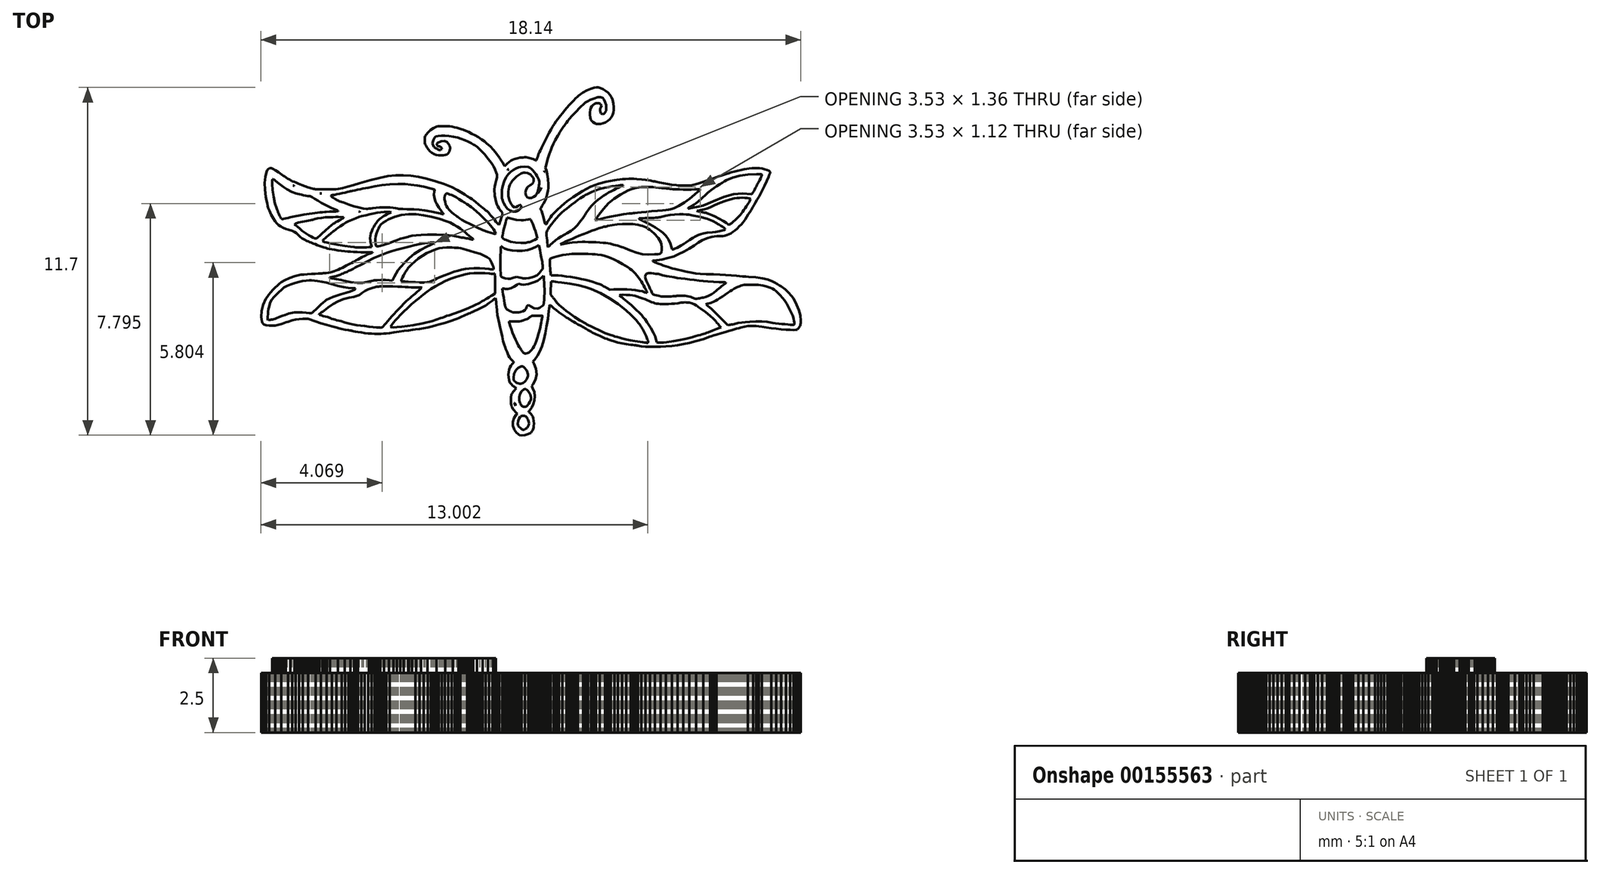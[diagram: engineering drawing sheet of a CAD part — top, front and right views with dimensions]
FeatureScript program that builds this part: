
annotation { "Feature Type Name" : "Feature", "Feature Type Description" : "" }
export const myFeature = defineFeature(function(context is Context, id is Id, definition is map)
    precondition{}
    {
        {
            var Q0;
            Q0=qCreatedBy(makeId("Top.planeOp"),FACE);
            var sketch = newSketch(context, id + "F0", { "sketchPlane" : qUnion([Q0])});
            skLineSegment(sketch, "E0", {"start": v(-0.39, -5.84) * mm, "end": v(-0.43, -5.8) * mm});
            skLineSegment(sketch, "E1", {"start": v(-0.43, -5.8) * mm, "end": v(-0.48, -5.76) * mm});
            skLineSegment(sketch, "E2", {"start": v(-0.48, -5.76) * mm, "end": v(-0.52, -5.71) * mm});
            skLineSegment(sketch, "E3", {"start": v(-0.52, -5.71) * mm, "end": v(-0.56, -5.66) * mm});
            skLineSegment(sketch, "E4", {"start": v(-0.56, -5.66) * mm, "end": v(-0.6, -5.53) * mm});
            skLineSegment(sketch, "E5", {"start": v(-0.6, -5.53) * mm, "end": v(-0.6, -5.4) * mm});
            skLineSegment(sketch, "E6", {"start": v(-0.6, -5.4) * mm, "end": v(-0.57, -5.28) * mm});
            skLineSegment(sketch, "E7", {"start": v(-0.57, -5.28) * mm, "end": v(-0.5, -5.18) * mm});
            skLineSegment(sketch, "E8", {"start": v(-0.5, -5.18) * mm, "end": v(-0.45, -5.13) * mm});
            skLineSegment(sketch, "E9", {"start": v(-0.45, -5.13) * mm, "end": v(-0.5, -5.07) * mm});
            skLineSegment(sketch, "E10", {"start": v(-0.5, -5.07) * mm, "end": v(-0.56, -5.02) * mm});
            skLineSegment(sketch, "E11", {"start": v(-0.56, -5.02) * mm, "end": v(-0.6, -4.96) * mm});
            skLineSegment(sketch, "E12", {"start": v(-0.6, -4.96) * mm, "end": v(-0.63, -4.9) * mm});
            skLineSegment(sketch, "E13", {"start": v(-0.63, -4.9) * mm, "end": v(-0.65, -4.86) * mm});
            skLineSegment(sketch, "E14", {"start": v(-0.65, -4.86) * mm, "end": v(-0.66, -4.83) * mm});
            skLineSegment(sketch, "E15", {"start": v(-0.66, -4.83) * mm, "end": v(-0.66, -4.79) * mm});
            skLineSegment(sketch, "E16", {"start": v(-0.66, -4.79) * mm, "end": v(-0.66, -4.73) * mm});
            skLineSegment(sketch, "E17", {"start": v(-0.66, -4.73) * mm, "end": v(-0.67, -4.66) * mm});
            skLineSegment(sketch, "E18", {"start": v(-0.67, -4.66) * mm, "end": v(-0.66, -4.61) * mm});
            skLineSegment(sketch, "E19", {"start": v(-0.66, -4.61) * mm, "end": v(-0.66, -4.57) * mm});
            skLineSegment(sketch, "E20", {"start": v(-0.66, -4.57) * mm, "end": v(-0.66, -4.54) * mm});
            skLineSegment(sketch, "E21", {"start": v(-0.66, -4.54) * mm, "end": v(-0.66, -4.52) * mm});
            skLineSegment(sketch, "E22", {"start": v(-0.66, -4.52) * mm, "end": v(-0.66, -4.5) * mm});
            skLineSegment(sketch, "E23", {"start": v(-0.66, -4.5) * mm, "end": v(-0.65, -4.48) * mm});
            skLineSegment(sketch, "E24", {"start": v(-0.65, -4.48) * mm, "end": v(-0.64, -4.47) * mm});
            skLineSegment(sketch, "E25", {"start": v(-0.64, -4.47) * mm, "end": v(-0.63, -4.45) * mm});
            skLineSegment(sketch, "E26", {"start": v(-0.63, -4.45) * mm, "end": v(-0.62, -4.42) * mm});
            skLineSegment(sketch, "E27", {"start": v(-0.62, -4.42) * mm, "end": v(-0.6, -4.39) * mm});
            skLineSegment(sketch, "E28", {"start": v(-0.6, -4.39) * mm, "end": v(-0.57, -4.36) * mm});
            skLineSegment(sketch, "E29", {"start": v(-0.57, -4.36) * mm, "end": v(-0.55, -4.33) * mm});
            skLineSegment(sketch, "E30", {"start": v(-0.55, -4.33) * mm, "end": v(-0.53, -4.3) * mm});
            skLineSegment(sketch, "E31", {"start": v(-0.53, -4.3) * mm, "end": v(-0.5, -4.3) * mm});
            skLineSegment(sketch, "E32", {"start": v(-0.5, -4.3) * mm, "end": v(-0.5, -4.28) * mm});
            skLineSegment(sketch, "E33", {"start": v(-0.5, -4.28) * mm, "end": v(-0.5, -4.27) * mm});
            skLineSegment(sketch, "E34", {"start": v(-0.5, -4.27) * mm, "end": v(-0.5, -4.26) * mm});
            skLineSegment(sketch, "E35", {"start": v(-0.5, -4.26) * mm, "end": v(-0.53, -4.24) * mm});
            skLineSegment(sketch, "E36", {"start": v(-0.53, -4.24) * mm, "end": v(-0.55, -4.22) * mm});
            skLineSegment(sketch, "E37", {"start": v(-0.55, -4.22) * mm, "end": v(-0.58, -4.2) * mm});
            skLineSegment(sketch, "E38", {"start": v(-0.58, -4.2) * mm, "end": v(-0.61, -4.17) * mm});
            skLineSegment(sketch, "E39", {"start": v(-0.61, -4.17) * mm, "end": v(-0.64, -4.15) * mm});
            skLineSegment(sketch, "E40", {"start": v(-0.64, -4.15) * mm, "end": v(-0.68, -4.1) * mm});
            skLineSegment(sketch, "E41", {"start": v(-0.68, -4.1) * mm, "end": v(-0.7, -4.08) * mm});
            skLineSegment(sketch, "E42", {"start": v(-0.7, -4.08) * mm, "end": v(-0.72, -4.04) * mm});
            skLineSegment(sketch, "E43", {"start": v(-0.72, -4.04) * mm, "end": v(-0.74, -4) * mm});
            skLineSegment(sketch, "E44", {"start": v(-0.74, -4) * mm, "end": v(-0.76, -3.81) * mm});
            skLineSegment(sketch, "E45", {"start": v(-0.76, -3.81) * mm, "end": v(-0.73, -3.65) * mm});
            skLineSegment(sketch, "E46", {"start": v(-0.73, -3.65) * mm, "end": v(-0.7, -3.58) * mm});
            skLineSegment(sketch, "E47", {"start": v(-0.7, -3.58) * mm, "end": v(-0.67, -3.51) * mm});
            skLineSegment(sketch, "E48", {"start": v(-0.67, -3.51) * mm, "end": v(-0.63, -3.46) * mm});
            skLineSegment(sketch, "E49", {"start": v(-0.63, -3.46) * mm, "end": v(-0.6, -3.43) * mm});
            skLineSegment(sketch, "E50", {"start": v(-0.6, -3.43) * mm, "end": v(-0.58, -3.4) * mm});
            skLineSegment(sketch, "E51", {"start": v(-0.58, -3.4) * mm, "end": v(-0.57, -3.4) * mm});
            skLineSegment(sketch, "E52", {"start": v(-0.57, -3.4) * mm, "end": v(-0.59, -3.37) * mm});
            skLineSegment(sketch, "E53", {"start": v(-0.59, -3.37) * mm, "end": v(-0.62, -3.34) * mm});
            skLineSegment(sketch, "E54", {"start": v(-0.62, -3.34) * mm, "end": v(-0.67, -3.3) * mm});
            skLineSegment(sketch, "E55", {"start": v(-0.67, -3.3) * mm, "end": v(-0.71, -3.23) * mm});
            skLineSegment(sketch, "E56", {"start": v(-0.71, -3.23) * mm, "end": v(-0.75, -3.16) * mm});
            skLineSegment(sketch, "E57", {"start": v(-0.75, -3.16) * mm, "end": v(-0.79, -3.1) * mm});
            skLineSegment(sketch, "E58", {"start": v(-0.79, -3.1) * mm, "end": v(-0.8, -3.05) * mm});
            skLineSegment(sketch, "E59", {"start": v(-0.8, -3.05) * mm, "end": v(-0.82, -3) * mm});
            skLineSegment(sketch, "E60", {"start": v(-0.82, -3) * mm, "end": v(-0.84, -2.95) * mm});
            skLineSegment(sketch, "E61", {"start": v(-0.84, -2.95) * mm, "end": v(-0.86, -2.9) * mm});
            skLineSegment(sketch, "E62", {"start": v(-0.86, -2.9) * mm, "end": v(-0.9, -2.8) * mm});
            skLineSegment(sketch, "E63", {"start": v(-0.9, -2.8) * mm, "end": v(-0.93, -2.68) * mm});
            skLineSegment(sketch, "E64", {"start": v(-0.93, -2.68) * mm, "end": v(-0.96, -2.54) * mm});
            skLineSegment(sketch, "E65", {"start": v(-0.96, -2.54) * mm, "end": v(-1, -2.36) * mm});
            skLineSegment(sketch, "E66", {"start": v(-1, -2.36) * mm, "end": v(-1.03, -2.21) * mm});
            skLineSegment(sketch, "E67", {"start": v(-1.03, -2.21) * mm, "end": v(-1.06, -2.08) * mm});
            skLineSegment(sketch, "E68", {"start": v(-1.06, -2.08) * mm, "end": v(-1.12, -1.8) * mm});
            skLineSegment(sketch, "E69", {"start": v(-1.12, -1.8) * mm, "end": v(-1.15, -1.51) * mm});
            skLineSegment(sketch, "E70", {"start": v(-1.15, -1.51) * mm, "end": v(-1.16, -1.44) * mm});
            skLineSegment(sketch, "E71", {"start": v(-1.16, -1.44) * mm, "end": v(-1.17, -1.37) * mm});
            skLineSegment(sketch, "E72", {"start": v(-1.17, -1.37) * mm, "end": v(-1.17, -1.31) * mm});
            skLineSegment(sketch, "E73", {"start": v(-1.17, -1.31) * mm, "end": v(-1.18, -1.28) * mm});
            skLineSegment(sketch, "E74", {"start": v(-1.18, -1.28) * mm, "end": v(-1.18, -1.23) * mm});
            skLineSegment(sketch, "E75", {"start": v(-1.18, -1.23) * mm, "end": v(-1.22, -1.26) * mm});
            skLineSegment(sketch, "E76", {"start": v(-1.22, -1.26) * mm, "end": v(-1.3, -1.32) * mm});
            skLineSegment(sketch, "E77", {"start": v(-1.3, -1.32) * mm, "end": v(-1.4, -1.4) * mm});
            skLineSegment(sketch, "E78", {"start": v(-1.4, -1.4) * mm, "end": v(-1.52, -1.48) * mm});
            skLineSegment(sketch, "E79", {"start": v(-1.52, -1.48) * mm, "end": v(-1.62, -1.54) * mm});
            skLineSegment(sketch, "E80", {"start": v(-1.62, -1.54) * mm, "end": v(-1.67, -1.57) * mm});
            skLineSegment(sketch, "E81", {"start": v(-1.67, -1.57) * mm, "end": v(-1.72, -1.6) * mm});
            skLineSegment(sketch, "E82", {"start": v(-1.72, -1.6) * mm, "end": v(-1.77, -1.62) * mm});
            skLineSegment(sketch, "E83", {"start": v(-1.77, -1.62) * mm, "end": v(-1.82, -1.64) * mm});
            skLineSegment(sketch, "E84", {"start": v(-1.82, -1.64) * mm, "end": v(-1.87, -1.66) * mm});
            skLineSegment(sketch, "E85", {"start": v(-1.87, -1.66) * mm, "end": v(-1.91, -1.68) * mm});
            skLineSegment(sketch, "E86", {"start": v(-1.91, -1.68) * mm, "end": v(-1.96, -1.7) * mm});
            skLineSegment(sketch, "E87", {"start": v(-1.96, -1.7) * mm, "end": v(-2, -1.72) * mm});
            skLineSegment(sketch, "E88", {"start": v(-2, -1.72) * mm, "end": v(-2.04, -1.74) * mm});
            skLineSegment(sketch, "E89", {"start": v(-2.04, -1.74) * mm, "end": v(-2.09, -1.76) * mm});
            skLineSegment(sketch, "E90", {"start": v(-2.09, -1.76) * mm, "end": v(-2.14, -1.79) * mm});
            skLineSegment(sketch, "E91", {"start": v(-2.14, -1.79) * mm, "end": v(-2.2, -1.8) * mm});
            skLineSegment(sketch, "E92", {"start": v(-2.2, -1.8) * mm, "end": v(-2.26, -1.83) * mm});
            skLineSegment(sketch, "E93", {"start": v(-2.26, -1.83) * mm, "end": v(-2.32, -1.86) * mm});
            skLineSegment(sketch, "E94", {"start": v(-2.32, -1.86) * mm, "end": v(-2.37, -1.88) * mm});
            skLineSegment(sketch, "E95", {"start": v(-2.37, -1.88) * mm, "end": v(-2.42, -1.9) * mm});
            skLineSegment(sketch, "E96", {"start": v(-2.42, -1.9) * mm, "end": v(-2.48, -1.93) * mm});
            skLineSegment(sketch, "E97", {"start": v(-2.48, -1.93) * mm, "end": v(-2.56, -1.96) * mm});
            skLineSegment(sketch, "E98", {"start": v(-2.56, -1.96) * mm, "end": v(-2.67, -2) * mm});
            skLineSegment(sketch, "E99", {"start": v(-2.67, -2) * mm, "end": v(-2.78, -2.03) * mm});
            skLineSegment(sketch, "E100", {"start": v(-2.78, -2.03) * mm, "end": v(-2.89, -2.07) * mm});
            skLineSegment(sketch, "E101", {"start": v(-2.89, -2.07) * mm, "end": v(-3, -2.1) * mm});
            skLineSegment(sketch, "E102", {"start": v(-3, -2.1) * mm, "end": v(-3.1, -2.13) * mm});
            skLineSegment(sketch, "E103", {"start": v(-3.1, -2.13) * mm, "end": v(-3.18, -2.15) * mm});
            skLineSegment(sketch, "E104", {"start": v(-3.18, -2.15) * mm, "end": v(-3.22, -2.16) * mm});
            skLineSegment(sketch, "E105", {"start": v(-3.22, -2.16) * mm, "end": v(-3.27, -2.17) * mm});
            skLineSegment(sketch, "E106", {"start": v(-3.27, -2.17) * mm, "end": v(-3.31, -2.18) * mm});
            skLineSegment(sketch, "E107", {"start": v(-3.31, -2.18) * mm, "end": v(-3.35, -2.2) * mm});
            skLineSegment(sketch, "E108", {"start": v(-3.35, -2.2) * mm, "end": v(-3.46, -2.22) * mm});
            skLineSegment(sketch, "E109", {"start": v(-3.46, -2.22) * mm, "end": v(-3.6, -2.25) * mm});
            skLineSegment(sketch, "E110", {"start": v(-3.6, -2.25) * mm, "end": v(-3.74, -2.27) * mm});
            skLineSegment(sketch, "E111", {"start": v(-3.74, -2.27) * mm, "end": v(-3.88, -2.3) * mm});
            skLineSegment(sketch, "E112", {"start": v(-3.88, -2.3) * mm, "end": v(-3.97, -2.3) * mm});
            skLineSegment(sketch, "E113", {"start": v(-3.97, -2.3) * mm, "end": v(-4.1, -2.32) * mm});
            skLineSegment(sketch, "E114", {"start": v(-4.1, -2.32) * mm, "end": v(-4.26, -2.34) * mm});
            skLineSegment(sketch, "E115", {"start": v(-4.26, -2.34) * mm, "end": v(-4.43, -2.37) * mm});
            skLineSegment(sketch, "E116", {"start": v(-4.43, -2.37) * mm, "end": v(-4.6, -2.4) * mm});
            skLineSegment(sketch, "E117", {"start": v(-4.6, -2.4) * mm, "end": v(-4.74, -2.4) * mm});
            skLineSegment(sketch, "E118", {"start": v(-4.74, -2.4) * mm, "end": v(-4.86, -2.42) * mm});
            skLineSegment(sketch, "E119", {"start": v(-4.86, -2.42) * mm, "end": v(-4.95, -2.43) * mm});
            skLineSegment(sketch, "E120", {"start": v(-4.95, -2.43) * mm, "end": v(-5.03, -2.44) * mm});
            skLineSegment(sketch, "E121", {"start": v(-5.03, -2.44) * mm, "end": v(-5.1, -2.44) * mm});
            skLineSegment(sketch, "E122", {"start": v(-5.1, -2.44) * mm, "end": v(-5.18, -2.44) * mm});
            skLineSegment(sketch, "E123", {"start": v(-5.18, -2.44) * mm, "end": v(-5.25, -2.44) * mm});
            skLineSegment(sketch, "E124", {"start": v(-5.25, -2.44) * mm, "end": v(-5.35, -2.43) * mm});
            skLineSegment(sketch, "E125", {"start": v(-5.35, -2.43) * mm, "end": v(-5.46, -2.42) * mm});
            skLineSegment(sketch, "E126", {"start": v(-5.46, -2.42) * mm, "end": v(-5.58, -2.4) * mm});
            skLineSegment(sketch, "E127", {"start": v(-5.58, -2.4) * mm, "end": v(-5.7, -2.4) * mm});
            skLineSegment(sketch, "E128", {"start": v(-5.7, -2.4) * mm, "end": v(-5.8, -2.38) * mm});
            skLineSegment(sketch, "E129", {"start": v(-5.8, -2.38) * mm, "end": v(-5.9, -2.36) * mm});
            skLineSegment(sketch, "E130", {"start": v(-5.9, -2.36) * mm, "end": v(-5.97, -2.35) * mm});
            skLineSegment(sketch, "E131", {"start": v(-5.97, -2.35) * mm, "end": v(-6, -2.34) * mm});
            skLineSegment(sketch, "E132", {"start": v(-6, -2.34) * mm, "end": v(-6.02, -2.34) * mm});
            skLineSegment(sketch, "E133", {"start": v(-6.02, -2.34) * mm, "end": v(-6.04, -2.33) * mm});
            skLineSegment(sketch, "E134", {"start": v(-6.04, -2.33) * mm, "end": v(-6.08, -2.32) * mm});
            skLineSegment(sketch, "E135", {"start": v(-6.08, -2.32) * mm, "end": v(-6.13, -2.32) * mm});
            skLineSegment(sketch, "E136", {"start": v(-6.13, -2.32) * mm, "end": v(-6.24, -2.3) * mm});
            skLineSegment(sketch, "E137", {"start": v(-6.24, -2.3) * mm, "end": v(-6.35, -2.27) * mm});
            skLineSegment(sketch, "E138", {"start": v(-6.35, -2.27) * mm, "end": v(-6.4, -2.26) * mm});
            skLineSegment(sketch, "E139", {"start": v(-6.4, -2.26) * mm, "end": v(-6.45, -2.25) * mm});
            skLineSegment(sketch, "E140", {"start": v(-6.45, -2.25) * mm, "end": v(-6.5, -2.23) * mm});
            skLineSegment(sketch, "E141", {"start": v(-6.5, -2.23) * mm, "end": v(-6.53, -2.23) * mm});
            skLineSegment(sketch, "E142", {"start": v(-6.53, -2.23) * mm, "end": v(-6.7, -2.19) * mm});
            skLineSegment(sketch, "E143", {"start": v(-6.7, -2.19) * mm, "end": v(-6.87, -2.14) * mm});
            skLineSegment(sketch, "E144", {"start": v(-6.87, -2.14) * mm, "end": v(-7.06, -2.08) * mm});
            skLineSegment(sketch, "E145", {"start": v(-7.06, -2.08) * mm, "end": v(-7.24, -2.02) * mm});
            skLineSegment(sketch, "E146", {"start": v(-7.24, -2.02) * mm, "end": v(-7.49, -1.94) * mm});
            skLineSegment(sketch, "E147", {"start": v(-7.49, -1.94) * mm, "end": v(-7.66, -1.94) * mm});
            skLineSegment(sketch, "E148", {"start": v(-7.66, -1.94) * mm, "end": v(-7.8, -1.94) * mm});
            skLineSegment(sketch, "E149", {"start": v(-7.8, -1.94) * mm, "end": v(-7.9, -1.96) * mm});
            skLineSegment(sketch, "E150", {"start": v(-7.9, -1.96) * mm, "end": v(-8.02, -1.98) * mm});
            skLineSegment(sketch, "E151", {"start": v(-8.02, -1.98) * mm, "end": v(-8.17, -2.03) * mm});
            skLineSegment(sketch, "E152", {"start": v(-8.17, -2.03) * mm, "end": v(-8.23, -2.05) * mm});
            skLineSegment(sketch, "E153", {"start": v(-8.23, -2.05) * mm, "end": v(-8.29, -2.07) * mm});
            skLineSegment(sketch, "E154", {"start": v(-8.29, -2.07) * mm, "end": v(-8.35, -2.1) * mm});
            skLineSegment(sketch, "E155", {"start": v(-8.35, -2.1) * mm, "end": v(-8.39, -2.1) * mm});
            skLineSegment(sketch, "E156", {"start": v(-8.39, -2.1) * mm, "end": v(-8.6, -2.16) * mm});
            skLineSegment(sketch, "E157", {"start": v(-8.6, -2.16) * mm, "end": v(-8.8, -2.16) * mm});
            skLineSegment(sketch, "E158", {"start": v(-8.8, -2.16) * mm, "end": v(-8.9, -2.15) * mm});
            skLineSegment(sketch, "E159", {"start": v(-8.9, -2.15) * mm, "end": v(-8.97, -2.12) * mm});
            skLineSegment(sketch, "E160", {"start": v(-8.97, -2.12) * mm, "end": v(-9, -2.09) * mm});
            skLineSegment(sketch, "E161", {"start": v(-9, -2.09) * mm, "end": v(-9.04, -2.04) * mm});
            skLineSegment(sketch, "E162", {"start": v(-9.04, -2.04) * mm, "end": v(-9.07, -1.87) * mm});
            skLineSegment(sketch, "E163", {"start": v(-9.07, -1.87) * mm, "end": v(-9.05, -1.67) * mm});
            skLineSegment(sketch, "E164", {"start": v(-9.05, -1.67) * mm, "end": v(-9, -1.46) * mm});
            skLineSegment(sketch, "E165", {"start": v(-9, -1.46) * mm, "end": v(-8.9, -1.26) * mm});
            skLineSegment(sketch, "E166", {"start": v(-8.9, -1.26) * mm, "end": v(-8.86, -1.2) * mm});
            skLineSegment(sketch, "E167", {"start": v(-8.86, -1.2) * mm, "end": v(-8.8, -1.12) * mm});
            skLineSegment(sketch, "E168", {"start": v(-8.8, -1.12) * mm, "end": v(-8.74, -1.04) * mm});
            skLineSegment(sketch, "E169", {"start": v(-8.74, -1.04) * mm, "end": v(-8.67, -0.96) * mm});
            skLineSegment(sketch, "E170", {"start": v(-8.67, -0.96) * mm, "end": v(-8.6, -0.88) * mm});
            skLineSegment(sketch, "E171", {"start": v(-8.6, -0.88) * mm, "end": v(-8.52, -0.8) * mm});
            skLineSegment(sketch, "E172", {"start": v(-8.52, -0.8) * mm, "end": v(-8.45, -0.75) * mm});
            skLineSegment(sketch, "E173", {"start": v(-8.45, -0.75) * mm, "end": v(-8.4, -0.7) * mm});
            skLineSegment(sketch, "E174", {"start": v(-8.4, -0.7) * mm, "end": v(-8.27, -0.64) * mm});
            skLineSegment(sketch, "E175", {"start": v(-8.27, -0.64) * mm, "end": v(-8.1, -0.56) * mm});
            skLineSegment(sketch, "E176", {"start": v(-8.1, -0.56) * mm, "end": v(-7.94, -0.5) * mm});
            skLineSegment(sketch, "E177", {"start": v(-7.94, -0.5) * mm, "end": v(-7.78, -0.46) * mm});
            skLineSegment(sketch, "E178", {"start": v(-7.78, -0.46) * mm, "end": v(-7.72, -0.45) * mm});
            skLineSegment(sketch, "E179", {"start": v(-7.72, -0.45) * mm, "end": v(-7.63, -0.44) * mm});
            skLineSegment(sketch, "E180", {"start": v(-7.63, -0.44) * mm, "end": v(-7.51, -0.43) * mm});
            skLineSegment(sketch, "E181", {"start": v(-7.51, -0.43) * mm, "end": v(-7.38, -0.43) * mm});
            skLineSegment(sketch, "E182", {"start": v(-7.38, -0.43) * mm, "end": v(-7.25, -0.42) * mm});
            skLineSegment(sketch, "E183", {"start": v(-7.25, -0.42) * mm, "end": v(-7.14, -0.41) * mm});
            skLineSegment(sketch, "E184", {"start": v(-7.14, -0.41) * mm, "end": v(-7.07, -0.4) * mm});
            skLineSegment(sketch, "E185", {"start": v(-7.07, -0.4) * mm, "end": v(-7.04, -0.4) * mm});
            skLineSegment(sketch, "E186", {"start": v(-7.04, -0.4) * mm, "end": v(-7.02, -0.4) * mm});
            skLineSegment(sketch, "E187", {"start": v(-7.02, -0.4) * mm, "end": v(-6.98, -0.4) * mm});
            skLineSegment(sketch, "E188", {"start": v(-6.98, -0.4) * mm, "end": v(-6.94, -0.4) * mm});
            skLineSegment(sketch, "E189", {"start": v(-6.94, -0.4) * mm, "end": v(-6.88, -0.39) * mm});
            skLineSegment(sketch, "E190", {"start": v(-6.88, -0.39) * mm, "end": v(-6.8, -0.38) * mm});
            skLineSegment(sketch, "E191", {"start": v(-6.8, -0.38) * mm, "end": v(-6.74, -0.37) * mm});
            skLineSegment(sketch, "E192", {"start": v(-6.74, -0.37) * mm, "end": v(-6.68, -0.36) * mm});
            skLineSegment(sketch, "E193", {"start": v(-6.68, -0.36) * mm, "end": v(-6.6, -0.33) * mm});
            skLineSegment(sketch, "E194", {"start": v(-6.6, -0.33) * mm, "end": v(-6.55, -0.3) * mm});
            skLineSegment(sketch, "E195", {"start": v(-6.55, -0.3) * mm, "end": v(-6.47, -0.28) * mm});
            skLineSegment(sketch, "E196", {"start": v(-6.47, -0.28) * mm, "end": v(-6.4, -0.25) * mm});
            skLineSegment(sketch, "E197", {"start": v(-6.4, -0.25) * mm, "end": v(-6.34, -0.21) * mm});
            skLineSegment(sketch, "E198", {"start": v(-6.34, -0.21) * mm, "end": v(-6.27, -0.18) * mm});
            skLineSegment(sketch, "E199", {"start": v(-6.27, -0.18) * mm, "end": v(-6.2, -0.14) * mm});
            skLineSegment(sketch, "E200", {"start": v(-6.2, -0.14) * mm, "end": v(-6.13, -0.1) * mm});
            skLineSegment(sketch, "E201", {"start": v(-6.13, -0.1) * mm, "end": v(-6.08, -0.08) * mm});
            skLineSegment(sketch, "E202", {"start": v(-6.08, -0.08) * mm, "end": v(-6.02, -0.05) * mm});
            skLineSegment(sketch, "E203", {"start": v(-6.02, -0.05) * mm, "end": v(-5.95, 0) * mm});
            skLineSegment(sketch, "E204", {"start": v(-5.95, 0) * mm, "end": v(-5.88, 0.03) * mm});
            skLineSegment(sketch, "E205", {"start": v(-5.88, 0.03) * mm, "end": v(-5.8, 0.07) * mm});
            skLineSegment(sketch, "E206", {"start": v(-5.8, 0.07) * mm, "end": v(-5.69, 0.13) * mm});
            skLineSegment(sketch, "E207", {"start": v(-5.69, 0.13) * mm, "end": v(-5.58, 0.19) * mm});
            skLineSegment(sketch, "E208", {"start": v(-5.58, 0.19) * mm, "end": v(-5.48, 0.23) * mm});
            skLineSegment(sketch, "E209", {"start": v(-5.48, 0.23) * mm, "end": v(-5.4, 0.27) * mm});
            skLineSegment(sketch, "E210", {"start": v(-5.4, 0.27) * mm, "end": v(-5.36, 0.28) * mm});
            skLineSegment(sketch, "E211", {"start": v(-5.36, 0.28) * mm, "end": v(-5.34, 0.29) * mm});
            skLineSegment(sketch, "E212", {"start": v(-5.34, 0.29) * mm, "end": v(-5.32, 0.3) * mm});
            skLineSegment(sketch, "E213", {"start": v(-5.32, 0.3) * mm, "end": v(-5.32, 0.3) * mm});
            skLineSegment(sketch, "E214", {"start": v(-5.32, 0.3) * mm, "end": v(-5.34, 0.3) * mm});
            skLineSegment(sketch, "E215", {"start": v(-5.34, 0.3) * mm, "end": v(-5.4, 0.3) * mm});
            skLineSegment(sketch, "E216", {"start": v(-5.4, 0.3) * mm, "end": v(-5.48, 0.3) * mm});
            skLineSegment(sketch, "E217", {"start": v(-5.48, 0.3) * mm, "end": v(-5.6, 0.3) * mm});
            skLineSegment(sketch, "E218", {"start": v(-5.6, 0.3) * mm, "end": v(-5.71, 0.3) * mm});
            skLineSegment(sketch, "E219", {"start": v(-5.71, 0.3) * mm, "end": v(-5.84, 0.31) * mm});
            skLineSegment(sketch, "E220", {"start": v(-5.84, 0.31) * mm, "end": v(-5.96, 0.32) * mm});
            skLineSegment(sketch, "E221", {"start": v(-5.96, 0.32) * mm, "end": v(-6.06, 0.32) * mm});
            skLineSegment(sketch, "E222", {"start": v(-6.06, 0.32) * mm, "end": v(-6.15, 0.33) * mm});
            skLineSegment(sketch, "E223", {"start": v(-6.15, 0.33) * mm, "end": v(-6.26, 0.34) * mm});
            skLineSegment(sketch, "E224", {"start": v(-6.26, 0.34) * mm, "end": v(-6.37, 0.35) * mm});
            skLineSegment(sketch, "E225", {"start": v(-6.37, 0.35) * mm, "end": v(-6.48, 0.37) * mm});
            skLineSegment(sketch, "E226", {"start": v(-6.48, 0.37) * mm, "end": v(-6.6, 0.39) * mm});
            skLineSegment(sketch, "E227", {"start": v(-6.6, 0.39) * mm, "end": v(-6.7, 0.4) * mm});
            skLineSegment(sketch, "E228", {"start": v(-6.7, 0.4) * mm, "end": v(-6.78, 0.42) * mm});
            skLineSegment(sketch, "E229", {"start": v(-6.78, 0.42) * mm, "end": v(-6.84, 0.43) * mm});
            skLineSegment(sketch, "E230", {"start": v(-6.84, 0.43) * mm, "end": v(-6.89, 0.45) * mm});
            skLineSegment(sketch, "E231", {"start": v(-6.89, 0.45) * mm, "end": v(-6.95, 0.47) * mm});
            skLineSegment(sketch, "E232", {"start": v(-6.95, 0.47) * mm, "end": v(-7.03, 0.5) * mm});
            skLineSegment(sketch, "E233", {"start": v(-7.03, 0.5) * mm, "end": v(-7.1, 0.52) * mm});
            skLineSegment(sketch, "E234", {"start": v(-7.1, 0.52) * mm, "end": v(-7.18, 0.55) * mm});
            skLineSegment(sketch, "E235", {"start": v(-7.18, 0.55) * mm, "end": v(-7.25, 0.58) * mm});
            skLineSegment(sketch, "E236", {"start": v(-7.25, 0.58) * mm, "end": v(-7.31, 0.6) * mm});
            skLineSegment(sketch, "E237", {"start": v(-7.31, 0.6) * mm, "end": v(-7.35, 0.62) * mm});
            skLineSegment(sketch, "E238", {"start": v(-7.35, 0.62) * mm, "end": v(-7.39, 0.63) * mm});
            skLineSegment(sketch, "E239", {"start": v(-7.39, 0.63) * mm, "end": v(-7.43, 0.65) * mm});
            skLineSegment(sketch, "E240", {"start": v(-7.43, 0.65) * mm, "end": v(-7.48, 0.67) * mm});
            skLineSegment(sketch, "E241", {"start": v(-7.48, 0.67) * mm, "end": v(-7.52, 0.69) * mm});
            skLineSegment(sketch, "E242", {"start": v(-7.52, 0.69) * mm, "end": v(-7.61, 0.73) * mm});
            skLineSegment(sketch, "E243", {"start": v(-7.61, 0.73) * mm, "end": v(-7.68, 0.77) * mm});
            skLineSegment(sketch, "E244", {"start": v(-7.68, 0.77) * mm, "end": v(-7.75, 0.82) * mm});
            skLineSegment(sketch, "E245", {"start": v(-7.75, 0.82) * mm, "end": v(-7.81, 0.88) * mm});
            skLineSegment(sketch, "E246", {"start": v(-7.81, 0.88) * mm, "end": v(-7.88, 0.95) * mm});
            skLineSegment(sketch, "E247", {"start": v(-7.88, 0.95) * mm, "end": v(-7.94, 0.99) * mm});
            skLineSegment(sketch, "E248", {"start": v(-7.94, 0.99) * mm, "end": v(-8.02, 1.02) * mm});
            skLineSegment(sketch, "E249", {"start": v(-8.02, 1.02) * mm, "end": v(-8.14, 1.06) * mm});
            skLineSegment(sketch, "E250", {"start": v(-8.14, 1.06) * mm, "end": v(-8.24, 1.1) * mm});
            skLineSegment(sketch, "E251", {"start": v(-8.24, 1.1) * mm, "end": v(-8.33, 1.13) * mm});
            skLineSegment(sketch, "E252", {"start": v(-8.33, 1.13) * mm, "end": v(-8.41, 1.18) * mm});
            skLineSegment(sketch, "E253", {"start": v(-8.41, 1.18) * mm, "end": v(-8.48, 1.22) * mm});
            skLineSegment(sketch, "E254", {"start": v(-8.48, 1.22) * mm, "end": v(-8.54, 1.28) * mm});
            skLineSegment(sketch, "E255", {"start": v(-8.54, 1.28) * mm, "end": v(-8.6, 1.35) * mm});
            skLineSegment(sketch, "E256", {"start": v(-8.6, 1.35) * mm, "end": v(-8.66, 1.45) * mm});
            skLineSegment(sketch, "E257", {"start": v(-8.66, 1.45) * mm, "end": v(-8.73, 1.57) * mm});
            skLineSegment(sketch, "E258", {"start": v(-8.73, 1.57) * mm, "end": v(-8.76, 1.64) * mm});
            skLineSegment(sketch, "E259", {"start": v(-8.76, 1.64) * mm, "end": v(-8.79, 1.7) * mm});
            skLineSegment(sketch, "E260", {"start": v(-8.79, 1.7) * mm, "end": v(-8.8, 1.75) * mm});
            skLineSegment(sketch, "E261", {"start": v(-8.8, 1.75) * mm, "end": v(-8.83, 1.8) * mm});
            skLineSegment(sketch, "E262", {"start": v(-8.83, 1.8) * mm, "end": v(-8.84, 1.87) * mm});
            skLineSegment(sketch, "E263", {"start": v(-8.84, 1.87) * mm, "end": v(-8.86, 1.95) * mm});
            skLineSegment(sketch, "E264", {"start": v(-8.86, 1.95) * mm, "end": v(-8.88, 2.05) * mm});
            skLineSegment(sketch, "E265", {"start": v(-8.88, 2.05) * mm, "end": v(-8.9, 2.17) * mm});
            skLineSegment(sketch, "E266", {"start": v(-8.9, 2.17) * mm, "end": v(-8.94, 2.41) * mm});
            skLineSegment(sketch, "E267", {"start": v(-8.94, 2.41) * mm, "end": v(-8.95, 2.64) * mm});
            skLineSegment(sketch, "E268", {"start": v(-8.95, 2.64) * mm, "end": v(-8.93, 2.84) * mm});
            skLineSegment(sketch, "E269", {"start": v(-8.93, 2.84) * mm, "end": v(-8.89, 3) * mm});
            skLineSegment(sketch, "E270", {"start": v(-8.89, 3) * mm, "end": v(-8.85, 3.07) * mm});
            skLineSegment(sketch, "E271", {"start": v(-8.85, 3.07) * mm, "end": v(-8.82, 3.11) * mm});
            skLineSegment(sketch, "E272", {"start": v(-8.82, 3.11) * mm, "end": v(-8.78, 3.13) * mm});
            skLineSegment(sketch, "E273", {"start": v(-8.78, 3.13) * mm, "end": v(-8.72, 3.13) * mm});
            skLineSegment(sketch, "E274", {"start": v(-8.72, 3.13) * mm, "end": v(-8.67, 3.1) * mm});
            skLineSegment(sketch, "E275", {"start": v(-8.67, 3.1) * mm, "end": v(-8.59, 3.06) * mm});
            skLineSegment(sketch, "E276", {"start": v(-8.59, 3.06) * mm, "end": v(-8.48, 3) * mm});
            skLineSegment(sketch, "E277", {"start": v(-8.48, 3) * mm, "end": v(-8.37, 2.92) * mm});
            skLineSegment(sketch, "E278", {"start": v(-8.37, 2.92) * mm, "end": v(-8.33, 2.89) * mm});
            skLineSegment(sketch, "E279", {"start": v(-8.33, 2.89) * mm, "end": v(-8.28, 2.85) * mm});
            skLineSegment(sketch, "E280", {"start": v(-8.28, 2.85) * mm, "end": v(-8.22, 2.82) * mm});
            skLineSegment(sketch, "E281", {"start": v(-8.22, 2.82) * mm, "end": v(-8.17, 2.78) * mm});
            skLineSegment(sketch, "E282", {"start": v(-8.17, 2.78) * mm, "end": v(-8.12, 2.75) * mm});
            skLineSegment(sketch, "E283", {"start": v(-8.12, 2.75) * mm, "end": v(-8.07, 2.72) * mm});
            skLineSegment(sketch, "E284", {"start": v(-8.07, 2.72) * mm, "end": v(-8.04, 2.7) * mm});
            skLineSegment(sketch, "E285", {"start": v(-8.04, 2.7) * mm, "end": v(-8.02, 2.7) * mm});
            skLineSegment(sketch, "E286", {"start": v(-8.02, 2.7) * mm, "end": v(-8, 2.7) * mm});
            skLineSegment(sketch, "E287", {"start": v(-8, 2.7) * mm, "end": v(-7.96, 2.67) * mm});
            skLineSegment(sketch, "E288", {"start": v(-7.96, 2.67) * mm, "end": v(-7.9, 2.65) * mm});
            skLineSegment(sketch, "E289", {"start": v(-7.9, 2.65) * mm, "end": v(-7.82, 2.61) * mm});
            skLineSegment(sketch, "E290", {"start": v(-7.82, 2.61) * mm, "end": v(-7.7, 2.56) * mm});
            skLineSegment(sketch, "E291", {"start": v(-7.7, 2.56) * mm, "end": v(-7.6, 2.52) * mm});
            skLineSegment(sketch, "E292", {"start": v(-7.6, 2.52) * mm, "end": v(-7.49, 2.49) * mm});
            skLineSegment(sketch, "E293", {"start": v(-7.49, 2.49) * mm, "end": v(-7.35, 2.45) * mm});
            skLineSegment(sketch, "E294", {"start": v(-7.35, 2.45) * mm, "end": v(-7.3, 2.44) * mm});
            skLineSegment(sketch, "E295", {"start": v(-7.3, 2.44) * mm, "end": v(-7.28, 2.43) * mm});
            skLineSegment(sketch, "E296", {"start": v(-7.28, 2.43) * mm, "end": v(-7.24, 2.42) * mm});
            skLineSegment(sketch, "E297", {"start": v(-7.24, 2.42) * mm, "end": v(-7.2, 2.42) * mm});
            skLineSegment(sketch, "E298", {"start": v(-7.2, 2.42) * mm, "end": v(-7.16, 2.42) * mm});
            skLineSegment(sketch, "E299", {"start": v(-7.16, 2.42) * mm, "end": v(-7.1, 2.42) * mm});
            skLineSegment(sketch, "E300", {"start": v(-7.1, 2.42) * mm, "end": v(-7.02, 2.42) * mm});
            skLineSegment(sketch, "E301", {"start": v(-7.02, 2.42) * mm, "end": v(-6.92, 2.42) * mm});
            skLineSegment(sketch, "E302", {"start": v(-6.92, 2.42) * mm, "end": v(-6.76, 2.42) * mm});
            skLineSegment(sketch, "E303", {"start": v(-6.76, 2.42) * mm, "end": v(-6.64, 2.42) * mm});
            skLineSegment(sketch, "E304", {"start": v(-6.64, 2.42) * mm, "end": v(-6.55, 2.43) * mm});
            skLineSegment(sketch, "E305", {"start": v(-6.55, 2.43) * mm, "end": v(-6.48, 2.44) * mm});
            skLineSegment(sketch, "E306", {"start": v(-6.48, 2.44) * mm, "end": v(-6.34, 2.46) * mm});
            skLineSegment(sketch, "E307", {"start": v(-6.34, 2.46) * mm, "end": v(-6.16, 2.5) * mm});
            skLineSegment(sketch, "E308", {"start": v(-6.16, 2.5) * mm, "end": v(-5.96, 2.56) * mm});
            skLineSegment(sketch, "E309", {"start": v(-5.96, 2.56) * mm, "end": v(-5.76, 2.62) * mm});
            skLineSegment(sketch, "E310", {"start": v(-5.76, 2.62) * mm, "end": v(-5.4, 2.73) * mm});
            skLineSegment(sketch, "E311", {"start": v(-5.4, 2.73) * mm, "end": v(-5.1, 2.8) * mm});
            skLineSegment(sketch, "E312", {"start": v(-5.1, 2.8) * mm, "end": v(-4.8, 2.86) * mm});
            skLineSegment(sketch, "E313", {"start": v(-4.8, 2.86) * mm, "end": v(-4.54, 2.9) * mm});
            skLineSegment(sketch, "E314", {"start": v(-4.54, 2.9) * mm, "end": v(-4.29, 2.9) * mm});
            skLineSegment(sketch, "E315", {"start": v(-4.29, 2.9) * mm, "end": v(-4.03, 2.88) * mm});
            skLineSegment(sketch, "E316", {"start": v(-4.03, 2.88) * mm, "end": v(-3.77, 2.84) * mm});
            skLineSegment(sketch, "E317", {"start": v(-3.77, 2.84) * mm, "end": v(-3.5, 2.78) * mm});
            skLineSegment(sketch, "E318", {"start": v(-3.5, 2.78) * mm, "end": v(-3.2, 2.7) * mm});
            skLineSegment(sketch, "E319", {"start": v(-3.2, 2.7) * mm, "end": v(-2.91, 2.6) * mm});
            skLineSegment(sketch, "E320", {"start": v(-2.91, 2.6) * mm, "end": v(-2.67, 2.5) * mm});
            skLineSegment(sketch, "E321", {"start": v(-2.67, 2.5) * mm, "end": v(-2.47, 2.4) * mm});
            skLineSegment(sketch, "E322", {"start": v(-2.47, 2.4) * mm, "end": v(-2.34, 2.32) * mm});
            skLineSegment(sketch, "E323", {"start": v(-2.34, 2.32) * mm, "end": v(-2.22, 2.25) * mm});
            skLineSegment(sketch, "E324", {"start": v(-2.22, 2.25) * mm, "end": v(-2.12, 2.19) * mm});
            skLineSegment(sketch, "E325", {"start": v(-2.12, 2.19) * mm, "end": v(-2.04, 2.14) * mm});
            skLineSegment(sketch, "E326", {"start": v(-2.04, 2.14) * mm, "end": v(-1.97, 2.09) * mm});
            skLineSegment(sketch, "E327", {"start": v(-1.97, 2.09) * mm, "end": v(-1.91, 2.04) * mm});
            skLineSegment(sketch, "E328", {"start": v(-1.91, 2.04) * mm, "end": v(-1.86, 2) * mm});
            skLineSegment(sketch, "E329", {"start": v(-1.86, 2) * mm, "end": v(-1.82, 1.97) * mm});
            skLineSegment(sketch, "E330", {"start": v(-1.82, 1.97) * mm, "end": v(-1.79, 1.94) * mm});
            skLineSegment(sketch, "E331", {"start": v(-1.79, 1.94) * mm, "end": v(-1.74, 1.9) * mm});
            skLineSegment(sketch, "E332", {"start": v(-1.74, 1.9) * mm, "end": v(-1.68, 1.85) * mm});
            skLineSegment(sketch, "E333", {"start": v(-1.68, 1.85) * mm, "end": v(-1.63, 1.8) * mm});
            skLineSegment(sketch, "E334", {"start": v(-1.63, 1.8) * mm, "end": v(-1.57, 1.76) * mm});
            skLineSegment(sketch, "E335", {"start": v(-1.57, 1.76) * mm, "end": v(-1.52, 1.72) * mm});
            skLineSegment(sketch, "E336", {"start": v(-1.52, 1.72) * mm, "end": v(-1.47, 1.68) * mm});
            skLineSegment(sketch, "E337", {"start": v(-1.47, 1.68) * mm, "end": v(-1.44, 1.66) * mm});
            skLineSegment(sketch, "E338", {"start": v(-1.44, 1.66) * mm, "end": v(-1.42, 1.63) * mm});
            skLineSegment(sketch, "E339", {"start": v(-1.42, 1.63) * mm, "end": v(-1.39, 1.6) * mm});
            skLineSegment(sketch, "E340", {"start": v(-1.39, 1.6) * mm, "end": v(-1.35, 1.55) * mm});
            skLineSegment(sketch, "E341", {"start": v(-1.35, 1.55) * mm, "end": v(-1.3, 1.5) * mm});
            skLineSegment(sketch, "E342", {"start": v(-1.3, 1.5) * mm, "end": v(-1.26, 1.44) * mm});
            skLineSegment(sketch, "E343", {"start": v(-1.26, 1.44) * mm, "end": v(-1.21, 1.39) * mm});
            skLineSegment(sketch, "E344", {"start": v(-1.21, 1.39) * mm, "end": v(-1.17, 1.34) * mm});
            skLineSegment(sketch, "E345", {"start": v(-1.17, 1.34) * mm, "end": v(-1.13, 1.3) * mm});
            skLineSegment(sketch, "E346", {"start": v(-1.13, 1.3) * mm, "end": v(-1.11, 1.26) * mm});
            skLineSegment(sketch, "E347", {"start": v(-1.11, 1.26) * mm, "end": v(-1.1, 1.24) * mm});
            skLineSegment(sketch, "E348", {"start": v(-1.1, 1.24) * mm, "end": v(-1.08, 1.23) * mm});
            skLineSegment(sketch, "E349", {"start": v(-1.08, 1.23) * mm, "end": v(-1.07, 1.23) * mm});
            skLineSegment(sketch, "E350", {"start": v(-1.07, 1.23) * mm, "end": v(-1.06, 1.25) * mm});
            skLineSegment(sketch, "E351", {"start": v(-1.06, 1.25) * mm, "end": v(-1.05, 1.28) * mm});
            skLineSegment(sketch, "E352", {"start": v(-1.05, 1.28) * mm, "end": v(-1.03, 1.33) * mm});
            skLineSegment(sketch, "E353", {"start": v(-1.03, 1.33) * mm, "end": v(-1.01, 1.4) * mm});
            skLineSegment(sketch, "E354", {"start": v(-1.01, 1.4) * mm, "end": v(-1, 1.45) * mm});
            skLineSegment(sketch, "E355", {"start": v(-1, 1.45) * mm, "end": v(-0.98, 1.51) * mm});
            skLineSegment(sketch, "E356", {"start": v(-0.98, 1.51) * mm, "end": v(-0.96, 1.56) * mm});
            skLineSegment(sketch, "E357", {"start": v(-0.96, 1.56) * mm, "end": v(-0.95, 1.6) * mm});
            skLineSegment(sketch, "E358", {"start": v(-0.95, 1.6) * mm, "end": v(-0.95, 1.61) * mm});
            skLineSegment(sketch, "E359", {"start": v(-0.95, 1.61) * mm, "end": v(-0.97, 1.64) * mm});
            skLineSegment(sketch, "E360", {"start": v(-0.97, 1.64) * mm, "end": v(-0.99, 1.67) * mm});
            skLineSegment(sketch, "E361", {"start": v(-0.99, 1.67) * mm, "end": v(-1.02, 1.72) * mm});
            skLineSegment(sketch, "E362", {"start": v(-1.02, 1.72) * mm, "end": v(-1.07, 1.79) * mm});
            skLineSegment(sketch, "E363", {"start": v(-1.07, 1.79) * mm, "end": v(-1.11, 1.85) * mm});
            skLineSegment(sketch, "E364", {"start": v(-1.11, 1.85) * mm, "end": v(-1.14, 1.9) * mm});
            skLineSegment(sketch, "E365", {"start": v(-1.14, 1.9) * mm, "end": v(-1.16, 1.98) * mm});
            skLineSegment(sketch, "E366", {"start": v(-1.16, 1.98) * mm, "end": v(-1.21, 2.2) * mm});
            skLineSegment(sketch, "E367", {"start": v(-1.21, 2.2) * mm, "end": v(-1.22, 2.42) * mm});
            skLineSegment(sketch, "E368", {"start": v(-1.22, 2.42) * mm, "end": v(-1.21, 2.51) * mm});
            skLineSegment(sketch, "E369", {"start": v(-1.21, 2.51) * mm, "end": v(-1.2, 2.62) * mm});
            skLineSegment(sketch, "E370", {"start": v(-1.2, 2.62) * mm, "end": v(-1.17, 2.73) * mm});
            skLineSegment(sketch, "E371", {"start": v(-1.17, 2.73) * mm, "end": v(-1.14, 2.82) * mm});
            skLineSegment(sketch, "E372", {"start": v(-1.14, 2.82) * mm, "end": v(-1.13, 2.85) * mm});
            skLineSegment(sketch, "E373", {"start": v(-1.13, 2.85) * mm, "end": v(-1.13, 2.88) * mm});
            skLineSegment(sketch, "E374", {"start": v(-1.13, 2.88) * mm, "end": v(-1.14, 2.92) * mm});
            skLineSegment(sketch, "E375", {"start": v(-1.14, 2.92) * mm, "end": v(-1.16, 2.98) * mm});
            skLineSegment(sketch, "E376", {"start": v(-1.16, 2.98) * mm, "end": v(-1.2, 3.09) * mm});
            skLineSegment(sketch, "E377", {"start": v(-1.2, 3.09) * mm, "end": v(-1.26, 3.2) * mm});
            skLineSegment(sketch, "E378", {"start": v(-1.26, 3.2) * mm, "end": v(-1.33, 3.31) * mm});
            skLineSegment(sketch, "E379", {"start": v(-1.33, 3.31) * mm, "end": v(-1.43, 3.44) * mm});
            skLineSegment(sketch, "E380", {"start": v(-1.43, 3.44) * mm, "end": v(-1.55, 3.6) * mm});
            skLineSegment(sketch, "E381", {"start": v(-1.55, 3.6) * mm, "end": v(-1.68, 3.74) * mm});
            skLineSegment(sketch, "E382", {"start": v(-1.68, 3.74) * mm, "end": v(-1.8, 3.84) * mm});
            skLineSegment(sketch, "E383", {"start": v(-1.8, 3.84) * mm, "end": v(-1.9, 3.91) * mm});
            skLineSegment(sketch, "E384", {"start": v(-1.9, 3.91) * mm, "end": v(-1.93, 3.93) * mm});
            skLineSegment(sketch, "E385", {"start": v(-1.93, 3.93) * mm, "end": v(-1.96, 3.95) * mm});
            skLineSegment(sketch, "E386", {"start": v(-1.96, 3.95) * mm, "end": v(-2, 3.97) * mm});
            skLineSegment(sketch, "E387", {"start": v(-2, 3.97) * mm, "end": v(-2.02, 3.99) * mm});
            skLineSegment(sketch, "E388", {"start": v(-2.02, 3.99) * mm, "end": v(-2.1, 4.03) * mm});
            skLineSegment(sketch, "E389", {"start": v(-2.1, 4.03) * mm, "end": v(-2.22, 4.08) * mm});
            skLineSegment(sketch, "E390", {"start": v(-2.22, 4.08) * mm, "end": v(-2.35, 4.13) * mm});
            skLineSegment(sketch, "E391", {"start": v(-2.35, 4.13) * mm, "end": v(-2.46, 4.16) * mm});
            skLineSegment(sketch, "E392", {"start": v(-2.46, 4.16) * mm, "end": v(-2.6, 4.2) * mm});
            skLineSegment(sketch, "E393", {"start": v(-2.6, 4.2) * mm, "end": v(-2.75, 4.22) * mm});
            skLineSegment(sketch, "E394", {"start": v(-2.75, 4.22) * mm, "end": v(-2.89, 4.23) * mm});
            skLineSegment(sketch, "E395", {"start": v(-2.89, 4.23) * mm, "end": v(-3, 4.23) * mm});
            skLineSegment(sketch, "E396", {"start": v(-3, 4.23) * mm, "end": v(-3.12, 4.22) * mm});
            skLineSegment(sketch, "E397", {"start": v(-3.12, 4.22) * mm, "end": v(-3.19, 4.2) * mm});
            skLineSegment(sketch, "E398", {"start": v(-3.19, 4.2) * mm, "end": v(-3.24, 4.16) * mm});
            skLineSegment(sketch, "E399", {"start": v(-3.24, 4.16) * mm, "end": v(-3.28, 4.1) * mm});
            skLineSegment(sketch, "E400", {"start": v(-3.28, 4.1) * mm, "end": v(-3.3, 3.97) * mm});
            skLineSegment(sketch, "E401", {"start": v(-3.3, 3.97) * mm, "end": v(-3.27, 3.87) * mm});
            skLineSegment(sketch, "E402", {"start": v(-3.27, 3.87) * mm, "end": v(-3.25, 3.85) * mm});
            skLineSegment(sketch, "E403", {"start": v(-3.25, 3.85) * mm, "end": v(-3.23, 3.83) * mm});
            skLineSegment(sketch, "E404", {"start": v(-3.23, 3.83) * mm, "end": v(-3.2, 3.8) * mm});
            skLineSegment(sketch, "E405", {"start": v(-3.2, 3.8) * mm, "end": v(-3.17, 3.79) * mm});
            skLineSegment(sketch, "E406", {"start": v(-3.17, 3.79) * mm, "end": v(-3.14, 3.77) * mm});
            skLineSegment(sketch, "E407", {"start": v(-3.14, 3.77) * mm, "end": v(-3.1, 3.76) * mm});
            skLineSegment(sketch, "E408", {"start": v(-3.1, 3.76) * mm, "end": v(-3.08, 3.75) * mm});
            skLineSegment(sketch, "E409", {"start": v(-3.08, 3.75) * mm, "end": v(-3.06, 3.74) * mm});
            skLineSegment(sketch, "E410", {"start": v(-3.06, 3.74) * mm, "end": v(-3.03, 3.75) * mm});
            skLineSegment(sketch, "E411", {"start": v(-3.03, 3.75) * mm, "end": v(-3.01, 3.77) * mm});
            skLineSegment(sketch, "E412", {"start": v(-3.01, 3.77) * mm, "end": v(-3, 3.79) * mm});
            skLineSegment(sketch, "E413", {"start": v(-3, 3.79) * mm, "end": v(-3, 3.8) * mm});
            skLineSegment(sketch, "E414", {"start": v(-3, 3.8) * mm, "end": v(-3, 3.82) * mm});
            skLineSegment(sketch, "E415", {"start": v(-3, 3.82) * mm, "end": v(-3.03, 3.84) * mm});
            skLineSegment(sketch, "E416", {"start": v(-3.03, 3.84) * mm, "end": v(-3.06, 3.86) * mm});
            skLineSegment(sketch, "E417", {"start": v(-3.06, 3.86) * mm, "end": v(-3.08, 3.87) * mm});
            skLineSegment(sketch, "E418", {"start": v(-3.08, 3.87) * mm, "end": v(-3.1, 3.87) * mm});
            skLineSegment(sketch, "E419", {"start": v(-3.1, 3.87) * mm, "end": v(-3.13, 3.9) * mm});
            skLineSegment(sketch, "E420", {"start": v(-3.13, 3.9) * mm, "end": v(-3.15, 3.91) * mm});
            skLineSegment(sketch, "E421", {"start": v(-3.15, 3.91) * mm, "end": v(-3.16, 3.94) * mm});
            skLineSegment(sketch, "E422", {"start": v(-3.16, 3.94) * mm, "end": v(-3.15, 3.96) * mm});
            skLineSegment(sketch, "E423", {"start": v(-3.15, 3.96) * mm, "end": v(-3.13, 3.99) * mm});
            skLineSegment(sketch, "E424", {"start": v(-3.13, 3.99) * mm, "end": v(-3.02, 4.04) * mm});
            skLineSegment(sketch, "E425", {"start": v(-3.02, 4.04) * mm, "end": v(-2.9, 4.05) * mm});
            skLineSegment(sketch, "E426", {"start": v(-2.9, 4.05) * mm, "end": v(-2.82, 4) * mm});
            skLineSegment(sketch, "E427", {"start": v(-2.82, 4) * mm, "end": v(-2.75, 3.92) * mm});
            skLineSegment(sketch, "E428", {"start": v(-2.75, 3.92) * mm, "end": v(-2.73, 3.89) * mm});
            skLineSegment(sketch, "E429", {"start": v(-2.73, 3.89) * mm, "end": v(-2.72, 3.86) * mm});
            skLineSegment(sketch, "E430", {"start": v(-2.72, 3.86) * mm, "end": v(-2.72, 3.83) * mm});
            skLineSegment(sketch, "E431", {"start": v(-2.72, 3.83) * mm, "end": v(-2.72, 3.8) * mm});
            skLineSegment(sketch, "E432", {"start": v(-2.72, 3.8) * mm, "end": v(-2.73, 3.74) * mm});
            skLineSegment(sketch, "E433", {"start": v(-2.73, 3.74) * mm, "end": v(-2.74, 3.7) * mm});
            skLineSegment(sketch, "E434", {"start": v(-2.74, 3.7) * mm, "end": v(-2.76, 3.65) * mm});
            skLineSegment(sketch, "E435", {"start": v(-2.76, 3.65) * mm, "end": v(-2.79, 3.62) * mm});
            skLineSegment(sketch, "E436", {"start": v(-2.79, 3.62) * mm, "end": v(-2.83, 3.6) * mm});
            skLineSegment(sketch, "E437", {"start": v(-2.83, 3.6) * mm, "end": v(-2.87, 3.58) * mm});
            skLineSegment(sketch, "E438", {"start": v(-2.87, 3.58) * mm, "end": v(-2.94, 3.57) * mm});
            skLineSegment(sketch, "E439", {"start": v(-2.94, 3.57) * mm, "end": v(-3.02, 3.56) * mm});
            skLineSegment(sketch, "E440", {"start": v(-3.02, 3.56) * mm, "end": v(-3.1, 3.57) * mm});
            skLineSegment(sketch, "E441", {"start": v(-3.1, 3.57) * mm, "end": v(-3.18, 3.58) * mm});
            skLineSegment(sketch, "E442", {"start": v(-3.18, 3.58) * mm, "end": v(-3.25, 3.6) * mm});
            skLineSegment(sketch, "E443", {"start": v(-3.25, 3.6) * mm, "end": v(-3.33, 3.66) * mm});
            skLineSegment(sketch, "E444", {"start": v(-3.33, 3.66) * mm, "end": v(-3.4, 3.7) * mm});
            skLineSegment(sketch, "E445", {"start": v(-3.4, 3.7) * mm, "end": v(-3.44, 3.75) * mm});
            skLineSegment(sketch, "E446", {"start": v(-3.44, 3.75) * mm, "end": v(-3.49, 3.82) * mm});
            skLineSegment(sketch, "E447", {"start": v(-3.49, 3.82) * mm, "end": v(-3.53, 3.9) * mm});
            skLineSegment(sketch, "E448", {"start": v(-3.53, 3.9) * mm, "end": v(-3.55, 3.94) * mm});
            skLineSegment(sketch, "E449", {"start": v(-3.55, 3.94) * mm, "end": v(-3.56, 3.98) * mm});
            skLineSegment(sketch, "E450", {"start": v(-3.56, 3.98) * mm, "end": v(-3.56, 4.02) * mm});
            skLineSegment(sketch, "E451", {"start": v(-3.56, 4.02) * mm, "end": v(-3.57, 4.08) * mm});
            skLineSegment(sketch, "E452", {"start": v(-3.57, 4.08) * mm, "end": v(-3.56, 4.14) * mm});
            skLineSegment(sketch, "E453", {"start": v(-3.56, 4.14) * mm, "end": v(-3.56, 4.18) * mm});
            skLineSegment(sketch, "E454", {"start": v(-3.56, 4.18) * mm, "end": v(-3.55, 4.21) * mm});
            skLineSegment(sketch, "E455", {"start": v(-3.55, 4.21) * mm, "end": v(-3.52, 4.25) * mm});
            skLineSegment(sketch, "E456", {"start": v(-3.52, 4.25) * mm, "end": v(-3.45, 4.34) * mm});
            skLineSegment(sketch, "E457", {"start": v(-3.45, 4.34) * mm, "end": v(-3.37, 4.41) * mm});
            skLineSegment(sketch, "E458", {"start": v(-3.37, 4.41) * mm, "end": v(-3.27, 4.48) * mm});
            skLineSegment(sketch, "E459", {"start": v(-3.27, 4.48) * mm, "end": v(-3.16, 4.53) * mm});
            skLineSegment(sketch, "E460", {"start": v(-3.16, 4.53) * mm, "end": v(-3.12, 4.54) * mm});
            skLineSegment(sketch, "E461", {"start": v(-3.12, 4.54) * mm, "end": v(-3.08, 4.55) * mm});
            skLineSegment(sketch, "E462", {"start": v(-3.08, 4.55) * mm, "end": v(-3.01, 4.55) * mm});
            skLineSegment(sketch, "E463", {"start": v(-3.01, 4.55) * mm, "end": v(-2.9, 4.55) * mm});
            skLineSegment(sketch, "E464", {"start": v(-2.9, 4.55) * mm, "end": v(-2.8, 4.55) * mm});
            skLineSegment(sketch, "E465", {"start": v(-2.8, 4.55) * mm, "end": v(-2.72, 4.54) * mm});
            skLineSegment(sketch, "E466", {"start": v(-2.72, 4.54) * mm, "end": v(-2.65, 4.53) * mm});
            skLineSegment(sketch, "E467", {"start": v(-2.65, 4.53) * mm, "end": v(-2.56, 4.5) * mm});
            skLineSegment(sketch, "E468", {"start": v(-2.56, 4.5) * mm, "end": v(-2.49, 4.49) * mm});
            skLineSegment(sketch, "E469", {"start": v(-2.49, 4.49) * mm, "end": v(-2.4, 4.47) * mm});
            skLineSegment(sketch, "E470", {"start": v(-2.4, 4.47) * mm, "end": v(-2.34, 4.44) * mm});
            skLineSegment(sketch, "E471", {"start": v(-2.34, 4.44) * mm, "end": v(-2.28, 4.43) * mm});
            skLineSegment(sketch, "E472", {"start": v(-2.28, 4.43) * mm, "end": v(-2.19, 4.4) * mm});
            skLineSegment(sketch, "E473", {"start": v(-2.19, 4.4) * mm, "end": v(-2.09, 4.35) * mm});
            skLineSegment(sketch, "E474", {"start": v(-2.09, 4.35) * mm, "end": v(-1.98, 4.3) * mm});
            skLineSegment(sketch, "E475", {"start": v(-1.98, 4.3) * mm, "end": v(-1.87, 4.24) * mm});
            skLineSegment(sketch, "E476", {"start": v(-1.87, 4.24) * mm, "end": v(-1.76, 4.17) * mm});
            skLineSegment(sketch, "E477", {"start": v(-1.76, 4.17) * mm, "end": v(-1.66, 4.1) * mm});
            skLineSegment(sketch, "E478", {"start": v(-1.66, 4.1) * mm, "end": v(-1.56, 4.03) * mm});
            skLineSegment(sketch, "E479", {"start": v(-1.56, 4.03) * mm, "end": v(-1.48, 3.97) * mm});
            skLineSegment(sketch, "E480", {"start": v(-1.48, 3.97) * mm, "end": v(-1.37, 3.87) * mm});
            skLineSegment(sketch, "E481", {"start": v(-1.37, 3.87) * mm, "end": v(-1.26, 3.74) * mm});
            skLineSegment(sketch, "E482", {"start": v(-1.26, 3.74) * mm, "end": v(-1.15, 3.61) * mm});
            skLineSegment(sketch, "E483", {"start": v(-1.15, 3.61) * mm, "end": v(-1.05, 3.48) * mm});
            skLineSegment(sketch, "E484", {"start": v(-1.05, 3.48) * mm, "end": v(-1.03, 3.45) * mm});
            skLineSegment(sketch, "E485", {"start": v(-1.03, 3.45) * mm, "end": v(-1, 3.41) * mm});
            skLineSegment(sketch, "E486", {"start": v(-1, 3.41) * mm, "end": v(-0.98, 3.38) * mm});
            skLineSegment(sketch, "E487", {"start": v(-0.98, 3.38) * mm, "end": v(-0.96, 3.34) * mm});
            skLineSegment(sketch, "E488", {"start": v(-0.96, 3.34) * mm, "end": v(-0.94, 3.3) * mm});
            skLineSegment(sketch, "E489", {"start": v(-0.94, 3.3) * mm, "end": v(-0.92, 3.28) * mm});
            skLineSegment(sketch, "E490", {"start": v(-0.92, 3.28) * mm, "end": v(-0.9, 3.25) * mm});
            skLineSegment(sketch, "E491", {"start": v(-0.9, 3.25) * mm, "end": v(-0.9, 3.24) * mm});
            skLineSegment(sketch, "E492", {"start": v(-0.9, 3.24) * mm, "end": v(-0.9, 3.22) * mm});
            skLineSegment(sketch, "E493", {"start": v(-0.9, 3.22) * mm, "end": v(-0.88, 3.21) * mm});
            skLineSegment(sketch, "E494", {"start": v(-0.88, 3.21) * mm, "end": v(-0.86, 3.22) * mm});
            skLineSegment(sketch, "E495", {"start": v(-0.86, 3.22) * mm, "end": v(-0.84, 3.25) * mm});
            skLineSegment(sketch, "E496", {"start": v(-0.84, 3.25) * mm, "end": v(-0.8, 3.3) * mm});
            skLineSegment(sketch, "E497", {"start": v(-0.8, 3.3) * mm, "end": v(-0.73, 3.34) * mm});
            skLineSegment(sketch, "E498", {"start": v(-0.73, 3.34) * mm, "end": v(-0.67, 3.39) * mm});
            skLineSegment(sketch, "E499", {"start": v(-0.67, 3.39) * mm, "end": v(-0.62, 3.42) * mm});
            skLineSegment(sketch, "E500", {"start": v(-0.62, 3.42) * mm, "end": v(-0.55, 3.44) * mm});
            skLineSegment(sketch, "E501", {"start": v(-0.55, 3.44) * mm, "end": v(-0.46, 3.47) * mm});
            skLineSegment(sketch, "E502", {"start": v(-0.46, 3.47) * mm, "end": v(-0.36, 3.49) * mm});
            skLineSegment(sketch, "E503", {"start": v(-0.36, 3.49) * mm, "end": v(-0.27, 3.5) * mm});
            skLineSegment(sketch, "E504", {"start": v(-0.27, 3.5) * mm, "end": v(-0.2, 3.5) * mm});
            skLineSegment(sketch, "E505", {"start": v(-0.2, 3.5) * mm, "end": v(-0.16, 3.5) * mm});
            skLineSegment(sketch, "E506", {"start": v(-0.16, 3.5) * mm, "end": v(-0.1, 3.5) * mm});
            skLineSegment(sketch, "E507", {"start": v(-0.1, 3.5) * mm, "end": v(-0.05, 3.48) * mm});
            skLineSegment(sketch, "E508", {"start": v(-0.05, 3.48) * mm, "end": v(0, 3.47) * mm});
            skLineSegment(sketch, "E509", {"start": v(0, 3.47) * mm, "end": v(0.04, 3.45) * mm});
            skLineSegment(sketch, "E510", {"start": v(0.04, 3.45) * mm, "end": v(0.08, 3.44) * mm});
            skLineSegment(sketch, "E511", {"start": v(0.08, 3.44) * mm, "end": v(0.11, 3.42) * mm});
            skLineSegment(sketch, "E512", {"start": v(0.11, 3.42) * mm, "end": v(0.14, 3.4) * mm});
            skLineSegment(sketch, "E513", {"start": v(0.14, 3.4) * mm, "end": v(0.16, 3.4) * mm});
            skLineSegment(sketch, "E514", {"start": v(0.16, 3.4) * mm, "end": v(0.17, 3.4) * mm});
            skLineSegment(sketch, "E515", {"start": v(0.17, 3.4) * mm, "end": v(0.18, 3.4) * mm});
            skLineSegment(sketch, "E516", {"start": v(0.18, 3.4) * mm, "end": v(0.18, 3.4) * mm});
            skLineSegment(sketch, "E517", {"start": v(0.18, 3.4) * mm, "end": v(0.2, 3.43) * mm});
            skLineSegment(sketch, "E518", {"start": v(0.2, 3.43) * mm, "end": v(0.21, 3.47) * mm});
            skLineSegment(sketch, "E519", {"start": v(0.21, 3.47) * mm, "end": v(0.23, 3.52) * mm});
            skLineSegment(sketch, "E520", {"start": v(0.23, 3.52) * mm, "end": v(0.25, 3.56) * mm});
            skLineSegment(sketch, "E521", {"start": v(0.25, 3.56) * mm, "end": v(0.27, 3.61) * mm});
            skLineSegment(sketch, "E522", {"start": v(0.27, 3.61) * mm, "end": v(0.3, 3.67) * mm});
            skLineSegment(sketch, "E523", {"start": v(0.3, 3.67) * mm, "end": v(0.32, 3.73) * mm});
            skLineSegment(sketch, "E524", {"start": v(0.32, 3.73) * mm, "end": v(0.36, 3.82) * mm});
            skLineSegment(sketch, "E525", {"start": v(0.36, 3.82) * mm, "end": v(0.41, 3.92) * mm});
            skLineSegment(sketch, "E526", {"start": v(0.41, 3.92) * mm, "end": v(0.48, 4.05) * mm});
            skLineSegment(sketch, "E527", {"start": v(0.48, 4.05) * mm, "end": v(0.55, 4.2) * mm});
            skLineSegment(sketch, "E528", {"start": v(0.55, 4.2) * mm, "end": v(0.62, 4.32) * mm});
            skLineSegment(sketch, "E529", {"start": v(0.62, 4.32) * mm, "end": v(0.68, 4.43) * mm});
            skLineSegment(sketch, "E530", {"start": v(0.68, 4.43) * mm, "end": v(0.73, 4.53) * mm});
            skLineSegment(sketch, "E531", {"start": v(0.73, 4.53) * mm, "end": v(0.79, 4.62) * mm});
            skLineSegment(sketch, "E532", {"start": v(0.79, 4.62) * mm, "end": v(0.85, 4.7) * mm});
            skLineSegment(sketch, "E533", {"start": v(0.85, 4.7) * mm, "end": v(0.91, 4.8) * mm});
            skLineSegment(sketch, "E534", {"start": v(0.91, 4.8) * mm, "end": v(0.99, 4.9) * mm});
            skLineSegment(sketch, "E535", {"start": v(0.99, 4.9) * mm, "end": v(1.07, 5) * mm});
            skLineSegment(sketch, "E536", {"start": v(1.07, 5) * mm, "end": v(1.14, 5.08) * mm});
            skLineSegment(sketch, "E537", {"start": v(1.14, 5.08) * mm, "end": v(1.21, 5.16) * mm});
            skLineSegment(sketch, "E538", {"start": v(1.21, 5.16) * mm, "end": v(1.3, 5.25) * mm});
            skLineSegment(sketch, "E539", {"start": v(1.3, 5.25) * mm, "end": v(1.37, 5.33) * mm});
            skLineSegment(sketch, "E540", {"start": v(1.37, 5.33) * mm, "end": v(1.44, 5.41) * mm});
            skLineSegment(sketch, "E541", {"start": v(1.44, 5.41) * mm, "end": v(1.51, 5.48) * mm});
            skLineSegment(sketch, "E542", {"start": v(1.51, 5.48) * mm, "end": v(1.57, 5.53) * mm});
            skLineSegment(sketch, "E543", {"start": v(1.57, 5.53) * mm, "end": v(1.61, 5.57) * mm});
            skLineSegment(sketch, "E544", {"start": v(1.61, 5.57) * mm, "end": v(1.75, 5.67) * mm});
            skLineSegment(sketch, "E545", {"start": v(1.75, 5.67) * mm, "end": v(1.89, 5.75) * mm});
            skLineSegment(sketch, "E546", {"start": v(1.89, 5.75) * mm, "end": v(2.01, 5.8) * mm});
            skLineSegment(sketch, "E547", {"start": v(2.01, 5.8) * mm, "end": v(2.13, 5.84) * mm});
            skLineSegment(sketch, "E548", {"start": v(2.13, 5.84) * mm, "end": v(2.2, 5.85) * mm});
            skLineSegment(sketch, "E549", {"start": v(2.2, 5.85) * mm, "end": v(2.27, 5.85) * mm});
            skLineSegment(sketch, "E550", {"start": v(2.27, 5.85) * mm, "end": v(2.34, 5.83) * mm});
            skLineSegment(sketch, "E551", {"start": v(2.34, 5.83) * mm, "end": v(2.43, 5.8) * mm});
            skLineSegment(sketch, "E552", {"start": v(2.43, 5.8) * mm, "end": v(2.51, 5.74) * mm});
            skLineSegment(sketch, "E553", {"start": v(2.51, 5.74) * mm, "end": v(2.6, 5.67) * mm});
            skLineSegment(sketch, "E554", {"start": v(2.6, 5.67) * mm, "end": v(2.66, 5.6) * mm});
            skLineSegment(sketch, "E555", {"start": v(2.66, 5.6) * mm, "end": v(2.7, 5.52) * mm});
            skLineSegment(sketch, "E556", {"start": v(2.7, 5.52) * mm, "end": v(2.74, 5.43) * mm});
            skLineSegment(sketch, "E557", {"start": v(2.74, 5.43) * mm, "end": v(2.77, 5.3) * mm});
            skLineSegment(sketch, "E558", {"start": v(2.77, 5.3) * mm, "end": v(2.79, 5.19) * mm});
            skLineSegment(sketch, "E559", {"start": v(2.79, 5.19) * mm, "end": v(2.8, 5.1) * mm});
            skLineSegment(sketch, "E560", {"start": v(2.8, 5.1) * mm, "end": v(2.78, 5) * mm});
            skLineSegment(sketch, "E561", {"start": v(2.78, 5) * mm, "end": v(2.75, 4.92) * mm});
            skLineSegment(sketch, "E562", {"start": v(2.75, 4.92) * mm, "end": v(2.7, 4.85) * mm});
            skLineSegment(sketch, "E563", {"start": v(2.7, 4.85) * mm, "end": v(2.65, 4.78) * mm});
            skLineSegment(sketch, "E564", {"start": v(2.65, 4.78) * mm, "end": v(2.59, 4.72) * mm});
            skLineSegment(sketch, "E565", {"start": v(2.59, 4.72) * mm, "end": v(2.51, 4.68) * mm});
            skLineSegment(sketch, "E566", {"start": v(2.51, 4.68) * mm, "end": v(2.43, 4.64) * mm});
            skLineSegment(sketch, "E567", {"start": v(2.43, 4.64) * mm, "end": v(2.34, 4.62) * mm});
            skLineSegment(sketch, "E568", {"start": v(2.34, 4.62) * mm, "end": v(2.26, 4.62) * mm});
            skLineSegment(sketch, "E569", {"start": v(2.26, 4.62) * mm, "end": v(2.2, 4.62) * mm});
            skLineSegment(sketch, "E570", {"start": v(2.2, 4.62) * mm, "end": v(2.15, 4.64) * mm});
            skLineSegment(sketch, "E571", {"start": v(2.15, 4.64) * mm, "end": v(2.1, 4.68) * mm});
            skLineSegment(sketch, "E572", {"start": v(2.1, 4.68) * mm, "end": v(2.04, 4.73) * mm});
            skLineSegment(sketch, "E573", {"start": v(2.04, 4.73) * mm, "end": v(2, 4.78) * mm});
            skLineSegment(sketch, "E574", {"start": v(2, 4.78) * mm, "end": v(2, 4.84) * mm});
            skLineSegment(sketch, "E575", {"start": v(2, 4.84) * mm, "end": v(1.99, 4.92) * mm});
            skLineSegment(sketch, "E576", {"start": v(1.99, 4.92) * mm, "end": v(1.99, 5.02) * mm});
            skLineSegment(sketch, "E577", {"start": v(1.99, 5.02) * mm, "end": v(2, 5.09) * mm});
            skLineSegment(sketch, "E578", {"start": v(2, 5.09) * mm, "end": v(2.02, 5.15) * mm});
            skLineSegment(sketch, "E579", {"start": v(2.02, 5.15) * mm, "end": v(2.05, 5.21) * mm});
            skLineSegment(sketch, "E580", {"start": v(2.05, 5.21) * mm, "end": v(2.09, 5.26) * mm});
            skLineSegment(sketch, "E581", {"start": v(2.09, 5.26) * mm, "end": v(2.14, 5.3) * mm});
            skLineSegment(sketch, "E582", {"start": v(2.14, 5.3) * mm, "end": v(2.2, 5.31) * mm});
            skLineSegment(sketch, "E583", {"start": v(2.2, 5.31) * mm, "end": v(2.25, 5.32) * mm});
            skLineSegment(sketch, "E584", {"start": v(2.25, 5.32) * mm, "end": v(2.29, 5.32) * mm});
            skLineSegment(sketch, "E585", {"start": v(2.29, 5.32) * mm, "end": v(2.32, 5.31) * mm});
            skLineSegment(sketch, "E586", {"start": v(2.32, 5.31) * mm, "end": v(2.34, 5.3) * mm});
            skLineSegment(sketch, "E587", {"start": v(2.34, 5.3) * mm, "end": v(2.36, 5.27) * mm});
            skLineSegment(sketch, "E588", {"start": v(2.36, 5.27) * mm, "end": v(2.38, 5.24) * mm});
            skLineSegment(sketch, "E589", {"start": v(2.38, 5.24) * mm, "end": v(2.36, 5.18) * mm});
            skLineSegment(sketch, "E590", {"start": v(2.36, 5.18) * mm, "end": v(2.34, 5.15) * mm});
            skLineSegment(sketch, "E591", {"start": v(2.34, 5.15) * mm, "end": v(2.33, 5.13) * mm});
            skLineSegment(sketch, "E592", {"start": v(2.33, 5.13) * mm, "end": v(2.33, 5.1) * mm});
            skLineSegment(sketch, "E593", {"start": v(2.33, 5.1) * mm, "end": v(2.33, 5.06) * mm});
            skLineSegment(sketch, "E594", {"start": v(2.33, 5.06) * mm, "end": v(2.34, 5.01) * mm});
            skLineSegment(sketch, "E595", {"start": v(2.34, 5.01) * mm, "end": v(2.36, 4.98) * mm});
            skLineSegment(sketch, "E596", {"start": v(2.36, 4.98) * mm, "end": v(2.38, 4.96) * mm});
            skLineSegment(sketch, "E597", {"start": v(2.38, 4.96) * mm, "end": v(2.42, 4.96) * mm});
            skLineSegment(sketch, "E598", {"start": v(2.42, 4.96) * mm, "end": v(2.46, 4.96) * mm});
            skLineSegment(sketch, "E599", {"start": v(2.46, 4.96) * mm, "end": v(2.49, 4.99) * mm});
            skLineSegment(sketch, "E600", {"start": v(2.49, 4.99) * mm, "end": v(2.51, 5.02) * mm});
            skLineSegment(sketch, "E601", {"start": v(2.51, 5.02) * mm, "end": v(2.53, 5.07) * mm});
            skLineSegment(sketch, "E602", {"start": v(2.53, 5.07) * mm, "end": v(2.54, 5.15) * mm});
            skLineSegment(sketch, "E603", {"start": v(2.54, 5.15) * mm, "end": v(2.53, 5.26) * mm});
            skLineSegment(sketch, "E604", {"start": v(2.53, 5.26) * mm, "end": v(2.5, 5.36) * mm});
            skLineSegment(sketch, "E605", {"start": v(2.5, 5.36) * mm, "end": v(2.46, 5.45) * mm});
            skLineSegment(sketch, "E606", {"start": v(2.46, 5.45) * mm, "end": v(2.41, 5.5) * mm});
            skLineSegment(sketch, "E607", {"start": v(2.41, 5.5) * mm, "end": v(2.35, 5.53) * mm});
            skLineSegment(sketch, "E608", {"start": v(2.35, 5.53) * mm, "end": v(2.25, 5.52) * mm});
            skLineSegment(sketch, "E609", {"start": v(2.25, 5.52) * mm, "end": v(2.12, 5.48) * mm});
            skLineSegment(sketch, "E610", {"start": v(2.12, 5.48) * mm, "end": v(2, 5.43) * mm});
            skLineSegment(sketch, "E611", {"start": v(2, 5.43) * mm, "end": v(1.91, 5.39) * mm});
            skLineSegment(sketch, "E612", {"start": v(1.91, 5.39) * mm, "end": v(1.84, 5.34) * mm});
            skLineSegment(sketch, "E613", {"start": v(1.84, 5.34) * mm, "end": v(1.75, 5.27) * mm});
            skLineSegment(sketch, "E614", {"start": v(1.75, 5.27) * mm, "end": v(1.7, 5.21) * mm});
            skLineSegment(sketch, "E615", {"start": v(1.7, 5.21) * mm, "end": v(1.62, 5.14) * mm});
            skLineSegment(sketch, "E616", {"start": v(1.62, 5.14) * mm, "end": v(1.54, 5.06) * mm});
            skLineSegment(sketch, "E617", {"start": v(1.54, 5.06) * mm, "end": v(1.46, 4.97) * mm});
            skLineSegment(sketch, "E618", {"start": v(1.46, 4.97) * mm, "end": v(1.38, 4.88) * mm});
            skLineSegment(sketch, "E619", {"start": v(1.38, 4.88) * mm, "end": v(1.3, 4.8) * mm});
            skLineSegment(sketch, "E620", {"start": v(1.3, 4.8) * mm, "end": v(1.24, 4.72) * mm});
            skLineSegment(sketch, "E621", {"start": v(1.24, 4.72) * mm, "end": v(1.2, 4.66) * mm});
            skLineSegment(sketch, "E622", {"start": v(1.2, 4.66) * mm, "end": v(1.17, 4.63) * mm});
            skLineSegment(sketch, "E623", {"start": v(1.17, 4.63) * mm, "end": v(1.15, 4.6) * mm});
            skLineSegment(sketch, "E624", {"start": v(1.15, 4.6) * mm, "end": v(1.12, 4.56) * mm});
            skLineSegment(sketch, "E625", {"start": v(1.12, 4.56) * mm, "end": v(1.1, 4.53) * mm});
            skLineSegment(sketch, "E626", {"start": v(1.1, 4.53) * mm, "end": v(1.08, 4.5) * mm});
            skLineSegment(sketch, "E627", {"start": v(1.08, 4.5) * mm, "end": v(1.05, 4.46) * mm});
            skLineSegment(sketch, "E628", {"start": v(1.05, 4.46) * mm, "end": v(1.02, 4.42) * mm});
            skLineSegment(sketch, "E629", {"start": v(1.02, 4.42) * mm, "end": v(1, 4.38) * mm});
            skLineSegment(sketch, "E630", {"start": v(1, 4.38) * mm, "end": v(0.97, 4.34) * mm});
            skLineSegment(sketch, "E631", {"start": v(0.97, 4.34) * mm, "end": v(0.95, 4.3) * mm});
            skLineSegment(sketch, "E632", {"start": v(0.95, 4.3) * mm, "end": v(0.93, 4.26) * mm});
            skLineSegment(sketch, "E633", {"start": v(0.93, 4.26) * mm, "end": v(0.91, 4.23) * mm});
            skLineSegment(sketch, "E634", {"start": v(0.91, 4.23) * mm, "end": v(0.82, 4.07) * mm});
            skLineSegment(sketch, "E635", {"start": v(0.82, 4.07) * mm, "end": v(0.75, 3.94) * mm});
            skLineSegment(sketch, "E636", {"start": v(0.75, 3.94) * mm, "end": v(0.7, 3.83) * mm});
            skLineSegment(sketch, "E637", {"start": v(0.7, 3.83) * mm, "end": v(0.66, 3.72) * mm});
            skLineSegment(sketch, "E638", {"start": v(0.66, 3.72) * mm, "end": v(0.66, 3.7) * mm});
            skLineSegment(sketch, "E639", {"start": v(0.66, 3.7) * mm, "end": v(0.64, 3.66) * mm});
            skLineSegment(sketch, "E640", {"start": v(0.64, 3.66) * mm, "end": v(0.63, 3.63) * mm});
            skLineSegment(sketch, "E641", {"start": v(0.63, 3.63) * mm, "end": v(0.62, 3.59) * mm});
            skLineSegment(sketch, "E642", {"start": v(0.62, 3.59) * mm, "end": v(0.57, 3.44) * mm});
            skLineSegment(sketch, "E643", {"start": v(0.57, 3.44) * mm, "end": v(0.51, 3.23) * mm});
            skLineSegment(sketch, "E644", {"start": v(0.51, 3.23) * mm, "end": v(0.5, 3.15) * mm});
            skLineSegment(sketch, "E645", {"start": v(0.5, 3.15) * mm, "end": v(0.52, 3.06) * mm});
            skLineSegment(sketch, "E646", {"start": v(0.52, 3.06) * mm, "end": v(0.55, 2.93) * mm});
            skLineSegment(sketch, "E647", {"start": v(0.55, 2.93) * mm, "end": v(0.58, 2.76) * mm});
            skLineSegment(sketch, "E648", {"start": v(0.58, 2.76) * mm, "end": v(0.6, 2.6) * mm});
            skLineSegment(sketch, "E649", {"start": v(0.6, 2.6) * mm, "end": v(0.6, 2.46) * mm});
            skLineSegment(sketch, "E650", {"start": v(0.6, 2.46) * mm, "end": v(0.58, 2.38) * mm});
            skLineSegment(sketch, "E651", {"start": v(0.58, 2.38) * mm, "end": v(0.55, 2.27) * mm});
            skLineSegment(sketch, "E652", {"start": v(0.55, 2.27) * mm, "end": v(0.53, 2.17) * mm});
            skLineSegment(sketch, "E653", {"start": v(0.53, 2.17) * mm, "end": v(0.5, 2.09) * mm});
            skLineSegment(sketch, "E654", {"start": v(0.5, 2.09) * mm, "end": v(0.47, 2.02) * mm});
            skLineSegment(sketch, "E655", {"start": v(0.47, 2.02) * mm, "end": v(0.43, 1.94) * mm});
            skLineSegment(sketch, "E656", {"start": v(0.43, 1.94) * mm, "end": v(0.38, 1.86) * mm});
            skLineSegment(sketch, "E657", {"start": v(0.38, 1.86) * mm, "end": v(0.34, 1.8) * mm});
            skLineSegment(sketch, "E658", {"start": v(0.34, 1.8) * mm, "end": v(0.33, 1.78) * mm});
            skLineSegment(sketch, "E659", {"start": v(0.33, 1.78) * mm, "end": v(0.32, 1.76) * mm});
            skLineSegment(sketch, "E660", {"start": v(0.32, 1.76) * mm, "end": v(0.32, 1.75) * mm});
            skLineSegment(sketch, "E661", {"start": v(0.32, 1.75) * mm, "end": v(0.33, 1.74) * mm});
            skLineSegment(sketch, "E662", {"start": v(0.33, 1.74) * mm, "end": v(0.36, 1.7) * mm});
            skLineSegment(sketch, "E663", {"start": v(0.36, 1.7) * mm, "end": v(0.4, 1.6) * mm});
            skLineSegment(sketch, "E664", {"start": v(0.4, 1.6) * mm, "end": v(0.43, 1.49) * mm});
            skLineSegment(sketch, "E665", {"start": v(0.43, 1.49) * mm, "end": v(0.46, 1.37) * mm});
            skLineSegment(sketch, "E666", {"start": v(0.46, 1.37) * mm, "end": v(0.47, 1.32) * mm});
            skLineSegment(sketch, "E667", {"start": v(0.47, 1.32) * mm, "end": v(0.48, 1.28) * mm});
            skLineSegment(sketch, "E668", {"start": v(0.48, 1.28) * mm, "end": v(0.48, 1.25) * mm});
            skLineSegment(sketch, "E669", {"start": v(0.48, 1.25) * mm, "end": v(0.49, 1.24) * mm});
            skLineSegment(sketch, "E670", {"start": v(0.49, 1.24) * mm, "end": v(0.5, 1.26) * mm});
            skLineSegment(sketch, "E671", {"start": v(0.5, 1.26) * mm, "end": v(0.56, 1.32) * mm});
            skLineSegment(sketch, "E672", {"start": v(0.56, 1.32) * mm, "end": v(0.61, 1.4) * mm});
            skLineSegment(sketch, "E673", {"start": v(0.61, 1.4) * mm, "end": v(0.66, 1.48) * mm});
            skLineSegment(sketch, "E674", {"start": v(0.66, 1.48) * mm, "end": v(0.7, 1.54) * mm});
            skLineSegment(sketch, "E675", {"start": v(0.7, 1.54) * mm, "end": v(0.78, 1.62) * mm});
            skLineSegment(sketch, "E676", {"start": v(0.78, 1.62) * mm, "end": v(0.88, 1.72) * mm});
            skLineSegment(sketch, "E677", {"start": v(0.88, 1.72) * mm, "end": v(1.02, 1.85) * mm});
            skLineSegment(sketch, "E678", {"start": v(1.02, 1.85) * mm, "end": v(1.13, 1.94) * mm});
            skLineSegment(sketch, "E679", {"start": v(1.13, 1.94) * mm, "end": v(1.21, 2.02) * mm});
            skLineSegment(sketch, "E680", {"start": v(1.21, 2.02) * mm, "end": v(1.3, 2.09) * mm});
            skLineSegment(sketch, "E681", {"start": v(1.3, 2.09) * mm, "end": v(1.42, 2.16) * mm});
            skLineSegment(sketch, "E682", {"start": v(1.42, 2.16) * mm, "end": v(1.73, 2.36) * mm});
            skLineSegment(sketch, "E683", {"start": v(1.73, 2.36) * mm, "end": v(2.02, 2.5) * mm});
            skLineSegment(sketch, "E684", {"start": v(2.02, 2.5) * mm, "end": v(2.29, 2.61) * mm});
            skLineSegment(sketch, "E685", {"start": v(2.29, 2.61) * mm, "end": v(2.54, 2.68) * mm});
            skLineSegment(sketch, "E686", {"start": v(2.54, 2.68) * mm, "end": v(2.67, 2.7) * mm});
            skLineSegment(sketch, "E687", {"start": v(2.67, 2.7) * mm, "end": v(2.81, 2.73) * mm});
            skLineSegment(sketch, "E688", {"start": v(2.81, 2.73) * mm, "end": v(2.89, 2.74) * mm});
            skLineSegment(sketch, "E689", {"start": v(2.89, 2.74) * mm, "end": v(2.98, 2.75) * mm});
            skLineSegment(sketch, "E690", {"start": v(2.98, 2.75) * mm, "end": v(3.09, 2.76) * mm});
            skLineSegment(sketch, "E691", {"start": v(3.09, 2.76) * mm, "end": v(3.18, 2.77) * mm});
            skLineSegment(sketch, "E692", {"start": v(3.18, 2.77) * mm, "end": v(3.3, 2.78) * mm});
            skLineSegment(sketch, "E693", {"start": v(3.3, 2.78) * mm, "end": v(3.38, 2.78) * mm});
            skLineSegment(sketch, "E694", {"start": v(3.38, 2.78) * mm, "end": v(3.46, 2.78) * mm});
            skLineSegment(sketch, "E695", {"start": v(3.46, 2.78) * mm, "end": v(3.56, 2.77) * mm});
            skLineSegment(sketch, "E696", {"start": v(3.56, 2.77) * mm, "end": v(3.73, 2.75) * mm});
            skLineSegment(sketch, "E697", {"start": v(3.73, 2.75) * mm, "end": v(3.86, 2.74) * mm});
            skLineSegment(sketch, "E698", {"start": v(3.86, 2.74) * mm, "end": v(3.95, 2.73) * mm});
            skLineSegment(sketch, "E699", {"start": v(3.95, 2.73) * mm, "end": v(4.03, 2.71) * mm});
            skLineSegment(sketch, "E700", {"start": v(4.03, 2.71) * mm, "end": v(4.07, 2.7) * mm});
            skLineSegment(sketch, "E701", {"start": v(4.07, 2.7) * mm, "end": v(4.12, 2.7) * mm});
            skLineSegment(sketch, "E702", {"start": v(4.12, 2.7) * mm, "end": v(4.17, 2.68) * mm});
            skLineSegment(sketch, "E703", {"start": v(4.17, 2.68) * mm, "end": v(4.21, 2.68) * mm});
            skLineSegment(sketch, "E704", {"start": v(4.21, 2.68) * mm, "end": v(4.33, 2.66) * mm});
            skLineSegment(sketch, "E705", {"start": v(4.33, 2.66) * mm, "end": v(4.46, 2.63) * mm});
            skLineSegment(sketch, "E706", {"start": v(4.46, 2.63) * mm, "end": v(4.6, 2.6) * mm});
            skLineSegment(sketch, "E707", {"start": v(4.6, 2.6) * mm, "end": v(4.73, 2.57) * mm});
            skLineSegment(sketch, "E708", {"start": v(4.73, 2.57) * mm, "end": v(4.9, 2.56) * mm});
            skLineSegment(sketch, "E709", {"start": v(4.9, 2.56) * mm, "end": v(5.08, 2.55) * mm});
            skLineSegment(sketch, "E710", {"start": v(5.08, 2.55) * mm, "end": v(5.25, 2.55) * mm});
            skLineSegment(sketch, "E711", {"start": v(5.25, 2.55) * mm, "end": v(5.37, 2.55) * mm});
            skLineSegment(sketch, "E712", {"start": v(5.37, 2.55) * mm, "end": v(5.48, 2.58) * mm});
            skLineSegment(sketch, "E713", {"start": v(5.48, 2.58) * mm, "end": v(5.62, 2.61) * mm});
            skLineSegment(sketch, "E714", {"start": v(5.62, 2.61) * mm, "end": v(5.78, 2.66) * mm});
            skLineSegment(sketch, "E715", {"start": v(5.78, 2.66) * mm, "end": v(5.95, 2.72) * mm});
            skLineSegment(sketch, "E716", {"start": v(5.95, 2.72) * mm, "end": v(6.05, 2.76) * mm});
            skLineSegment(sketch, "E717", {"start": v(6.05, 2.76) * mm, "end": v(6.15, 2.8) * mm});
            skLineSegment(sketch, "E718", {"start": v(6.15, 2.8) * mm, "end": v(6.24, 2.83) * mm});
            skLineSegment(sketch, "E719", {"start": v(6.24, 2.83) * mm, "end": v(6.3, 2.85) * mm});
            skLineSegment(sketch, "E720", {"start": v(6.3, 2.85) * mm, "end": v(6.43, 2.9) * mm});
            skLineSegment(sketch, "E721", {"start": v(6.43, 2.9) * mm, "end": v(6.55, 2.93) * mm});
            skLineSegment(sketch, "E722", {"start": v(6.55, 2.93) * mm, "end": v(6.63, 2.96) * mm});
            skLineSegment(sketch, "E723", {"start": v(6.63, 2.96) * mm, "end": v(6.74, 3) * mm});
            skLineSegment(sketch, "E724", {"start": v(6.74, 3) * mm, "end": v(6.85, 3.02) * mm});
            skLineSegment(sketch, "E725", {"start": v(6.85, 3.02) * mm, "end": v(6.96, 3.05) * mm});
            skLineSegment(sketch, "E726", {"start": v(6.96, 3.05) * mm, "end": v(7.07, 3.08) * mm});
            skLineSegment(sketch, "E727", {"start": v(7.07, 3.08) * mm, "end": v(7.17, 3.1) * mm});
            skLineSegment(sketch, "E728", {"start": v(7.17, 3.1) * mm, "end": v(7.26, 3.11) * mm});
            skLineSegment(sketch, "E729", {"start": v(7.26, 3.11) * mm, "end": v(7.33, 3.12) * mm});
            skLineSegment(sketch, "E730", {"start": v(7.33, 3.12) * mm, "end": v(7.44, 3.13) * mm});
            skLineSegment(sketch, "E731", {"start": v(7.44, 3.13) * mm, "end": v(7.57, 3.13) * mm});
            skLineSegment(sketch, "E732", {"start": v(7.57, 3.13) * mm, "end": v(7.68, 3.13) * mm});
            skLineSegment(sketch, "E733", {"start": v(7.68, 3.13) * mm, "end": v(7.77, 3.12) * mm});
            skLineSegment(sketch, "E734", {"start": v(7.77, 3.12) * mm, "end": v(7.86, 3.1) * mm});
            skLineSegment(sketch, "E735", {"start": v(7.86, 3.1) * mm, "end": v(7.94, 3.07) * mm});
            skLineSegment(sketch, "E736", {"start": v(7.94, 3.07) * mm, "end": v(8, 3.04) * mm});
            skLineSegment(sketch, "E737", {"start": v(8, 3.04) * mm, "end": v(8.04, 3) * mm});
            skLineSegment(sketch, "E738", {"start": v(8.04, 3) * mm, "end": v(8.05, 2.98) * mm});
            skLineSegment(sketch, "E739", {"start": v(8.05, 2.98) * mm, "end": v(8.04, 2.96) * mm});
            skLineSegment(sketch, "E740", {"start": v(8.04, 2.96) * mm, "end": v(8.03, 2.94) * mm});
            skLineSegment(sketch, "E741", {"start": v(8.03, 2.94) * mm, "end": v(8.02, 2.92) * mm});
            skLineSegment(sketch, "E742", {"start": v(8.02, 2.92) * mm, "end": v(8, 2.89) * mm});
            skLineSegment(sketch, "E743", {"start": v(8, 2.89) * mm, "end": v(8, 2.84) * mm});
            skLineSegment(sketch, "E744", {"start": v(8, 2.84) * mm, "end": v(7.94, 2.7) * mm});
            skLineSegment(sketch, "E745", {"start": v(7.94, 2.7) * mm, "end": v(7.86, 2.53) * mm});
            skLineSegment(sketch, "E746", {"start": v(7.86, 2.53) * mm, "end": v(7.77, 2.36) * mm});
            skLineSegment(sketch, "E747", {"start": v(7.77, 2.36) * mm, "end": v(7.67, 2.19) * mm});
            skLineSegment(sketch, "E748", {"start": v(7.67, 2.19) * mm, "end": v(7.6, 2.07) * mm});
            skLineSegment(sketch, "E749", {"start": v(7.6, 2.07) * mm, "end": v(7.55, 1.98) * mm});
            skLineSegment(sketch, "E750", {"start": v(7.55, 1.98) * mm, "end": v(7.5, 1.9) * mm});
            skLineSegment(sketch, "E751", {"start": v(7.5, 1.9) * mm, "end": v(7.47, 1.82) * mm});
            skLineSegment(sketch, "E752", {"start": v(7.47, 1.82) * mm, "end": v(7.44, 1.77) * mm});
            skLineSegment(sketch, "E753", {"start": v(7.44, 1.77) * mm, "end": v(7.4, 1.72) * mm});
            skLineSegment(sketch, "E754", {"start": v(7.4, 1.72) * mm, "end": v(7.38, 1.68) * mm});
            skLineSegment(sketch, "E755", {"start": v(7.38, 1.68) * mm, "end": v(7.36, 1.65) * mm});
            skLineSegment(sketch, "E756", {"start": v(7.36, 1.65) * mm, "end": v(7.31, 1.58) * mm});
            skLineSegment(sketch, "E757", {"start": v(7.31, 1.58) * mm, "end": v(7.26, 1.5) * mm});
            skLineSegment(sketch, "E758", {"start": v(7.26, 1.5) * mm, "end": v(7.2, 1.41) * mm});
            skLineSegment(sketch, "E759", {"start": v(7.2, 1.41) * mm, "end": v(7.16, 1.35) * mm});
            skLineSegment(sketch, "E760", {"start": v(7.16, 1.35) * mm, "end": v(7.13, 1.3) * mm});
            skLineSegment(sketch, "E761", {"start": v(7.13, 1.3) * mm, "end": v(7.07, 1.24) * mm});
            skLineSegment(sketch, "E762", {"start": v(7.07, 1.24) * mm, "end": v(7, 1.18) * mm});
            skLineSegment(sketch, "E763", {"start": v(7, 1.18) * mm, "end": v(6.94, 1.1) * mm});
            skLineSegment(sketch, "E764", {"start": v(6.94, 1.1) * mm, "end": v(6.86, 1.04) * mm});
            skLineSegment(sketch, "E765", {"start": v(6.86, 1.04) * mm, "end": v(6.79, 0.99) * mm});
            skLineSegment(sketch, "E766", {"start": v(6.79, 0.99) * mm, "end": v(6.72, 0.94) * mm});
            skLineSegment(sketch, "E767", {"start": v(6.72, 0.94) * mm, "end": v(6.66, 0.91) * mm});
            skLineSegment(sketch, "E768", {"start": v(6.66, 0.91) * mm, "end": v(6.6, 0.89) * mm});
            skLineSegment(sketch, "E769", {"start": v(6.6, 0.89) * mm, "end": v(6.52, 0.86) * mm});
            skLineSegment(sketch, "E770", {"start": v(6.52, 0.86) * mm, "end": v(6.46, 0.85) * mm});
            skLineSegment(sketch, "E771", {"start": v(6.46, 0.85) * mm, "end": v(6.43, 0.85) * mm});
            skLineSegment(sketch, "E772", {"start": v(6.43, 0.85) * mm, "end": v(6.41, 0.85) * mm});
            skLineSegment(sketch, "E773", {"start": v(6.41, 0.85) * mm, "end": v(6.37, 0.85) * mm});
            skLineSegment(sketch, "E774", {"start": v(6.37, 0.85) * mm, "end": v(6.32, 0.85) * mm});
            skLineSegment(sketch, "E775", {"start": v(6.32, 0.85) * mm, "end": v(6.26, 0.85) * mm});
            skLineSegment(sketch, "E776", {"start": v(6.26, 0.85) * mm, "end": v(6.16, 0.84) * mm});
            skLineSegment(sketch, "E777", {"start": v(6.16, 0.84) * mm, "end": v(6.1, 0.83) * mm});
            skLineSegment(sketch, "E778", {"start": v(6.1, 0.83) * mm, "end": v(6.03, 0.81) * mm});
            skLineSegment(sketch, "E779", {"start": v(6.03, 0.81) * mm, "end": v(5.95, 0.78) * mm});
            skLineSegment(sketch, "E780", {"start": v(5.95, 0.78) * mm, "end": v(5.84, 0.74) * mm});
            skLineSegment(sketch, "E781", {"start": v(5.84, 0.74) * mm, "end": v(5.76, 0.7) * mm});
            skLineSegment(sketch, "E782", {"start": v(5.76, 0.7) * mm, "end": v(5.7, 0.67) * mm});
            skLineSegment(sketch, "E783", {"start": v(5.7, 0.67) * mm, "end": v(5.63, 0.63) * mm});
            skLineSegment(sketch, "E784", {"start": v(5.63, 0.63) * mm, "end": v(5.49, 0.53) * mm});
            skLineSegment(sketch, "E785", {"start": v(5.49, 0.53) * mm, "end": v(5.32, 0.43) * mm});
            skLineSegment(sketch, "E786", {"start": v(5.32, 0.43) * mm, "end": v(5.14, 0.33) * mm});
            skLineSegment(sketch, "E787", {"start": v(5.14, 0.33) * mm, "end": v(4.96, 0.23) * mm});
            skLineSegment(sketch, "E788", {"start": v(4.96, 0.23) * mm, "end": v(4.8, 0.17) * mm});
            skLineSegment(sketch, "E789", {"start": v(4.8, 0.17) * mm, "end": v(4.6, 0.1) * mm});
            skLineSegment(sketch, "E790", {"start": v(4.6, 0.1) * mm, "end": v(4.4, 0.06) * mm});
            skLineSegment(sketch, "E791", {"start": v(4.4, 0.06) * mm, "end": v(4.23, 0.03) * mm});
            skLineSegment(sketch, "E792", {"start": v(4.23, 0.03) * mm, "end": v(4.18, 0.03) * mm});
            skLineSegment(sketch, "E793", {"start": v(4.18, 0.03) * mm, "end": v(4.14, 0.02) * mm});
            skLineSegment(sketch, "E794", {"start": v(4.14, 0.02) * mm, "end": v(4.1, 0.02) * mm});
            skLineSegment(sketch, "E795", {"start": v(4.1, 0.02) * mm, "end": v(4.1, 0.02) * mm});
            skLineSegment(sketch, "E796", {"start": v(4.1, 0.02) * mm, "end": v(4.1, 0.01) * mm});
            skLineSegment(sketch, "E797", {"start": v(4.1, 0.01) * mm, "end": v(4.12, 0) * mm});
            skLineSegment(sketch, "E798", {"start": v(4.12, 0) * mm, "end": v(4.16, -0.03) * mm});
            skLineSegment(sketch, "E799", {"start": v(4.16, -0.03) * mm, "end": v(4.22, -0.05) * mm});
            skLineSegment(sketch, "E800", {"start": v(4.22, -0.05) * mm, "end": v(4.29, -0.08) * mm});
            skLineSegment(sketch, "E801", {"start": v(4.29, -0.08) * mm, "end": v(4.37, -0.1) * mm});
            skLineSegment(sketch, "E802", {"start": v(4.37, -0.1) * mm, "end": v(4.45, -0.14) * mm});
            skLineSegment(sketch, "E803", {"start": v(4.45, -0.14) * mm, "end": v(4.54, -0.17) * mm});
            skLineSegment(sketch, "E804", {"start": v(4.54, -0.17) * mm, "end": v(4.63, -0.2) * mm});
            skLineSegment(sketch, "E805", {"start": v(4.63, -0.2) * mm, "end": v(4.7, -0.22) * mm});
            skLineSegment(sketch, "E806", {"start": v(4.7, -0.22) * mm, "end": v(4.77, -0.24) * mm});
            skLineSegment(sketch, "E807", {"start": v(4.77, -0.24) * mm, "end": v(4.85, -0.26) * mm});
            skLineSegment(sketch, "E808", {"start": v(4.85, -0.26) * mm, "end": v(4.94, -0.28) * mm});
            skLineSegment(sketch, "E809", {"start": v(4.94, -0.28) * mm, "end": v(5.06, -0.3) * mm});
            skLineSegment(sketch, "E810", {"start": v(5.06, -0.3) * mm, "end": v(5.21, -0.34) * mm});
            skLineSegment(sketch, "E811", {"start": v(5.21, -0.34) * mm, "end": v(5.41, -0.38) * mm});
            skLineSegment(sketch, "E812", {"start": v(5.41, -0.38) * mm, "end": v(5.54, -0.4) * mm});
            skLineSegment(sketch, "E813", {"start": v(5.54, -0.4) * mm, "end": v(5.7, -0.42) * mm});
            skLineSegment(sketch, "E814", {"start": v(5.7, -0.42) * mm, "end": v(5.9, -0.43) * mm});
            skLineSegment(sketch, "E815", {"start": v(5.9, -0.43) * mm, "end": v(6.14, -0.44) * mm});
            skLineSegment(sketch, "E816", {"start": v(6.14, -0.44) * mm, "end": v(6.36, -0.45) * mm});
            skLineSegment(sketch, "E817", {"start": v(6.36, -0.45) * mm, "end": v(6.55, -0.46) * mm});
            skLineSegment(sketch, "E818", {"start": v(6.55, -0.46) * mm, "end": v(6.73, -0.47) * mm});
            skLineSegment(sketch, "E819", {"start": v(6.73, -0.47) * mm, "end": v(6.92, -0.49) * mm});
            skLineSegment(sketch, "E820", {"start": v(6.92, -0.49) * mm, "end": v(7.01, -0.5) * mm});
            skLineSegment(sketch, "E821", {"start": v(7.01, -0.5) * mm, "end": v(7.12, -0.5) * mm});
            skLineSegment(sketch, "E822", {"start": v(7.12, -0.5) * mm, "end": v(7.23, -0.52) * mm});
            skLineSegment(sketch, "E823", {"start": v(7.23, -0.52) * mm, "end": v(7.32, -0.52) * mm});
            skLineSegment(sketch, "E824", {"start": v(7.32, -0.52) * mm, "end": v(7.57, -0.54) * mm});
            skLineSegment(sketch, "E825", {"start": v(7.57, -0.54) * mm, "end": v(7.79, -0.57) * mm});
            skLineSegment(sketch, "E826", {"start": v(7.79, -0.57) * mm, "end": v(7.97, -0.62) * mm});
            skLineSegment(sketch, "E827", {"start": v(7.97, -0.62) * mm, "end": v(8.12, -0.67) * mm});
            skLineSegment(sketch, "E828", {"start": v(8.12, -0.67) * mm, "end": v(8.2, -0.71) * mm});
            skLineSegment(sketch, "E829", {"start": v(8.2, -0.71) * mm, "end": v(8.29, -0.76) * mm});
            skLineSegment(sketch, "E830", {"start": v(8.29, -0.76) * mm, "end": v(8.37, -0.8) * mm});
            skLineSegment(sketch, "E831", {"start": v(8.37, -0.8) * mm, "end": v(8.42, -0.84) * mm});
            skLineSegment(sketch, "E832", {"start": v(8.42, -0.84) * mm, "end": v(8.55, -0.95) * mm});
            skLineSegment(sketch, "E833", {"start": v(8.55, -0.95) * mm, "end": v(8.67, -1.06) * mm});
            skLineSegment(sketch, "E834", {"start": v(8.67, -1.06) * mm, "end": v(8.76, -1.16) * mm});
            skLineSegment(sketch, "E835", {"start": v(8.76, -1.16) * mm, "end": v(8.83, -1.25) * mm});
            skLineSegment(sketch, "E836", {"start": v(8.83, -1.25) * mm, "end": v(8.94, -1.46) * mm});
            skLineSegment(sketch, "E837", {"start": v(8.94, -1.46) * mm, "end": v(9.01, -1.65) * mm});
            skLineSegment(sketch, "E838", {"start": v(9.01, -1.65) * mm, "end": v(9.06, -1.82) * mm});
            skLineSegment(sketch, "E839", {"start": v(9.06, -1.82) * mm, "end": v(9.07, -2) * mm});
            skLineSegment(sketch, "E840", {"start": v(9.07, -2) * mm, "end": v(9.07, -2.07) * mm});
            skLineSegment(sketch, "E841", {"start": v(9.07, -2.07) * mm, "end": v(9.06, -2.12) * mm});
            skLineSegment(sketch, "E842", {"start": v(9.06, -2.12) * mm, "end": v(9.06, -2.15) * mm});
            skLineSegment(sketch, "E843", {"start": v(9.06, -2.15) * mm, "end": v(9.05, -2.17) * mm});
            skLineSegment(sketch, "E844", {"start": v(9.05, -2.17) * mm, "end": v(9.02, -2.21) * mm});
            skLineSegment(sketch, "E845", {"start": v(9.02, -2.21) * mm, "end": v(9, -2.25) * mm});
            skLineSegment(sketch, "E846", {"start": v(9, -2.25) * mm, "end": v(8.97, -2.28) * mm});
            skLineSegment(sketch, "E847", {"start": v(8.97, -2.28) * mm, "end": v(8.95, -2.3) * mm});
            skLineSegment(sketch, "E848", {"start": v(8.95, -2.3) * mm, "end": v(8.91, -2.3) * mm});
            skLineSegment(sketch, "E849", {"start": v(8.91, -2.3) * mm, "end": v(8.83, -2.31) * mm});
            skLineSegment(sketch, "E850", {"start": v(8.83, -2.31) * mm, "end": v(8.71, -2.3) * mm});
            skLineSegment(sketch, "E851", {"start": v(8.71, -2.3) * mm, "end": v(8.57, -2.3) * mm});
            skLineSegment(sketch, "E852", {"start": v(8.57, -2.3) * mm, "end": v(8.42, -2.28) * mm});
            skLineSegment(sketch, "E853", {"start": v(8.42, -2.28) * mm, "end": v(8.25, -2.27) * mm});
            skLineSegment(sketch, "E854", {"start": v(8.25, -2.27) * mm, "end": v(8.08, -2.24) * mm});
            skLineSegment(sketch, "E855", {"start": v(8.08, -2.24) * mm, "end": v(7.92, -2.22) * mm});
            skLineSegment(sketch, "E856", {"start": v(7.92, -2.22) * mm, "end": v(7.77, -2.2) * mm});
            skLineSegment(sketch, "E857", {"start": v(7.77, -2.2) * mm, "end": v(7.66, -2.18) * mm});
            skLineSegment(sketch, "E858", {"start": v(7.66, -2.18) * mm, "end": v(7.57, -2.17) * mm});
            skLineSegment(sketch, "E859", {"start": v(7.57, -2.17) * mm, "end": v(7.47, -2.17) * mm});
            skLineSegment(sketch, "E860", {"start": v(7.47, -2.17) * mm, "end": v(7.3, -2.17) * mm});
            skLineSegment(sketch, "E861", {"start": v(7.3, -2.17) * mm, "end": v(7.06, -2.23) * mm});
            skLineSegment(sketch, "E862", {"start": v(7.06, -2.23) * mm, "end": v(7, -2.25) * mm});
            skLineSegment(sketch, "E863", {"start": v(7, -2.25) * mm, "end": v(6.92, -2.27) * mm});
            skLineSegment(sketch, "E864", {"start": v(6.92, -2.27) * mm, "end": v(6.84, -2.29) * mm});
            skLineSegment(sketch, "E865", {"start": v(6.84, -2.29) * mm, "end": v(6.76, -2.31) * mm});
            skLineSegment(sketch, "E866", {"start": v(6.76, -2.31) * mm, "end": v(6.66, -2.34) * mm});
            skLineSegment(sketch, "E867", {"start": v(6.66, -2.34) * mm, "end": v(6.55, -2.37) * mm});
            skLineSegment(sketch, "E868", {"start": v(6.55, -2.37) * mm, "end": v(6.4, -2.41) * mm});
            skLineSegment(sketch, "E869", {"start": v(6.4, -2.41) * mm, "end": v(6.24, -2.46) * mm});
            skLineSegment(sketch, "E870", {"start": v(6.24, -2.46) * mm, "end": v(6.2, -2.48) * mm});
            skLineSegment(sketch, "E871", {"start": v(6.2, -2.48) * mm, "end": v(6.14, -2.5) * mm});
            skLineSegment(sketch, "E872", {"start": v(6.14, -2.5) * mm, "end": v(6.08, -2.52) * mm});
            skLineSegment(sketch, "E873", {"start": v(6.08, -2.52) * mm, "end": v(6.02, -2.53) * mm});
            skLineSegment(sketch, "E874", {"start": v(6.02, -2.53) * mm, "end": v(5.8, -2.61) * mm});
            skLineSegment(sketch, "E875", {"start": v(5.8, -2.61) * mm, "end": v(5.55, -2.69) * mm});
            skLineSegment(sketch, "E876", {"start": v(5.55, -2.69) * mm, "end": v(5.32, -2.75) * mm});
            skLineSegment(sketch, "E877", {"start": v(5.32, -2.75) * mm, "end": v(5.13, -2.79) * mm});
            skLineSegment(sketch, "E878", {"start": v(5.13, -2.79) * mm, "end": v(4.94, -2.82) * mm});
            skLineSegment(sketch, "E879", {"start": v(4.94, -2.82) * mm, "end": v(4.74, -2.84) * mm});
            skLineSegment(sketch, "E880", {"start": v(4.74, -2.84) * mm, "end": v(4.55, -2.86) * mm});
            skLineSegment(sketch, "E881", {"start": v(4.55, -2.86) * mm, "end": v(4.36, -2.87) * mm});
            skLineSegment(sketch, "E882", {"start": v(4.36, -2.87) * mm, "end": v(4.18, -2.88) * mm});
            skLineSegment(sketch, "E883", {"start": v(4.18, -2.88) * mm, "end": v(4, -2.88) * mm});
            skLineSegment(sketch, "E884", {"start": v(4, -2.88) * mm, "end": v(3.85, -2.87) * mm});
            skLineSegment(sketch, "E885", {"start": v(3.85, -2.87) * mm, "end": v(3.72, -2.86) * mm});
            skLineSegment(sketch, "E886", {"start": v(3.72, -2.86) * mm, "end": v(3.65, -2.85) * mm});
            skLineSegment(sketch, "E887", {"start": v(3.65, -2.85) * mm, "end": v(3.6, -2.84) * mm});
            skLineSegment(sketch, "E888", {"start": v(3.6, -2.84) * mm, "end": v(3.56, -2.83) * mm});
            skLineSegment(sketch, "E889", {"start": v(3.56, -2.83) * mm, "end": v(3.54, -2.83) * mm});
            skLineSegment(sketch, "E890", {"start": v(3.54, -2.83) * mm, "end": v(3.52, -2.82) * mm});
            skLineSegment(sketch, "E891", {"start": v(3.52, -2.82) * mm, "end": v(3.48, -2.82) * mm});
            skLineSegment(sketch, "E892", {"start": v(3.48, -2.82) * mm, "end": v(3.43, -2.81) * mm});
            skLineSegment(sketch, "E893", {"start": v(3.43, -2.81) * mm, "end": v(3.36, -2.8) * mm});
            skLineSegment(sketch, "E894", {"start": v(3.36, -2.8) * mm, "end": v(3.2, -2.79) * mm});
            skLineSegment(sketch, "E895", {"start": v(3.2, -2.79) * mm, "end": v(3.06, -2.76) * mm});
            skLineSegment(sketch, "E896", {"start": v(3.06, -2.76) * mm, "end": v(2.93, -2.73) * mm});
            skLineSegment(sketch, "E897", {"start": v(2.93, -2.73) * mm, "end": v(2.82, -2.7) * mm});
            skLineSegment(sketch, "E898", {"start": v(2.82, -2.7) * mm, "end": v(2.78, -2.69) * mm});
            skLineSegment(sketch, "E899", {"start": v(2.78, -2.69) * mm, "end": v(2.73, -2.67) * mm});
            skLineSegment(sketch, "E900", {"start": v(2.73, -2.67) * mm, "end": v(2.68, -2.66) * mm});
            skLineSegment(sketch, "E901", {"start": v(2.68, -2.66) * mm, "end": v(2.64, -2.64) * mm});
            skLineSegment(sketch, "E902", {"start": v(2.64, -2.64) * mm, "end": v(2.6, -2.63) * mm});
            skLineSegment(sketch, "E903", {"start": v(2.6, -2.63) * mm, "end": v(2.55, -2.61) * mm});
            skLineSegment(sketch, "E904", {"start": v(2.55, -2.61) * mm, "end": v(2.5, -2.59) * mm});
            skLineSegment(sketch, "E905", {"start": v(2.5, -2.59) * mm, "end": v(2.44, -2.56) * mm});
            skLineSegment(sketch, "E906", {"start": v(2.44, -2.56) * mm, "end": v(2.31, -2.5) * mm});
            skLineSegment(sketch, "E907", {"start": v(2.31, -2.5) * mm, "end": v(2.2, -2.45) * mm});
            skLineSegment(sketch, "E908", {"start": v(2.2, -2.45) * mm, "end": v(2.14, -2.43) * mm});
            skLineSegment(sketch, "E909", {"start": v(2.14, -2.43) * mm, "end": v(2.08, -2.4) * mm});
            skLineSegment(sketch, "E910", {"start": v(2.08, -2.4) * mm, "end": v(2.02, -2.37) * mm});
            skLineSegment(sketch, "E911", {"start": v(2.02, -2.37) * mm, "end": v(1.98, -2.34) * mm});
            skLineSegment(sketch, "E912", {"start": v(1.98, -2.34) * mm, "end": v(1.93, -2.3) * mm});
            skLineSegment(sketch, "E913", {"start": v(1.93, -2.3) * mm, "end": v(1.85, -2.26) * mm});
            skLineSegment(sketch, "E914", {"start": v(1.85, -2.26) * mm, "end": v(1.76, -2.22) * mm});
            skLineSegment(sketch, "E915", {"start": v(1.76, -2.22) * mm, "end": v(1.67, -2.17) * mm});
            skLineSegment(sketch, "E916", {"start": v(1.67, -2.17) * mm, "end": v(1.58, -2.12) * mm});
            skLineSegment(sketch, "E917", {"start": v(1.58, -2.12) * mm, "end": v(1.5, -2.07) * mm});
            skLineSegment(sketch, "E918", {"start": v(1.5, -2.07) * mm, "end": v(1.43, -2.04) * mm});
            skLineSegment(sketch, "E919", {"start": v(1.43, -2.04) * mm, "end": v(1.4, -2) * mm});
            skLineSegment(sketch, "E920", {"start": v(1.4, -2) * mm, "end": v(1.37, -2) * mm});
            skLineSegment(sketch, "E921", {"start": v(1.37, -2) * mm, "end": v(1.34, -1.97) * mm});
            skLineSegment(sketch, "E922", {"start": v(1.34, -1.97) * mm, "end": v(1.31, -1.95) * mm});
            skLineSegment(sketch, "E923", {"start": v(1.31, -1.95) * mm, "end": v(1.3, -1.94) * mm});
            skLineSegment(sketch, "E924", {"start": v(1.3, -1.94) * mm, "end": v(1.26, -1.92) * mm});
            skLineSegment(sketch, "E925", {"start": v(1.26, -1.92) * mm, "end": v(1.2, -1.89) * mm});
            skLineSegment(sketch, "E926", {"start": v(1.2, -1.89) * mm, "end": v(1.13, -1.84) * mm});
            skLineSegment(sketch, "E927", {"start": v(1.13, -1.84) * mm, "end": v(1.06, -1.8) * mm});
            skLineSegment(sketch, "E928", {"start": v(1.06, -1.8) * mm, "end": v(0.94, -1.71) * mm});
            skLineSegment(sketch, "E929", {"start": v(0.94, -1.71) * mm, "end": v(0.85, -1.65) * mm});
            skLineSegment(sketch, "E930", {"start": v(0.85, -1.65) * mm, "end": v(0.77, -1.58) * mm});
            skLineSegment(sketch, "E931", {"start": v(0.77, -1.58) * mm, "end": v(0.69, -1.5) * mm});
            skLineSegment(sketch, "E932", {"start": v(0.69, -1.5) * mm, "end": v(0.67, -1.49) * mm});
            skLineSegment(sketch, "E933", {"start": v(0.67, -1.49) * mm, "end": v(0.65, -1.48) * mm});
            skLineSegment(sketch, "E934", {"start": v(0.65, -1.48) * mm, "end": v(0.64, -1.47) * mm});
            skLineSegment(sketch, "E935", {"start": v(0.64, -1.47) * mm, "end": v(0.63, -1.47) * mm});
            skLineSegment(sketch, "E936", {"start": v(0.63, -1.47) * mm, "end": v(0.63, -1.49) * mm});
            skLineSegment(sketch, "E937", {"start": v(0.63, -1.49) * mm, "end": v(0.62, -1.53) * mm});
            skLineSegment(sketch, "E938", {"start": v(0.62, -1.53) * mm, "end": v(0.62, -1.6) * mm});
            skLineSegment(sketch, "E939", {"start": v(0.62, -1.6) * mm, "end": v(0.6, -1.67) * mm});
            skLineSegment(sketch, "E940", {"start": v(0.6, -1.67) * mm, "end": v(0.57, -1.94) * mm});
            skLineSegment(sketch, "E941", {"start": v(0.57, -1.94) * mm, "end": v(0.53, -2.18) * mm});
            skLineSegment(sketch, "E942", {"start": v(0.53, -2.18) * mm, "end": v(0.49, -2.42) * mm});
            skLineSegment(sketch, "E943", {"start": v(0.49, -2.42) * mm, "end": v(0.43, -2.64) * mm});
            skLineSegment(sketch, "E944", {"start": v(0.43, -2.64) * mm, "end": v(0.37, -2.86) * mm});
            skLineSegment(sketch, "E945", {"start": v(0.37, -2.86) * mm, "end": v(0.3, -3.04) * mm});
            skLineSegment(sketch, "E946", {"start": v(0.3, -3.04) * mm, "end": v(0.22, -3.18) * mm});
            skLineSegment(sketch, "E947", {"start": v(0.22, -3.18) * mm, "end": v(0.13, -3.3) * mm});
            skLineSegment(sketch, "E948", {"start": v(0.13, -3.3) * mm, "end": v(0.06, -3.37) * mm});
            skLineSegment(sketch, "E949", {"start": v(0.06, -3.37) * mm, "end": v(0.1, -3.44) * mm});
            skLineSegment(sketch, "E950", {"start": v(0.1, -3.44) * mm, "end": v(0.18, -3.6) * mm});
            skLineSegment(sketch, "E951", {"start": v(0.18, -3.6) * mm, "end": v(0.2, -3.8) * mm});
            skLineSegment(sketch, "E952", {"start": v(0.2, -3.8) * mm, "end": v(0.15, -3.98) * mm});
            skLineSegment(sketch, "E953", {"start": v(0.15, -3.98) * mm, "end": v(0.07, -4.14) * mm});
            skLineSegment(sketch, "E954", {"start": v(0.07, -4.14) * mm, "end": v(0.03, -4.19) * mm});
            skLineSegment(sketch, "E955", {"start": v(0.03, -4.19) * mm, "end": v(0.06, -4.25) * mm});
            skLineSegment(sketch, "E956", {"start": v(0.06, -4.25) * mm, "end": v(0.11, -4.4) * mm});
            skLineSegment(sketch, "E957", {"start": v(0.11, -4.4) * mm, "end": v(0.13, -4.54) * mm});
            skLineSegment(sketch, "E958", {"start": v(0.13, -4.54) * mm, "end": v(0.12, -4.67) * mm});
            skLineSegment(sketch, "E959", {"start": v(0.12, -4.67) * mm, "end": v(0.09, -4.8) * mm});
            skLineSegment(sketch, "E960", {"start": v(0.09, -4.8) * mm, "end": v(0.03, -4.92) * mm});
            skLineSegment(sketch, "E961", {"start": v(0.03, -4.92) * mm, "end": v(-0.03, -5) * mm});
            skLineSegment(sketch, "E962", {"start": v(-0.03, -5) * mm, "end": v(-0.05, -5.03) * mm});
            skLineSegment(sketch, "E963", {"start": v(-0.05, -5.03) * mm, "end": v(-0.07, -5.05) * mm});
            skLineSegment(sketch, "E964", {"start": v(-0.07, -5.05) * mm, "end": v(-0.08, -5.07) * mm});
            skLineSegment(sketch, "E965", {"start": v(-0.08, -5.07) * mm, "end": v(-0.08, -5.07) * mm});
            skLineSegment(sketch, "E966", {"start": v(-0.08, -5.07) * mm, "end": v(-0.05, -5.09) * mm});
            skLineSegment(sketch, "E967", {"start": v(-0.05, -5.09) * mm, "end": v(-0.02, -5.1) * mm});
            skLineSegment(sketch, "E968", {"start": v(-0.02, -5.1) * mm, "end": v(0.01, -5.14) * mm});
            skLineSegment(sketch, "E969", {"start": v(0.01, -5.14) * mm, "end": v(0.03, -5.16) * mm});
            skLineSegment(sketch, "E970", {"start": v(0.03, -5.16) * mm, "end": v(0.07, -5.23) * mm});
            skLineSegment(sketch, "E971", {"start": v(0.07, -5.23) * mm, "end": v(0.09, -5.3) * mm});
            skLineSegment(sketch, "E972", {"start": v(0.09, -5.3) * mm, "end": v(0.1, -5.37) * mm});
            skLineSegment(sketch, "E973", {"start": v(0.1, -5.37) * mm, "end": v(0.1, -5.47) * mm});
            skLineSegment(sketch, "E974", {"start": v(0.1, -5.47) * mm, "end": v(0.1, -5.54) * mm});
            skLineSegment(sketch, "E975", {"start": v(0.1, -5.54) * mm, "end": v(0.1, -5.6) * mm});
            skLineSegment(sketch, "E976", {"start": v(0.1, -5.6) * mm, "end": v(0.09, -5.63) * mm});
            skLineSegment(sketch, "E977", {"start": v(0.09, -5.63) * mm, "end": v(0.07, -5.67) * mm});
            skLineSegment(sketch, "E978", {"start": v(0.07, -5.67) * mm, "end": v(0.06, -5.7) * mm});
            skLineSegment(sketch, "E979", {"start": v(0.06, -5.7) * mm, "end": v(0.04, -5.72) * mm});
            skLineSegment(sketch, "E980", {"start": v(0.04, -5.72) * mm, "end": v(0.02, -5.75) * mm});
            skLineSegment(sketch, "E981", {"start": v(0.02, -5.75) * mm, "end": v(0, -5.76) * mm});
            skLineSegment(sketch, "E982", {"start": v(0, -5.76) * mm, "end": v(-0.08, -5.8) * mm});
            skLineSegment(sketch, "E983", {"start": v(-0.08, -5.8) * mm, "end": v(-0.2, -5.84) * mm});
            skLineSegment(sketch, "E984", {"start": v(-0.2, -5.84) * mm, "end": v(-0.3, -5.85) * mm});
            skLineSegment(sketch, "E985", {"start": v(-0.3, -5.85) * mm, "end": v(-0.39, -5.84) * mm});
            skLineSegment(sketch, "E986", {"start": v(-0.19, -5.64) * mm, "end": v(-0.17, -5.63) * mm});
            skLineSegment(sketch, "E987", {"start": v(-0.17, -5.63) * mm, "end": v(-0.15, -5.62) * mm});
            skLineSegment(sketch, "E988", {"start": v(-0.15, -5.62) * mm, "end": v(-0.12, -5.6) * mm});
            skLineSegment(sketch, "E989", {"start": v(-0.12, -5.6) * mm, "end": v(-0.1, -5.56) * mm});
            skLineSegment(sketch, "E990", {"start": v(-0.1, -5.56) * mm, "end": v(-0.07, -5.5) * mm});
            skLineSegment(sketch, "E991", {"start": v(-0.07, -5.5) * mm, "end": v(-0.06, -5.45) * mm});
            skLineSegment(sketch, "E992", {"start": v(-0.06, -5.45) * mm, "end": v(-0.07, -5.4) * mm});
            skLineSegment(sketch, "E993", {"start": v(-0.07, -5.4) * mm, "end": v(-0.1, -5.32) * mm});
            skLineSegment(sketch, "E994", {"start": v(-0.1, -5.32) * mm, "end": v(-0.12, -5.28) * mm});
            skLineSegment(sketch, "E995", {"start": v(-0.12, -5.28) * mm, "end": v(-0.13, -5.25) * mm});
            skLineSegment(sketch, "E996", {"start": v(-0.13, -5.25) * mm, "end": v(-0.15, -5.23) * mm});
            skLineSegment(sketch, "E997", {"start": v(-0.15, -5.23) * mm, "end": v(-0.16, -5.22) * mm});
            skLineSegment(sketch, "E998", {"start": v(-0.16, -5.22) * mm, "end": v(-0.18, -5.2) * mm});
            skLineSegment(sketch, "E999", {"start": v(-0.18, -5.2) * mm, "end": v(-0.2, -5.2) * mm});
            skLineSegment(sketch, "E1000", {"start": v(-0.2, -5.2) * mm, "end": v(-0.22, -5.2) * mm});
            skLineSegment(sketch, "E1001", {"start": v(-0.22, -5.2) * mm, "end": v(-0.25, -5.2) * mm});
            skLineSegment(sketch, "E1002", {"start": v(-0.25, -5.2) * mm, "end": v(-0.3, -5.2) * mm});
            skLineSegment(sketch, "E1003", {"start": v(-0.3, -5.2) * mm, "end": v(-0.33, -5.2) * mm});
            skLineSegment(sketch, "E1004", {"start": v(-0.33, -5.2) * mm, "end": v(-0.34, -5.21) * mm});
            skLineSegment(sketch, "E1005", {"start": v(-0.34, -5.21) * mm, "end": v(-0.36, -5.23) * mm});
            skLineSegment(sketch, "E1006", {"start": v(-0.36, -5.23) * mm, "end": v(-0.4, -5.3) * mm});
            skLineSegment(sketch, "E1007", {"start": v(-0.4, -5.3) * mm, "end": v(-0.43, -5.38) * mm});
            skLineSegment(sketch, "E1008", {"start": v(-0.43, -5.38) * mm, "end": v(-0.44, -5.46) * mm});
            skLineSegment(sketch, "E1009", {"start": v(-0.44, -5.46) * mm, "end": v(-0.42, -5.53) * mm});
            skLineSegment(sketch, "E1010", {"start": v(-0.42, -5.53) * mm, "end": v(-0.4, -5.56) * mm});
            skLineSegment(sketch, "E1011", {"start": v(-0.4, -5.56) * mm, "end": v(-0.37, -5.6) * mm});
            skLineSegment(sketch, "E1012", {"start": v(-0.37, -5.6) * mm, "end": v(-0.31, -5.64) * mm});
            skLineSegment(sketch, "E1013", {"start": v(-0.31, -5.64) * mm, "end": v(-0.26, -5.66) * mm});
            skLineSegment(sketch, "E1014", {"start": v(-0.26, -5.66) * mm, "end": v(-0.22, -5.66) * mm});
            skLineSegment(sketch, "E1015", {"start": v(-0.22, -5.66) * mm, "end": v(-0.19, -5.64) * mm});
            skLineSegment(sketch, "E1016", {"start": v(-0.18, -4.89) * mm, "end": v(-0.15, -4.88) * mm});
            skLineSegment(sketch, "E1017", {"start": v(-0.15, -4.88) * mm, "end": v(-0.1, -4.84) * mm});
            skLineSegment(sketch, "E1018", {"start": v(-0.1, -4.84) * mm, "end": v(-0.07, -4.79) * mm});
            skLineSegment(sketch, "E1019", {"start": v(-0.07, -4.79) * mm, "end": v(-0.03, -4.72) * mm});
            skLineSegment(sketch, "E1020", {"start": v(-0.03, -4.72) * mm, "end": v(0, -4.68) * mm});
            skLineSegment(sketch, "E1021", {"start": v(0, -4.68) * mm, "end": v(0, -4.64) * mm});
            skLineSegment(sketch, "E1022", {"start": v(0, -4.64) * mm, "end": v(0, -4.61) * mm});
            skLineSegment(sketch, "E1023", {"start": v(0, -4.61) * mm, "end": v(0, -4.58) * mm});
            skLineSegment(sketch, "E1024", {"start": v(0, -4.58) * mm, "end": v(-0.02, -4.47) * mm});
            skLineSegment(sketch, "E1025", {"start": v(-0.02, -4.47) * mm, "end": v(-0.1, -4.36) * mm});
            skLineSegment(sketch, "E1026", {"start": v(-0.1, -4.36) * mm, "end": v(-0.14, -4.32) * mm});
            skLineSegment(sketch, "E1027", {"start": v(-0.14, -4.32) * mm, "end": v(-0.17, -4.3) * mm});
            skLineSegment(sketch, "E1028", {"start": v(-0.17, -4.3) * mm, "end": v(-0.2, -4.3) * mm});
            skLineSegment(sketch, "E1029", {"start": v(-0.2, -4.3) * mm, "end": v(-0.24, -4.31) * mm});
            skLineSegment(sketch, "E1030", {"start": v(-0.24, -4.31) * mm, "end": v(-0.3, -4.37) * mm});
            skLineSegment(sketch, "E1031", {"start": v(-0.3, -4.37) * mm, "end": v(-0.36, -4.46) * mm});
            skLineSegment(sketch, "E1032", {"start": v(-0.36, -4.46) * mm, "end": v(-0.39, -4.57) * mm});
            skLineSegment(sketch, "E1033", {"start": v(-0.39, -4.57) * mm, "end": v(-0.38, -4.68) * mm});
            skLineSegment(sketch, "E1034", {"start": v(-0.38, -4.68) * mm, "end": v(-0.37, -4.72) * mm});
            skLineSegment(sketch, "E1035", {"start": v(-0.37, -4.72) * mm, "end": v(-0.36, -4.77) * mm});
            skLineSegment(sketch, "E1036", {"start": v(-0.36, -4.77) * mm, "end": v(-0.34, -4.8) * mm});
            skLineSegment(sketch, "E1037", {"start": v(-0.34, -4.8) * mm, "end": v(-0.32, -4.84) * mm});
            skLineSegment(sketch, "E1038", {"start": v(-0.32, -4.84) * mm, "end": v(-0.3, -4.86) * mm});
            skLineSegment(sketch, "E1039", {"start": v(-0.3, -4.86) * mm, "end": v(-0.28, -4.88) * mm});
            skLineSegment(sketch, "E1040", {"start": v(-0.28, -4.88) * mm, "end": v(-0.25, -4.9) * mm});
            skLineSegment(sketch, "E1041", {"start": v(-0.25, -4.9) * mm, "end": v(-0.23, -4.9) * mm});
            skLineSegment(sketch, "E1042", {"start": v(-0.23, -4.9) * mm, "end": v(-0.2, -4.9) * mm});
            skLineSegment(sketch, "E1043", {"start": v(-0.2, -4.9) * mm, "end": v(-0.18, -4.89) * mm});
            skLineSegment(sketch, "E1044", {"start": v(-0.52, -4.81) * mm, "end": v(-0.53, -4.79) * mm});
            skLineSegment(sketch, "E1045", {"start": v(-0.53, -4.79) * mm, "end": v(-0.54, -4.77) * mm});
            skLineSegment(sketch, "E1046", {"start": v(-0.54, -4.77) * mm, "end": v(-0.55, -4.77) * mm});
            skLineSegment(sketch, "E1047", {"start": v(-0.55, -4.77) * mm, "end": v(-0.55, -4.77) * mm});
            skLineSegment(sketch, "E1048", {"start": v(-0.55, -4.77) * mm, "end": v(-0.54, -4.8) * mm});
            skLineSegment(sketch, "E1049", {"start": v(-0.54, -4.8) * mm, "end": v(-0.53, -4.82) * mm});
            skLineSegment(sketch, "E1050", {"start": v(-0.53, -4.82) * mm, "end": v(-0.52, -4.85) * mm});
            skLineSegment(sketch, "E1051", {"start": v(-0.52, -4.85) * mm, "end": v(-0.51, -4.86) * mm});
            skLineSegment(sketch, "E1052", {"start": v(-0.51, -4.86) * mm, "end": v(-0.51, -4.84) * mm});
            skLineSegment(sketch, "E1053", {"start": v(-0.51, -4.84) * mm, "end": v(-0.52, -4.81) * mm});
            skLineSegment(sketch, "E1054", {"start": v(-0.26, -4.09) * mm, "end": v(-0.22, -4.06) * mm});
            skLineSegment(sketch, "E1055", {"start": v(-0.22, -4.06) * mm, "end": v(-0.19, -4.03) * mm});
            skLineSegment(sketch, "E1056", {"start": v(-0.19, -4.03) * mm, "end": v(-0.15, -3.98) * mm});
            skLineSegment(sketch, "E1057", {"start": v(-0.15, -3.98) * mm, "end": v(-0.12, -3.92) * mm});
            skLineSegment(sketch, "E1058", {"start": v(-0.12, -3.92) * mm, "end": v(-0.1, -3.89) * mm});
            skLineSegment(sketch, "E1059", {"start": v(-0.1, -3.89) * mm, "end": v(-0.1, -3.86) * mm});
            skLineSegment(sketch, "E1060", {"start": v(-0.1, -3.86) * mm, "end": v(-0.1, -3.83) * mm});
            skLineSegment(sketch, "E1061", {"start": v(-0.1, -3.83) * mm, "end": v(-0.1, -3.8) * mm});
            skLineSegment(sketch, "E1062", {"start": v(-0.1, -3.8) * mm, "end": v(-0.13, -3.68) * mm});
            skLineSegment(sketch, "E1063", {"start": v(-0.13, -3.68) * mm, "end": v(-0.22, -3.57) * mm});
            skLineSegment(sketch, "E1064", {"start": v(-0.22, -3.57) * mm, "end": v(-0.24, -3.55) * mm});
            skLineSegment(sketch, "E1065", {"start": v(-0.24, -3.55) * mm, "end": v(-0.26, -3.54) * mm});
            skLineSegment(sketch, "E1066", {"start": v(-0.26, -3.54) * mm, "end": v(-0.29, -3.53) * mm});
            skLineSegment(sketch, "E1067", {"start": v(-0.29, -3.53) * mm, "end": v(-0.32, -3.54) * mm});
            skLineSegment(sketch, "E1068", {"start": v(-0.32, -3.54) * mm, "end": v(-0.42, -3.58) * mm});
            skLineSegment(sketch, "E1069", {"start": v(-0.42, -3.58) * mm, "end": v(-0.5, -3.66) * mm});
            skLineSegment(sketch, "E1070", {"start": v(-0.5, -3.66) * mm, "end": v(-0.56, -3.78) * mm});
            skLineSegment(sketch, "E1071", {"start": v(-0.56, -3.78) * mm, "end": v(-0.58, -3.92) * mm});
            skLineSegment(sketch, "E1072", {"start": v(-0.58, -3.92) * mm, "end": v(-0.58, -3.96) * mm});
            skLineSegment(sketch, "E1073", {"start": v(-0.58, -3.96) * mm, "end": v(-0.58, -3.98) * mm});
            skLineSegment(sketch, "E1074", {"start": v(-0.58, -3.98) * mm, "end": v(-0.57, -4) * mm});
            skLineSegment(sketch, "E1075", {"start": v(-0.57, -4) * mm, "end": v(-0.55, -4.03) * mm});
            skLineSegment(sketch, "E1076", {"start": v(-0.55, -4.03) * mm, "end": v(-0.52, -4.06) * mm});
            skLineSegment(sketch, "E1077", {"start": v(-0.52, -4.06) * mm, "end": v(-0.5, -4.08) * mm});
            skLineSegment(sketch, "E1078", {"start": v(-0.5, -4.08) * mm, "end": v(-0.46, -4.1) * mm});
            skLineSegment(sketch, "E1079", {"start": v(-0.46, -4.1) * mm, "end": v(-0.42, -4.1) * mm});
            skLineSegment(sketch, "E1080", {"start": v(-0.42, -4.1) * mm, "end": v(-0.37, -4.11) * mm});
            skLineSegment(sketch, "E1081", {"start": v(-0.37, -4.11) * mm, "end": v(-0.34, -4.11) * mm});
            skLineSegment(sketch, "E1082", {"start": v(-0.34, -4.11) * mm, "end": v(-0.3, -4.1) * mm});
            skLineSegment(sketch, "E1083", {"start": v(-0.3, -4.1) * mm, "end": v(-0.26, -4.09) * mm});
            skLineSegment(sketch, "E1084", {"start": v(-0.08, -3.08) * mm, "end": v(-0.06, -3.06) * mm});
            skLineSegment(sketch, "E1085", {"start": v(-0.06, -3.06) * mm, "end": v(-0.03, -3.04) * mm});
            skLineSegment(sketch, "E1086", {"start": v(-0.03, -3.04) * mm, "end": v(0, -3.02) * mm});
            skLineSegment(sketch, "E1087", {"start": v(0, -3.02) * mm, "end": v(0.02, -2.99) * mm});
            skLineSegment(sketch, "E1088", {"start": v(0.02, -2.99) * mm, "end": v(0.07, -2.93) * mm});
            skLineSegment(sketch, "E1089", {"start": v(0.07, -2.93) * mm, "end": v(0.11, -2.86) * mm});
            skLineSegment(sketch, "E1090", {"start": v(0.11, -2.86) * mm, "end": v(0.15, -2.78) * mm});
            skLineSegment(sketch, "E1091", {"start": v(0.15, -2.78) * mm, "end": v(0.19, -2.68) * mm});
            skLineSegment(sketch, "E1092", {"start": v(0.19, -2.68) * mm, "end": v(0.23, -2.57) * mm});
            skLineSegment(sketch, "E1093", {"start": v(0.23, -2.57) * mm, "end": v(0.26, -2.43) * mm});
            skLineSegment(sketch, "E1094", {"start": v(0.26, -2.43) * mm, "end": v(0.3, -2.26) * mm});
            skLineSegment(sketch, "E1095", {"start": v(0.3, -2.26) * mm, "end": v(0.35, -2.06) * mm});
            skLineSegment(sketch, "E1096", {"start": v(0.35, -2.06) * mm, "end": v(0.36, -1.99) * mm});
            skLineSegment(sketch, "E1097", {"start": v(0.36, -1.99) * mm, "end": v(0.38, -1.92) * mm});
            skLineSegment(sketch, "E1098", {"start": v(0.38, -1.92) * mm, "end": v(0.39, -1.87) * mm});
            skLineSegment(sketch, "E1099", {"start": v(0.39, -1.87) * mm, "end": v(0.4, -1.85) * mm});
            skLineSegment(sketch, "E1100", {"start": v(0.4, -1.85) * mm, "end": v(0.4, -1.84) * mm});
            skLineSegment(sketch, "E1101", {"start": v(0.4, -1.84) * mm, "end": v(0.4, -1.84) * mm});
            skLineSegment(sketch, "E1102", {"start": v(0.4, -1.84) * mm, "end": v(0.39, -1.83) * mm});
            skLineSegment(sketch, "E1103", {"start": v(0.39, -1.83) * mm, "end": v(0.37, -1.83) * mm});
            skLineSegment(sketch, "E1104", {"start": v(0.37, -1.83) * mm, "end": v(0.35, -1.83) * mm});
            skLineSegment(sketch, "E1105", {"start": v(0.35, -1.83) * mm, "end": v(0.32, -1.83) * mm});
            skLineSegment(sketch, "E1106", {"start": v(0.32, -1.83) * mm, "end": v(0.28, -1.83) * mm});
            skLineSegment(sketch, "E1107", {"start": v(0.28, -1.83) * mm, "end": v(0.22, -1.83) * mm});
            skLineSegment(sketch, "E1108", {"start": v(0.22, -1.83) * mm, "end": v(0.04, -1.83) * mm});
            skLineSegment(sketch, "E1109", {"start": v(0.04, -1.83) * mm, "end": v(-0.04, -1.89) * mm});
            skLineSegment(sketch, "E1110", {"start": v(-0.04, -1.89) * mm, "end": v(-0.09, -1.92) * mm});
            skLineSegment(sketch, "E1111", {"start": v(-0.09, -1.92) * mm, "end": v(-0.14, -1.94) * mm});
            skLineSegment(sketch, "E1112", {"start": v(-0.14, -1.94) * mm, "end": v(-0.19, -1.96) * mm});
            skLineSegment(sketch, "E1113", {"start": v(-0.19, -1.96) * mm, "end": v(-0.25, -1.99) * mm});
            skLineSegment(sketch, "E1114", {"start": v(-0.25, -1.99) * mm, "end": v(-0.33, -2) * mm});
            skLineSegment(sketch, "E1115", {"start": v(-0.33, -2) * mm, "end": v(-0.38, -2.02) * mm});
            skLineSegment(sketch, "E1116", {"start": v(-0.38, -2.02) * mm, "end": v(-0.45, -2.03) * mm});
            skLineSegment(sketch, "E1117", {"start": v(-0.45, -2.03) * mm, "end": v(-0.56, -2.03) * mm});
            skLineSegment(sketch, "E1118", {"start": v(-0.56, -2.03) * mm, "end": v(-0.63, -2.03) * mm});
            skLineSegment(sketch, "E1119", {"start": v(-0.63, -2.03) * mm, "end": v(-0.68, -2.03) * mm});
            skLineSegment(sketch, "E1120", {"start": v(-0.68, -2.03) * mm, "end": v(-0.72, -2.03) * mm});
            skLineSegment(sketch, "E1121", {"start": v(-0.72, -2.03) * mm, "end": v(-0.74, -2.03) * mm});
            skLineSegment(sketch, "E1122", {"start": v(-0.74, -2.03) * mm, "end": v(-0.73, -2.04) * mm});
            skLineSegment(sketch, "E1123", {"start": v(-0.73, -2.04) * mm, "end": v(-0.72, -2.08) * mm});
            skLineSegment(sketch, "E1124", {"start": v(-0.72, -2.08) * mm, "end": v(-0.7, -2.17) * mm});
            skLineSegment(sketch, "E1125", {"start": v(-0.7, -2.17) * mm, "end": v(-0.66, -2.28) * mm});
            skLineSegment(sketch, "E1126", {"start": v(-0.66, -2.28) * mm, "end": v(-0.61, -2.4) * mm});
            skLineSegment(sketch, "E1127", {"start": v(-0.61, -2.4) * mm, "end": v(-0.56, -2.52) * mm});
            skLineSegment(sketch, "E1128", {"start": v(-0.56, -2.52) * mm, "end": v(-0.51, -2.63) * mm});
            skLineSegment(sketch, "E1129", {"start": v(-0.51, -2.63) * mm, "end": v(-0.46, -2.74) * mm});
            skLineSegment(sketch, "E1130", {"start": v(-0.46, -2.74) * mm, "end": v(-0.42, -2.82) * mm});
            skLineSegment(sketch, "E1131", {"start": v(-0.42, -2.82) * mm, "end": v(-0.39, -2.88) * mm});
            skLineSegment(sketch, "E1132", {"start": v(-0.39, -2.88) * mm, "end": v(-0.36, -2.92) * mm});
            skLineSegment(sketch, "E1133", {"start": v(-0.36, -2.92) * mm, "end": v(-0.33, -2.96) * mm});
            skLineSegment(sketch, "E1134", {"start": v(-0.33, -2.96) * mm, "end": v(-0.32, -2.98) * mm});
            skLineSegment(sketch, "E1135", {"start": v(-0.32, -2.98) * mm, "end": v(-0.3, -3) * mm});
            skLineSegment(sketch, "E1136", {"start": v(-0.3, -3) * mm, "end": v(-0.3, -3.02) * mm});
            skLineSegment(sketch, "E1137", {"start": v(-0.3, -3.02) * mm, "end": v(-0.27, -3.05) * mm});
            skLineSegment(sketch, "E1138", {"start": v(-0.27, -3.05) * mm, "end": v(-0.24, -3.08) * mm});
            skLineSegment(sketch, "E1139", {"start": v(-0.24, -3.08) * mm, "end": v(-0.22, -3.1) * mm});
            skLineSegment(sketch, "E1140", {"start": v(-0.22, -3.1) * mm, "end": v(-0.2, -3.1) * mm});
            skLineSegment(sketch, "E1141", {"start": v(-0.2, -3.1) * mm, "end": v(-0.17, -3.1) * mm});
            skLineSegment(sketch, "E1142", {"start": v(-0.17, -3.1) * mm, "end": v(-0.13, -3.1) * mm});
            skLineSegment(sketch, "E1143", {"start": v(-0.13, -3.1) * mm, "end": v(-0.08, -3.08) * mm});
            skLineSegment(sketch, "E1144", {"start": v(3.94, -2.73) * mm, "end": v(3.95, -2.72) * mm});
            skLineSegment(sketch, "E1145", {"start": v(3.95, -2.72) * mm, "end": v(3.95, -2.7) * mm});
            skLineSegment(sketch, "E1146", {"start": v(3.95, -2.7) * mm, "end": v(3.94, -2.68) * mm});
            skLineSegment(sketch, "E1147", {"start": v(3.94, -2.68) * mm, "end": v(3.92, -2.62) * mm});
            skLineSegment(sketch, "E1148", {"start": v(3.92, -2.62) * mm, "end": v(3.88, -2.51) * mm});
            skLineSegment(sketch, "E1149", {"start": v(3.88, -2.51) * mm, "end": v(3.82, -2.4) * mm});
            skLineSegment(sketch, "E1150", {"start": v(3.82, -2.4) * mm, "end": v(3.77, -2.29) * mm});
            skLineSegment(sketch, "E1151", {"start": v(3.77, -2.29) * mm, "end": v(3.72, -2.21) * mm});
            skLineSegment(sketch, "E1152", {"start": v(3.72, -2.21) * mm, "end": v(3.7, -2.19) * mm});
            skLineSegment(sketch, "E1153", {"start": v(3.7, -2.19) * mm, "end": v(3.67, -2.15) * mm});
            skLineSegment(sketch, "E1154", {"start": v(3.67, -2.15) * mm, "end": v(3.65, -2.11) * mm});
            skLineSegment(sketch, "E1155", {"start": v(3.65, -2.11) * mm, "end": v(3.62, -2.08) * mm});
            skLineSegment(sketch, "E1156", {"start": v(3.62, -2.08) * mm, "end": v(3.55, -1.99) * mm});
            skLineSegment(sketch, "E1157", {"start": v(3.55, -1.99) * mm, "end": v(3.47, -1.9) * mm});
            skLineSegment(sketch, "E1158", {"start": v(3.47, -1.9) * mm, "end": v(3.36, -1.79) * mm});
            skLineSegment(sketch, "E1159", {"start": v(3.36, -1.79) * mm, "end": v(3.2, -1.66) * mm});
            skLineSegment(sketch, "E1160", {"start": v(3.2, -1.66) * mm, "end": v(2.94, -1.44) * mm});
            skLineSegment(sketch, "E1161", {"start": v(2.94, -1.44) * mm, "end": v(2.65, -1.25) * mm});
            skLineSegment(sketch, "E1162", {"start": v(2.65, -1.25) * mm, "end": v(2.34, -1.07) * mm});
            skLineSegment(sketch, "E1163", {"start": v(2.34, -1.07) * mm, "end": v(2.03, -0.93) * mm});
            skLineSegment(sketch, "E1164", {"start": v(2.03, -0.93) * mm, "end": v(1.84, -0.86) * mm});
            skLineSegment(sketch, "E1165", {"start": v(1.84, -0.86) * mm, "end": v(1.6, -0.8) * mm});
            skLineSegment(sketch, "E1166", {"start": v(1.6, -0.8) * mm, "end": v(1.32, -0.75) * mm});
            skLineSegment(sketch, "E1167", {"start": v(1.32, -0.75) * mm, "end": v(1.03, -0.7) * mm});
            skLineSegment(sketch, "E1168", {"start": v(1.03, -0.7) * mm, "end": v(0.91, -0.7) * mm});
            skLineSegment(sketch, "E1169", {"start": v(0.91, -0.7) * mm, "end": v(0.83, -0.69) * mm});
            skLineSegment(sketch, "E1170", {"start": v(0.83, -0.69) * mm, "end": v(0.77, -0.68) * mm});
            skLineSegment(sketch, "E1171", {"start": v(0.77, -0.68) * mm, "end": v(0.73, -0.68) * mm});
            skLineSegment(sketch, "E1172", {"start": v(0.73, -0.68) * mm, "end": v(0.7, -0.68) * mm});
            skLineSegment(sketch, "E1173", {"start": v(0.7, -0.68) * mm, "end": v(0.7, -0.68) * mm});
            skLineSegment(sketch, "E1174", {"start": v(0.7, -0.68) * mm, "end": v(0.69, -0.68) * mm});
            skLineSegment(sketch, "E1175", {"start": v(0.69, -0.68) * mm, "end": v(0.69, -0.69) * mm});
            skLineSegment(sketch, "E1176", {"start": v(0.69, -0.69) * mm, "end": v(0.68, -0.71) * mm});
            skLineSegment(sketch, "E1177", {"start": v(0.68, -0.71) * mm, "end": v(0.68, -0.76) * mm});
            skLineSegment(sketch, "E1178", {"start": v(0.68, -0.76) * mm, "end": v(0.67, -0.83) * mm});
            skLineSegment(sketch, "E1179", {"start": v(0.67, -0.83) * mm, "end": v(0.67, -0.91) * mm});
            skLineSegment(sketch, "E1180", {"start": v(0.67, -0.91) * mm, "end": v(0.67, -1.12) * mm});
            skLineSegment(sketch, "E1181", {"start": v(0.67, -1.12) * mm, "end": v(0.72, -1.18) * mm});
            skLineSegment(sketch, "E1182", {"start": v(0.72, -1.18) * mm, "end": v(0.73, -1.2) * mm});
            skLineSegment(sketch, "E1183", {"start": v(0.73, -1.2) * mm, "end": v(0.75, -1.23) * mm});
            skLineSegment(sketch, "E1184", {"start": v(0.75, -1.23) * mm, "end": v(0.77, -1.24) * mm});
            skLineSegment(sketch, "E1185", {"start": v(0.77, -1.24) * mm, "end": v(0.77, -1.25) * mm});
            skLineSegment(sketch, "E1186", {"start": v(0.77, -1.25) * mm, "end": v(0.78, -1.26) * mm});
            skLineSegment(sketch, "E1187", {"start": v(0.78, -1.26) * mm, "end": v(0.8, -1.28) * mm});
            skLineSegment(sketch, "E1188", {"start": v(0.8, -1.28) * mm, "end": v(0.82, -1.3) * mm});
            skLineSegment(sketch, "E1189", {"start": v(0.82, -1.3) * mm, "end": v(0.84, -1.34) * mm});
            skLineSegment(sketch, "E1190", {"start": v(0.84, -1.34) * mm, "end": v(0.86, -1.37) * mm});
            skLineSegment(sketch, "E1191", {"start": v(0.86, -1.37) * mm, "end": v(0.89, -1.4) * mm});
            skLineSegment(sketch, "E1192", {"start": v(0.89, -1.4) * mm, "end": v(0.92, -1.43) * mm});
            skLineSegment(sketch, "E1193", {"start": v(0.92, -1.43) * mm, "end": v(0.96, -1.47) * mm});
            skLineSegment(sketch, "E1194", {"start": v(0.96, -1.47) * mm, "end": v(1.02, -1.52) * mm});
            skLineSegment(sketch, "E1195", {"start": v(1.02, -1.52) * mm, "end": v(1.1, -1.58) * mm});
            skLineSegment(sketch, "E1196", {"start": v(1.1, -1.58) * mm, "end": v(1.2, -1.66) * mm});
            skLineSegment(sketch, "E1197", {"start": v(1.2, -1.66) * mm, "end": v(1.31, -1.76) * mm});
            skLineSegment(sketch, "E1198", {"start": v(1.31, -1.76) * mm, "end": v(1.46, -1.86) * mm});
            skLineSegment(sketch, "E1199", {"start": v(1.46, -1.86) * mm, "end": v(1.65, -1.98) * mm});
            skLineSegment(sketch, "E1200", {"start": v(1.65, -1.98) * mm, "end": v(1.86, -2.1) * mm});
            skLineSegment(sketch, "E1201", {"start": v(1.86, -2.1) * mm, "end": v(2.1, -2.23) * mm});
            skLineSegment(sketch, "E1202", {"start": v(2.1, -2.23) * mm, "end": v(2.31, -2.33) * mm});
            skLineSegment(sketch, "E1203", {"start": v(2.31, -2.33) * mm, "end": v(2.5, -2.4) * mm});
            skLineSegment(sketch, "E1204", {"start": v(2.5, -2.4) * mm, "end": v(2.65, -2.47) * mm});
            skLineSegment(sketch, "E1205", {"start": v(2.65, -2.47) * mm, "end": v(2.77, -2.5) * mm});
            skLineSegment(sketch, "E1206", {"start": v(2.77, -2.5) * mm, "end": v(2.83, -2.53) * mm});
            skLineSegment(sketch, "E1207", {"start": v(2.83, -2.53) * mm, "end": v(2.9, -2.55) * mm});
            skLineSegment(sketch, "E1208", {"start": v(2.9, -2.55) * mm, "end": v(2.99, -2.57) * mm});
            skLineSegment(sketch, "E1209", {"start": v(2.99, -2.57) * mm, "end": v(3.06, -2.59) * mm});
            skLineSegment(sketch, "E1210", {"start": v(3.06, -2.59) * mm, "end": v(3.21, -2.63) * mm});
            skLineSegment(sketch, "E1211", {"start": v(3.21, -2.63) * mm, "end": v(3.35, -2.66) * mm});
            skLineSegment(sketch, "E1212", {"start": v(3.35, -2.66) * mm, "end": v(3.5, -2.68) * mm});
            skLineSegment(sketch, "E1213", {"start": v(3.5, -2.68) * mm, "end": v(3.68, -2.71) * mm});
            skLineSegment(sketch, "E1214", {"start": v(3.68, -2.71) * mm, "end": v(3.77, -2.72) * mm});
            skLineSegment(sketch, "E1215", {"start": v(3.77, -2.72) * mm, "end": v(3.83, -2.73) * mm});
            skLineSegment(sketch, "E1216", {"start": v(3.83, -2.73) * mm, "end": v(3.87, -2.74) * mm});
            skLineSegment(sketch, "E1217", {"start": v(3.87, -2.74) * mm, "end": v(3.9, -2.74) * mm});
            skLineSegment(sketch, "E1218", {"start": v(3.9, -2.74) * mm, "end": v(3.92, -2.74) * mm});
            skLineSegment(sketch, "E1219", {"start": v(3.92, -2.74) * mm, "end": v(3.93, -2.74) * mm});
            skLineSegment(sketch, "E1220", {"start": v(3.93, -2.74) * mm, "end": v(3.93, -2.74) * mm});
            skLineSegment(sketch, "E1221", {"start": v(3.93, -2.74) * mm, "end": v(3.94, -2.73) * mm});
            skLineSegment(sketch, "E1222", {"start": v(4.57, -2.72) * mm, "end": v(4.81, -2.68) * mm});
            skLineSegment(sketch, "E1223", {"start": v(4.81, -2.68) * mm, "end": v(5.02, -2.65) * mm});
            skLineSegment(sketch, "E1224", {"start": v(5.02, -2.65) * mm, "end": v(5.22, -2.6) * mm});
            skLineSegment(sketch, "E1225", {"start": v(5.22, -2.6) * mm, "end": v(5.41, -2.55) * mm});
            skLineSegment(sketch, "E1226", {"start": v(5.41, -2.55) * mm, "end": v(5.53, -2.52) * mm});
            skLineSegment(sketch, "E1227", {"start": v(5.53, -2.52) * mm, "end": v(5.62, -2.5) * mm});
            skLineSegment(sketch, "E1228", {"start": v(5.62, -2.5) * mm, "end": v(5.7, -2.47) * mm});
            skLineSegment(sketch, "E1229", {"start": v(5.7, -2.47) * mm, "end": v(5.76, -2.46) * mm});
            skLineSegment(sketch, "E1230", {"start": v(5.76, -2.46) * mm, "end": v(5.81, -2.44) * mm});
            skLineSegment(sketch, "E1231", {"start": v(5.81, -2.44) * mm, "end": v(5.86, -2.42) * mm});
            skLineSegment(sketch, "E1232", {"start": v(5.86, -2.42) * mm, "end": v(5.9, -2.4) * mm});
            skLineSegment(sketch, "E1233", {"start": v(5.9, -2.4) * mm, "end": v(5.96, -2.39) * mm});
            skLineSegment(sketch, "E1234", {"start": v(5.96, -2.39) * mm, "end": v(6.11, -2.33) * mm});
            skLineSegment(sketch, "E1235", {"start": v(6.11, -2.33) * mm, "end": v(6.25, -2.28) * mm});
            skLineSegment(sketch, "E1236", {"start": v(6.25, -2.28) * mm, "end": v(6.35, -2.24) * mm});
            skLineSegment(sketch, "E1237", {"start": v(6.35, -2.24) * mm, "end": v(6.39, -2.23) * mm});
            skLineSegment(sketch, "E1238", {"start": v(6.39, -2.23) * mm, "end": v(6.39, -2.22) * mm});
            skLineSegment(sketch, "E1239", {"start": v(6.39, -2.22) * mm, "end": v(6.37, -2.2) * mm});
            skLineSegment(sketch, "E1240", {"start": v(6.37, -2.2) * mm, "end": v(6.35, -2.17) * mm});
            skLineSegment(sketch, "E1241", {"start": v(6.35, -2.17) * mm, "end": v(6.32, -2.14) * mm});
            skLineSegment(sketch, "E1242", {"start": v(6.32, -2.14) * mm, "end": v(6.29, -2.1) * mm});
            skLineSegment(sketch, "E1243", {"start": v(6.29, -2.1) * mm, "end": v(6.26, -2.07) * mm});
            skLineSegment(sketch, "E1244", {"start": v(6.26, -2.07) * mm, "end": v(6.23, -2.04) * mm});
            skLineSegment(sketch, "E1245", {"start": v(6.23, -2.04) * mm, "end": v(6.21, -2.01) * mm});
            skLineSegment(sketch, "E1246", {"start": v(6.21, -2.01) * mm, "end": v(6.14, -1.93) * mm});
            skLineSegment(sketch, "E1247", {"start": v(6.14, -1.93) * mm, "end": v(6.02, -1.83) * mm});
            skLineSegment(sketch, "E1248", {"start": v(6.02, -1.83) * mm, "end": v(5.87, -1.7) * mm});
            skLineSegment(sketch, "E1249", {"start": v(5.87, -1.7) * mm, "end": v(5.7, -1.59) * mm});
            skLineSegment(sketch, "E1250", {"start": v(5.7, -1.59) * mm, "end": v(5.67, -1.57) * mm});
            skLineSegment(sketch, "E1251", {"start": v(5.67, -1.57) * mm, "end": v(5.64, -1.54) * mm});
            skLineSegment(sketch, "E1252", {"start": v(5.64, -1.54) * mm, "end": v(5.6, -1.51) * mm});
            skLineSegment(sketch, "E1253", {"start": v(5.6, -1.51) * mm, "end": v(5.57, -1.5) * mm});
            skLineSegment(sketch, "E1254", {"start": v(5.57, -1.5) * mm, "end": v(5.5, -1.45) * mm});
            skLineSegment(sketch, "E1255", {"start": v(5.5, -1.45) * mm, "end": v(5.42, -1.42) * mm});
            skLineSegment(sketch, "E1256", {"start": v(5.42, -1.42) * mm, "end": v(5.33, -1.4) * mm});
            skLineSegment(sketch, "E1257", {"start": v(5.33, -1.4) * mm, "end": v(5.24, -1.38) * mm});
            skLineSegment(sketch, "E1258", {"start": v(5.24, -1.38) * mm, "end": v(5.18, -1.38) * mm});
            skLineSegment(sketch, "E1259", {"start": v(5.18, -1.38) * mm, "end": v(5.12, -1.38) * mm});
            skLineSegment(sketch, "E1260", {"start": v(5.12, -1.38) * mm, "end": v(5.04, -1.4) * mm});
            skLineSegment(sketch, "E1261", {"start": v(5.04, -1.4) * mm, "end": v(4.94, -1.4) * mm});
            skLineSegment(sketch, "E1262", {"start": v(4.94, -1.4) * mm, "end": v(4.83, -1.42) * mm});
            skLineSegment(sketch, "E1263", {"start": v(4.83, -1.42) * mm, "end": v(4.73, -1.43) * mm});
            skLineSegment(sketch, "E1264", {"start": v(4.73, -1.43) * mm, "end": v(4.63, -1.44) * mm});
            skLineSegment(sketch, "E1265", {"start": v(4.63, -1.44) * mm, "end": v(4.5, -1.44) * mm});
            skLineSegment(sketch, "E1266", {"start": v(4.5, -1.44) * mm, "end": v(4.42, -1.44) * mm});
            skLineSegment(sketch, "E1267", {"start": v(4.42, -1.44) * mm, "end": v(4.34, -1.44) * mm});
            skLineSegment(sketch, "E1268", {"start": v(4.34, -1.44) * mm, "end": v(4.28, -1.43) * mm});
            skLineSegment(sketch, "E1269", {"start": v(4.28, -1.43) * mm, "end": v(4.23, -1.42) * mm});
            skLineSegment(sketch, "E1270", {"start": v(4.23, -1.42) * mm, "end": v(4.17, -1.4) * mm});
            skLineSegment(sketch, "E1271", {"start": v(4.17, -1.4) * mm, "end": v(4.12, -1.4) * mm});
            skLineSegment(sketch, "E1272", {"start": v(4.12, -1.4) * mm, "end": v(4.06, -1.37) * mm});
            skLineSegment(sketch, "E1273", {"start": v(4.06, -1.37) * mm, "end": v(3.98, -1.34) * mm});
            skLineSegment(sketch, "E1274", {"start": v(3.98, -1.34) * mm, "end": v(3.92, -1.3) * mm});
            skLineSegment(sketch, "E1275", {"start": v(3.92, -1.3) * mm, "end": v(3.84, -1.28) * mm});
            skLineSegment(sketch, "E1276", {"start": v(3.84, -1.28) * mm, "end": v(3.75, -1.24) * mm});
            skLineSegment(sketch, "E1277", {"start": v(3.75, -1.24) * mm, "end": v(3.67, -1.22) * mm});
            skLineSegment(sketch, "E1278", {"start": v(3.67, -1.22) * mm, "end": v(3.58, -1.18) * mm});
            skLineSegment(sketch, "E1279", {"start": v(3.58, -1.18) * mm, "end": v(3.5, -1.16) * mm});
            skLineSegment(sketch, "E1280", {"start": v(3.5, -1.16) * mm, "end": v(3.43, -1.15) * mm});
            skLineSegment(sketch, "E1281", {"start": v(3.43, -1.15) * mm, "end": v(3.33, -1.14) * mm});
            skLineSegment(sketch, "E1282", {"start": v(3.33, -1.14) * mm, "end": v(3.2, -1.13) * mm});
            skLineSegment(sketch, "E1283", {"start": v(3.2, -1.13) * mm, "end": v(3.09, -1.12) * mm});
            skLineSegment(sketch, "E1284", {"start": v(3.09, -1.12) * mm, "end": v(3, -1.13) * mm});
            skLineSegment(sketch, "E1285", {"start": v(3, -1.13) * mm, "end": v(2.98, -1.14) * mm});
            skLineSegment(sketch, "E1286", {"start": v(2.98, -1.14) * mm, "end": v(2.99, -1.15) * mm});
            skLineSegment(sketch, "E1287", {"start": v(2.99, -1.15) * mm, "end": v(3.02, -1.18) * mm});
            skLineSegment(sketch, "E1288", {"start": v(3.02, -1.18) * mm, "end": v(3.06, -1.21) * mm});
            skLineSegment(sketch, "E1289", {"start": v(3.06, -1.21) * mm, "end": v(3.11, -1.25) * mm});
            skLineSegment(sketch, "E1290", {"start": v(3.11, -1.25) * mm, "end": v(3.24, -1.36) * mm});
            skLineSegment(sketch, "E1291", {"start": v(3.24, -1.36) * mm, "end": v(3.38, -1.48) * mm});
            skLineSegment(sketch, "E1292", {"start": v(3.38, -1.48) * mm, "end": v(3.52, -1.6) * mm});
            skLineSegment(sketch, "E1293", {"start": v(3.52, -1.6) * mm, "end": v(3.66, -1.74) * mm});
            skLineSegment(sketch, "E1294", {"start": v(3.66, -1.74) * mm, "end": v(3.73, -1.81) * mm});
            skLineSegment(sketch, "E1295", {"start": v(3.73, -1.81) * mm, "end": v(3.78, -1.88) * mm});
            skLineSegment(sketch, "E1296", {"start": v(3.78, -1.88) * mm, "end": v(3.84, -1.95) * mm});
            skLineSegment(sketch, "E1297", {"start": v(3.84, -1.95) * mm, "end": v(3.9, -2.04) * mm});
            skLineSegment(sketch, "E1298", {"start": v(3.9, -2.04) * mm, "end": v(4.03, -2.24) * mm});
            skLineSegment(sketch, "E1299", {"start": v(4.03, -2.24) * mm, "end": v(4.12, -2.4) * mm});
            skLineSegment(sketch, "E1300", {"start": v(4.12, -2.4) * mm, "end": v(4.18, -2.53) * mm});
            skLineSegment(sketch, "E1301", {"start": v(4.18, -2.53) * mm, "end": v(4.21, -2.64) * mm});
            skLineSegment(sketch, "E1302", {"start": v(4.21, -2.64) * mm, "end": v(4.22, -2.67) * mm});
            skLineSegment(sketch, "E1303", {"start": v(4.22, -2.67) * mm, "end": v(4.23, -2.7) * mm});
            skLineSegment(sketch, "E1304", {"start": v(4.23, -2.7) * mm, "end": v(4.23, -2.71) * mm});
            skLineSegment(sketch, "E1305", {"start": v(4.23, -2.71) * mm, "end": v(4.24, -2.72) * mm});
            skLineSegment(sketch, "E1306", {"start": v(4.24, -2.72) * mm, "end": v(4.27, -2.73) * mm});
            skLineSegment(sketch, "E1307", {"start": v(4.27, -2.73) * mm, "end": v(4.35, -2.73) * mm});
            skLineSegment(sketch, "E1308", {"start": v(4.35, -2.73) * mm, "end": v(4.46, -2.73) * mm});
            skLineSegment(sketch, "E1309", {"start": v(4.46, -2.73) * mm, "end": v(4.57, -2.72) * mm});
            skLineSegment(sketch, "E1310", {"start": v(-5, -2.2) * mm, "end": v(-4.97, -2.18) * mm});
            skLineSegment(sketch, "E1311", {"start": v(-4.97, -2.18) * mm, "end": v(-4.92, -2.14) * mm});
            skLineSegment(sketch, "E1312", {"start": v(-4.92, -2.14) * mm, "end": v(-4.87, -2.08) * mm});
            skLineSegment(sketch, "E1313", {"start": v(-4.87, -2.08) * mm, "end": v(-4.8, -2.01) * mm});
            skLineSegment(sketch, "E1314", {"start": v(-4.8, -2.01) * mm, "end": v(-4.74, -1.93) * mm});
            skLineSegment(sketch, "E1315", {"start": v(-4.74, -1.93) * mm, "end": v(-4.67, -1.85) * mm});
            skLineSegment(sketch, "E1316", {"start": v(-4.67, -1.85) * mm, "end": v(-4.6, -1.76) * mm});
            skLineSegment(sketch, "E1317", {"start": v(-4.6, -1.76) * mm, "end": v(-4.53, -1.7) * mm});
            skLineSegment(sketch, "E1318", {"start": v(-4.53, -1.7) * mm, "end": v(-4.46, -1.63) * mm});
            skLineSegment(sketch, "E1319", {"start": v(-4.46, -1.63) * mm, "end": v(-4.4, -1.56) * mm});
            skLineSegment(sketch, "E1320", {"start": v(-4.4, -1.56) * mm, "end": v(-4.34, -1.5) * mm});
            skLineSegment(sketch, "E1321", {"start": v(-4.34, -1.5) * mm, "end": v(-4.29, -1.44) * mm});
            skLineSegment(sketch, "E1322", {"start": v(-4.29, -1.44) * mm, "end": v(-4.24, -1.4) * mm});
            skLineSegment(sketch, "E1323", {"start": v(-4.24, -1.4) * mm, "end": v(-4.18, -1.34) * mm});
            skLineSegment(sketch, "E1324", {"start": v(-4.18, -1.34) * mm, "end": v(-4.12, -1.28) * mm});
            skLineSegment(sketch, "E1325", {"start": v(-4.12, -1.28) * mm, "end": v(-4.06, -1.23) * mm});
            skLineSegment(sketch, "E1326", {"start": v(-4.06, -1.23) * mm, "end": v(-4, -1.19) * mm});
            skLineSegment(sketch, "E1327", {"start": v(-4, -1.19) * mm, "end": v(-3.95, -1.14) * mm});
            skLineSegment(sketch, "E1328", {"start": v(-3.95, -1.14) * mm, "end": v(-3.9, -1.1) * mm});
            skLineSegment(sketch, "E1329", {"start": v(-3.9, -1.1) * mm, "end": v(-3.85, -1.06) * mm});
            skLineSegment(sketch, "E1330", {"start": v(-3.85, -1.06) * mm, "end": v(-3.82, -1.02) * mm});
            skLineSegment(sketch, "E1331", {"start": v(-3.82, -1.02) * mm, "end": v(-3.78, -1) * mm});
            skLineSegment(sketch, "E1332", {"start": v(-3.78, -1) * mm, "end": v(-3.75, -0.96) * mm});
            skLineSegment(sketch, "E1333", {"start": v(-3.75, -0.96) * mm, "end": v(-3.72, -0.94) * mm});
            skLineSegment(sketch, "E1334", {"start": v(-3.72, -0.94) * mm, "end": v(-3.7, -0.92) * mm});
            skLineSegment(sketch, "E1335", {"start": v(-3.7, -0.92) * mm, "end": v(-3.69, -0.9) * mm});
            skLineSegment(sketch, "E1336", {"start": v(-3.69, -0.9) * mm, "end": v(-3.67, -0.9) * mm});
            skLineSegment(sketch, "E1337", {"start": v(-3.67, -0.9) * mm, "end": v(-3.67, -0.89) * mm});
            skLineSegment(sketch, "E1338", {"start": v(-3.67, -0.89) * mm, "end": v(-3.68, -0.88) * mm});
            skLineSegment(sketch, "E1339", {"start": v(-3.68, -0.88) * mm, "end": v(-3.72, -0.88) * mm});
            skLineSegment(sketch, "E1340", {"start": v(-3.72, -0.88) * mm, "end": v(-3.77, -0.88) * mm});
            skLineSegment(sketch, "E1341", {"start": v(-3.77, -0.88) * mm, "end": v(-3.83, -0.88) * mm});
            skLineSegment(sketch, "E1342", {"start": v(-3.83, -0.88) * mm, "end": v(-3.92, -0.88) * mm});
            skLineSegment(sketch, "E1343", {"start": v(-3.92, -0.88) * mm, "end": v(-4.02, -0.87) * mm});
            skLineSegment(sketch, "E1344", {"start": v(-4.02, -0.87) * mm, "end": v(-4.12, -0.87) * mm});
            skLineSegment(sketch, "E1345", {"start": v(-4.12, -0.87) * mm, "end": v(-4.23, -0.86) * mm});
            skLineSegment(sketch, "E1346", {"start": v(-4.23, -0.86) * mm, "end": v(-4.34, -0.85) * mm});
            skLineSegment(sketch, "E1347", {"start": v(-4.34, -0.85) * mm, "end": v(-4.48, -0.85) * mm});
            skLineSegment(sketch, "E1348", {"start": v(-4.48, -0.85) * mm, "end": v(-4.64, -0.84) * mm});
            skLineSegment(sketch, "E1349", {"start": v(-4.64, -0.84) * mm, "end": v(-4.78, -0.84) * mm});
            skLineSegment(sketch, "E1350", {"start": v(-4.78, -0.84) * mm, "end": v(-4.88, -0.84) * mm});
            skLineSegment(sketch, "E1351", {"start": v(-4.88, -0.84) * mm, "end": v(-4.96, -0.84) * mm});
            skLineSegment(sketch, "E1352", {"start": v(-4.96, -0.84) * mm, "end": v(-5.03, -0.84) * mm});
            skLineSegment(sketch, "E1353", {"start": v(-5.03, -0.84) * mm, "end": v(-5.08, -0.84) * mm});
            skLineSegment(sketch, "E1354", {"start": v(-5.08, -0.84) * mm, "end": v(-5.12, -0.85) * mm});
            skLineSegment(sketch, "E1355", {"start": v(-5.12, -0.85) * mm, "end": v(-5.15, -0.85) * mm});
            skLineSegment(sketch, "E1356", {"start": v(-5.15, -0.85) * mm, "end": v(-5.18, -0.86) * mm});
            skLineSegment(sketch, "E1357", {"start": v(-5.18, -0.86) * mm, "end": v(-5.22, -0.87) * mm});
            skLineSegment(sketch, "E1358", {"start": v(-5.22, -0.87) * mm, "end": v(-5.36, -0.9) * mm});
            skLineSegment(sketch, "E1359", {"start": v(-5.36, -0.9) * mm, "end": v(-5.47, -0.94) * mm});
            skLineSegment(sketch, "E1360", {"start": v(-5.47, -0.94) * mm, "end": v(-5.57, -1) * mm});
            skLineSegment(sketch, "E1361", {"start": v(-5.57, -1) * mm, "end": v(-5.68, -1.07) * mm});
            skLineSegment(sketch, "E1362", {"start": v(-5.68, -1.07) * mm, "end": v(-5.76, -1.13) * mm});
            skLineSegment(sketch, "E1363", {"start": v(-5.76, -1.13) * mm, "end": v(-5.84, -1.16) * mm});
            skLineSegment(sketch, "E1364", {"start": v(-5.84, -1.16) * mm, "end": v(-5.94, -1.2) * mm});
            skLineSegment(sketch, "E1365", {"start": v(-5.94, -1.2) * mm, "end": v(-6.1, -1.23) * mm});
            skLineSegment(sketch, "E1366", {"start": v(-6.1, -1.23) * mm, "end": v(-6.3, -1.28) * mm});
            skLineSegment(sketch, "E1367", {"start": v(-6.3, -1.28) * mm, "end": v(-6.48, -1.35) * mm});
            skLineSegment(sketch, "E1368", {"start": v(-6.48, -1.35) * mm, "end": v(-6.65, -1.44) * mm});
            skLineSegment(sketch, "E1369", {"start": v(-6.65, -1.44) * mm, "end": v(-6.82, -1.55) * mm});
            skLineSegment(sketch, "E1370", {"start": v(-6.82, -1.55) * mm, "end": v(-6.88, -1.6) * mm});
            skLineSegment(sketch, "E1371", {"start": v(-6.88, -1.6) * mm, "end": v(-6.94, -1.65) * mm});
            skLineSegment(sketch, "E1372", {"start": v(-6.94, -1.65) * mm, "end": v(-7, -1.69) * mm});
            skLineSegment(sketch, "E1373", {"start": v(-7, -1.69) * mm, "end": v(-7.04, -1.72) * mm});
            skLineSegment(sketch, "E1374", {"start": v(-7.04, -1.72) * mm, "end": v(-7.07, -1.75) * mm});
            skLineSegment(sketch, "E1375", {"start": v(-7.07, -1.75) * mm, "end": v(-7.1, -1.77) * mm});
            skLineSegment(sketch, "E1376", {"start": v(-7.1, -1.77) * mm, "end": v(-7.12, -1.78) * mm});
            skLineSegment(sketch, "E1377", {"start": v(-7.12, -1.78) * mm, "end": v(-7.12, -1.8) * mm});
            skLineSegment(sketch, "E1378", {"start": v(-7.12, -1.8) * mm, "end": v(-7.11, -1.8) * mm});
            skLineSegment(sketch, "E1379", {"start": v(-7.11, -1.8) * mm, "end": v(-7.08, -1.8) * mm});
            skLineSegment(sketch, "E1380", {"start": v(-7.08, -1.8) * mm, "end": v(-7.03, -1.82) * mm});
            skLineSegment(sketch, "E1381", {"start": v(-7.03, -1.82) * mm, "end": v(-6.97, -1.84) * mm});
            skLineSegment(sketch, "E1382", {"start": v(-6.97, -1.84) * mm, "end": v(-6.85, -1.88) * mm});
            skLineSegment(sketch, "E1383", {"start": v(-6.85, -1.88) * mm, "end": v(-6.74, -1.91) * mm});
            skLineSegment(sketch, "E1384", {"start": v(-6.74, -1.91) * mm, "end": v(-6.7, -1.93) * mm});
            skLineSegment(sketch, "E1385", {"start": v(-6.7, -1.93) * mm, "end": v(-6.64, -1.94) * mm});
            skLineSegment(sketch, "E1386", {"start": v(-6.64, -1.94) * mm, "end": v(-6.58, -1.96) * mm});
            skLineSegment(sketch, "E1387", {"start": v(-6.58, -1.96) * mm, "end": v(-6.52, -1.98) * mm});
            skLineSegment(sketch, "E1388", {"start": v(-6.52, -1.98) * mm, "end": v(-6.38, -2.01) * mm});
            skLineSegment(sketch, "E1389", {"start": v(-6.38, -2.01) * mm, "end": v(-6.24, -2.05) * mm});
            skLineSegment(sketch, "E1390", {"start": v(-6.24, -2.05) * mm, "end": v(-6.1, -2.1) * mm});
            skLineSegment(sketch, "E1391", {"start": v(-6.1, -2.1) * mm, "end": v(-5.97, -2.12) * mm});
            skLineSegment(sketch, "E1392", {"start": v(-5.97, -2.12) * mm, "end": v(-5.85, -2.14) * mm});
            skLineSegment(sketch, "E1393", {"start": v(-5.85, -2.14) * mm, "end": v(-5.73, -2.16) * mm});
            skLineSegment(sketch, "E1394", {"start": v(-5.73, -2.16) * mm, "end": v(-5.58, -2.18) * mm});
            skLineSegment(sketch, "E1395", {"start": v(-5.58, -2.18) * mm, "end": v(-5.44, -2.2) * mm});
            skLineSegment(sketch, "E1396", {"start": v(-5.44, -2.2) * mm, "end": v(-5.3, -2.21) * mm});
            skLineSegment(sketch, "E1397", {"start": v(-5.3, -2.21) * mm, "end": v(-5.19, -2.22) * mm});
            skLineSegment(sketch, "E1398", {"start": v(-5.19, -2.22) * mm, "end": v(-5.14, -2.22) * mm});
            skLineSegment(sketch, "E1399", {"start": v(-5.14, -2.22) * mm, "end": v(-5.1, -2.23) * mm});
            skLineSegment(sketch, "E1400", {"start": v(-5.1, -2.23) * mm, "end": v(-5.07, -2.23) * mm});
            skLineSegment(sketch, "E1401", {"start": v(-5.07, -2.23) * mm, "end": v(-5.05, -2.23) * mm});
            skLineSegment(sketch, "E1402", {"start": v(-5.05, -2.23) * mm, "end": v(-5.03, -2.22) * mm});
            skLineSegment(sketch, "E1403", {"start": v(-5.03, -2.22) * mm, "end": v(-5, -2.2) * mm});
            skLineSegment(sketch, "E1404", {"start": v(-4.33, -2.2) * mm, "end": v(-3.96, -2.15) * mm});
            skLineSegment(sketch, "E1405", {"start": v(-3.96, -2.15) * mm, "end": v(-3.62, -2.09) * mm});
            skLineSegment(sketch, "E1406", {"start": v(-3.62, -2.09) * mm, "end": v(-3.32, -2) * mm});
            skLineSegment(sketch, "E1407", {"start": v(-3.32, -2) * mm, "end": v(-3.03, -1.91) * mm});
            skLineSegment(sketch, "E1408", {"start": v(-3.03, -1.91) * mm, "end": v(-2.97, -1.89) * mm});
            skLineSegment(sketch, "E1409", {"start": v(-2.97, -1.89) * mm, "end": v(-2.9, -1.86) * mm});
            skLineSegment(sketch, "E1410", {"start": v(-2.9, -1.86) * mm, "end": v(-2.82, -1.84) * mm});
            skLineSegment(sketch, "E1411", {"start": v(-2.82, -1.84) * mm, "end": v(-2.75, -1.81) * mm});
            skLineSegment(sketch, "E1412", {"start": v(-2.75, -1.81) * mm, "end": v(-2.4, -1.69) * mm});
            skLineSegment(sketch, "E1413", {"start": v(-2.4, -1.69) * mm, "end": v(-2.1, -1.58) * mm});
            skLineSegment(sketch, "E1414", {"start": v(-2.1, -1.58) * mm, "end": v(-1.88, -1.48) * mm});
            skLineSegment(sketch, "E1415", {"start": v(-1.88, -1.48) * mm, "end": v(-1.72, -1.4) * mm});
            skLineSegment(sketch, "E1416", {"start": v(-1.72, -1.4) * mm, "end": v(-1.68, -1.37) * mm});
            skLineSegment(sketch, "E1417", {"start": v(-1.68, -1.37) * mm, "end": v(-1.63, -1.34) * mm});
            skLineSegment(sketch, "E1418", {"start": v(-1.63, -1.34) * mm, "end": v(-1.57, -1.3) * mm});
            skLineSegment(sketch, "E1419", {"start": v(-1.57, -1.3) * mm, "end": v(-1.52, -1.27) * mm});
            skLineSegment(sketch, "E1420", {"start": v(-1.52, -1.27) * mm, "end": v(-1.47, -1.24) * mm});
            skLineSegment(sketch, "E1421", {"start": v(-1.47, -1.24) * mm, "end": v(-1.4, -1.2) * mm});
            skLineSegment(sketch, "E1422", {"start": v(-1.4, -1.2) * mm, "end": v(-1.35, -1.17) * mm});
            skLineSegment(sketch, "E1423", {"start": v(-1.35, -1.17) * mm, "end": v(-1.3, -1.14) * mm});
            skLineSegment(sketch, "E1424", {"start": v(-1.3, -1.14) * mm, "end": v(-1.2, -1.08) * mm});
            skLineSegment(sketch, "E1425", {"start": v(-1.2, -1.08) * mm, "end": v(-1.2, -0.75) * mm});
            skLineSegment(sketch, "E1426", {"start": v(-1.2, -0.75) * mm, "end": v(-1.2, -0.62) * mm});
            skLineSegment(sketch, "E1427", {"start": v(-1.2, -0.62) * mm, "end": v(-1.2, -0.51) * mm});
            skLineSegment(sketch, "E1428", {"start": v(-1.2, -0.51) * mm, "end": v(-1.2, -0.44) * mm});
            skLineSegment(sketch, "E1429", {"start": v(-1.2, -0.44) * mm, "end": v(-1.21, -0.41) * mm});
            skLineSegment(sketch, "E1430", {"start": v(-1.21, -0.41) * mm, "end": v(-1.22, -0.41) * mm});
            skLineSegment(sketch, "E1431", {"start": v(-1.22, -0.41) * mm, "end": v(-1.24, -0.42) * mm});
            skLineSegment(sketch, "E1432", {"start": v(-1.24, -0.42) * mm, "end": v(-1.26, -0.43) * mm});
            skLineSegment(sketch, "E1433", {"start": v(-1.26, -0.43) * mm, "end": v(-1.3, -0.43) * mm});
            skLineSegment(sketch, "E1434", {"start": v(-1.3, -0.43) * mm, "end": v(-1.33, -0.42) * mm});
            skLineSegment(sketch, "E1435", {"start": v(-1.33, -0.42) * mm, "end": v(-1.4, -0.41) * mm});
            skLineSegment(sketch, "E1436", {"start": v(-1.4, -0.41) * mm, "end": v(-1.54, -0.4) * mm});
            skLineSegment(sketch, "E1437", {"start": v(-1.54, -0.4) * mm, "end": v(-1.72, -0.4) * mm});
            skLineSegment(sketch, "E1438", {"start": v(-1.72, -0.4) * mm, "end": v(-1.9, -0.4) * mm});
            skLineSegment(sketch, "E1439", {"start": v(-1.9, -0.4) * mm, "end": v(-2.06, -0.41) * mm});
            skLineSegment(sketch, "E1440", {"start": v(-2.06, -0.41) * mm, "end": v(-2.2, -0.44) * mm});
            skLineSegment(sketch, "E1441", {"start": v(-2.2, -0.44) * mm, "end": v(-2.34, -0.47) * mm});
            skLineSegment(sketch, "E1442", {"start": v(-2.34, -0.47) * mm, "end": v(-2.51, -0.53) * mm});
            skLineSegment(sketch, "E1443", {"start": v(-2.51, -0.53) * mm, "end": v(-2.7, -0.6) * mm});
            skLineSegment(sketch, "E1444", {"start": v(-2.7, -0.6) * mm, "end": v(-2.87, -0.67) * mm});
            skLineSegment(sketch, "E1445", {"start": v(-2.87, -0.67) * mm, "end": v(-3.05, -0.75) * mm});
            skLineSegment(sketch, "E1446", {"start": v(-3.05, -0.75) * mm, "end": v(-3.21, -0.84) * mm});
            skLineSegment(sketch, "E1447", {"start": v(-3.21, -0.84) * mm, "end": v(-3.36, -0.93) * mm});
            skLineSegment(sketch, "E1448", {"start": v(-3.36, -0.93) * mm, "end": v(-3.5, -1.02) * mm});
            skLineSegment(sketch, "E1449", {"start": v(-3.5, -1.02) * mm, "end": v(-3.62, -1.12) * mm});
            skLineSegment(sketch, "E1450", {"start": v(-3.62, -1.12) * mm, "end": v(-3.68, -1.18) * mm});
            skLineSegment(sketch, "E1451", {"start": v(-3.68, -1.18) * mm, "end": v(-3.77, -1.25) * mm});
            skLineSegment(sketch, "E1452", {"start": v(-3.77, -1.25) * mm, "end": v(-3.87, -1.33) * mm});
            skLineSegment(sketch, "E1453", {"start": v(-3.87, -1.33) * mm, "end": v(-3.95, -1.4) * mm});
            skLineSegment(sketch, "E1454", {"start": v(-3.95, -1.4) * mm, "end": v(-4, -1.43) * mm});
            skLineSegment(sketch, "E1455", {"start": v(-4, -1.43) * mm, "end": v(-4.07, -1.5) * mm});
            skLineSegment(sketch, "E1456", {"start": v(-4.07, -1.5) * mm, "end": v(-4.16, -1.58) * mm});
            skLineSegment(sketch, "E1457", {"start": v(-4.16, -1.58) * mm, "end": v(-4.26, -1.68) * mm});
            skLineSegment(sketch, "E1458", {"start": v(-4.26, -1.68) * mm, "end": v(-4.39, -1.8) * mm});
            skLineSegment(sketch, "E1459", {"start": v(-4.39, -1.8) * mm, "end": v(-4.48, -1.9) * mm});
            skLineSegment(sketch, "E1460", {"start": v(-4.48, -1.9) * mm, "end": v(-4.56, -1.98) * mm});
            skLineSegment(sketch, "E1461", {"start": v(-4.56, -1.98) * mm, "end": v(-4.62, -2.06) * mm});
            skLineSegment(sketch, "E1462", {"start": v(-4.62, -2.06) * mm, "end": v(-4.65, -2.1) * mm});
            skLineSegment(sketch, "E1463", {"start": v(-4.65, -2.1) * mm, "end": v(-4.69, -2.15) * mm});
            skLineSegment(sketch, "E1464", {"start": v(-4.69, -2.15) * mm, "end": v(-4.7, -2.19) * mm});
            skLineSegment(sketch, "E1465", {"start": v(-4.7, -2.19) * mm, "end": v(-4.72, -2.2) * mm});
            skLineSegment(sketch, "E1466", {"start": v(-4.72, -2.2) * mm, "end": v(-4.7, -2.22) * mm});
            skLineSegment(sketch, "E1467", {"start": v(-4.7, -2.22) * mm, "end": v(-4.62, -2.22) * mm});
            skLineSegment(sketch, "E1468", {"start": v(-4.62, -2.22) * mm, "end": v(-4.5, -2.22) * mm});
            skLineSegment(sketch, "E1469", {"start": v(-4.5, -2.22) * mm, "end": v(-4.33, -2.2) * mm});
            skLineSegment(sketch, "E1470", {"start": v(6.83, -2.1) * mm, "end": v(6.97, -2.08) * mm});
            skLineSegment(sketch, "E1471", {"start": v(6.97, -2.08) * mm, "end": v(7.09, -2.06) * mm});
            skLineSegment(sketch, "E1472", {"start": v(7.09, -2.06) * mm, "end": v(7.2, -2.04) * mm});
            skLineSegment(sketch, "E1473", {"start": v(7.2, -2.04) * mm, "end": v(7.35, -2.03) * mm});
            skLineSegment(sketch, "E1474", {"start": v(7.35, -2.03) * mm, "end": v(7.56, -2.02) * mm});
            skLineSegment(sketch, "E1475", {"start": v(7.56, -2.02) * mm, "end": v(7.76, -2.03) * mm});
            skLineSegment(sketch, "E1476", {"start": v(7.76, -2.03) * mm, "end": v(7.95, -2.04) * mm});
            skLineSegment(sketch, "E1477", {"start": v(7.95, -2.04) * mm, "end": v(8.13, -2.07) * mm});
            skLineSegment(sketch, "E1478", {"start": v(8.13, -2.07) * mm, "end": v(8.22, -2.08) * mm});
            skLineSegment(sketch, "E1479", {"start": v(8.22, -2.08) * mm, "end": v(8.33, -2.1) * mm});
            skLineSegment(sketch, "E1480", {"start": v(8.33, -2.1) * mm, "end": v(8.44, -2.1) * mm});
            skLineSegment(sketch, "E1481", {"start": v(8.44, -2.1) * mm, "end": v(8.55, -2.12) * mm});
            skLineSegment(sketch, "E1482", {"start": v(8.55, -2.12) * mm, "end": v(8.64, -2.12) * mm});
            skLineSegment(sketch, "E1483", {"start": v(8.64, -2.12) * mm, "end": v(8.71, -2.13) * mm});
            skLineSegment(sketch, "E1484", {"start": v(8.71, -2.13) * mm, "end": v(8.78, -2.14) * mm});
            skLineSegment(sketch, "E1485", {"start": v(8.78, -2.14) * mm, "end": v(8.8, -2.14) * mm});
            skLineSegment(sketch, "E1486", {"start": v(8.8, -2.14) * mm, "end": v(8.83, -2.14) * mm});
            skLineSegment(sketch, "E1487", {"start": v(8.83, -2.14) * mm, "end": v(8.84, -2.14) * mm});
            skLineSegment(sketch, "E1488", {"start": v(8.84, -2.14) * mm, "end": v(8.85, -2.13) * mm});
            skLineSegment(sketch, "E1489", {"start": v(8.85, -2.13) * mm, "end": v(8.85, -2.12) * mm});
            skLineSegment(sketch, "E1490", {"start": v(8.85, -2.12) * mm, "end": v(8.86, -2.1) * mm});
            skLineSegment(sketch, "E1491", {"start": v(8.86, -2.1) * mm, "end": v(8.86, -2.08) * mm});
            skLineSegment(sketch, "E1492", {"start": v(8.86, -2.08) * mm, "end": v(8.85, -2.05) * mm});
            skLineSegment(sketch, "E1493", {"start": v(8.85, -2.05) * mm, "end": v(8.85, -2) * mm});
            skLineSegment(sketch, "E1494", {"start": v(8.85, -2) * mm, "end": v(8.83, -1.91) * mm});
            skLineSegment(sketch, "E1495", {"start": v(8.83, -1.91) * mm, "end": v(8.8, -1.83) * mm});
            skLineSegment(sketch, "E1496", {"start": v(8.8, -1.83) * mm, "end": v(8.76, -1.72) * mm});
            skLineSegment(sketch, "E1497", {"start": v(8.76, -1.72) * mm, "end": v(8.68, -1.58) * mm});
            skLineSegment(sketch, "E1498", {"start": v(8.68, -1.58) * mm, "end": v(8.6, -1.42) * mm});
            skLineSegment(sketch, "E1499", {"start": v(8.6, -1.42) * mm, "end": v(8.53, -1.32) * mm});
            skLineSegment(sketch, "E1500", {"start": v(8.53, -1.32) * mm, "end": v(8.47, -1.23) * mm});
            skLineSegment(sketch, "E1501", {"start": v(8.47, -1.23) * mm, "end": v(8.38, -1.13) * mm});
            skLineSegment(sketch, "E1502", {"start": v(8.38, -1.13) * mm, "end": v(8.3, -1.06) * mm});
            skLineSegment(sketch, "E1503", {"start": v(8.3, -1.06) * mm, "end": v(8.24, -1) * mm});
            skLineSegment(sketch, "E1504", {"start": v(8.24, -1) * mm, "end": v(8.18, -0.96) * mm});
            skLineSegment(sketch, "E1505", {"start": v(8.18, -0.96) * mm, "end": v(8.12, -0.92) * mm});
            skLineSegment(sketch, "E1506", {"start": v(8.12, -0.92) * mm, "end": v(8.06, -0.89) * mm});
            skLineSegment(sketch, "E1507", {"start": v(8.06, -0.89) * mm, "end": v(7.98, -0.86) * mm});
            skLineSegment(sketch, "E1508", {"start": v(7.98, -0.86) * mm, "end": v(7.9, -0.84) * mm});
            skLineSegment(sketch, "E1509", {"start": v(7.9, -0.84) * mm, "end": v(7.8, -0.81) * mm});
            skLineSegment(sketch, "E1510", {"start": v(7.8, -0.81) * mm, "end": v(7.72, -0.8) * mm});
            skLineSegment(sketch, "E1511", {"start": v(7.72, -0.8) * mm, "end": v(7.65, -0.79) * mm});
            skLineSegment(sketch, "E1512", {"start": v(7.65, -0.79) * mm, "end": v(7.56, -0.78) * mm});
            skLineSegment(sketch, "E1513", {"start": v(7.56, -0.78) * mm, "end": v(7.43, -0.78) * mm});
            skLineSegment(sketch, "E1514", {"start": v(7.43, -0.78) * mm, "end": v(7.35, -0.78) * mm});
            skLineSegment(sketch, "E1515", {"start": v(7.35, -0.78) * mm, "end": v(7.28, -0.79) * mm});
            skLineSegment(sketch, "E1516", {"start": v(7.28, -0.79) * mm, "end": v(7.22, -0.79) * mm});
            skLineSegment(sketch, "E1517", {"start": v(7.22, -0.79) * mm, "end": v(7.17, -0.8) * mm});
            skLineSegment(sketch, "E1518", {"start": v(7.17, -0.8) * mm, "end": v(7.12, -0.8) * mm});
            skLineSegment(sketch, "E1519", {"start": v(7.12, -0.8) * mm, "end": v(7.07, -0.82) * mm});
            skLineSegment(sketch, "E1520", {"start": v(7.07, -0.82) * mm, "end": v(7.01, -0.84) * mm});
            skLineSegment(sketch, "E1521", {"start": v(7.01, -0.84) * mm, "end": v(6.94, -0.87) * mm});
            skLineSegment(sketch, "E1522", {"start": v(6.94, -0.87) * mm, "end": v(6.84, -0.92) * mm});
            skLineSegment(sketch, "E1523", {"start": v(6.84, -0.92) * mm, "end": v(6.76, -0.97) * mm});
            skLineSegment(sketch, "E1524", {"start": v(6.76, -0.97) * mm, "end": v(6.7, -1) * mm});
            skLineSegment(sketch, "E1525", {"start": v(6.7, -1) * mm, "end": v(6.62, -1.06) * mm});
            skLineSegment(sketch, "E1526", {"start": v(6.62, -1.06) * mm, "end": v(6.54, -1.12) * mm});
            skLineSegment(sketch, "E1527", {"start": v(6.54, -1.12) * mm, "end": v(6.45, -1.18) * mm});
            skLineSegment(sketch, "E1528", {"start": v(6.45, -1.18) * mm, "end": v(6.36, -1.24) * mm});
            skLineSegment(sketch, "E1529", {"start": v(6.36, -1.24) * mm, "end": v(6.28, -1.29) * mm});
            skLineSegment(sketch, "E1530", {"start": v(6.28, -1.29) * mm, "end": v(6.21, -1.33) * mm});
            skLineSegment(sketch, "E1531", {"start": v(6.21, -1.33) * mm, "end": v(6.16, -1.35) * mm});
            skLineSegment(sketch, "E1532", {"start": v(6.16, -1.35) * mm, "end": v(6.05, -1.4) * mm});
            skLineSegment(sketch, "E1533", {"start": v(6.05, -1.4) * mm, "end": v(5.94, -1.43) * mm});
            skLineSegment(sketch, "E1534", {"start": v(5.94, -1.43) * mm, "end": v(5.9, -1.44) * mm});
            skLineSegment(sketch, "E1535", {"start": v(5.9, -1.44) * mm, "end": v(5.88, -1.44) * mm});
            skLineSegment(sketch, "E1536", {"start": v(5.88, -1.44) * mm, "end": v(5.9, -1.46) * mm});
            skLineSegment(sketch, "E1537", {"start": v(5.9, -1.46) * mm, "end": v(5.92, -1.48) * mm});
            skLineSegment(sketch, "E1538", {"start": v(5.92, -1.48) * mm, "end": v(5.96, -1.5) * mm});
            skLineSegment(sketch, "E1539", {"start": v(5.96, -1.5) * mm, "end": v(6, -1.55) * mm});
            skLineSegment(sketch, "E1540", {"start": v(6, -1.55) * mm, "end": v(6.07, -1.6) * mm});
            skLineSegment(sketch, "E1541", {"start": v(6.07, -1.6) * mm, "end": v(6.16, -1.68) * mm});
            skLineSegment(sketch, "E1542", {"start": v(6.16, -1.68) * mm, "end": v(6.26, -1.77) * mm});
            skLineSegment(sketch, "E1543", {"start": v(6.26, -1.77) * mm, "end": v(6.37, -1.9) * mm});
            skLineSegment(sketch, "E1544", {"start": v(6.37, -1.9) * mm, "end": v(6.62, -2.15) * mm});
            skLineSegment(sketch, "E1545", {"start": v(6.62, -2.15) * mm, "end": v(6.67, -2.14) * mm});
            skLineSegment(sketch, "E1546", {"start": v(6.67, -2.14) * mm, "end": v(6.7, -2.14) * mm});
            skLineSegment(sketch, "E1547", {"start": v(6.7, -2.14) * mm, "end": v(6.74, -2.13) * mm});
            skLineSegment(sketch, "E1548", {"start": v(6.74, -2.13) * mm, "end": v(6.78, -2.12) * mm});
            skLineSegment(sketch, "E1549", {"start": v(6.78, -2.12) * mm, "end": v(6.83, -2.1) * mm});
            skLineSegment(sketch, "E1550", {"start": v(-8.73, -1.96) * mm, "end": v(-8.68, -1.95) * mm});
            skLineSegment(sketch, "E1551", {"start": v(-8.68, -1.95) * mm, "end": v(-8.64, -1.94) * mm});
            skLineSegment(sketch, "E1552", {"start": v(-8.64, -1.94) * mm, "end": v(-8.6, -1.93) * mm});
            skLineSegment(sketch, "E1553", {"start": v(-8.6, -1.93) * mm, "end": v(-8.56, -1.92) * mm});
            skLineSegment(sketch, "E1554", {"start": v(-8.56, -1.92) * mm, "end": v(-8.45, -1.87) * mm});
            skLineSegment(sketch, "E1555", {"start": v(-8.45, -1.87) * mm, "end": v(-8.35, -1.83) * mm});
            skLineSegment(sketch, "E1556", {"start": v(-8.35, -1.83) * mm, "end": v(-8.27, -1.8) * mm});
            skLineSegment(sketch, "E1557", {"start": v(-8.27, -1.8) * mm, "end": v(-8.2, -1.77) * mm});
            skLineSegment(sketch, "E1558", {"start": v(-8.2, -1.77) * mm, "end": v(-8.13, -1.76) * mm});
            skLineSegment(sketch, "E1559", {"start": v(-8.13, -1.76) * mm, "end": v(-8.07, -1.74) * mm});
            skLineSegment(sketch, "E1560", {"start": v(-8.07, -1.74) * mm, "end": v(-8, -1.73) * mm});
            skLineSegment(sketch, "E1561", {"start": v(-8, -1.73) * mm, "end": v(-7.94, -1.72) * mm});
            skLineSegment(sketch, "E1562", {"start": v(-7.94, -1.72) * mm, "end": v(-7.88, -1.71) * mm});
            skLineSegment(sketch, "E1563", {"start": v(-7.88, -1.71) * mm, "end": v(-7.82, -1.71) * mm});
            skLineSegment(sketch, "E1564", {"start": v(-7.82, -1.71) * mm, "end": v(-7.76, -1.72) * mm});
            skLineSegment(sketch, "E1565", {"start": v(-7.76, -1.72) * mm, "end": v(-7.68, -1.72) * mm});
            skLineSegment(sketch, "E1566", {"start": v(-7.68, -1.72) * mm, "end": v(-7.55, -1.73) * mm});
            skLineSegment(sketch, "E1567", {"start": v(-7.55, -1.73) * mm, "end": v(-7.45, -1.74) * mm});
            skLineSegment(sketch, "E1568", {"start": v(-7.45, -1.74) * mm, "end": v(-7.36, -1.75) * mm});
            skLineSegment(sketch, "E1569", {"start": v(-7.36, -1.75) * mm, "end": v(-7.15, -1.55) * mm});
            skLineSegment(sketch, "E1570", {"start": v(-7.15, -1.55) * mm, "end": v(-7.06, -1.45) * mm});
            skLineSegment(sketch, "E1571", {"start": v(-7.06, -1.45) * mm, "end": v(-6.98, -1.38) * mm});
            skLineSegment(sketch, "E1572", {"start": v(-6.98, -1.38) * mm, "end": v(-6.92, -1.33) * mm});
            skLineSegment(sketch, "E1573", {"start": v(-6.92, -1.33) * mm, "end": v(-6.87, -1.3) * mm});
            skLineSegment(sketch, "E1574", {"start": v(-6.87, -1.3) * mm, "end": v(-6.65, -1.2) * mm});
            skLineSegment(sketch, "E1575", {"start": v(-6.65, -1.2) * mm, "end": v(-6.39, -1.1) * mm});
            skLineSegment(sketch, "E1576", {"start": v(-6.39, -1.1) * mm, "end": v(-6.2, -1.06) * mm});
            skLineSegment(sketch, "E1577", {"start": v(-6.2, -1.06) * mm, "end": v(-6.08, -1.02) * mm});
            skLineSegment(sketch, "E1578", {"start": v(-6.08, -1.02) * mm, "end": v(-5.99, -0.98) * mm});
            skLineSegment(sketch, "E1579", {"start": v(-5.99, -0.98) * mm, "end": v(-5.93, -0.95) * mm});
            skLineSegment(sketch, "E1580", {"start": v(-5.93, -0.95) * mm, "end": v(-5.9, -0.93) * mm});
            skLineSegment(sketch, "E1581", {"start": v(-5.9, -0.93) * mm, "end": v(-5.9, -0.91) * mm});
            skLineSegment(sketch, "E1582", {"start": v(-5.9, -0.91) * mm, "end": v(-5.93, -0.9) * mm});
            skLineSegment(sketch, "E1583", {"start": v(-5.93, -0.9) * mm, "end": v(-6, -0.9) * mm});
            skLineSegment(sketch, "E1584", {"start": v(-6, -0.9) * mm, "end": v(-6.14, -0.9) * mm});
            skLineSegment(sketch, "E1585", {"start": v(-6.14, -0.9) * mm, "end": v(-6.3, -0.87) * mm});
            skLineSegment(sketch, "E1586", {"start": v(-6.3, -0.87) * mm, "end": v(-6.5, -0.82) * mm});
            skLineSegment(sketch, "E1587", {"start": v(-6.5, -0.82) * mm, "end": v(-6.74, -0.75) * mm});
            skLineSegment(sketch, "E1588", {"start": v(-6.74, -0.75) * mm, "end": v(-6.88, -0.72) * mm});
            skLineSegment(sketch, "E1589", {"start": v(-6.88, -0.72) * mm, "end": v(-7.01, -0.69) * mm});
            skLineSegment(sketch, "E1590", {"start": v(-7.01, -0.69) * mm, "end": v(-7.17, -0.66) * mm});
            skLineSegment(sketch, "E1591", {"start": v(-7.17, -0.66) * mm, "end": v(-7.38, -0.64) * mm});
            skLineSegment(sketch, "E1592", {"start": v(-7.38, -0.64) * mm, "end": v(-7.45, -0.64) * mm});
            skLineSegment(sketch, "E1593", {"start": v(-7.45, -0.64) * mm, "end": v(-7.55, -0.65) * mm});
            skLineSegment(sketch, "E1594", {"start": v(-7.55, -0.65) * mm, "end": v(-7.67, -0.67) * mm});
            skLineSegment(sketch, "E1595", {"start": v(-7.67, -0.67) * mm, "end": v(-7.78, -0.68) * mm});
            skLineSegment(sketch, "E1596", {"start": v(-7.78, -0.68) * mm, "end": v(-7.92, -0.72) * mm});
            skLineSegment(sketch, "E1597", {"start": v(-7.92, -0.72) * mm, "end": v(-8.07, -0.77) * mm});
            skLineSegment(sketch, "E1598", {"start": v(-8.07, -0.77) * mm, "end": v(-8.2, -0.83) * mm});
            skLineSegment(sketch, "E1599", {"start": v(-8.2, -0.83) * mm, "end": v(-8.3, -0.88) * mm});
            skLineSegment(sketch, "E1600", {"start": v(-8.3, -0.88) * mm, "end": v(-8.34, -0.91) * mm});
            skLineSegment(sketch, "E1601", {"start": v(-8.34, -0.91) * mm, "end": v(-8.4, -0.96) * mm});
            skLineSegment(sketch, "E1602", {"start": v(-8.4, -0.96) * mm, "end": v(-8.46, -1.02) * mm});
            skLineSegment(sketch, "E1603", {"start": v(-8.46, -1.02) * mm, "end": v(-8.53, -1.1) * mm});
            skLineSegment(sketch, "E1604", {"start": v(-8.53, -1.1) * mm, "end": v(-8.63, -1.2) * mm});
            skLineSegment(sketch, "E1605", {"start": v(-8.63, -1.2) * mm, "end": v(-8.7, -1.3) * mm});
            skLineSegment(sketch, "E1606", {"start": v(-8.7, -1.3) * mm, "end": v(-8.75, -1.37) * mm});
            skLineSegment(sketch, "E1607", {"start": v(-8.75, -1.37) * mm, "end": v(-8.79, -1.47) * mm});
            skLineSegment(sketch, "E1608", {"start": v(-8.79, -1.47) * mm, "end": v(-8.8, -1.53) * mm});
            skLineSegment(sketch, "E1609", {"start": v(-8.8, -1.53) * mm, "end": v(-8.82, -1.6) * mm});
            skLineSegment(sketch, "E1610", {"start": v(-8.82, -1.6) * mm, "end": v(-8.83, -1.7) * mm});
            skLineSegment(sketch, "E1611", {"start": v(-8.83, -1.7) * mm, "end": v(-8.84, -1.78) * mm});
            skLineSegment(sketch, "E1612", {"start": v(-8.84, -1.78) * mm, "end": v(-8.84, -1.85) * mm});
            skLineSegment(sketch, "E1613", {"start": v(-8.84, -1.85) * mm, "end": v(-8.85, -1.92) * mm});
            skLineSegment(sketch, "E1614", {"start": v(-8.85, -1.92) * mm, "end": v(-8.84, -1.96) * mm});
            skLineSegment(sketch, "E1615", {"start": v(-8.84, -1.96) * mm, "end": v(-8.84, -1.98) * mm});
            skLineSegment(sketch, "E1616", {"start": v(-8.84, -1.98) * mm, "end": v(-8.82, -1.98) * mm});
            skLineSegment(sketch, "E1617", {"start": v(-8.82, -1.98) * mm, "end": v(-8.8, -1.97) * mm});
            skLineSegment(sketch, "E1618", {"start": v(-8.8, -1.97) * mm, "end": v(-8.76, -1.97) * mm});
            skLineSegment(sketch, "E1619", {"start": v(-8.76, -1.97) * mm, "end": v(-8.73, -1.96) * mm});
            skLineSegment(sketch, "E1620", {"start": v(-0.35, -1.7) * mm, "end": v(-0.26, -1.67) * mm});
            skLineSegment(sketch, "E1621", {"start": v(-0.26, -1.67) * mm, "end": v(-0.2, -1.64) * mm});
            skLineSegment(sketch, "E1622", {"start": v(-0.2, -1.64) * mm, "end": v(-0.16, -1.6) * mm});
            skLineSegment(sketch, "E1623", {"start": v(-0.16, -1.6) * mm, "end": v(-0.15, -1.55) * mm});
            skLineSegment(sketch, "E1624", {"start": v(-0.15, -1.55) * mm, "end": v(-0.14, -1.52) * mm});
            skLineSegment(sketch, "E1625", {"start": v(-0.14, -1.52) * mm, "end": v(-0.13, -1.5) * mm});
            skLineSegment(sketch, "E1626", {"start": v(-0.13, -1.5) * mm, "end": v(-0.1, -1.48) * mm});
            skLineSegment(sketch, "E1627", {"start": v(-0.1, -1.48) * mm, "end": v(-0.08, -1.48) * mm});
            skLineSegment(sketch, "E1628", {"start": v(-0.08, -1.48) * mm, "end": v(-0.05, -1.49) * mm});
            skLineSegment(sketch, "E1629", {"start": v(-0.05, -1.49) * mm, "end": v(0, -1.51) * mm});
            skLineSegment(sketch, "E1630", {"start": v(0, -1.51) * mm, "end": v(0.1, -1.57) * mm});
            skLineSegment(sketch, "E1631", {"start": v(0.1, -1.57) * mm, "end": v(0.22, -1.59) * mm});
            skLineSegment(sketch, "E1632", {"start": v(0.22, -1.59) * mm, "end": v(0.25, -1.58) * mm});
            skLineSegment(sketch, "E1633", {"start": v(0.25, -1.58) * mm, "end": v(0.28, -1.57) * mm});
            skLineSegment(sketch, "E1634", {"start": v(0.28, -1.57) * mm, "end": v(0.31, -1.56) * mm});
            skLineSegment(sketch, "E1635", {"start": v(0.31, -1.56) * mm, "end": v(0.35, -1.53) * mm});
            skLineSegment(sketch, "E1636", {"start": v(0.35, -1.53) * mm, "end": v(0.42, -1.48) * mm});
            skLineSegment(sketch, "E1637", {"start": v(0.42, -1.48) * mm, "end": v(0.44, -1.39) * mm});
            skLineSegment(sketch, "E1638", {"start": v(0.44, -1.39) * mm, "end": v(0.45, -1.3) * mm});
            skLineSegment(sketch, "E1639", {"start": v(0.45, -1.3) * mm, "end": v(0.45, -1.19) * mm});
            skLineSegment(sketch, "E1640", {"start": v(0.45, -1.19) * mm, "end": v(0.46, -1.07) * mm});
            skLineSegment(sketch, "E1641", {"start": v(0.46, -1.07) * mm, "end": v(0.46, -0.95) * mm});
            skLineSegment(sketch, "E1642", {"start": v(0.46, -0.95) * mm, "end": v(0.46, -0.82) * mm});
            skLineSegment(sketch, "E1643", {"start": v(0.46, -0.82) * mm, "end": v(0.45, -0.7) * mm});
            skLineSegment(sketch, "E1644", {"start": v(0.45, -0.7) * mm, "end": v(0.44, -0.6) * mm});
            skLineSegment(sketch, "E1645", {"start": v(0.44, -0.6) * mm, "end": v(0.43, -0.52) * mm});
            skLineSegment(sketch, "E1646", {"start": v(0.43, -0.52) * mm, "end": v(0.43, -0.49) * mm});
            skLineSegment(sketch, "E1647", {"start": v(0.43, -0.49) * mm, "end": v(0.36, -0.55) * mm});
            skLineSegment(sketch, "E1648", {"start": v(0.36, -0.55) * mm, "end": v(0.3, -0.6) * mm});
            skLineSegment(sketch, "E1649", {"start": v(0.3, -0.6) * mm, "end": v(0.23, -0.65) * mm});
            skLineSegment(sketch, "E1650", {"start": v(0.23, -0.65) * mm, "end": v(0.14, -0.69) * mm});
            skLineSegment(sketch, "E1651", {"start": v(0.14, -0.69) * mm, "end": v(0.03, -0.73) * mm});
            skLineSegment(sketch, "E1652", {"start": v(0.03, -0.73) * mm, "end": v(-0.09, -0.76) * mm});
            skLineSegment(sketch, "E1653", {"start": v(-0.09, -0.76) * mm, "end": v(-0.18, -0.78) * mm});
            skLineSegment(sketch, "E1654", {"start": v(-0.18, -0.78) * mm, "end": v(-0.25, -0.78) * mm});
            skLineSegment(sketch, "E1655", {"start": v(-0.25, -0.78) * mm, "end": v(-0.33, -0.77) * mm});
            skLineSegment(sketch, "E1656", {"start": v(-0.33, -0.77) * mm, "end": v(-0.41, -0.75) * mm});
            skLineSegment(sketch, "E1657", {"start": v(-0.41, -0.75) * mm, "end": v(-0.47, -0.8) * mm});
            skLineSegment(sketch, "E1658", {"start": v(-0.47, -0.8) * mm, "end": v(-0.57, -0.85) * mm});
            skLineSegment(sketch, "E1659", {"start": v(-0.57, -0.85) * mm, "end": v(-0.67, -0.9) * mm});
            skLineSegment(sketch, "E1660", {"start": v(-0.67, -0.9) * mm, "end": v(-0.77, -0.92) * mm});
            skLineSegment(sketch, "E1661", {"start": v(-0.77, -0.92) * mm, "end": v(-0.85, -0.93) * mm});
            skLineSegment(sketch, "E1662", {"start": v(-0.85, -0.93) * mm, "end": v(-0.9, -0.92) * mm});
            skLineSegment(sketch, "E1663", {"start": v(-0.9, -0.92) * mm, "end": v(-0.94, -0.91) * mm});
            skLineSegment(sketch, "E1664", {"start": v(-0.94, -0.91) * mm, "end": v(-0.95, -0.91) * mm});
            skLineSegment(sketch, "E1665", {"start": v(-0.95, -0.91) * mm, "end": v(-0.95, -0.91) * mm});
            skLineSegment(sketch, "E1666", {"start": v(-0.95, -0.91) * mm, "end": v(-0.96, -0.92) * mm});
            skLineSegment(sketch, "E1667", {"start": v(-0.96, -0.92) * mm, "end": v(-0.96, -0.94) * mm});
            skLineSegment(sketch, "E1668", {"start": v(-0.96, -0.94) * mm, "end": v(-0.95, -0.98) * mm});
            skLineSegment(sketch, "E1669", {"start": v(-0.95, -0.98) * mm, "end": v(-0.94, -1.03) * mm});
            skLineSegment(sketch, "E1670", {"start": v(-0.94, -1.03) * mm, "end": v(-0.93, -1.1) * mm});
            skLineSegment(sketch, "E1671", {"start": v(-0.93, -1.1) * mm, "end": v(-0.91, -1.22) * mm});
            skLineSegment(sketch, "E1672", {"start": v(-0.91, -1.22) * mm, "end": v(-0.9, -1.33) * mm});
            skLineSegment(sketch, "E1673", {"start": v(-0.9, -1.33) * mm, "end": v(-0.88, -1.41) * mm});
            skLineSegment(sketch, "E1674", {"start": v(-0.88, -1.41) * mm, "end": v(-0.87, -1.48) * mm});
            skLineSegment(sketch, "E1675", {"start": v(-0.87, -1.48) * mm, "end": v(-0.86, -1.52) * mm});
            skLineSegment(sketch, "E1676", {"start": v(-0.86, -1.52) * mm, "end": v(-0.85, -1.56) * mm});
            skLineSegment(sketch, "E1677", {"start": v(-0.85, -1.56) * mm, "end": v(-0.83, -1.58) * mm});
            skLineSegment(sketch, "E1678", {"start": v(-0.83, -1.58) * mm, "end": v(-0.82, -1.6) * mm});
            skLineSegment(sketch, "E1679", {"start": v(-0.82, -1.6) * mm, "end": v(-0.8, -1.61) * mm});
            skLineSegment(sketch, "E1680", {"start": v(-0.8, -1.61) * mm, "end": v(-0.76, -1.64) * mm});
            skLineSegment(sketch, "E1681", {"start": v(-0.76, -1.64) * mm, "end": v(-0.71, -1.67) * mm});
            skLineSegment(sketch, "E1682", {"start": v(-0.71, -1.67) * mm, "end": v(-0.66, -1.7) * mm});
            skLineSegment(sketch, "E1683", {"start": v(-0.66, -1.7) * mm, "end": v(-0.62, -1.71) * mm});
            skLineSegment(sketch, "E1684", {"start": v(-0.62, -1.71) * mm, "end": v(-0.56, -1.72) * mm});
            skLineSegment(sketch, "E1685", {"start": v(-0.56, -1.72) * mm, "end": v(-0.48, -1.72) * mm});
            skLineSegment(sketch, "E1686", {"start": v(-0.48, -1.72) * mm, "end": v(-0.4, -1.72) * mm});
            skLineSegment(sketch, "E1687", {"start": v(-0.4, -1.72) * mm, "end": v(-0.35, -1.7) * mm});
            skLineSegment(sketch, "E1688", {"start": v(5.63, -1.25) * mm, "end": v(5.66, -1.24) * mm});
            skLineSegment(sketch, "E1689", {"start": v(5.66, -1.24) * mm, "end": v(5.7, -1.23) * mm});
            skLineSegment(sketch, "E1690", {"start": v(5.7, -1.23) * mm, "end": v(5.75, -1.22) * mm});
            skLineSegment(sketch, "E1691", {"start": v(5.75, -1.22) * mm, "end": v(5.8, -1.22) * mm});
            skLineSegment(sketch, "E1692", {"start": v(5.8, -1.22) * mm, "end": v(5.88, -1.2) * mm});
            skLineSegment(sketch, "E1693", {"start": v(5.88, -1.2) * mm, "end": v(5.98, -1.15) * mm});
            skLineSegment(sketch, "E1694", {"start": v(5.98, -1.15) * mm, "end": v(6.07, -1.1) * mm});
            skLineSegment(sketch, "E1695", {"start": v(6.07, -1.1) * mm, "end": v(6.15, -1.06) * mm});
            skLineSegment(sketch, "E1696", {"start": v(6.15, -1.06) * mm, "end": v(6.18, -1.03) * mm});
            skLineSegment(sketch, "E1697", {"start": v(6.18, -1.03) * mm, "end": v(6.22, -1) * mm});
            skLineSegment(sketch, "E1698", {"start": v(6.22, -1) * mm, "end": v(6.27, -0.96) * mm});
            skLineSegment(sketch, "E1699", {"start": v(6.27, -0.96) * mm, "end": v(6.31, -0.92) * mm});
            skLineSegment(sketch, "E1700", {"start": v(6.31, -0.92) * mm, "end": v(6.36, -0.88) * mm});
            skLineSegment(sketch, "E1701", {"start": v(6.36, -0.88) * mm, "end": v(6.41, -0.83) * mm});
            skLineSegment(sketch, "E1702", {"start": v(6.41, -0.83) * mm, "end": v(6.46, -0.8) * mm});
            skLineSegment(sketch, "E1703", {"start": v(6.46, -0.8) * mm, "end": v(6.5, -0.77) * mm});
            skLineSegment(sketch, "E1704", {"start": v(6.5, -0.77) * mm, "end": v(6.52, -0.76) * mm});
            skLineSegment(sketch, "E1705", {"start": v(6.52, -0.76) * mm, "end": v(6.54, -0.74) * mm});
            skLineSegment(sketch, "E1706", {"start": v(6.54, -0.74) * mm, "end": v(6.56, -0.73) * mm});
            skLineSegment(sketch, "E1707", {"start": v(6.56, -0.73) * mm, "end": v(6.56, -0.72) * mm});
            skLineSegment(sketch, "E1708", {"start": v(6.56, -0.72) * mm, "end": v(6.55, -0.71) * mm});
            skLineSegment(sketch, "E1709", {"start": v(6.55, -0.71) * mm, "end": v(6.53, -0.7) * mm});
            skLineSegment(sketch, "E1710", {"start": v(6.53, -0.7) * mm, "end": v(6.5, -0.7) * mm});
            skLineSegment(sketch, "E1711", {"start": v(6.5, -0.7) * mm, "end": v(6.47, -0.7) * mm});
            skLineSegment(sketch, "E1712", {"start": v(6.47, -0.7) * mm, "end": v(6.32, -0.7) * mm});
            skLineSegment(sketch, "E1713", {"start": v(6.32, -0.7) * mm, "end": v(6.14, -0.69) * mm});
            skLineSegment(sketch, "E1714", {"start": v(6.14, -0.69) * mm, "end": v(5.95, -0.67) * mm});
            skLineSegment(sketch, "E1715", {"start": v(5.95, -0.67) * mm, "end": v(5.8, -0.66) * mm});
            skLineSegment(sketch, "E1716", {"start": v(5.8, -0.66) * mm, "end": v(5.65, -0.64) * mm});
            skLineSegment(sketch, "E1717", {"start": v(5.65, -0.64) * mm, "end": v(5.5, -0.63) * mm});
            skLineSegment(sketch, "E1718", {"start": v(5.5, -0.63) * mm, "end": v(5.34, -0.6) * mm});
            skLineSegment(sketch, "E1719", {"start": v(5.34, -0.6) * mm, "end": v(5.19, -0.59) * mm});
            skLineSegment(sketch, "E1720", {"start": v(5.19, -0.59) * mm, "end": v(5.04, -0.57) * mm});
            skLineSegment(sketch, "E1721", {"start": v(5.04, -0.57) * mm, "end": v(4.92, -0.55) * mm});
            skLineSegment(sketch, "E1722", {"start": v(4.92, -0.55) * mm, "end": v(4.82, -0.54) * mm});
            skLineSegment(sketch, "E1723", {"start": v(4.82, -0.54) * mm, "end": v(4.75, -0.53) * mm});
            skLineSegment(sketch, "E1724", {"start": v(4.75, -0.53) * mm, "end": v(4.57, -0.5) * mm});
            skLineSegment(sketch, "E1725", {"start": v(4.57, -0.5) * mm, "end": v(4.44, -0.47) * mm});
            skLineSegment(sketch, "E1726", {"start": v(4.44, -0.47) * mm, "end": v(4.37, -0.45) * mm});
            skLineSegment(sketch, "E1727", {"start": v(4.37, -0.45) * mm, "end": v(4.33, -0.44) * mm});
            skLineSegment(sketch, "E1728", {"start": v(4.33, -0.44) * mm, "end": v(4.29, -0.43) * mm});
            skLineSegment(sketch, "E1729", {"start": v(4.29, -0.43) * mm, "end": v(4.24, -0.42) * mm});
            skLineSegment(sketch, "E1730", {"start": v(4.24, -0.42) * mm, "end": v(4.2, -0.42) * mm});
            skLineSegment(sketch, "E1731", {"start": v(4.2, -0.42) * mm, "end": v(4.13, -0.4) * mm});
            skLineSegment(sketch, "E1732", {"start": v(4.13, -0.4) * mm, "end": v(4.06, -0.4) * mm});
            skLineSegment(sketch, "E1733", {"start": v(4.06, -0.4) * mm, "end": v(4, -0.39) * mm});
            skLineSegment(sketch, "E1734", {"start": v(4, -0.39) * mm, "end": v(3.95, -0.4) * mm});
            skLineSegment(sketch, "E1735", {"start": v(3.95, -0.4) * mm, "end": v(3.91, -0.4) * mm});
            skLineSegment(sketch, "E1736", {"start": v(3.91, -0.4) * mm, "end": v(3.9, -0.41) * mm});
            skLineSegment(sketch, "E1737", {"start": v(3.9, -0.41) * mm, "end": v(3.88, -0.43) * mm});
            skLineSegment(sketch, "E1738", {"start": v(3.88, -0.43) * mm, "end": v(3.87, -0.45) * mm});
            skLineSegment(sketch, "E1739", {"start": v(3.87, -0.45) * mm, "end": v(3.86, -0.47) * mm});
            skLineSegment(sketch, "E1740", {"start": v(3.86, -0.47) * mm, "end": v(3.85, -0.52) * mm});
            skLineSegment(sketch, "E1741", {"start": v(3.85, -0.52) * mm, "end": v(3.85, -0.58) * mm});
            skLineSegment(sketch, "E1742", {"start": v(3.85, -0.58) * mm, "end": v(3.88, -0.66) * mm});
            skLineSegment(sketch, "E1743", {"start": v(3.88, -0.66) * mm, "end": v(3.94, -0.78) * mm});
            skLineSegment(sketch, "E1744", {"start": v(3.94, -0.78) * mm, "end": v(3.98, -0.85) * mm});
            skLineSegment(sketch, "E1745", {"start": v(3.98, -0.85) * mm, "end": v(4.01, -0.92) * mm});
            skLineSegment(sketch, "E1746", {"start": v(4.01, -0.92) * mm, "end": v(4.04, -0.98) * mm});
            skLineSegment(sketch, "E1747", {"start": v(4.04, -0.98) * mm, "end": v(4.06, -1.02) * mm});
            skLineSegment(sketch, "E1748", {"start": v(4.06, -1.02) * mm, "end": v(4.07, -1.05) * mm});
            skLineSegment(sketch, "E1749", {"start": v(4.07, -1.05) * mm, "end": v(4.08, -1.08) * mm});
            skLineSegment(sketch, "E1750", {"start": v(4.08, -1.08) * mm, "end": v(4.1, -1.1) * mm});
            skLineSegment(sketch, "E1751", {"start": v(4.1, -1.1) * mm, "end": v(4.1, -1.11) * mm});
            skLineSegment(sketch, "E1752", {"start": v(4.1, -1.11) * mm, "end": v(4.13, -1.12) * mm});
            skLineSegment(sketch, "E1753", {"start": v(4.13, -1.12) * mm, "end": v(4.17, -1.14) * mm});
            skLineSegment(sketch, "E1754", {"start": v(4.17, -1.14) * mm, "end": v(4.23, -1.15) * mm});
            skLineSegment(sketch, "E1755", {"start": v(4.23, -1.15) * mm, "end": v(4.3, -1.16) * mm});
            skLineSegment(sketch, "E1756", {"start": v(4.3, -1.16) * mm, "end": v(4.39, -1.18) * mm});
            skLineSegment(sketch, "E1757", {"start": v(4.39, -1.18) * mm, "end": v(4.46, -1.19) * mm});
            skLineSegment(sketch, "E1758", {"start": v(4.46, -1.19) * mm, "end": v(4.54, -1.19) * mm});
            skLineSegment(sketch, "E1759", {"start": v(4.54, -1.19) * mm, "end": v(4.64, -1.18) * mm});
            skLineSegment(sketch, "E1760", {"start": v(4.64, -1.18) * mm, "end": v(4.72, -1.18) * mm});
            skLineSegment(sketch, "E1761", {"start": v(4.72, -1.18) * mm, "end": v(4.79, -1.18) * mm});
            skLineSegment(sketch, "E1762", {"start": v(4.79, -1.18) * mm, "end": v(4.84, -1.17) * mm});
            skLineSegment(sketch, "E1763", {"start": v(4.84, -1.17) * mm, "end": v(4.88, -1.17) * mm});
            skLineSegment(sketch, "E1764", {"start": v(4.88, -1.17) * mm, "end": v(4.91, -1.16) * mm});
            skLineSegment(sketch, "E1765", {"start": v(4.91, -1.16) * mm, "end": v(4.96, -1.16) * mm});
            skLineSegment(sketch, "E1766", {"start": v(4.96, -1.16) * mm, "end": v(5, -1.16) * mm});
            skLineSegment(sketch, "E1767", {"start": v(5, -1.16) * mm, "end": v(5.06, -1.16) * mm});
            skLineSegment(sketch, "E1768", {"start": v(5.06, -1.16) * mm, "end": v(5.13, -1.16) * mm});
            skLineSegment(sketch, "E1769", {"start": v(5.13, -1.16) * mm, "end": v(5.2, -1.16) * mm});
            skLineSegment(sketch, "E1770", {"start": v(5.2, -1.16) * mm, "end": v(5.25, -1.17) * mm});
            skLineSegment(sketch, "E1771", {"start": v(5.25, -1.17) * mm, "end": v(5.32, -1.19) * mm});
            skLineSegment(sketch, "E1772", {"start": v(5.32, -1.19) * mm, "end": v(5.37, -1.2) * mm});
            skLineSegment(sketch, "E1773", {"start": v(5.37, -1.2) * mm, "end": v(5.42, -1.22) * mm});
            skLineSegment(sketch, "E1774", {"start": v(5.42, -1.22) * mm, "end": v(5.47, -1.23) * mm});
            skLineSegment(sketch, "E1775", {"start": v(5.47, -1.23) * mm, "end": v(5.5, -1.24) * mm});
            skLineSegment(sketch, "E1776", {"start": v(5.5, -1.24) * mm, "end": v(5.53, -1.26) * mm});
            skLineSegment(sketch, "E1777", {"start": v(5.53, -1.26) * mm, "end": v(5.55, -1.26) * mm});
            skLineSegment(sketch, "E1778", {"start": v(5.55, -1.26) * mm, "end": v(5.58, -1.26) * mm});
            skLineSegment(sketch, "E1779", {"start": v(5.58, -1.26) * mm, "end": v(5.63, -1.25) * mm});
            skLineSegment(sketch, "E1780", {"start": v(3.9, -1.04) * mm, "end": v(3.9, -1.02) * mm});
            skLineSegment(sketch, "E1781", {"start": v(3.9, -1.02) * mm, "end": v(3.88, -0.98) * mm});
            skLineSegment(sketch, "E1782", {"start": v(3.88, -0.98) * mm, "end": v(3.86, -0.93) * mm});
            skLineSegment(sketch, "E1783", {"start": v(3.86, -0.93) * mm, "end": v(3.83, -0.87) * mm});
            skLineSegment(sketch, "E1784", {"start": v(3.83, -0.87) * mm, "end": v(3.8, -0.81) * mm});
            skLineSegment(sketch, "E1785", {"start": v(3.8, -0.81) * mm, "end": v(3.75, -0.74) * mm});
            skLineSegment(sketch, "E1786", {"start": v(3.75, -0.74) * mm, "end": v(3.71, -0.68) * mm});
            skLineSegment(sketch, "E1787", {"start": v(3.71, -0.68) * mm, "end": v(3.68, -0.62) * mm});
            skLineSegment(sketch, "E1788", {"start": v(3.68, -0.62) * mm, "end": v(3.62, -0.54) * mm});
            skLineSegment(sketch, "E1789", {"start": v(3.62, -0.54) * mm, "end": v(3.56, -0.47) * mm});
            skLineSegment(sketch, "E1790", {"start": v(3.56, -0.47) * mm, "end": v(3.51, -0.41) * mm});
            skLineSegment(sketch, "E1791", {"start": v(3.51, -0.41) * mm, "end": v(3.44, -0.35) * mm});
            skLineSegment(sketch, "E1792", {"start": v(3.44, -0.35) * mm, "end": v(3.4, -0.3) * mm});
            skLineSegment(sketch, "E1793", {"start": v(3.4, -0.3) * mm, "end": v(3.34, -0.25) * mm});
            skLineSegment(sketch, "E1794", {"start": v(3.34, -0.25) * mm, "end": v(3.3, -0.22) * mm});
            skLineSegment(sketch, "E1795", {"start": v(3.3, -0.22) * mm, "end": v(3.26, -0.2) * mm});
            skLineSegment(sketch, "E1796", {"start": v(3.26, -0.2) * mm, "end": v(3.08, -0.1) * mm});
            skLineSegment(sketch, "E1797", {"start": v(3.08, -0.1) * mm, "end": v(2.93, 0) * mm});
            skLineSegment(sketch, "E1798", {"start": v(2.93, 0) * mm, "end": v(2.8, 0.06) * mm});
            skLineSegment(sketch, "E1799", {"start": v(2.8, 0.06) * mm, "end": v(2.69, 0.11) * mm});
            skLineSegment(sketch, "E1800", {"start": v(2.69, 0.11) * mm, "end": v(2.58, 0.15) * mm});
            skLineSegment(sketch, "E1801", {"start": v(2.58, 0.15) * mm, "end": v(2.47, 0.18) * mm});
            skLineSegment(sketch, "E1802", {"start": v(2.47, 0.18) * mm, "end": v(2.36, 0.2) * mm});
            skLineSegment(sketch, "E1803", {"start": v(2.36, 0.2) * mm, "end": v(2.25, 0.23) * mm});
            skLineSegment(sketch, "E1804", {"start": v(2.25, 0.23) * mm, "end": v(2.17, 0.24) * mm});
            skLineSegment(sketch, "E1805", {"start": v(2.17, 0.24) * mm, "end": v(2.06, 0.24) * mm});
            skLineSegment(sketch, "E1806", {"start": v(2.06, 0.24) * mm, "end": v(1.92, 0.25) * mm});
            skLineSegment(sketch, "E1807", {"start": v(1.92, 0.25) * mm, "end": v(1.78, 0.25) * mm});
            skLineSegment(sketch, "E1808", {"start": v(1.78, 0.25) * mm, "end": v(1.63, 0.26) * mm});
            skLineSegment(sketch, "E1809", {"start": v(1.63, 0.26) * mm, "end": v(1.5, 0.25) * mm});
            skLineSegment(sketch, "E1810", {"start": v(1.5, 0.25) * mm, "end": v(1.38, 0.25) * mm});
            skLineSegment(sketch, "E1811", {"start": v(1.38, 0.25) * mm, "end": v(1.29, 0.25) * mm});
            skLineSegment(sketch, "E1812", {"start": v(1.29, 0.25) * mm, "end": v(1.18, 0.23) * mm});
            skLineSegment(sketch, "E1813", {"start": v(1.18, 0.23) * mm, "end": v(1.08, 0.21) * mm});
            skLineSegment(sketch, "E1814", {"start": v(1.08, 0.21) * mm, "end": v(0.97, 0.2) * mm});
            skLineSegment(sketch, "E1815", {"start": v(0.97, 0.2) * mm, "end": v(0.87, 0.17) * mm});
            skLineSegment(sketch, "E1816", {"start": v(0.87, 0.17) * mm, "end": v(0.78, 0.14) * mm});
            skLineSegment(sketch, "E1817", {"start": v(0.78, 0.14) * mm, "end": v(0.7, 0.12) * mm});
            skLineSegment(sketch, "E1818", {"start": v(0.7, 0.12) * mm, "end": v(0.66, 0.1) * mm});
            skLineSegment(sketch, "E1819", {"start": v(0.66, 0.1) * mm, "end": v(0.64, 0.07) * mm});
            skLineSegment(sketch, "E1820", {"start": v(0.64, 0.07) * mm, "end": v(0.64, 0.05) * mm});
            skLineSegment(sketch, "E1821", {"start": v(0.64, 0.05) * mm, "end": v(0.64, 0) * mm});
            skLineSegment(sketch, "E1822", {"start": v(0.64, 0) * mm, "end": v(0.64, -0.07) * mm});
            skLineSegment(sketch, "E1823", {"start": v(0.64, -0.07) * mm, "end": v(0.65, -0.15) * mm});
            skLineSegment(sketch, "E1824", {"start": v(0.65, -0.15) * mm, "end": v(0.65, -0.24) * mm});
            skLineSegment(sketch, "E1825", {"start": v(0.65, -0.24) * mm, "end": v(0.66, -0.31) * mm});
            skLineSegment(sketch, "E1826", {"start": v(0.66, -0.31) * mm, "end": v(0.67, -0.38) * mm});
            skLineSegment(sketch, "E1827", {"start": v(0.67, -0.38) * mm, "end": v(0.67, -0.42) * mm});
            skLineSegment(sketch, "E1828", {"start": v(0.67, -0.42) * mm, "end": v(0.68, -0.47) * mm});
            skLineSegment(sketch, "E1829", {"start": v(0.68, -0.47) * mm, "end": v(0.72, -0.47) * mm});
            skLineSegment(sketch, "E1830", {"start": v(0.72, -0.47) * mm, "end": v(0.8, -0.47) * mm});
            skLineSegment(sketch, "E1831", {"start": v(0.8, -0.47) * mm, "end": v(0.91, -0.48) * mm});
            skLineSegment(sketch, "E1832", {"start": v(0.91, -0.48) * mm, "end": v(1.05, -0.49) * mm});
            skLineSegment(sketch, "E1833", {"start": v(1.05, -0.49) * mm, "end": v(1.2, -0.5) * mm});
            skLineSegment(sketch, "E1834", {"start": v(1.2, -0.5) * mm, "end": v(1.34, -0.52) * mm});
            skLineSegment(sketch, "E1835", {"start": v(1.34, -0.52) * mm, "end": v(1.48, -0.55) * mm});
            skLineSegment(sketch, "E1836", {"start": v(1.48, -0.55) * mm, "end": v(1.61, -0.57) * mm});
            skLineSegment(sketch, "E1837", {"start": v(1.61, -0.57) * mm, "end": v(1.71, -0.6) * mm});
            skLineSegment(sketch, "E1838", {"start": v(1.71, -0.6) * mm, "end": v(1.78, -0.6) * mm});
            skLineSegment(sketch, "E1839", {"start": v(1.78, -0.6) * mm, "end": v(1.85, -0.62) * mm});
            skLineSegment(sketch, "E1840", {"start": v(1.85, -0.62) * mm, "end": v(1.95, -0.65) * mm});
            skLineSegment(sketch, "E1841", {"start": v(1.95, -0.65) * mm, "end": v(2.08, -0.69) * mm});
            skLineSegment(sketch, "E1842", {"start": v(2.08, -0.69) * mm, "end": v(2.22, -0.73) * mm});
            skLineSegment(sketch, "E1843", {"start": v(2.22, -0.73) * mm, "end": v(2.34, -0.78) * mm});
            skLineSegment(sketch, "E1844", {"start": v(2.34, -0.78) * mm, "end": v(2.39, -0.8) * mm});
            skLineSegment(sketch, "E1845", {"start": v(2.39, -0.8) * mm, "end": v(2.45, -0.83) * mm});
            skLineSegment(sketch, "E1846", {"start": v(2.45, -0.83) * mm, "end": v(2.5, -0.86) * mm});
            skLineSegment(sketch, "E1847", {"start": v(2.5, -0.86) * mm, "end": v(2.55, -0.9) * mm});
            skLineSegment(sketch, "E1848", {"start": v(2.55, -0.9) * mm, "end": v(2.66, -0.96) * mm});
            skLineSegment(sketch, "E1849", {"start": v(2.66, -0.96) * mm, "end": v(2.8, -0.95) * mm});
            skLineSegment(sketch, "E1850", {"start": v(2.8, -0.95) * mm, "end": v(2.94, -0.94) * mm});
            skLineSegment(sketch, "E1851", {"start": v(2.94, -0.94) * mm, "end": v(3.09, -0.94) * mm});
            skLineSegment(sketch, "E1852", {"start": v(3.09, -0.94) * mm, "end": v(3.23, -0.94) * mm});
            skLineSegment(sketch, "E1853", {"start": v(3.23, -0.94) * mm, "end": v(3.38, -0.95) * mm});
            skLineSegment(sketch, "E1854", {"start": v(3.38, -0.95) * mm, "end": v(3.51, -0.97) * mm});
            skLineSegment(sketch, "E1855", {"start": v(3.51, -0.97) * mm, "end": v(3.64, -0.99) * mm});
            skLineSegment(sketch, "E1856", {"start": v(3.64, -0.99) * mm, "end": v(3.75, -1.01) * mm});
            skLineSegment(sketch, "E1857", {"start": v(3.75, -1.01) * mm, "end": v(3.83, -1.04) * mm});
            skLineSegment(sketch, "E1858", {"start": v(3.83, -1.04) * mm, "end": v(3.87, -1.05) * mm});
            skLineSegment(sketch, "E1859", {"start": v(3.87, -1.05) * mm, "end": v(3.9, -1.05) * mm});
            skLineSegment(sketch, "E1860", {"start": v(3.9, -1.05) * mm, "end": v(3.9, -1.05) * mm});
            skLineSegment(sketch, "E1861", {"start": v(3.9, -1.05) * mm, "end": v(3.9, -1.04) * mm});
            skLineSegment(sketch, "E1862", {"start": v(-5.48, -0.7) * mm, "end": v(-5.42, -0.68) * mm});
            skLineSegment(sketch, "E1863", {"start": v(-5.42, -0.68) * mm, "end": v(-5.36, -0.66) * mm});
            skLineSegment(sketch, "E1864", {"start": v(-5.36, -0.66) * mm, "end": v(-5.3, -0.65) * mm});
            skLineSegment(sketch, "E1865", {"start": v(-5.3, -0.65) * mm, "end": v(-5.26, -0.64) * mm});
            skLineSegment(sketch, "E1866", {"start": v(-5.26, -0.64) * mm, "end": v(-5.16, -0.63) * mm});
            skLineSegment(sketch, "E1867", {"start": v(-5.16, -0.63) * mm, "end": v(-5.03, -0.63) * mm});
            skLineSegment(sketch, "E1868", {"start": v(-5.03, -0.63) * mm, "end": v(-4.89, -0.63) * mm});
            skLineSegment(sketch, "E1869", {"start": v(-4.89, -0.63) * mm, "end": v(-4.75, -0.64) * mm});
            skLineSegment(sketch, "E1870", {"start": v(-4.75, -0.64) * mm, "end": v(-4.65, -0.64) * mm});
            skLineSegment(sketch, "E1871", {"start": v(-4.65, -0.64) * mm, "end": v(-4.6, -0.52) * mm});
            skLineSegment(sketch, "E1872", {"start": v(-4.6, -0.52) * mm, "end": v(-4.53, -0.4) * mm});
            skLineSegment(sketch, "E1873", {"start": v(-4.53, -0.4) * mm, "end": v(-4.46, -0.3) * mm});
            skLineSegment(sketch, "E1874", {"start": v(-4.46, -0.3) * mm, "end": v(-4.37, -0.18) * mm});
            skLineSegment(sketch, "E1875", {"start": v(-4.37, -0.18) * mm, "end": v(-4.25, -0.05) * mm});
            skLineSegment(sketch, "E1876", {"start": v(-4.25, -0.05) * mm, "end": v(-4.09, 0.1) * mm});
            skLineSegment(sketch, "E1877", {"start": v(-4.09, 0.1) * mm, "end": v(-3.91, 0.25) * mm});
            skLineSegment(sketch, "E1878", {"start": v(-3.91, 0.25) * mm, "end": v(-3.71, 0.38) * mm});
            skLineSegment(sketch, "E1879", {"start": v(-3.71, 0.38) * mm, "end": v(-3.47, 0.5) * mm});
            skLineSegment(sketch, "E1880", {"start": v(-3.47, 0.5) * mm, "end": v(-3.38, 0.55) * mm});
            skLineSegment(sketch, "E1881", {"start": v(-3.38, 0.55) * mm, "end": v(-3.3, 0.59) * mm});
            skLineSegment(sketch, "E1882", {"start": v(-3.3, 0.59) * mm, "end": v(-3.26, 0.61) * mm});
            skLineSegment(sketch, "E1883", {"start": v(-3.26, 0.61) * mm, "end": v(-3.24, 0.63) * mm});
            skLineSegment(sketch, "E1884", {"start": v(-3.24, 0.63) * mm, "end": v(-3.26, 0.63) * mm});
            skLineSegment(sketch, "E1885", {"start": v(-3.26, 0.63) * mm, "end": v(-3.3, 0.63) * mm});
            skLineSegment(sketch, "E1886", {"start": v(-3.3, 0.63) * mm, "end": v(-3.38, 0.63) * mm});
            skLineSegment(sketch, "E1887", {"start": v(-3.38, 0.63) * mm, "end": v(-3.47, 0.62) * mm});
            skLineSegment(sketch, "E1888", {"start": v(-3.47, 0.62) * mm, "end": v(-3.58, 0.6) * mm});
            skLineSegment(sketch, "E1889", {"start": v(-3.58, 0.6) * mm, "end": v(-3.73, 0.58) * mm});
            skLineSegment(sketch, "E1890", {"start": v(-3.73, 0.58) * mm, "end": v(-3.9, 0.54) * mm});
            skLineSegment(sketch, "E1891", {"start": v(-3.9, 0.54) * mm, "end": v(-4.1, 0.5) * mm});
            skLineSegment(sketch, "E1892", {"start": v(-4.1, 0.5) * mm, "end": v(-4.3, 0.44) * mm});
            skLineSegment(sketch, "E1893", {"start": v(-4.3, 0.44) * mm, "end": v(-4.5, 0.4) * mm});
            skLineSegment(sketch, "E1894", {"start": v(-4.5, 0.4) * mm, "end": v(-4.68, 0.34) * mm});
            skLineSegment(sketch, "E1895", {"start": v(-4.68, 0.34) * mm, "end": v(-4.83, 0.3) * mm});
            skLineSegment(sketch, "E1896", {"start": v(-4.83, 0.3) * mm, "end": v(-5.27, 0.12) * mm});
            skLineSegment(sketch, "E1897", {"start": v(-5.27, 0.12) * mm, "end": v(-5.71, -0.11) * mm});
            skLineSegment(sketch, "E1898", {"start": v(-5.71, -0.11) * mm, "end": v(-5.76, -0.14) * mm});
            skLineSegment(sketch, "E1899", {"start": v(-5.76, -0.14) * mm, "end": v(-5.82, -0.17) * mm});
            skLineSegment(sketch, "E1900", {"start": v(-5.82, -0.17) * mm, "end": v(-5.9, -0.21) * mm});
            skLineSegment(sketch, "E1901", {"start": v(-5.9, -0.21) * mm, "end": v(-5.97, -0.25) * mm});
            skLineSegment(sketch, "E1902", {"start": v(-5.97, -0.25) * mm, "end": v(-6.05, -0.3) * mm});
            skLineSegment(sketch, "E1903", {"start": v(-6.05, -0.3) * mm, "end": v(-6.12, -0.32) * mm});
            skLineSegment(sketch, "E1904", {"start": v(-6.12, -0.32) * mm, "end": v(-6.18, -0.35) * mm});
            skLineSegment(sketch, "E1905", {"start": v(-6.18, -0.35) * mm, "end": v(-6.23, -0.37) * mm});
            skLineSegment(sketch, "E1906", {"start": v(-6.23, -0.37) * mm, "end": v(-6.26, -0.38) * mm});
            skLineSegment(sketch, "E1907", {"start": v(-6.26, -0.38) * mm, "end": v(-6.3, -0.4) * mm});
            skLineSegment(sketch, "E1908", {"start": v(-6.3, -0.4) * mm, "end": v(-6.35, -0.42) * mm});
            skLineSegment(sketch, "E1909", {"start": v(-6.35, -0.42) * mm, "end": v(-6.4, -0.44) * mm});
            skLineSegment(sketch, "E1910", {"start": v(-6.4, -0.44) * mm, "end": v(-6.54, -0.5) * mm});
            skLineSegment(sketch, "E1911", {"start": v(-6.54, -0.5) * mm, "end": v(-6.68, -0.53) * mm});
            skLineSegment(sketch, "E1912", {"start": v(-6.68, -0.53) * mm, "end": v(-6.73, -0.54) * mm});
            skLineSegment(sketch, "E1913", {"start": v(-6.73, -0.54) * mm, "end": v(-6.76, -0.54) * mm});
            skLineSegment(sketch, "E1914", {"start": v(-6.76, -0.54) * mm, "end": v(-6.76, -0.55) * mm});
            skLineSegment(sketch, "E1915", {"start": v(-6.76, -0.55) * mm, "end": v(-6.76, -0.55) * mm});
            skLineSegment(sketch, "E1916", {"start": v(-6.76, -0.55) * mm, "end": v(-6.74, -0.56) * mm});
            skLineSegment(sketch, "E1917", {"start": v(-6.74, -0.56) * mm, "end": v(-6.72, -0.56) * mm});
            skLineSegment(sketch, "E1918", {"start": v(-6.72, -0.56) * mm, "end": v(-6.7, -0.57) * mm});
            skLineSegment(sketch, "E1919", {"start": v(-6.7, -0.57) * mm, "end": v(-6.65, -0.58) * mm});
            skLineSegment(sketch, "E1920", {"start": v(-6.65, -0.58) * mm, "end": v(-6.6, -0.58) * mm});
            skLineSegment(sketch, "E1921", {"start": v(-6.6, -0.58) * mm, "end": v(-6.54, -0.6) * mm});
            skLineSegment(sketch, "E1922", {"start": v(-6.54, -0.6) * mm, "end": v(-6.46, -0.6) * mm});
            skLineSegment(sketch, "E1923", {"start": v(-6.46, -0.6) * mm, "end": v(-6.38, -0.63) * mm});
            skLineSegment(sketch, "E1924", {"start": v(-6.38, -0.63) * mm, "end": v(-6.3, -0.65) * mm});
            skLineSegment(sketch, "E1925", {"start": v(-6.3, -0.65) * mm, "end": v(-6.05, -0.7) * mm});
            skLineSegment(sketch, "E1926", {"start": v(-6.05, -0.7) * mm, "end": v(-5.84, -0.72) * mm});
            skLineSegment(sketch, "E1927", {"start": v(-5.84, -0.72) * mm, "end": v(-5.65, -0.72) * mm});
            skLineSegment(sketch, "E1928", {"start": v(-5.65, -0.72) * mm, "end": v(-5.48, -0.7) * mm});
            skLineSegment(sketch, "E1929", {"start": v(-3.49, -0.7) * mm, "end": v(-3.4, -0.68) * mm});
            skLineSegment(sketch, "E1930", {"start": v(-3.4, -0.68) * mm, "end": v(-3.32, -0.65) * mm});
            skLineSegment(sketch, "E1931", {"start": v(-3.32, -0.65) * mm, "end": v(-3.27, -0.63) * mm});
            skLineSegment(sketch, "E1932", {"start": v(-3.27, -0.63) * mm, "end": v(-3.22, -0.6) * mm});
            skLineSegment(sketch, "E1933", {"start": v(-3.22, -0.6) * mm, "end": v(-3.16, -0.58) * mm});
            skLineSegment(sketch, "E1934", {"start": v(-3.16, -0.58) * mm, "end": v(-3.1, -0.55) * mm});
            skLineSegment(sketch, "E1935", {"start": v(-3.1, -0.55) * mm, "end": v(-3, -0.51) * mm});
            skLineSegment(sketch, "E1936", {"start": v(-3, -0.51) * mm, "end": v(-2.9, -0.47) * mm});
            skLineSegment(sketch, "E1937", {"start": v(-2.9, -0.47) * mm, "end": v(-2.76, -0.42) * mm});
            skLineSegment(sketch, "E1938", {"start": v(-2.76, -0.42) * mm, "end": v(-2.57, -0.35) * mm});
            skLineSegment(sketch, "E1939", {"start": v(-2.57, -0.35) * mm, "end": v(-2.46, -0.32) * mm});
            skLineSegment(sketch, "E1940", {"start": v(-2.46, -0.32) * mm, "end": v(-2.33, -0.29) * mm});
            skLineSegment(sketch, "E1941", {"start": v(-2.33, -0.29) * mm, "end": v(-2.2, -0.26) * mm});
            skLineSegment(sketch, "E1942", {"start": v(-2.2, -0.26) * mm, "end": v(-2.07, -0.24) * mm});
            skLineSegment(sketch, "E1943", {"start": v(-2.07, -0.24) * mm, "end": v(-1.9, -0.23) * mm});
            skLineSegment(sketch, "E1944", {"start": v(-1.9, -0.23) * mm, "end": v(-1.72, -0.23) * mm});
            skLineSegment(sketch, "E1945", {"start": v(-1.72, -0.23) * mm, "end": v(-1.55, -0.24) * mm});
            skLineSegment(sketch, "E1946", {"start": v(-1.55, -0.24) * mm, "end": v(-1.4, -0.26) * mm});
            skLineSegment(sketch, "E1947", {"start": v(-1.4, -0.26) * mm, "end": v(-1.35, -0.26) * mm});
            skLineSegment(sketch, "E1948", {"start": v(-1.35, -0.26) * mm, "end": v(-1.3, -0.27) * mm});
            skLineSegment(sketch, "E1949", {"start": v(-1.3, -0.27) * mm, "end": v(-1.27, -0.27) * mm});
            skLineSegment(sketch, "E1950", {"start": v(-1.27, -0.27) * mm, "end": v(-1.26, -0.27) * mm});
            skLineSegment(sketch, "E1951", {"start": v(-1.26, -0.27) * mm, "end": v(-1.25, -0.25) * mm});
            skLineSegment(sketch, "E1952", {"start": v(-1.25, -0.25) * mm, "end": v(-1.25, -0.22) * mm});
            skLineSegment(sketch, "E1953", {"start": v(-1.25, -0.22) * mm, "end": v(-1.27, -0.17) * mm});
            skLineSegment(sketch, "E1954", {"start": v(-1.27, -0.17) * mm, "end": v(-1.29, -0.11) * mm});
            skLineSegment(sketch, "E1955", {"start": v(-1.29, -0.11) * mm, "end": v(-1.31, -0.05) * mm});
            skLineSegment(sketch, "E1956", {"start": v(-1.31, -0.05) * mm, "end": v(-1.34, 0) * mm});
            skLineSegment(sketch, "E1957", {"start": v(-1.34, 0) * mm, "end": v(-1.37, 0.05) * mm});
            skLineSegment(sketch, "E1958", {"start": v(-1.37, 0.05) * mm, "end": v(-1.4, 0.09) * mm});
            skLineSegment(sketch, "E1959", {"start": v(-1.4, 0.09) * mm, "end": v(-1.46, 0.14) * mm});
            skLineSegment(sketch, "E1960", {"start": v(-1.46, 0.14) * mm, "end": v(-1.56, 0.2) * mm});
            skLineSegment(sketch, "E1961", {"start": v(-1.56, 0.2) * mm, "end": v(-1.7, 0.25) * mm});
            skLineSegment(sketch, "E1962", {"start": v(-1.7, 0.25) * mm, "end": v(-1.89, 0.3) * mm});
            skLineSegment(sketch, "E1963", {"start": v(-1.89, 0.3) * mm, "end": v(-2.05, 0.35) * mm});
            skLineSegment(sketch, "E1964", {"start": v(-2.05, 0.35) * mm, "end": v(-2.17, 0.4) * mm});
            skLineSegment(sketch, "E1965", {"start": v(-2.17, 0.4) * mm, "end": v(-2.27, 0.42) * mm});
            skLineSegment(sketch, "E1966", {"start": v(-2.27, 0.42) * mm, "end": v(-2.36, 0.44) * mm});
            skLineSegment(sketch, "E1967", {"start": v(-2.36, 0.44) * mm, "end": v(-2.43, 0.45) * mm});
            skLineSegment(sketch, "E1968", {"start": v(-2.43, 0.45) * mm, "end": v(-2.5, 0.46) * mm});
            skLineSegment(sketch, "E1969", {"start": v(-2.5, 0.46) * mm, "end": v(-2.57, 0.46) * mm});
            skLineSegment(sketch, "E1970", {"start": v(-2.57, 0.46) * mm, "end": v(-2.65, 0.46) * mm});
            skLineSegment(sketch, "E1971", {"start": v(-2.65, 0.46) * mm, "end": v(-2.83, 0.47) * mm});
            skLineSegment(sketch, "E1972", {"start": v(-2.83, 0.47) * mm, "end": v(-2.96, 0.46) * mm});
            skLineSegment(sketch, "E1973", {"start": v(-2.96, 0.46) * mm, "end": v(-3.08, 0.44) * mm});
            skLineSegment(sketch, "E1974", {"start": v(-3.08, 0.44) * mm, "end": v(-3.2, 0.4) * mm});
            skLineSegment(sketch, "E1975", {"start": v(-3.2, 0.4) * mm, "end": v(-3.34, 0.35) * mm});
            skLineSegment(sketch, "E1976", {"start": v(-3.34, 0.35) * mm, "end": v(-3.5, 0.27) * mm});
            skLineSegment(sketch, "E1977", {"start": v(-3.5, 0.27) * mm, "end": v(-3.64, 0.19) * mm});
            skLineSegment(sketch, "E1978", {"start": v(-3.64, 0.19) * mm, "end": v(-3.77, 0.1) * mm});
            skLineSegment(sketch, "E1979", {"start": v(-3.77, 0.1) * mm, "end": v(-3.82, 0.06) * mm});
            skLineSegment(sketch, "E1980", {"start": v(-3.82, 0.06) * mm, "end": v(-3.87, 0.02) * mm});
            skLineSegment(sketch, "E1981", {"start": v(-3.87, 0.02) * mm, "end": v(-3.92, -0.03) * mm});
            skLineSegment(sketch, "E1982", {"start": v(-3.92, -0.03) * mm, "end": v(-3.98, -0.08) * mm});
            skLineSegment(sketch, "E1983", {"start": v(-3.98, -0.08) * mm, "end": v(-4.03, -0.13) * mm});
            skLineSegment(sketch, "E1984", {"start": v(-4.03, -0.13) * mm, "end": v(-4.07, -0.17) * mm});
            skLineSegment(sketch, "E1985", {"start": v(-4.07, -0.17) * mm, "end": v(-4.1, -0.2) * mm});
            skLineSegment(sketch, "E1986", {"start": v(-4.1, -0.2) * mm, "end": v(-4.12, -0.22) * mm});
            skLineSegment(sketch, "E1987", {"start": v(-4.12, -0.22) * mm, "end": v(-4.14, -0.26) * mm});
            skLineSegment(sketch, "E1988", {"start": v(-4.14, -0.26) * mm, "end": v(-4.18, -0.3) * mm});
            skLineSegment(sketch, "E1989", {"start": v(-4.18, -0.3) * mm, "end": v(-4.2, -0.33) * mm});
            skLineSegment(sketch, "E1990", {"start": v(-4.2, -0.33) * mm, "end": v(-4.22, -0.37) * mm});
            skLineSegment(sketch, "E1991", {"start": v(-4.22, -0.37) * mm, "end": v(-4.25, -0.42) * mm});
            skLineSegment(sketch, "E1992", {"start": v(-4.25, -0.42) * mm, "end": v(-4.28, -0.48) * mm});
            skLineSegment(sketch, "E1993", {"start": v(-4.28, -0.48) * mm, "end": v(-4.3, -0.53) * mm});
            skLineSegment(sketch, "E1994", {"start": v(-4.3, -0.53) * mm, "end": v(-4.33, -0.58) * mm});
            skLineSegment(sketch, "E1995", {"start": v(-4.33, -0.58) * mm, "end": v(-4.34, -0.62) * mm});
            skLineSegment(sketch, "E1996", {"start": v(-4.34, -0.62) * mm, "end": v(-4.35, -0.64) * mm});
            skLineSegment(sketch, "E1997", {"start": v(-4.35, -0.64) * mm, "end": v(-4.35, -0.66) * mm});
            skLineSegment(sketch, "E1998", {"start": v(-4.35, -0.66) * mm, "end": v(-4.34, -0.67) * mm});
            skLineSegment(sketch, "E1999", {"start": v(-4.34, -0.67) * mm, "end": v(-4.3, -0.67) * mm});
            skLineSegment(sketch, "E2000", {"start": v(-4.3, -0.67) * mm, "end": v(-4.24, -0.68) * mm});
            skLineSegment(sketch, "E2001", {"start": v(-4.24, -0.68) * mm, "end": v(-4.12, -0.69) * mm});
            skLineSegment(sketch, "E2002", {"start": v(-4.12, -0.69) * mm, "end": v(-4, -0.7) * mm});
            skLineSegment(sketch, "E2003", {"start": v(-4, -0.7) * mm, "end": v(-3.88, -0.7) * mm});
            skLineSegment(sketch, "E2004", {"start": v(-3.88, -0.7) * mm, "end": v(-3.73, -0.7) * mm});
            skLineSegment(sketch, "E2005", {"start": v(-3.73, -0.7) * mm, "end": v(-3.6, -0.7) * mm});
            skLineSegment(sketch, "E2006", {"start": v(-3.6, -0.7) * mm, "end": v(-3.49, -0.7) * mm});
            skLineSegment(sketch, "E2007", {"start": v(-0.58, -0.55) * mm, "end": v(-0.48, -0.52) * mm});
            skLineSegment(sketch, "E2008", {"start": v(-0.48, -0.52) * mm, "end": v(-0.37, -0.55) * mm});
            skLineSegment(sketch, "E2009", {"start": v(-0.37, -0.55) * mm, "end": v(-0.3, -0.57) * mm});
            skLineSegment(sketch, "E2010", {"start": v(-0.3, -0.57) * mm, "end": v(-0.26, -0.57) * mm});
            skLineSegment(sketch, "E2011", {"start": v(-0.26, -0.57) * mm, "end": v(-0.21, -0.58) * mm});
            skLineSegment(sketch, "E2012", {"start": v(-0.21, -0.58) * mm, "end": v(-0.15, -0.57) * mm});
            skLineSegment(sketch, "E2013", {"start": v(-0.15, -0.57) * mm, "end": v(-0.05, -0.56) * mm});
            skLineSegment(sketch, "E2014", {"start": v(-0.05, -0.56) * mm, "end": v(0.04, -0.53) * mm});
            skLineSegment(sketch, "E2015", {"start": v(0.04, -0.53) * mm, "end": v(0.08, -0.52) * mm});
            skLineSegment(sketch, "E2016", {"start": v(0.08, -0.52) * mm, "end": v(0.12, -0.5) * mm});
            skLineSegment(sketch, "E2017", {"start": v(0.12, -0.5) * mm, "end": v(0.15, -0.5) * mm});
            skLineSegment(sketch, "E2018", {"start": v(0.15, -0.5) * mm, "end": v(0.17, -0.49) * mm});
            skLineSegment(sketch, "E2019", {"start": v(0.17, -0.49) * mm, "end": v(0.2, -0.47) * mm});
            skLineSegment(sketch, "E2020", {"start": v(0.2, -0.47) * mm, "end": v(0.25, -0.44) * mm});
            skLineSegment(sketch, "E2021", {"start": v(0.25, -0.44) * mm, "end": v(0.29, -0.4) * mm});
            skLineSegment(sketch, "E2022", {"start": v(0.29, -0.4) * mm, "end": v(0.33, -0.34) * mm});
            skLineSegment(sketch, "E2023", {"start": v(0.33, -0.34) * mm, "end": v(0.36, -0.3) * mm});
            skLineSegment(sketch, "E2024", {"start": v(0.36, -0.3) * mm, "end": v(0.38, -0.27) * mm});
            skLineSegment(sketch, "E2025", {"start": v(0.38, -0.27) * mm, "end": v(0.4, -0.25) * mm});
            skLineSegment(sketch, "E2026", {"start": v(0.4, -0.25) * mm, "end": v(0.4, -0.23) * mm});
            skLineSegment(sketch, "E2027", {"start": v(0.4, -0.23) * mm, "end": v(0.4, -0.19) * mm});
            skLineSegment(sketch, "E2028", {"start": v(0.4, -0.19) * mm, "end": v(0.4, -0.13) * mm});
            skLineSegment(sketch, "E2029", {"start": v(0.4, -0.13) * mm, "end": v(0.39, -0.08) * mm});
            skLineSegment(sketch, "E2030", {"start": v(0.39, -0.08) * mm, "end": v(0.38, -0.02) * mm});
            skLineSegment(sketch, "E2031", {"start": v(0.38, -0.02) * mm, "end": v(0.37, 0.04) * mm});
            skLineSegment(sketch, "E2032", {"start": v(0.37, 0.04) * mm, "end": v(0.36, 0.08) * mm});
            skLineSegment(sketch, "E2033", {"start": v(0.36, 0.08) * mm, "end": v(0.35, 0.14) * mm});
            skLineSegment(sketch, "E2034", {"start": v(0.35, 0.14) * mm, "end": v(0.34, 0.2) * mm});
            skLineSegment(sketch, "E2035", {"start": v(0.34, 0.2) * mm, "end": v(0.32, 0.28) * mm});
            skLineSegment(sketch, "E2036", {"start": v(0.32, 0.28) * mm, "end": v(0.3, 0.36) * mm});
            skLineSegment(sketch, "E2037", {"start": v(0.3, 0.36) * mm, "end": v(0.3, 0.43) * mm});
            skLineSegment(sketch, "E2038", {"start": v(0.3, 0.43) * mm, "end": v(0.28, 0.49) * mm});
            skLineSegment(sketch, "E2039", {"start": v(0.28, 0.49) * mm, "end": v(0.27, 0.53) * mm});
            skLineSegment(sketch, "E2040", {"start": v(0.27, 0.53) * mm, "end": v(0.27, 0.54) * mm});
            skLineSegment(sketch, "E2041", {"start": v(0.27, 0.54) * mm, "end": v(0.26, 0.54) * mm});
            skLineSegment(sketch, "E2042", {"start": v(0.26, 0.54) * mm, "end": v(0.25, 0.53) * mm});
            skLineSegment(sketch, "E2043", {"start": v(0.25, 0.53) * mm, "end": v(0.22, 0.51) * mm});
            skLineSegment(sketch, "E2044", {"start": v(0.22, 0.51) * mm, "end": v(0.19, 0.5) * mm});
            skLineSegment(sketch, "E2045", {"start": v(0.19, 0.5) * mm, "end": v(0.05, 0.43) * mm});
            skLineSegment(sketch, "E2046", {"start": v(0.05, 0.43) * mm, "end": v(-0.11, 0.38) * mm});
            skLineSegment(sketch, "E2047", {"start": v(-0.11, 0.38) * mm, "end": v(-0.28, 0.35) * mm});
            skLineSegment(sketch, "E2048", {"start": v(-0.28, 0.35) * mm, "end": v(-0.47, 0.35) * mm});
            skLineSegment(sketch, "E2049", {"start": v(-0.47, 0.35) * mm, "end": v(-0.63, 0.36) * mm});
            skLineSegment(sketch, "E2050", {"start": v(-0.63, 0.36) * mm, "end": v(-0.77, 0.4) * mm});
            skLineSegment(sketch, "E2051", {"start": v(-0.77, 0.4) * mm, "end": v(-0.88, 0.43) * mm});
            skLineSegment(sketch, "E2052", {"start": v(-0.88, 0.43) * mm, "end": v(-0.96, 0.49) * mm});
            skLineSegment(sketch, "E2053", {"start": v(-0.96, 0.49) * mm, "end": v(-0.98, 0.5) * mm});
            skLineSegment(sketch, "E2054", {"start": v(-0.98, 0.5) * mm, "end": v(-1, 0.51) * mm});
            skLineSegment(sketch, "E2055", {"start": v(-1, 0.51) * mm, "end": v(-1, 0.5) * mm});
            skLineSegment(sketch, "E2056", {"start": v(-1, 0.5) * mm, "end": v(-1, 0.45) * mm});
            skLineSegment(sketch, "E2057", {"start": v(-1, 0.45) * mm, "end": v(-1, 0.39) * mm});
            skLineSegment(sketch, "E2058", {"start": v(-1, 0.39) * mm, "end": v(-1.02, 0.31) * mm});
            skLineSegment(sketch, "E2059", {"start": v(-1.02, 0.31) * mm, "end": v(-1.02, 0.2) * mm});
            skLineSegment(sketch, "E2060", {"start": v(-1.02, 0.2) * mm, "end": v(-1.02, 0.1) * mm});
            skLineSegment(sketch, "E2061", {"start": v(-1.02, 0.1) * mm, "end": v(-1.02, -0.04) * mm});
            skLineSegment(sketch, "E2062", {"start": v(-1.02, -0.04) * mm, "end": v(-1.02, -0.2) * mm});
            skLineSegment(sketch, "E2063", {"start": v(-1.02, -0.2) * mm, "end": v(-1, -0.5) * mm});
            skLineSegment(sketch, "E2064", {"start": v(-1, -0.5) * mm, "end": v(-0.98, -0.52) * mm});
            skLineSegment(sketch, "E2065", {"start": v(-0.98, -0.52) * mm, "end": v(-0.93, -0.55) * mm});
            skLineSegment(sketch, "E2066", {"start": v(-0.93, -0.55) * mm, "end": v(-0.85, -0.57) * mm});
            skLineSegment(sketch, "E2067", {"start": v(-0.85, -0.57) * mm, "end": v(-0.77, -0.59) * mm});
            skLineSegment(sketch, "E2068", {"start": v(-0.77, -0.59) * mm, "end": v(-0.72, -0.6) * mm});
            skLineSegment(sketch, "E2069", {"start": v(-0.72, -0.6) * mm, "end": v(-0.7, -0.59) * mm});
            skLineSegment(sketch, "E2070", {"start": v(-0.7, -0.59) * mm, "end": v(-0.66, -0.58) * mm});
            skLineSegment(sketch, "E2071", {"start": v(-0.66, -0.58) * mm, "end": v(-0.62, -0.57) * mm});
            skLineSegment(sketch, "E2072", {"start": v(-0.62, -0.57) * mm, "end": v(-0.58, -0.55) * mm});
            skLineSegment(sketch, "E2073", {"start": v(4.16, 0.23) * mm, "end": v(4.27, 0.25) * mm});
            skLineSegment(sketch, "E2074", {"start": v(4.27, 0.25) * mm, "end": v(4.34, 0.26) * mm});
            skLineSegment(sketch, "E2075", {"start": v(4.34, 0.26) * mm, "end": v(4.37, 0.28) * mm});
            skLineSegment(sketch, "E2076", {"start": v(4.37, 0.28) * mm, "end": v(4.38, 0.3) * mm});
            skLineSegment(sketch, "E2077", {"start": v(4.38, 0.3) * mm, "end": v(4.4, 0.38) * mm});
            skLineSegment(sketch, "E2078", {"start": v(4.4, 0.38) * mm, "end": v(4.4, 0.48) * mm});
            skLineSegment(sketch, "E2079", {"start": v(4.4, 0.48) * mm, "end": v(4.4, 0.57) * mm});
            skLineSegment(sketch, "E2080", {"start": v(4.4, 0.57) * mm, "end": v(4.38, 0.63) * mm});
            skLineSegment(sketch, "E2081", {"start": v(4.38, 0.63) * mm, "end": v(4.29, 0.78) * mm});
            skLineSegment(sketch, "E2082", {"start": v(4.29, 0.78) * mm, "end": v(4.14, 0.94) * mm});
            skLineSegment(sketch, "E2083", {"start": v(4.14, 0.94) * mm, "end": v(4.06, 1) * mm});
            skLineSegment(sketch, "E2084", {"start": v(4.06, 1) * mm, "end": v(4, 1.06) * mm});
            skLineSegment(sketch, "E2085", {"start": v(4, 1.06) * mm, "end": v(3.93, 1.1) * mm});
            skLineSegment(sketch, "E2086", {"start": v(3.93, 1.1) * mm, "end": v(3.88, 1.14) * mm});
            skLineSegment(sketch, "E2087", {"start": v(3.88, 1.14) * mm, "end": v(3.82, 1.17) * mm});
            skLineSegment(sketch, "E2088", {"start": v(3.82, 1.17) * mm, "end": v(3.76, 1.2) * mm});
            skLineSegment(sketch, "E2089", {"start": v(3.76, 1.2) * mm, "end": v(3.68, 1.21) * mm});
            skLineSegment(sketch, "E2090", {"start": v(3.68, 1.21) * mm, "end": v(3.6, 1.23) * mm});
            skLineSegment(sketch, "E2091", {"start": v(3.6, 1.23) * mm, "end": v(3.5, 1.25) * mm});
            skLineSegment(sketch, "E2092", {"start": v(3.5, 1.25) * mm, "end": v(3.44, 1.26) * mm});
            skLineSegment(sketch, "E2093", {"start": v(3.44, 1.26) * mm, "end": v(3.36, 1.26) * mm});
            skLineSegment(sketch, "E2094", {"start": v(3.36, 1.26) * mm, "end": v(3.25, 1.26) * mm});
            skLineSegment(sketch, "E2095", {"start": v(3.25, 1.26) * mm, "end": v(3.08, 1.25) * mm});
            skLineSegment(sketch, "E2096", {"start": v(3.08, 1.25) * mm, "end": v(2.9, 1.24) * mm});
            skLineSegment(sketch, "E2097", {"start": v(2.9, 1.24) * mm, "end": v(2.73, 1.22) * mm});
            skLineSegment(sketch, "E2098", {"start": v(2.73, 1.22) * mm, "end": v(2.6, 1.19) * mm});
            skLineSegment(sketch, "E2099", {"start": v(2.6, 1.19) * mm, "end": v(2.55, 1.18) * mm});
            skLineSegment(sketch, "E2100", {"start": v(2.55, 1.18) * mm, "end": v(2.52, 1.17) * mm});
            skLineSegment(sketch, "E2101", {"start": v(2.52, 1.17) * mm, "end": v(2.48, 1.17) * mm});
            skLineSegment(sketch, "E2102", {"start": v(2.48, 1.17) * mm, "end": v(2.46, 1.16) * mm});
            skLineSegment(sketch, "E2103", {"start": v(2.46, 1.16) * mm, "end": v(2.39, 1.14) * mm});
            skLineSegment(sketch, "E2104", {"start": v(2.39, 1.14) * mm, "end": v(2.29, 1.11) * mm});
            skLineSegment(sketch, "E2105", {"start": v(2.29, 1.11) * mm, "end": v(2.17, 1.07) * mm});
            skLineSegment(sketch, "E2106", {"start": v(2.17, 1.07) * mm, "end": v(2.03, 1.02) * mm});
            skLineSegment(sketch, "E2107", {"start": v(2.03, 1.02) * mm, "end": v(1.9, 0.97) * mm});
            skLineSegment(sketch, "E2108", {"start": v(1.9, 0.97) * mm, "end": v(1.75, 0.91) * mm});
            skLineSegment(sketch, "E2109", {"start": v(1.75, 0.91) * mm, "end": v(1.62, 0.86) * mm});
            skLineSegment(sketch, "E2110", {"start": v(1.62, 0.86) * mm, "end": v(1.5, 0.8) * mm});
            skLineSegment(sketch, "E2111", {"start": v(1.5, 0.8) * mm, "end": v(1.46, 0.79) * mm});
            skLineSegment(sketch, "E2112", {"start": v(1.46, 0.79) * mm, "end": v(1.4, 0.76) * mm});
            skLineSegment(sketch, "E2113", {"start": v(1.4, 0.76) * mm, "end": v(1.33, 0.73) * mm});
            skLineSegment(sketch, "E2114", {"start": v(1.33, 0.73) * mm, "end": v(1.27, 0.7) * mm});
            skLineSegment(sketch, "E2115", {"start": v(1.27, 0.7) * mm, "end": v(1.17, 0.67) * mm});
            skLineSegment(sketch, "E2116", {"start": v(1.17, 0.67) * mm, "end": v(1.08, 0.62) * mm});
            skLineSegment(sketch, "E2117", {"start": v(1.08, 0.62) * mm, "end": v(1.02, 0.59) * mm});
            skLineSegment(sketch, "E2118", {"start": v(1.02, 0.59) * mm, "end": v(1, 0.57) * mm});
            skLineSegment(sketch, "E2119", {"start": v(1, 0.57) * mm, "end": v(1, 0.57) * mm});
            skLineSegment(sketch, "E2120", {"start": v(1, 0.57) * mm, "end": v(1.03, 0.57) * mm});
            skLineSegment(sketch, "E2121", {"start": v(1.03, 0.57) * mm, "end": v(1.05, 0.58) * mm});
            skLineSegment(sketch, "E2122", {"start": v(1.05, 0.58) * mm, "end": v(1.08, 0.58) * mm});
            skLineSegment(sketch, "E2123", {"start": v(1.08, 0.58) * mm, "end": v(1.21, 0.6) * mm});
            skLineSegment(sketch, "E2124", {"start": v(1.21, 0.6) * mm, "end": v(1.39, 0.63) * mm});
            skLineSegment(sketch, "E2125", {"start": v(1.39, 0.63) * mm, "end": v(1.57, 0.64) * mm});
            skLineSegment(sketch, "E2126", {"start": v(1.57, 0.64) * mm, "end": v(1.73, 0.65) * mm});
            skLineSegment(sketch, "E2127", {"start": v(1.73, 0.65) * mm, "end": v(1.83, 0.65) * mm});
            skLineSegment(sketch, "E2128", {"start": v(1.83, 0.65) * mm, "end": v(1.94, 0.65) * mm});
            skLineSegment(sketch, "E2129", {"start": v(1.94, 0.65) * mm, "end": v(2.06, 0.65) * mm});
            skLineSegment(sketch, "E2130", {"start": v(2.06, 0.65) * mm, "end": v(2.2, 0.64) * mm});
            skLineSegment(sketch, "E2131", {"start": v(2.2, 0.64) * mm, "end": v(2.32, 0.63) * mm});
            skLineSegment(sketch, "E2132", {"start": v(2.32, 0.63) * mm, "end": v(2.43, 0.63) * mm});
            skLineSegment(sketch, "E2133", {"start": v(2.43, 0.63) * mm, "end": v(2.53, 0.62) * mm});
            skLineSegment(sketch, "E2134", {"start": v(2.53, 0.62) * mm, "end": v(2.6, 0.6) * mm});
            skLineSegment(sketch, "E2135", {"start": v(2.6, 0.6) * mm, "end": v(2.68, 0.59) * mm});
            skLineSegment(sketch, "E2136", {"start": v(2.68, 0.59) * mm, "end": v(2.79, 0.56) * mm});
            skLineSegment(sketch, "E2137", {"start": v(2.79, 0.56) * mm, "end": v(2.91, 0.53) * mm});
            skLineSegment(sketch, "E2138", {"start": v(2.91, 0.53) * mm, "end": v(3.05, 0.48) * mm});
            skLineSegment(sketch, "E2139", {"start": v(3.05, 0.48) * mm, "end": v(3.1, 0.47) * mm});
            skLineSegment(sketch, "E2140", {"start": v(3.1, 0.47) * mm, "end": v(3.17, 0.44) * mm});
            skLineSegment(sketch, "E2141", {"start": v(3.17, 0.44) * mm, "end": v(3.26, 0.4) * mm});
            skLineSegment(sketch, "E2142", {"start": v(3.26, 0.4) * mm, "end": v(3.35, 0.37) * mm});
            skLineSegment(sketch, "E2143", {"start": v(3.35, 0.37) * mm, "end": v(3.56, 0.29) * mm});
            skLineSegment(sketch, "E2144", {"start": v(3.56, 0.29) * mm, "end": v(3.75, 0.24) * mm});
            skLineSegment(sketch, "E2145", {"start": v(3.75, 0.24) * mm, "end": v(3.94, 0.22) * mm});
            skLineSegment(sketch, "E2146", {"start": v(3.94, 0.22) * mm, "end": v(4.16, 0.23) * mm});
            skLineSegment(sketch, "E2147", {"start": v(4.92, 0.46) * mm, "end": v(4.98, 0.5) * mm});
            skLineSegment(sketch, "E2148", {"start": v(4.98, 0.5) * mm, "end": v(5.05, 0.53) * mm});
            skLineSegment(sketch, "E2149", {"start": v(5.05, 0.53) * mm, "end": v(5.13, 0.58) * mm});
            skLineSegment(sketch, "E2150", {"start": v(5.13, 0.58) * mm, "end": v(5.21, 0.63) * mm});
            skLineSegment(sketch, "E2151", {"start": v(5.21, 0.63) * mm, "end": v(5.34, 0.72) * mm});
            skLineSegment(sketch, "E2152", {"start": v(5.34, 0.72) * mm, "end": v(5.44, 0.78) * mm});
            skLineSegment(sketch, "E2153", {"start": v(5.44, 0.78) * mm, "end": v(5.54, 0.83) * mm});
            skLineSegment(sketch, "E2154", {"start": v(5.54, 0.83) * mm, "end": v(5.63, 0.88) * mm});
            skLineSegment(sketch, "E2155", {"start": v(5.63, 0.88) * mm, "end": v(5.71, 0.92) * mm});
            skLineSegment(sketch, "E2156", {"start": v(5.71, 0.92) * mm, "end": v(5.8, 0.94) * mm});
            skLineSegment(sketch, "E2157", {"start": v(5.8, 0.94) * mm, "end": v(5.92, 0.96) * mm});
            skLineSegment(sketch, "E2158", {"start": v(5.92, 0.96) * mm, "end": v(6.1, 0.98) * mm});
            skLineSegment(sketch, "E2159", {"start": v(6.1, 0.98) * mm, "end": v(6.22, 1) * mm});
            skLineSegment(sketch, "E2160", {"start": v(6.22, 1) * mm, "end": v(6.34, 1.01) * mm});
            skLineSegment(sketch, "E2161", {"start": v(6.34, 1.01) * mm, "end": v(6.45, 1.04) * mm});
            skLineSegment(sketch, "E2162", {"start": v(6.45, 1.04) * mm, "end": v(6.5, 1.06) * mm});
            skLineSegment(sketch, "E2163", {"start": v(6.5, 1.06) * mm, "end": v(6.52, 1.07) * mm});
            skLineSegment(sketch, "E2164", {"start": v(6.52, 1.07) * mm, "end": v(6.53, 1.08) * mm});
            skLineSegment(sketch, "E2165", {"start": v(6.53, 1.08) * mm, "end": v(6.52, 1.1) * mm});
            skLineSegment(sketch, "E2166", {"start": v(6.52, 1.1) * mm, "end": v(6.5, 1.13) * mm});
            skLineSegment(sketch, "E2167", {"start": v(6.5, 1.13) * mm, "end": v(6.45, 1.16) * mm});
            skLineSegment(sketch, "E2168", {"start": v(6.45, 1.16) * mm, "end": v(6.4, 1.2) * mm});
            skLineSegment(sketch, "E2169", {"start": v(6.4, 1.2) * mm, "end": v(6.36, 1.21) * mm});
            skLineSegment(sketch, "E2170", {"start": v(6.36, 1.21) * mm, "end": v(6.32, 1.24) * mm});
            skLineSegment(sketch, "E2171", {"start": v(6.32, 1.24) * mm, "end": v(6.28, 1.26) * mm});
            skLineSegment(sketch, "E2172", {"start": v(6.28, 1.26) * mm, "end": v(6.25, 1.28) * mm});
            skLineSegment(sketch, "E2173", {"start": v(6.25, 1.28) * mm, "end": v(6.12, 1.36) * mm});
            skLineSegment(sketch, "E2174", {"start": v(6.12, 1.36) * mm, "end": v(5.93, 1.43) * mm});
            skLineSegment(sketch, "E2175", {"start": v(5.93, 1.43) * mm, "end": v(5.69, 1.5) * mm});
            skLineSegment(sketch, "E2176", {"start": v(5.69, 1.5) * mm, "end": v(5.41, 1.55) * mm});
            skLineSegment(sketch, "E2177", {"start": v(5.41, 1.55) * mm, "end": v(5.31, 1.57) * mm});
            skLineSegment(sketch, "E2178", {"start": v(5.31, 1.57) * mm, "end": v(5.23, 1.58) * mm});
            skLineSegment(sketch, "E2179", {"start": v(5.23, 1.58) * mm, "end": v(5.13, 1.58) * mm});
            skLineSegment(sketch, "E2180", {"start": v(5.13, 1.58) * mm, "end": v(5, 1.58) * mm});
            skLineSegment(sketch, "E2181", {"start": v(5, 1.58) * mm, "end": v(4.83, 1.58) * mm});
            skLineSegment(sketch, "E2182", {"start": v(4.83, 1.58) * mm, "end": v(4.68, 1.56) * mm});
            skLineSegment(sketch, "E2183", {"start": v(4.68, 1.56) * mm, "end": v(4.54, 1.54) * mm});
            skLineSegment(sketch, "E2184", {"start": v(4.54, 1.54) * mm, "end": v(4.38, 1.5) * mm});
            skLineSegment(sketch, "E2185", {"start": v(4.38, 1.5) * mm, "end": v(4.35, 1.49) * mm});
            skLineSegment(sketch, "E2186", {"start": v(4.35, 1.49) * mm, "end": v(4.31, 1.48) * mm});
            skLineSegment(sketch, "E2187", {"start": v(4.31, 1.48) * mm, "end": v(4.28, 1.47) * mm});
            skLineSegment(sketch, "E2188", {"start": v(4.28, 1.47) * mm, "end": v(4.24, 1.47) * mm});
            skLineSegment(sketch, "E2189", {"start": v(4.24, 1.47) * mm, "end": v(4.2, 1.46) * mm});
            skLineSegment(sketch, "E2190", {"start": v(4.2, 1.46) * mm, "end": v(4.13, 1.46) * mm});
            skLineSegment(sketch, "E2191", {"start": v(4.13, 1.46) * mm, "end": v(4.06, 1.46) * mm});
            skLineSegment(sketch, "E2192", {"start": v(4.06, 1.46) * mm, "end": v(3.96, 1.46) * mm});
            skLineSegment(sketch, "E2193", {"start": v(3.96, 1.46) * mm, "end": v(3.84, 1.45) * mm});
            skLineSegment(sketch, "E2194", {"start": v(3.84, 1.45) * mm, "end": v(3.74, 1.45) * mm});
            skLineSegment(sketch, "E2195", {"start": v(3.74, 1.45) * mm, "end": v(3.67, 1.45) * mm});
            skLineSegment(sketch, "E2196", {"start": v(3.67, 1.45) * mm, "end": v(3.64, 1.45) * mm});
            skLineSegment(sketch, "E2197", {"start": v(3.64, 1.45) * mm, "end": v(3.64, 1.43) * mm});
            skLineSegment(sketch, "E2198", {"start": v(3.64, 1.43) * mm, "end": v(3.66, 1.42) * mm});
            skLineSegment(sketch, "E2199", {"start": v(3.66, 1.42) * mm, "end": v(3.7, 1.4) * mm});
            skLineSegment(sketch, "E2200", {"start": v(3.7, 1.4) * mm, "end": v(3.75, 1.37) * mm});
            skLineSegment(sketch, "E2201", {"start": v(3.75, 1.37) * mm, "end": v(3.83, 1.33) * mm});
            skLineSegment(sketch, "E2202", {"start": v(3.83, 1.33) * mm, "end": v(4, 1.24) * mm});
            skLineSegment(sketch, "E2203", {"start": v(4, 1.24) * mm, "end": v(4.18, 1.14) * mm});
            skLineSegment(sketch, "E2204", {"start": v(4.18, 1.14) * mm, "end": v(4.33, 1.04) * mm});
            skLineSegment(sketch, "E2205", {"start": v(4.33, 1.04) * mm, "end": v(4.44, 0.96) * mm});
            skLineSegment(sketch, "E2206", {"start": v(4.44, 0.96) * mm, "end": v(4.54, 0.86) * mm});
            skLineSegment(sketch, "E2207", {"start": v(4.54, 0.86) * mm, "end": v(4.63, 0.73) * mm});
            skLineSegment(sketch, "E2208", {"start": v(4.63, 0.73) * mm, "end": v(4.7, 0.6) * mm});
            skLineSegment(sketch, "E2209", {"start": v(4.7, 0.6) * mm, "end": v(4.73, 0.47) * mm});
            skLineSegment(sketch, "E2210", {"start": v(4.73, 0.47) * mm, "end": v(4.74, 0.43) * mm});
            skLineSegment(sketch, "E2211", {"start": v(4.74, 0.43) * mm, "end": v(4.75, 0.4) * mm});
            skLineSegment(sketch, "E2212", {"start": v(4.75, 0.4) * mm, "end": v(4.76, 0.4) * mm});
            skLineSegment(sketch, "E2213", {"start": v(4.76, 0.4) * mm, "end": v(4.8, 0.4) * mm});
            skLineSegment(sketch, "E2214", {"start": v(4.8, 0.4) * mm, "end": v(4.85, 0.43) * mm});
            skLineSegment(sketch, "E2215", {"start": v(4.85, 0.43) * mm, "end": v(4.92, 0.46) * mm});
            skLineSegment(sketch, "E2216", {"start": v(-5.35, 0.48) * mm, "end": v(-5.35, 0.5) * mm});
            skLineSegment(sketch, "E2217", {"start": v(-5.35, 0.5) * mm, "end": v(-5.36, 0.52) * mm});
            skLineSegment(sketch, "E2218", {"start": v(-5.36, 0.52) * mm, "end": v(-5.36, 0.56) * mm});
            skLineSegment(sketch, "E2219", {"start": v(-5.36, 0.56) * mm, "end": v(-5.38, 0.6) * mm});
            skLineSegment(sketch, "E2220", {"start": v(-5.38, 0.6) * mm, "end": v(-5.39, 0.66) * mm});
            skLineSegment(sketch, "E2221", {"start": v(-5.39, 0.66) * mm, "end": v(-5.4, 0.71) * mm});
            skLineSegment(sketch, "E2222", {"start": v(-5.4, 0.71) * mm, "end": v(-5.4, 0.76) * mm});
            skLineSegment(sketch, "E2223", {"start": v(-5.4, 0.76) * mm, "end": v(-5.4, 0.79) * mm});
            skLineSegment(sketch, "E2224", {"start": v(-5.4, 0.79) * mm, "end": v(-5.4, 0.86) * mm});
            skLineSegment(sketch, "E2225", {"start": v(-5.4, 0.86) * mm, "end": v(-5.37, 0.94) * mm});
            skLineSegment(sketch, "E2226", {"start": v(-5.37, 0.94) * mm, "end": v(-5.34, 1.03) * mm});
            skLineSegment(sketch, "E2227", {"start": v(-5.34, 1.03) * mm, "end": v(-5.3, 1.1) * mm});
            skLineSegment(sketch, "E2228", {"start": v(-5.3, 1.1) * mm, "end": v(-5.28, 1.16) * mm});
            skLineSegment(sketch, "E2229", {"start": v(-5.28, 1.16) * mm, "end": v(-5.25, 1.21) * mm});
            skLineSegment(sketch, "E2230", {"start": v(-5.25, 1.21) * mm, "end": v(-5.2, 1.28) * mm});
            skLineSegment(sketch, "E2231", {"start": v(-5.2, 1.28) * mm, "end": v(-5.15, 1.35) * mm});
            skLineSegment(sketch, "E2232", {"start": v(-5.15, 1.35) * mm, "end": v(-5.09, 1.42) * mm});
            skLineSegment(sketch, "E2233", {"start": v(-5.09, 1.42) * mm, "end": v(-5.04, 1.46) * mm});
            skLineSegment(sketch, "E2234", {"start": v(-5.04, 1.46) * mm, "end": v(-5, 1.49) * mm});
            skLineSegment(sketch, "E2235", {"start": v(-5, 1.49) * mm, "end": v(-4.95, 1.52) * mm});
            skLineSegment(sketch, "E2236", {"start": v(-4.95, 1.52) * mm, "end": v(-4.9, 1.55) * mm});
            skLineSegment(sketch, "E2237", {"start": v(-4.9, 1.55) * mm, "end": v(-4.84, 1.58) * mm});
            skLineSegment(sketch, "E2238", {"start": v(-4.84, 1.58) * mm, "end": v(-4.7, 1.65) * mm});
            skLineSegment(sketch, "E2239", {"start": v(-4.7, 1.65) * mm, "end": v(-4.74, 1.66) * mm});
            skLineSegment(sketch, "E2240", {"start": v(-4.74, 1.66) * mm, "end": v(-4.82, 1.66) * mm});
            skLineSegment(sketch, "E2241", {"start": v(-4.82, 1.66) * mm, "end": v(-4.93, 1.66) * mm});
            skLineSegment(sketch, "E2242", {"start": v(-4.93, 1.66) * mm, "end": v(-5.05, 1.65) * mm});
            skLineSegment(sketch, "E2243", {"start": v(-5.05, 1.65) * mm, "end": v(-5.17, 1.64) * mm});
            skLineSegment(sketch, "E2244", {"start": v(-5.17, 1.64) * mm, "end": v(-5.28, 1.62) * mm});
            skLineSegment(sketch, "E2245", {"start": v(-5.28, 1.62) * mm, "end": v(-5.4, 1.58) * mm});
            skLineSegment(sketch, "E2246", {"start": v(-5.4, 1.58) * mm, "end": v(-5.55, 1.55) * mm});
            skLineSegment(sketch, "E2247", {"start": v(-5.55, 1.55) * mm, "end": v(-5.68, 1.52) * mm});
            skLineSegment(sketch, "E2248", {"start": v(-5.68, 1.52) * mm, "end": v(-5.78, 1.5) * mm});
            skLineSegment(sketch, "E2249", {"start": v(-5.78, 1.5) * mm, "end": v(-5.9, 1.45) * mm});
            skLineSegment(sketch, "E2250", {"start": v(-5.9, 1.45) * mm, "end": v(-6.02, 1.4) * mm});
            skLineSegment(sketch, "E2251", {"start": v(-6.02, 1.4) * mm, "end": v(-6.14, 1.35) * mm});
            skLineSegment(sketch, "E2252", {"start": v(-6.14, 1.35) * mm, "end": v(-6.22, 1.3) * mm});
            skLineSegment(sketch, "E2253", {"start": v(-6.22, 1.3) * mm, "end": v(-6.31, 1.25) * mm});
            skLineSegment(sketch, "E2254", {"start": v(-6.31, 1.25) * mm, "end": v(-6.41, 1.18) * mm});
            skLineSegment(sketch, "E2255", {"start": v(-6.41, 1.18) * mm, "end": v(-6.5, 1.12) * mm});
            skLineSegment(sketch, "E2256", {"start": v(-6.5, 1.12) * mm, "end": v(-6.54, 1.09) * mm});
            skLineSegment(sketch, "E2257", {"start": v(-6.54, 1.09) * mm, "end": v(-6.57, 1.06) * mm});
            skLineSegment(sketch, "E2258", {"start": v(-6.57, 1.06) * mm, "end": v(-6.6, 1.03) * mm});
            skLineSegment(sketch, "E2259", {"start": v(-6.6, 1.03) * mm, "end": v(-6.63, 1) * mm});
            skLineSegment(sketch, "E2260", {"start": v(-6.63, 1) * mm, "end": v(-6.73, 0.94) * mm});
            skLineSegment(sketch, "E2261", {"start": v(-6.73, 0.94) * mm, "end": v(-6.8, 0.87) * mm});
            skLineSegment(sketch, "E2262", {"start": v(-6.8, 0.87) * mm, "end": v(-6.87, 0.82) * mm});
            skLineSegment(sketch, "E2263", {"start": v(-6.87, 0.82) * mm, "end": v(-6.92, 0.78) * mm});
            skLineSegment(sketch, "E2264", {"start": v(-6.92, 0.78) * mm, "end": v(-6.95, 0.75) * mm});
            skLineSegment(sketch, "E2265", {"start": v(-6.95, 0.75) * mm, "end": v(-6.98, 0.72) * mm});
            skLineSegment(sketch, "E2266", {"start": v(-6.98, 0.72) * mm, "end": v(-7, 0.7) * mm});
            skLineSegment(sketch, "E2267", {"start": v(-7, 0.7) * mm, "end": v(-7, 0.69) * mm});
            skLineSegment(sketch, "E2268", {"start": v(-7, 0.69) * mm, "end": v(-6.98, 0.67) * mm});
            skLineSegment(sketch, "E2269", {"start": v(-6.98, 0.67) * mm, "end": v(-6.93, 0.65) * mm});
            skLineSegment(sketch, "E2270", {"start": v(-6.93, 0.65) * mm, "end": v(-6.85, 0.63) * mm});
            skLineSegment(sketch, "E2271", {"start": v(-6.85, 0.63) * mm, "end": v(-6.75, 0.6) * mm});
            skLineSegment(sketch, "E2272", {"start": v(-6.75, 0.6) * mm, "end": v(-6.49, 0.56) * mm});
            skLineSegment(sketch, "E2273", {"start": v(-6.49, 0.56) * mm, "end": v(-6.26, 0.52) * mm});
            skLineSegment(sketch, "E2274", {"start": v(-6.26, 0.52) * mm, "end": v(-6.07, 0.5) * mm});
            skLineSegment(sketch, "E2275", {"start": v(-6.07, 0.5) * mm, "end": v(-5.93, 0.47) * mm});
            skLineSegment(sketch, "E2276", {"start": v(-5.93, 0.47) * mm, "end": v(-5.89, 0.47) * mm});
            skLineSegment(sketch, "E2277", {"start": v(-5.89, 0.47) * mm, "end": v(-5.81, 0.47) * mm});
            skLineSegment(sketch, "E2278", {"start": v(-5.81, 0.47) * mm, "end": v(-5.72, 0.47) * mm});
            skLineSegment(sketch, "E2279", {"start": v(-5.72, 0.47) * mm, "end": v(-5.62, 0.47) * mm});
            skLineSegment(sketch, "E2280", {"start": v(-5.62, 0.47) * mm, "end": v(-5.52, 0.47) * mm});
            skLineSegment(sketch, "E2281", {"start": v(-5.52, 0.47) * mm, "end": v(-5.44, 0.47) * mm});
            skLineSegment(sketch, "E2282", {"start": v(-5.44, 0.47) * mm, "end": v(-5.38, 0.48) * mm});
            skLineSegment(sketch, "E2283", {"start": v(-5.38, 0.48) * mm, "end": v(-5.35, 0.48) * mm});
            skLineSegment(sketch, "E2284", {"start": v(0.84, 0.71) * mm, "end": v(0.92, 0.77) * mm});
            skLineSegment(sketch, "E2285", {"start": v(0.92, 0.77) * mm, "end": v(1.02, 0.84) * mm});
            skLineSegment(sketch, "E2286", {"start": v(1.02, 0.84) * mm, "end": v(1.13, 0.9) * mm});
            skLineSegment(sketch, "E2287", {"start": v(1.13, 0.9) * mm, "end": v(1.23, 0.95) * mm});
            skLineSegment(sketch, "E2288", {"start": v(1.23, 0.95) * mm, "end": v(1.36, 1.03) * mm});
            skLineSegment(sketch, "E2289", {"start": v(1.36, 1.03) * mm, "end": v(1.47, 1.12) * mm});
            skLineSegment(sketch, "E2290", {"start": v(1.47, 1.12) * mm, "end": v(1.57, 1.22) * mm});
            skLineSegment(sketch, "E2291", {"start": v(1.57, 1.22) * mm, "end": v(1.67, 1.36) * mm});
            skLineSegment(sketch, "E2292", {"start": v(1.67, 1.36) * mm, "end": v(1.69, 1.38) * mm});
            skLineSegment(sketch, "E2293", {"start": v(1.69, 1.38) * mm, "end": v(1.7, 1.4) * mm});
            skLineSegment(sketch, "E2294", {"start": v(1.7, 1.4) * mm, "end": v(1.73, 1.43) * mm});
            skLineSegment(sketch, "E2295", {"start": v(1.73, 1.43) * mm, "end": v(1.75, 1.45) * mm});
            skLineSegment(sketch, "E2296", {"start": v(1.75, 1.45) * mm, "end": v(1.77, 1.48) * mm});
            skLineSegment(sketch, "E2297", {"start": v(1.77, 1.48) * mm, "end": v(1.8, 1.52) * mm});
            skLineSegment(sketch, "E2298", {"start": v(1.8, 1.52) * mm, "end": v(1.82, 1.56) * mm});
            skLineSegment(sketch, "E2299", {"start": v(1.82, 1.56) * mm, "end": v(1.85, 1.6) * mm});
            skLineSegment(sketch, "E2300", {"start": v(1.85, 1.6) * mm, "end": v(1.88, 1.65) * mm});
            skLineSegment(sketch, "E2301", {"start": v(1.88, 1.65) * mm, "end": v(1.9, 1.7) * mm});
            skLineSegment(sketch, "E2302", {"start": v(1.9, 1.7) * mm, "end": v(1.94, 1.75) * mm});
            skLineSegment(sketch, "E2303", {"start": v(1.94, 1.75) * mm, "end": v(1.97, 1.78) * mm});
            skLineSegment(sketch, "E2304", {"start": v(1.97, 1.78) * mm, "end": v(2, 1.82) * mm});
            skLineSegment(sketch, "E2305", {"start": v(2, 1.82) * mm, "end": v(2.03, 1.85) * mm});
            skLineSegment(sketch, "E2306", {"start": v(2.03, 1.85) * mm, "end": v(2.06, 1.88) * mm});
            skLineSegment(sketch, "E2307", {"start": v(2.06, 1.88) * mm, "end": v(2.07, 1.9) * mm});
            skLineSegment(sketch, "E2308", {"start": v(2.07, 1.9) * mm, "end": v(2.11, 1.94) * mm});
            skLineSegment(sketch, "E2309", {"start": v(2.11, 1.94) * mm, "end": v(2.18, 2) * mm});
            skLineSegment(sketch, "E2310", {"start": v(2.18, 2) * mm, "end": v(2.26, 2.06) * mm});
            skLineSegment(sketch, "E2311", {"start": v(2.26, 2.06) * mm, "end": v(2.35, 2.13) * mm});
            skLineSegment(sketch, "E2312", {"start": v(2.35, 2.13) * mm, "end": v(2.44, 2.2) * mm});
            skLineSegment(sketch, "E2313", {"start": v(2.44, 2.2) * mm, "end": v(2.53, 2.26) * mm});
            skLineSegment(sketch, "E2314", {"start": v(2.53, 2.26) * mm, "end": v(2.62, 2.32) * mm});
            skLineSegment(sketch, "E2315", {"start": v(2.62, 2.32) * mm, "end": v(2.68, 2.35) * mm});
            skLineSegment(sketch, "E2316", {"start": v(2.68, 2.35) * mm, "end": v(2.73, 2.38) * mm});
            skLineSegment(sketch, "E2317", {"start": v(2.73, 2.38) * mm, "end": v(2.8, 2.4) * mm});
            skLineSegment(sketch, "E2318", {"start": v(2.8, 2.4) * mm, "end": v(2.85, 2.43) * mm});
            skLineSegment(sketch, "E2319", {"start": v(2.85, 2.43) * mm, "end": v(2.9, 2.46) * mm});
            skLineSegment(sketch, "E2320", {"start": v(2.9, 2.46) * mm, "end": v(2.95, 2.48) * mm});
            skLineSegment(sketch, "E2321", {"start": v(2.95, 2.48) * mm, "end": v(3, 2.5) * mm});
            skLineSegment(sketch, "E2322", {"start": v(3, 2.5) * mm, "end": v(3.04, 2.52) * mm});
            skLineSegment(sketch, "E2323", {"start": v(3.04, 2.52) * mm, "end": v(3.07, 2.53) * mm});
            skLineSegment(sketch, "E2324", {"start": v(3.07, 2.53) * mm, "end": v(3.1, 2.55) * mm});
            skLineSegment(sketch, "E2325", {"start": v(3.1, 2.55) * mm, "end": v(3.1, 2.55) * mm});
            skLineSegment(sketch, "E2326", {"start": v(3.1, 2.55) * mm, "end": v(3.1, 2.56) * mm});
            skLineSegment(sketch, "E2327", {"start": v(3.1, 2.56) * mm, "end": v(3.1, 2.56) * mm});
            skLineSegment(sketch, "E2328", {"start": v(3.1, 2.56) * mm, "end": v(3.08, 2.57) * mm});
            skLineSegment(sketch, "E2329", {"start": v(3.08, 2.57) * mm, "end": v(3.05, 2.56) * mm});
            skLineSegment(sketch, "E2330", {"start": v(3.05, 2.56) * mm, "end": v(3.01, 2.56) * mm});
            skLineSegment(sketch, "E2331", {"start": v(3.01, 2.56) * mm, "end": v(2.96, 2.56) * mm});
            skLineSegment(sketch, "E2332", {"start": v(2.96, 2.56) * mm, "end": v(2.85, 2.54) * mm});
            skLineSegment(sketch, "E2333", {"start": v(2.85, 2.54) * mm, "end": v(2.74, 2.53) * mm});
            skLineSegment(sketch, "E2334", {"start": v(2.74, 2.53) * mm, "end": v(2.62, 2.5) * mm});
            skLineSegment(sketch, "E2335", {"start": v(2.62, 2.5) * mm, "end": v(2.48, 2.47) * mm});
            skLineSegment(sketch, "E2336", {"start": v(2.48, 2.47) * mm, "end": v(2.32, 2.43) * mm});
            skLineSegment(sketch, "E2337", {"start": v(2.32, 2.43) * mm, "end": v(2.18, 2.39) * mm});
            skLineSegment(sketch, "E2338", {"start": v(2.18, 2.39) * mm, "end": v(2.05, 2.33) * mm});
            skLineSegment(sketch, "E2339", {"start": v(2.05, 2.33) * mm, "end": v(1.9, 2.26) * mm});
            skLineSegment(sketch, "E2340", {"start": v(1.9, 2.26) * mm, "end": v(1.84, 2.23) * mm});
            skLineSegment(sketch, "E2341", {"start": v(1.84, 2.23) * mm, "end": v(1.78, 2.2) * mm});
            skLineSegment(sketch, "E2342", {"start": v(1.78, 2.2) * mm, "end": v(1.72, 2.16) * mm});
            skLineSegment(sketch, "E2343", {"start": v(1.72, 2.16) * mm, "end": v(1.66, 2.12) * mm});
            skLineSegment(sketch, "E2344", {"start": v(1.66, 2.12) * mm, "end": v(1.59, 2.07) * mm});
            skLineSegment(sketch, "E2345", {"start": v(1.59, 2.07) * mm, "end": v(1.5, 2) * mm});
            skLineSegment(sketch, "E2346", {"start": v(1.5, 2) * mm, "end": v(1.37, 1.9) * mm});
            skLineSegment(sketch, "E2347", {"start": v(1.37, 1.9) * mm, "end": v(1.2, 1.78) * mm});
            skLineSegment(sketch, "E2348", {"start": v(1.2, 1.78) * mm, "end": v(1.13, 1.71) * mm});
            skLineSegment(sketch, "E2349", {"start": v(1.13, 1.71) * mm, "end": v(1.04, 1.63) * mm});
            skLineSegment(sketch, "E2350", {"start": v(1.04, 1.63) * mm, "end": v(0.95, 1.54) * mm});
            skLineSegment(sketch, "E2351", {"start": v(0.95, 1.54) * mm, "end": v(0.86, 1.45) * mm});
            skLineSegment(sketch, "E2352", {"start": v(0.86, 1.45) * mm, "end": v(0.78, 1.35) * mm});
            skLineSegment(sketch, "E2353", {"start": v(0.78, 1.35) * mm, "end": v(0.7, 1.25) * mm});
            skLineSegment(sketch, "E2354", {"start": v(0.7, 1.25) * mm, "end": v(0.63, 1.16) * mm});
            skLineSegment(sketch, "E2355", {"start": v(0.63, 1.16) * mm, "end": v(0.58, 1.08) * mm});
            skLineSegment(sketch, "E2356", {"start": v(0.58, 1.08) * mm, "end": v(0.56, 1.04) * mm});
            skLineSegment(sketch, "E2357", {"start": v(0.56, 1.04) * mm, "end": v(0.54, 1) * mm});
            skLineSegment(sketch, "E2358", {"start": v(0.54, 1) * mm, "end": v(0.53, 0.98) * mm});
            skLineSegment(sketch, "E2359", {"start": v(0.53, 0.98) * mm, "end": v(0.53, 0.96) * mm});
            skLineSegment(sketch, "E2360", {"start": v(0.53, 0.96) * mm, "end": v(0.53, 0.92) * mm});
            skLineSegment(sketch, "E2361", {"start": v(0.53, 0.92) * mm, "end": v(0.53, 0.86) * mm});
            skLineSegment(sketch, "E2362", {"start": v(0.53, 0.86) * mm, "end": v(0.54, 0.8) * mm});
            skLineSegment(sketch, "E2363", {"start": v(0.54, 0.8) * mm, "end": v(0.55, 0.7) * mm});
            skLineSegment(sketch, "E2364", {"start": v(0.55, 0.7) * mm, "end": v(0.55, 0.63) * mm});
            skLineSegment(sketch, "E2365", {"start": v(0.55, 0.63) * mm, "end": v(0.56, 0.56) * mm});
            skLineSegment(sketch, "E2366", {"start": v(0.56, 0.56) * mm, "end": v(0.57, 0.51) * mm});
            skLineSegment(sketch, "E2367", {"start": v(0.57, 0.51) * mm, "end": v(0.57, 0.49) * mm});
            skLineSegment(sketch, "E2368", {"start": v(0.57, 0.49) * mm, "end": v(0.58, 0.49) * mm});
            skLineSegment(sketch, "E2369", {"start": v(0.58, 0.49) * mm, "end": v(0.6, 0.5) * mm});
            skLineSegment(sketch, "E2370", {"start": v(0.6, 0.5) * mm, "end": v(0.63, 0.52) * mm});
            skLineSegment(sketch, "E2371", {"start": v(0.63, 0.52) * mm, "end": v(0.67, 0.57) * mm});
            skLineSegment(sketch, "E2372", {"start": v(0.67, 0.57) * mm, "end": v(0.72, 0.6) * mm});
            skLineSegment(sketch, "E2373", {"start": v(0.72, 0.6) * mm, "end": v(0.76, 0.65) * mm});
            skLineSegment(sketch, "E2374", {"start": v(0.76, 0.65) * mm, "end": v(0.8, 0.69) * mm});
            skLineSegment(sketch, "E2375", {"start": v(0.8, 0.69) * mm, "end": v(0.84, 0.71) * mm});
            skLineSegment(sketch, "E2376", {"start": v(-5.07, 0.52) * mm, "end": v(-4.93, 0.56) * mm});
            skLineSegment(sketch, "E2377", {"start": v(-4.93, 0.56) * mm, "end": v(-4.77, 0.61) * mm});
            skLineSegment(sketch, "E2378", {"start": v(-4.77, 0.61) * mm, "end": v(-4.61, 0.67) * mm});
            skLineSegment(sketch, "E2379", {"start": v(-4.61, 0.67) * mm, "end": v(-4.5, 0.71) * mm});
            skLineSegment(sketch, "E2380", {"start": v(-4.5, 0.71) * mm, "end": v(-4.4, 0.75) * mm});
            skLineSegment(sketch, "E2381", {"start": v(-4.4, 0.75) * mm, "end": v(-4.28, 0.79) * mm});
            skLineSegment(sketch, "E2382", {"start": v(-4.28, 0.79) * mm, "end": v(-4.22, 0.8) * mm});
            skLineSegment(sketch, "E2383", {"start": v(-4.22, 0.8) * mm, "end": v(-4.17, 0.82) * mm});
            skLineSegment(sketch, "E2384", {"start": v(-4.17, 0.82) * mm, "end": v(-4.13, 0.83) * mm});
            skLineSegment(sketch, "E2385", {"start": v(-4.13, 0.83) * mm, "end": v(-4.1, 0.84) * mm});
            skLineSegment(sketch, "E2386", {"start": v(-4.1, 0.84) * mm, "end": v(-4, 0.86) * mm});
            skLineSegment(sketch, "E2387", {"start": v(-4, 0.86) * mm, "end": v(-3.86, 0.88) * mm});
            skLineSegment(sketch, "E2388", {"start": v(-3.86, 0.88) * mm, "end": v(-3.69, 0.9) * mm});
            skLineSegment(sketch, "E2389", {"start": v(-3.69, 0.9) * mm, "end": v(-3.48, 0.9) * mm});
            skLineSegment(sketch, "E2390", {"start": v(-3.48, 0.9) * mm, "end": v(-3.16, 0.9) * mm});
            skLineSegment(sketch, "E2391", {"start": v(-3.16, 0.9) * mm, "end": v(-2.87, 0.9) * mm});
            skLineSegment(sketch, "E2392", {"start": v(-2.87, 0.9) * mm, "end": v(-2.62, 0.87) * mm});
            skLineSegment(sketch, "E2393", {"start": v(-2.62, 0.87) * mm, "end": v(-2.43, 0.83) * mm});
            skLineSegment(sketch, "E2394", {"start": v(-2.43, 0.83) * mm, "end": v(-2.38, 0.82) * mm});
            skLineSegment(sketch, "E2395", {"start": v(-2.38, 0.82) * mm, "end": v(-2.33, 0.8) * mm});
            skLineSegment(sketch, "E2396", {"start": v(-2.33, 0.8) * mm, "end": v(-2.27, 0.8) * mm});
            skLineSegment(sketch, "E2397", {"start": v(-2.27, 0.8) * mm, "end": v(-2.22, 0.78) * mm});
            skLineSegment(sketch, "E2398", {"start": v(-2.22, 0.78) * mm, "end": v(-2.17, 0.78) * mm});
            skLineSegment(sketch, "E2399", {"start": v(-2.17, 0.78) * mm, "end": v(-2.12, 0.77) * mm});
            skLineSegment(sketch, "E2400", {"start": v(-2.12, 0.77) * mm, "end": v(-2.07, 0.76) * mm});
            skLineSegment(sketch, "E2401", {"start": v(-2.07, 0.76) * mm, "end": v(-2.04, 0.75) * mm});
            skLineSegment(sketch, "E2402", {"start": v(-2.04, 0.75) * mm, "end": v(-1.98, 0.74) * mm});
            skLineSegment(sketch, "E2403", {"start": v(-1.98, 0.74) * mm, "end": v(-1.95, 0.73) * mm});
            skLineSegment(sketch, "E2404", {"start": v(-1.95, 0.73) * mm, "end": v(-1.94, 0.74) * mm});
            skLineSegment(sketch, "E2405", {"start": v(-1.94, 0.74) * mm, "end": v(-1.94, 0.74) * mm});
            skLineSegment(sketch, "E2406", {"start": v(-1.94, 0.74) * mm, "end": v(-1.95, 0.76) * mm});
            skLineSegment(sketch, "E2407", {"start": v(-1.95, 0.76) * mm, "end": v(-1.97, 0.78) * mm});
            skLineSegment(sketch, "E2408", {"start": v(-1.97, 0.78) * mm, "end": v(-2.02, 0.82) * mm});
            skLineSegment(sketch, "E2409", {"start": v(-2.02, 0.82) * mm, "end": v(-2.07, 0.86) * mm});
            skLineSegment(sketch, "E2410", {"start": v(-2.07, 0.86) * mm, "end": v(-2.14, 0.91) * mm});
            skLineSegment(sketch, "E2411", {"start": v(-2.14, 0.91) * mm, "end": v(-2.2, 0.97) * mm});
            skLineSegment(sketch, "E2412", {"start": v(-2.2, 0.97) * mm, "end": v(-2.29, 1.03) * mm});
            skLineSegment(sketch, "E2413", {"start": v(-2.29, 1.03) * mm, "end": v(-2.37, 1.1) * mm});
            skLineSegment(sketch, "E2414", {"start": v(-2.37, 1.1) * mm, "end": v(-2.47, 1.16) * mm});
            skLineSegment(sketch, "E2415", {"start": v(-2.47, 1.16) * mm, "end": v(-2.59, 1.23) * mm});
            skLineSegment(sketch, "E2416", {"start": v(-2.59, 1.23) * mm, "end": v(-2.71, 1.3) * mm});
            skLineSegment(sketch, "E2417", {"start": v(-2.71, 1.3) * mm, "end": v(-2.83, 1.35) * mm});
            skLineSegment(sketch, "E2418", {"start": v(-2.83, 1.35) * mm, "end": v(-3.08, 1.43) * mm});
            skLineSegment(sketch, "E2419", {"start": v(-3.08, 1.43) * mm, "end": v(-3.34, 1.5) * mm});
            skLineSegment(sketch, "E2420", {"start": v(-3.34, 1.5) * mm, "end": v(-3.6, 1.55) * mm});
            skLineSegment(sketch, "E2421", {"start": v(-3.6, 1.55) * mm, "end": v(-3.85, 1.58) * mm});
            skLineSegment(sketch, "E2422", {"start": v(-3.85, 1.58) * mm, "end": v(-4.1, 1.58) * mm});
            skLineSegment(sketch, "E2423", {"start": v(-4.1, 1.58) * mm, "end": v(-4.35, 1.56) * mm});
            skLineSegment(sketch, "E2424", {"start": v(-4.35, 1.56) * mm, "end": v(-4.58, 1.5) * mm});
            skLineSegment(sketch, "E2425", {"start": v(-4.58, 1.5) * mm, "end": v(-4.8, 1.41) * mm});
            skLineSegment(sketch, "E2426", {"start": v(-4.8, 1.41) * mm, "end": v(-4.87, 1.36) * mm});
            skLineSegment(sketch, "E2427", {"start": v(-4.87, 1.36) * mm, "end": v(-4.96, 1.3) * mm});
            skLineSegment(sketch, "E2428", {"start": v(-4.96, 1.3) * mm, "end": v(-5.04, 1.24) * mm});
            skLineSegment(sketch, "E2429", {"start": v(-5.04, 1.24) * mm, "end": v(-5.08, 1.18) * mm});
            skLineSegment(sketch, "E2430", {"start": v(-5.08, 1.18) * mm, "end": v(-5.12, 1.12) * mm});
            skLineSegment(sketch, "E2431", {"start": v(-5.12, 1.12) * mm, "end": v(-5.15, 1.03) * mm});
            skLineSegment(sketch, "E2432", {"start": v(-5.15, 1.03) * mm, "end": v(-5.19, 0.94) * mm});
            skLineSegment(sketch, "E2433", {"start": v(-5.19, 0.94) * mm, "end": v(-5.2, 0.85) * mm});
            skLineSegment(sketch, "E2434", {"start": v(-5.2, 0.85) * mm, "end": v(-5.22, 0.75) * mm});
            skLineSegment(sketch, "E2435", {"start": v(-5.22, 0.75) * mm, "end": v(-5.23, 0.65) * mm});
            skLineSegment(sketch, "E2436", {"start": v(-5.23, 0.65) * mm, "end": v(-5.22, 0.57) * mm});
            skLineSegment(sketch, "E2437", {"start": v(-5.22, 0.57) * mm, "end": v(-5.2, 0.52) * mm});
            skLineSegment(sketch, "E2438", {"start": v(-5.2, 0.52) * mm, "end": v(-5.18, 0.5) * mm});
            skLineSegment(sketch, "E2439", {"start": v(-5.18, 0.5) * mm, "end": v(-5.17, 0.5) * mm});
            skLineSegment(sketch, "E2440", {"start": v(-5.17, 0.5) * mm, "end": v(-5.13, 0.5) * mm});
            skLineSegment(sketch, "E2441", {"start": v(-5.13, 0.5) * mm, "end": v(-5.07, 0.52) * mm});
            skLineSegment(sketch, "E2442", {"start": v(-0.18, 0.62) * mm, "end": v(-0.14, 0.63) * mm});
            skLineSegment(sketch, "E2443", {"start": v(-0.14, 0.63) * mm, "end": v(-0.1, 0.64) * mm});
            skLineSegment(sketch, "E2444", {"start": v(-0.1, 0.64) * mm, "end": v(-0.05, 0.65) * mm});
            skLineSegment(sketch, "E2445", {"start": v(-0.05, 0.65) * mm, "end": v(-0.01, 0.66) * mm});
            skLineSegment(sketch, "E2446", {"start": v(-0.01, 0.66) * mm, "end": v(0.06, 0.7) * mm});
            skLineSegment(sketch, "E2447", {"start": v(0.06, 0.7) * mm, "end": v(0.14, 0.73) * mm});
            skLineSegment(sketch, "E2448", {"start": v(0.14, 0.73) * mm, "end": v(0.2, 0.76) * mm});
            skLineSegment(sketch, "E2449", {"start": v(0.2, 0.76) * mm, "end": v(0.22, 0.78) * mm});
            skLineSegment(sketch, "E2450", {"start": v(0.22, 0.78) * mm, "end": v(0.2, 0.83) * mm});
            skLineSegment(sketch, "E2451", {"start": v(0.2, 0.83) * mm, "end": v(0.18, 0.92) * mm});
            skLineSegment(sketch, "E2452", {"start": v(0.18, 0.92) * mm, "end": v(0.15, 1.02) * mm});
            skLineSegment(sketch, "E2453", {"start": v(0.15, 1.02) * mm, "end": v(0.13, 1.1) * mm});
            skLineSegment(sketch, "E2454", {"start": v(0.13, 1.1) * mm, "end": v(0.07, 1.26) * mm});
            skLineSegment(sketch, "E2455", {"start": v(0.07, 1.26) * mm, "end": v(0.02, 1.36) * mm});
            skLineSegment(sketch, "E2456", {"start": v(0.02, 1.36) * mm, "end": v(0, 1.4) * mm});
            skLineSegment(sketch, "E2457", {"start": v(0, 1.4) * mm, "end": v(-0.03, 1.42) * mm});
            skLineSegment(sketch, "E2458", {"start": v(-0.03, 1.42) * mm, "end": v(-0.09, 1.4) * mm});
            skLineSegment(sketch, "E2459", {"start": v(-0.09, 1.4) * mm, "end": v(-0.17, 1.4) * mm});
            skLineSegment(sketch, "E2460", {"start": v(-0.17, 1.4) * mm, "end": v(-0.25, 1.38) * mm});
            skLineSegment(sketch, "E2461", {"start": v(-0.25, 1.38) * mm, "end": v(-0.32, 1.38) * mm});
            skLineSegment(sketch, "E2462", {"start": v(-0.32, 1.38) * mm, "end": v(-0.49, 1.4) * mm});
            skLineSegment(sketch, "E2463", {"start": v(-0.49, 1.4) * mm, "end": v(-0.7, 1.44) * mm});
            skLineSegment(sketch, "E2464", {"start": v(-0.7, 1.44) * mm, "end": v(-0.73, 1.45) * mm});
            skLineSegment(sketch, "E2465", {"start": v(-0.73, 1.45) * mm, "end": v(-0.76, 1.46) * mm});
            skLineSegment(sketch, "E2466", {"start": v(-0.76, 1.46) * mm, "end": v(-0.79, 1.47) * mm});
            skLineSegment(sketch, "E2467", {"start": v(-0.79, 1.47) * mm, "end": v(-0.8, 1.47) * mm});
            skLineSegment(sketch, "E2468", {"start": v(-0.8, 1.47) * mm, "end": v(-0.81, 1.44) * mm});
            skLineSegment(sketch, "E2469", {"start": v(-0.81, 1.44) * mm, "end": v(-0.83, 1.38) * mm});
            skLineSegment(sketch, "E2470", {"start": v(-0.83, 1.38) * mm, "end": v(-0.85, 1.3) * mm});
            skLineSegment(sketch, "E2471", {"start": v(-0.85, 1.3) * mm, "end": v(-0.87, 1.22) * mm});
            skLineSegment(sketch, "E2472", {"start": v(-0.87, 1.22) * mm, "end": v(-0.9, 1.13) * mm});
            skLineSegment(sketch, "E2473", {"start": v(-0.9, 1.13) * mm, "end": v(-0.92, 1.04) * mm});
            skLineSegment(sketch, "E2474", {"start": v(-0.92, 1.04) * mm, "end": v(-0.94, 0.95) * mm});
            skLineSegment(sketch, "E2475", {"start": v(-0.94, 0.95) * mm, "end": v(-0.95, 0.88) * mm});
            skLineSegment(sketch, "E2476", {"start": v(-0.95, 0.88) * mm, "end": v(-0.96, 0.85) * mm});
            skLineSegment(sketch, "E2477", {"start": v(-0.96, 0.85) * mm, "end": v(-0.96, 0.82) * mm});
            skLineSegment(sketch, "E2478", {"start": v(-0.96, 0.82) * mm, "end": v(-0.96, 0.8) * mm});
            skLineSegment(sketch, "E2479", {"start": v(-0.96, 0.8) * mm, "end": v(-0.95, 0.78) * mm});
            skLineSegment(sketch, "E2480", {"start": v(-0.95, 0.78) * mm, "end": v(-0.94, 0.77) * mm});
            skLineSegment(sketch, "E2481", {"start": v(-0.94, 0.77) * mm, "end": v(-0.92, 0.76) * mm});
            skLineSegment(sketch, "E2482", {"start": v(-0.92, 0.76) * mm, "end": v(-0.88, 0.74) * mm});
            skLineSegment(sketch, "E2483", {"start": v(-0.88, 0.74) * mm, "end": v(-0.84, 0.72) * mm});
            skLineSegment(sketch, "E2484", {"start": v(-0.84, 0.72) * mm, "end": v(-0.68, 0.66) * mm});
            skLineSegment(sketch, "E2485", {"start": v(-0.68, 0.66) * mm, "end": v(-0.51, 0.63) * mm});
            skLineSegment(sketch, "E2486", {"start": v(-0.51, 0.63) * mm, "end": v(-0.34, 0.61) * mm});
            skLineSegment(sketch, "E2487", {"start": v(-0.34, 0.61) * mm, "end": v(-0.18, 0.62) * mm});
            skLineSegment(sketch, "E2488", {"start": v(-7.02, 0.93) * mm, "end": v(-6.9, 1.04) * mm});
            skLineSegment(sketch, "E2489", {"start": v(-6.9, 1.04) * mm, "end": v(-6.79, 1.14) * mm});
            skLineSegment(sketch, "E2490", {"start": v(-6.79, 1.14) * mm, "end": v(-6.7, 1.22) * mm});
            skLineSegment(sketch, "E2491", {"start": v(-6.7, 1.22) * mm, "end": v(-6.63, 1.27) * mm});
            skLineSegment(sketch, "E2492", {"start": v(-6.63, 1.27) * mm, "end": v(-6.6, 1.28) * mm});
            skLineSegment(sketch, "E2493", {"start": v(-6.6, 1.28) * mm, "end": v(-6.56, 1.31) * mm});
            skLineSegment(sketch, "E2494", {"start": v(-6.56, 1.31) * mm, "end": v(-6.5, 1.35) * mm});
            skLineSegment(sketch, "E2495", {"start": v(-6.5, 1.35) * mm, "end": v(-6.43, 1.38) * mm});
            skLineSegment(sketch, "E2496", {"start": v(-6.43, 1.38) * mm, "end": v(-6.39, 1.41) * mm});
            skLineSegment(sketch, "E2497", {"start": v(-6.39, 1.41) * mm, "end": v(-6.35, 1.43) * mm});
            skLineSegment(sketch, "E2498", {"start": v(-6.35, 1.43) * mm, "end": v(-6.32, 1.45) * mm});
            skLineSegment(sketch, "E2499", {"start": v(-6.32, 1.45) * mm, "end": v(-6.3, 1.46) * mm});
            skLineSegment(sketch, "E2500", {"start": v(-6.3, 1.46) * mm, "end": v(-6.3, 1.47) * mm});
            skLineSegment(sketch, "E2501", {"start": v(-6.3, 1.47) * mm, "end": v(-6.3, 1.47) * mm});
            skLineSegment(sketch, "E2502", {"start": v(-6.3, 1.47) * mm, "end": v(-6.3, 1.48) * mm});
            skLineSegment(sketch, "E2503", {"start": v(-6.3, 1.48) * mm, "end": v(-6.3, 1.48) * mm});
            skLineSegment(sketch, "E2504", {"start": v(-6.3, 1.48) * mm, "end": v(-6.33, 1.49) * mm});
            skLineSegment(sketch, "E2505", {"start": v(-6.33, 1.49) * mm, "end": v(-6.4, 1.49) * mm});
            skLineSegment(sketch, "E2506", {"start": v(-6.4, 1.49) * mm, "end": v(-6.47, 1.5) * mm});
            skLineSegment(sketch, "E2507", {"start": v(-6.47, 1.5) * mm, "end": v(-6.56, 1.5) * mm});
            skLineSegment(sketch, "E2508", {"start": v(-6.56, 1.5) * mm, "end": v(-6.65, 1.49) * mm});
            skLineSegment(sketch, "E2509", {"start": v(-6.65, 1.49) * mm, "end": v(-6.75, 1.49) * mm});
            skLineSegment(sketch, "E2510", {"start": v(-6.75, 1.49) * mm, "end": v(-6.83, 1.48) * mm});
            skLineSegment(sketch, "E2511", {"start": v(-6.83, 1.48) * mm, "end": v(-6.9, 1.48) * mm});
            skLineSegment(sketch, "E2512", {"start": v(-6.9, 1.48) * mm, "end": v(-7.04, 1.46) * mm});
            skLineSegment(sketch, "E2513", {"start": v(-7.04, 1.46) * mm, "end": v(-7.17, 1.44) * mm});
            skLineSegment(sketch, "E2514", {"start": v(-7.17, 1.44) * mm, "end": v(-7.27, 1.42) * mm});
            skLineSegment(sketch, "E2515", {"start": v(-7.27, 1.42) * mm, "end": v(-7.34, 1.4) * mm});
            skLineSegment(sketch, "E2516", {"start": v(-7.34, 1.4) * mm, "end": v(-7.36, 1.4) * mm});
            skLineSegment(sketch, "E2517", {"start": v(-7.36, 1.4) * mm, "end": v(-7.41, 1.38) * mm});
            skLineSegment(sketch, "E2518", {"start": v(-7.41, 1.38) * mm, "end": v(-7.47, 1.37) * mm});
            skLineSegment(sketch, "E2519", {"start": v(-7.47, 1.37) * mm, "end": v(-7.54, 1.36) * mm});
            skLineSegment(sketch, "E2520", {"start": v(-7.54, 1.36) * mm, "end": v(-7.68, 1.33) * mm});
            skLineSegment(sketch, "E2521", {"start": v(-7.68, 1.33) * mm, "end": v(-7.81, 1.3) * mm});
            skLineSegment(sketch, "E2522", {"start": v(-7.81, 1.3) * mm, "end": v(-7.91, 1.27) * mm});
            skLineSegment(sketch, "E2523", {"start": v(-7.91, 1.27) * mm, "end": v(-7.95, 1.25) * mm});
            skLineSegment(sketch, "E2524", {"start": v(-7.95, 1.25) * mm, "end": v(-7.94, 1.24) * mm});
            skLineSegment(sketch, "E2525", {"start": v(-7.94, 1.24) * mm, "end": v(-7.93, 1.23) * mm});
            skLineSegment(sketch, "E2526", {"start": v(-7.93, 1.23) * mm, "end": v(-7.91, 1.22) * mm});
            skLineSegment(sketch, "E2527", {"start": v(-7.91, 1.22) * mm, "end": v(-7.89, 1.2) * mm});
            skLineSegment(sketch, "E2528", {"start": v(-7.89, 1.2) * mm, "end": v(-7.86, 1.18) * mm});
            skLineSegment(sketch, "E2529", {"start": v(-7.86, 1.18) * mm, "end": v(-7.82, 1.15) * mm});
            skLineSegment(sketch, "E2530", {"start": v(-7.82, 1.15) * mm, "end": v(-7.78, 1.12) * mm});
            skLineSegment(sketch, "E2531", {"start": v(-7.78, 1.12) * mm, "end": v(-7.75, 1.08) * mm});
            skLineSegment(sketch, "E2532", {"start": v(-7.75, 1.08) * mm, "end": v(-7.68, 1.03) * mm});
            skLineSegment(sketch, "E2533", {"start": v(-7.68, 1.03) * mm, "end": v(-7.61, 0.97) * mm});
            skLineSegment(sketch, "E2534", {"start": v(-7.61, 0.97) * mm, "end": v(-7.54, 0.92) * mm});
            skLineSegment(sketch, "E2535", {"start": v(-7.54, 0.92) * mm, "end": v(-7.46, 0.87) * mm});
            skLineSegment(sketch, "E2536", {"start": v(-7.46, 0.87) * mm, "end": v(-7.39, 0.83) * mm});
            skLineSegment(sketch, "E2537", {"start": v(-7.39, 0.83) * mm, "end": v(-7.32, 0.8) * mm});
            skLineSegment(sketch, "E2538", {"start": v(-7.32, 0.8) * mm, "end": v(-7.26, 0.78) * mm});
            skLineSegment(sketch, "E2539", {"start": v(-7.26, 0.78) * mm, "end": v(-7.22, 0.77) * mm});
            skLineSegment(sketch, "E2540", {"start": v(-7.22, 0.77) * mm, "end": v(-7.21, 0.77) * mm});
            skLineSegment(sketch, "E2541", {"start": v(-7.21, 0.77) * mm, "end": v(-7.2, 0.77) * mm});
            skLineSegment(sketch, "E2542", {"start": v(-7.2, 0.77) * mm, "end": v(-7.18, 0.78) * mm});
            skLineSegment(sketch, "E2543", {"start": v(-7.18, 0.78) * mm, "end": v(-7.16, 0.8) * mm});
            skLineSegment(sketch, "E2544", {"start": v(-7.16, 0.8) * mm, "end": v(-7.14, 0.82) * mm});
            skLineSegment(sketch, "E2545", {"start": v(-7.14, 0.82) * mm, "end": v(-7.1, 0.85) * mm});
            skLineSegment(sketch, "E2546", {"start": v(-7.1, 0.85) * mm, "end": v(-7.07, 0.88) * mm});
            skLineSegment(sketch, "E2547", {"start": v(-7.07, 0.88) * mm, "end": v(-7.02, 0.93) * mm});
            skLineSegment(sketch, "E2548", {"start": v(-1.18, 0.93) * mm, "end": v(-1.2, 0.97) * mm});
            skLineSegment(sketch, "E2549", {"start": v(-1.2, 0.97) * mm, "end": v(-1.22, 1.01) * mm});
            skLineSegment(sketch, "E2550", {"start": v(-1.22, 1.01) * mm, "end": v(-1.25, 1.07) * mm});
            skLineSegment(sketch, "E2551", {"start": v(-1.25, 1.07) * mm, "end": v(-1.3, 1.14) * mm});
            skLineSegment(sketch, "E2552", {"start": v(-1.3, 1.14) * mm, "end": v(-1.36, 1.21) * mm});
            skLineSegment(sketch, "E2553", {"start": v(-1.36, 1.21) * mm, "end": v(-1.41, 1.28) * mm});
            skLineSegment(sketch, "E2554", {"start": v(-1.41, 1.28) * mm, "end": v(-1.47, 1.34) * mm});
            skLineSegment(sketch, "E2555", {"start": v(-1.47, 1.34) * mm, "end": v(-1.53, 1.4) * mm});
            skLineSegment(sketch, "E2556", {"start": v(-1.53, 1.4) * mm, "end": v(-1.57, 1.44) * mm});
            skLineSegment(sketch, "E2557", {"start": v(-1.57, 1.44) * mm, "end": v(-1.62, 1.48) * mm});
            skLineSegment(sketch, "E2558", {"start": v(-1.62, 1.48) * mm, "end": v(-1.67, 1.54) * mm});
            skLineSegment(sketch, "E2559", {"start": v(-1.67, 1.54) * mm, "end": v(-1.73, 1.59) * mm});
            skLineSegment(sketch, "E2560", {"start": v(-1.73, 1.59) * mm, "end": v(-1.83, 1.68) * mm});
            skLineSegment(sketch, "E2561", {"start": v(-1.83, 1.68) * mm, "end": v(-1.92, 1.76) * mm});
            skLineSegment(sketch, "E2562", {"start": v(-1.92, 1.76) * mm, "end": v(-2, 1.82) * mm});
            skLineSegment(sketch, "E2563", {"start": v(-2, 1.82) * mm, "end": v(-2.06, 1.86) * mm});
            skLineSegment(sketch, "E2564", {"start": v(-2.06, 1.86) * mm, "end": v(-2.1, 1.89) * mm});
            skLineSegment(sketch, "E2565", {"start": v(-2.1, 1.89) * mm, "end": v(-2.15, 1.92) * mm});
            skLineSegment(sketch, "E2566", {"start": v(-2.15, 1.92) * mm, "end": v(-2.23, 1.97) * mm});
            skLineSegment(sketch, "E2567", {"start": v(-2.23, 1.97) * mm, "end": v(-2.32, 2.03) * mm});
            skLineSegment(sketch, "E2568", {"start": v(-2.32, 2.03) * mm, "end": v(-2.42, 2.1) * mm});
            skLineSegment(sketch, "E2569", {"start": v(-2.42, 2.1) * mm, "end": v(-2.5, 2.15) * mm});
            skLineSegment(sketch, "E2570", {"start": v(-2.5, 2.15) * mm, "end": v(-2.59, 2.2) * mm});
            skLineSegment(sketch, "E2571", {"start": v(-2.59, 2.2) * mm, "end": v(-2.67, 2.23) * mm});
            skLineSegment(sketch, "E2572", {"start": v(-2.67, 2.23) * mm, "end": v(-2.73, 2.25) * mm});
            skLineSegment(sketch, "E2573", {"start": v(-2.73, 2.25) * mm, "end": v(-2.78, 2.27) * mm});
            skLineSegment(sketch, "E2574", {"start": v(-2.78, 2.27) * mm, "end": v(-2.81, 2.28) * mm});
            skLineSegment(sketch, "E2575", {"start": v(-2.81, 2.28) * mm, "end": v(-2.83, 2.29) * mm});
            skLineSegment(sketch, "E2576", {"start": v(-2.83, 2.29) * mm, "end": v(-2.84, 2.28) * mm});
            skLineSegment(sketch, "E2577", {"start": v(-2.84, 2.28) * mm, "end": v(-2.85, 2.27) * mm});
            skLineSegment(sketch, "E2578", {"start": v(-2.85, 2.27) * mm, "end": v(-2.86, 2.26) * mm});
            skLineSegment(sketch, "E2579", {"start": v(-2.86, 2.26) * mm, "end": v(-2.88, 2.23) * mm});
            skLineSegment(sketch, "E2580", {"start": v(-2.88, 2.23) * mm, "end": v(-2.89, 2.21) * mm});
            skLineSegment(sketch, "E2581", {"start": v(-2.89, 2.21) * mm, "end": v(-2.9, 2.19) * mm});
            skLineSegment(sketch, "E2582", {"start": v(-2.9, 2.19) * mm, "end": v(-2.9, 2.16) * mm});
            skLineSegment(sketch, "E2583", {"start": v(-2.9, 2.16) * mm, "end": v(-2.9, 2.15) * mm});
            skLineSegment(sketch, "E2584", {"start": v(-2.9, 2.15) * mm, "end": v(-2.9, 2.08) * mm});
            skLineSegment(sketch, "E2585", {"start": v(-2.9, 2.08) * mm, "end": v(-2.88, 2) * mm});
            skLineSegment(sketch, "E2586", {"start": v(-2.88, 2) * mm, "end": v(-2.86, 1.92) * mm});
            skLineSegment(sketch, "E2587", {"start": v(-2.86, 1.92) * mm, "end": v(-2.84, 1.86) * mm});
            skLineSegment(sketch, "E2588", {"start": v(-2.84, 1.86) * mm, "end": v(-2.8, 1.8) * mm});
            skLineSegment(sketch, "E2589", {"start": v(-2.8, 1.8) * mm, "end": v(-2.74, 1.72) * mm});
            skLineSegment(sketch, "E2590", {"start": v(-2.74, 1.72) * mm, "end": v(-2.66, 1.65) * mm});
            skLineSegment(sketch, "E2591", {"start": v(-2.66, 1.65) * mm, "end": v(-2.6, 1.6) * mm});
            skLineSegment(sketch, "E2592", {"start": v(-2.6, 1.6) * mm, "end": v(-2.55, 1.56) * mm});
            skLineSegment(sketch, "E2593", {"start": v(-2.55, 1.56) * mm, "end": v(-2.51, 1.53) * mm});
            skLineSegment(sketch, "E2594", {"start": v(-2.51, 1.53) * mm, "end": v(-2.48, 1.5) * mm});
            skLineSegment(sketch, "E2595", {"start": v(-2.48, 1.5) * mm, "end": v(-2.46, 1.5) * mm});
            skLineSegment(sketch, "E2596", {"start": v(-2.46, 1.5) * mm, "end": v(-2.4, 1.44) * mm});
            skLineSegment(sketch, "E2597", {"start": v(-2.4, 1.44) * mm, "end": v(-2.32, 1.4) * mm});
            skLineSegment(sketch, "E2598", {"start": v(-2.32, 1.4) * mm, "end": v(-2.2, 1.33) * mm});
            skLineSegment(sketch, "E2599", {"start": v(-2.2, 1.33) * mm, "end": v(-2.04, 1.25) * mm});
            skLineSegment(sketch, "E2600", {"start": v(-2.04, 1.25) * mm, "end": v(-1.8, 1.14) * mm});
            skLineSegment(sketch, "E2601", {"start": v(-1.8, 1.14) * mm, "end": v(-1.61, 1.06) * mm});
            skLineSegment(sketch, "E2602", {"start": v(-1.61, 1.06) * mm, "end": v(-1.44, 1) * mm});
            skLineSegment(sketch, "E2603", {"start": v(-1.44, 1) * mm, "end": v(-1.27, 0.94) * mm});
            skLineSegment(sketch, "E2604", {"start": v(-1.27, 0.94) * mm, "end": v(-1.22, 0.93) * mm});
            skLineSegment(sketch, "E2605", {"start": v(-1.22, 0.93) * mm, "end": v(-1.2, 0.92) * mm});
            skLineSegment(sketch, "E2606", {"start": v(-1.2, 0.92) * mm, "end": v(-1.18, 0.93) * mm});
            skLineSegment(sketch, "E2607", {"start": v(-1.18, 0.93) * mm, "end": v(-1.18, 0.93) * mm});
            skLineSegment(sketch, "E2608", {"start": v(6.79, 1.32) * mm, "end": v(6.89, 1.4) * mm});
            skLineSegment(sketch, "E2609", {"start": v(6.89, 1.4) * mm, "end": v(6.97, 1.48) * mm});
            skLineSegment(sketch, "E2610", {"start": v(6.97, 1.48) * mm, "end": v(7.04, 1.56) * mm});
            skLineSegment(sketch, "E2611", {"start": v(7.04, 1.56) * mm, "end": v(7.12, 1.66) * mm});
            skLineSegment(sketch, "E2612", {"start": v(7.12, 1.66) * mm, "end": v(7.16, 1.72) * mm});
            skLineSegment(sketch, "E2613", {"start": v(7.16, 1.72) * mm, "end": v(7.2, 1.79) * mm});
            skLineSegment(sketch, "E2614", {"start": v(7.2, 1.79) * mm, "end": v(7.25, 1.86) * mm});
            skLineSegment(sketch, "E2615", {"start": v(7.25, 1.86) * mm, "end": v(7.3, 1.92) * mm});
            skLineSegment(sketch, "E2616", {"start": v(7.3, 1.92) * mm, "end": v(7.33, 1.98) * mm});
            skLineSegment(sketch, "E2617", {"start": v(7.33, 1.98) * mm, "end": v(7.36, 2.03) * mm});
            skLineSegment(sketch, "E2618", {"start": v(7.36, 2.03) * mm, "end": v(7.38, 2.07) * mm});
            skLineSegment(sketch, "E2619", {"start": v(7.38, 2.07) * mm, "end": v(7.38, 2.1) * mm});
            skLineSegment(sketch, "E2620", {"start": v(7.38, 2.1) * mm, "end": v(7.37, 2.1) * mm});
            skLineSegment(sketch, "E2621", {"start": v(7.37, 2.1) * mm, "end": v(7.33, 2.12) * mm});
            skLineSegment(sketch, "E2622", {"start": v(7.33, 2.12) * mm, "end": v(7.27, 2.13) * mm});
            skLineSegment(sketch, "E2623", {"start": v(7.27, 2.13) * mm, "end": v(7.2, 2.14) * mm});
            skLineSegment(sketch, "E2624", {"start": v(7.2, 2.14) * mm, "end": v(7.1, 2.14) * mm});
            skLineSegment(sketch, "E2625", {"start": v(7.1, 2.14) * mm, "end": v(7.01, 2.14) * mm});
            skLineSegment(sketch, "E2626", {"start": v(7.01, 2.14) * mm, "end": v(6.92, 2.13) * mm});
            skLineSegment(sketch, "E2627", {"start": v(6.92, 2.13) * mm, "end": v(6.84, 2.12) * mm});
            skLineSegment(sketch, "E2628", {"start": v(6.84, 2.12) * mm, "end": v(6.7, 2.09) * mm});
            skLineSegment(sketch, "E2629", {"start": v(6.7, 2.09) * mm, "end": v(6.53, 2.03) * mm});
            skLineSegment(sketch, "E2630", {"start": v(6.53, 2.03) * mm, "end": v(6.36, 1.97) * mm});
            skLineSegment(sketch, "E2631", {"start": v(6.36, 1.97) * mm, "end": v(6.18, 1.88) * mm});
            skLineSegment(sketch, "E2632", {"start": v(6.18, 1.88) * mm, "end": v(6.03, 1.82) * mm});
            skLineSegment(sketch, "E2633", {"start": v(6.03, 1.82) * mm, "end": v(5.92, 1.77) * mm});
            skLineSegment(sketch, "E2634", {"start": v(5.92, 1.77) * mm, "end": v(5.83, 1.75) * mm});
            skLineSegment(sketch, "E2635", {"start": v(5.83, 1.75) * mm, "end": v(5.71, 1.72) * mm});
            skLineSegment(sketch, "E2636", {"start": v(5.71, 1.72) * mm, "end": v(5.67, 1.71) * mm});
            skLineSegment(sketch, "E2637", {"start": v(5.67, 1.71) * mm, "end": v(5.63, 1.7) * mm});
            skLineSegment(sketch, "E2638", {"start": v(5.63, 1.7) * mm, "end": v(5.6, 1.7) * mm});
            skLineSegment(sketch, "E2639", {"start": v(5.6, 1.7) * mm, "end": v(5.59, 1.7) * mm});
            skLineSegment(sketch, "E2640", {"start": v(5.59, 1.7) * mm, "end": v(5.59, 1.69) * mm});
            skLineSegment(sketch, "E2641", {"start": v(5.59, 1.69) * mm, "end": v(5.6, 1.68) * mm});
            skLineSegment(sketch, "E2642", {"start": v(5.6, 1.68) * mm, "end": v(5.65, 1.67) * mm});
            skLineSegment(sketch, "E2643", {"start": v(5.65, 1.67) * mm, "end": v(5.73, 1.66) * mm});
            skLineSegment(sketch, "E2644", {"start": v(5.73, 1.66) * mm, "end": v(5.79, 1.65) * mm});
            skLineSegment(sketch, "E2645", {"start": v(5.79, 1.65) * mm, "end": v(5.84, 1.64) * mm});
            skLineSegment(sketch, "E2646", {"start": v(5.84, 1.64) * mm, "end": v(5.88, 1.63) * mm});
            skLineSegment(sketch, "E2647", {"start": v(5.88, 1.63) * mm, "end": v(5.93, 1.62) * mm});
            skLineSegment(sketch, "E2648", {"start": v(5.93, 1.62) * mm, "end": v(5.98, 1.6) * mm});
            skLineSegment(sketch, "E2649", {"start": v(5.98, 1.6) * mm, "end": v(6.04, 1.58) * mm});
            skLineSegment(sketch, "E2650", {"start": v(6.04, 1.58) * mm, "end": v(6.1, 1.55) * mm});
            skLineSegment(sketch, "E2651", {"start": v(6.1, 1.55) * mm, "end": v(6.18, 1.5) * mm});
            skLineSegment(sketch, "E2652", {"start": v(6.18, 1.5) * mm, "end": v(6.33, 1.43) * mm});
            skLineSegment(sketch, "E2653", {"start": v(6.33, 1.43) * mm, "end": v(6.47, 1.36) * mm});
            skLineSegment(sketch, "E2654", {"start": v(6.47, 1.36) * mm, "end": v(6.57, 1.3) * mm});
            skLineSegment(sketch, "E2655", {"start": v(6.57, 1.3) * mm, "end": v(6.63, 1.24) * mm});
            skLineSegment(sketch, "E2656", {"start": v(6.63, 1.24) * mm, "end": v(6.64, 1.23) * mm});
            skLineSegment(sketch, "E2657", {"start": v(6.64, 1.23) * mm, "end": v(6.66, 1.22) * mm});
            skLineSegment(sketch, "E2658", {"start": v(6.66, 1.22) * mm, "end": v(6.67, 1.23) * mm});
            skLineSegment(sketch, "E2659", {"start": v(6.67, 1.23) * mm, "end": v(6.7, 1.25) * mm});
            skLineSegment(sketch, "E2660", {"start": v(6.7, 1.25) * mm, "end": v(6.74, 1.28) * mm});
            skLineSegment(sketch, "E2661", {"start": v(6.74, 1.28) * mm, "end": v(6.79, 1.32) * mm});
            skLineSegment(sketch, "E2662", {"start": v(2.38, 1.44) * mm, "end": v(2.47, 1.46) * mm});
            skLineSegment(sketch, "E2663", {"start": v(2.47, 1.46) * mm, "end": v(2.58, 1.48) * mm});
            skLineSegment(sketch, "E2664", {"start": v(2.58, 1.48) * mm, "end": v(2.71, 1.5) * mm});
            skLineSegment(sketch, "E2665", {"start": v(2.71, 1.5) * mm, "end": v(2.85, 1.53) * mm});
            skLineSegment(sketch, "E2666", {"start": v(2.85, 1.53) * mm, "end": v(3, 1.56) * mm});
            skLineSegment(sketch, "E2667", {"start": v(3, 1.56) * mm, "end": v(3.12, 1.58) * mm});
            skLineSegment(sketch, "E2668", {"start": v(3.12, 1.58) * mm, "end": v(3.23, 1.6) * mm});
            skLineSegment(sketch, "E2669", {"start": v(3.23, 1.6) * mm, "end": v(3.3, 1.6) * mm});
            skLineSegment(sketch, "E2670", {"start": v(3.3, 1.6) * mm, "end": v(3.34, 1.6) * mm});
            skLineSegment(sketch, "E2671", {"start": v(3.34, 1.6) * mm, "end": v(3.4, 1.62) * mm});
            skLineSegment(sketch, "E2672", {"start": v(3.4, 1.62) * mm, "end": v(3.45, 1.62) * mm});
            skLineSegment(sketch, "E2673", {"start": v(3.45, 1.62) * mm, "end": v(3.5, 1.63) * mm});
            skLineSegment(sketch, "E2674", {"start": v(3.5, 1.63) * mm, "end": v(3.58, 1.64) * mm});
            skLineSegment(sketch, "E2675", {"start": v(3.58, 1.64) * mm, "end": v(3.71, 1.65) * mm});
            skLineSegment(sketch, "E2676", {"start": v(3.71, 1.65) * mm, "end": v(3.88, 1.67) * mm});
            skLineSegment(sketch, "E2677", {"start": v(3.88, 1.67) * mm, "end": v(4.05, 1.68) * mm});
            skLineSegment(sketch, "E2678", {"start": v(4.05, 1.68) * mm, "end": v(4.26, 1.7) * mm});
            skLineSegment(sketch, "E2679", {"start": v(4.26, 1.7) * mm, "end": v(4.42, 1.72) * mm});
            skLineSegment(sketch, "E2680", {"start": v(4.42, 1.72) * mm, "end": v(4.54, 1.73) * mm});
            skLineSegment(sketch, "E2681", {"start": v(4.54, 1.73) * mm, "end": v(4.63, 1.74) * mm});
            skLineSegment(sketch, "E2682", {"start": v(4.63, 1.74) * mm, "end": v(4.7, 1.75) * mm});
            skLineSegment(sketch, "E2683", {"start": v(4.7, 1.75) * mm, "end": v(4.74, 1.76) * mm});
            skLineSegment(sketch, "E2684", {"start": v(4.74, 1.76) * mm, "end": v(4.78, 1.78) * mm});
            skLineSegment(sketch, "E2685", {"start": v(4.78, 1.78) * mm, "end": v(4.82, 1.8) * mm});
            skLineSegment(sketch, "E2686", {"start": v(4.82, 1.8) * mm, "end": v(4.98, 1.87) * mm});
            skLineSegment(sketch, "E2687", {"start": v(4.98, 1.87) * mm, "end": v(5.16, 1.98) * mm});
            skLineSegment(sketch, "E2688", {"start": v(5.16, 1.98) * mm, "end": v(5.34, 2.11) * mm});
            skLineSegment(sketch, "E2689", {"start": v(5.34, 2.11) * mm, "end": v(5.5, 2.24) * mm});
            skLineSegment(sketch, "E2690", {"start": v(5.5, 2.24) * mm, "end": v(5.55, 2.28) * mm});
            skLineSegment(sketch, "E2691", {"start": v(5.55, 2.28) * mm, "end": v(5.59, 2.31) * mm});
            skLineSegment(sketch, "E2692", {"start": v(5.59, 2.31) * mm, "end": v(5.62, 2.34) * mm});
            skLineSegment(sketch, "E2693", {"start": v(5.62, 2.34) * mm, "end": v(5.65, 2.37) * mm});
            skLineSegment(sketch, "E2694", {"start": v(5.65, 2.37) * mm, "end": v(5.68, 2.4) * mm});
            skLineSegment(sketch, "E2695", {"start": v(5.68, 2.4) * mm, "end": v(5.7, 2.42) * mm});
            skLineSegment(sketch, "E2696", {"start": v(5.7, 2.42) * mm, "end": v(5.69, 2.43) * mm});
            skLineSegment(sketch, "E2697", {"start": v(5.69, 2.43) * mm, "end": v(5.65, 2.43) * mm});
            skLineSegment(sketch, "E2698", {"start": v(5.65, 2.43) * mm, "end": v(5.6, 2.42) * mm});
            skLineSegment(sketch, "E2699", {"start": v(5.6, 2.42) * mm, "end": v(5.5, 2.42) * mm});
            skLineSegment(sketch, "E2700", {"start": v(5.5, 2.42) * mm, "end": v(5.39, 2.42) * mm});
            skLineSegment(sketch, "E2701", {"start": v(5.39, 2.42) * mm, "end": v(5.26, 2.41) * mm});
            skLineSegment(sketch, "E2702", {"start": v(5.26, 2.41) * mm, "end": v(5.12, 2.42) * mm});
            skLineSegment(sketch, "E2703", {"start": v(5.12, 2.42) * mm, "end": v(5, 2.42) * mm});
            skLineSegment(sketch, "E2704", {"start": v(5, 2.42) * mm, "end": v(4.87, 2.42) * mm});
            skLineSegment(sketch, "E2705", {"start": v(4.87, 2.42) * mm, "end": v(4.77, 2.43) * mm});
            skLineSegment(sketch, "E2706", {"start": v(4.77, 2.43) * mm, "end": v(4.56, 2.44) * mm});
            skLineSegment(sketch, "E2707", {"start": v(4.56, 2.44) * mm, "end": v(4.4, 2.46) * mm});
            skLineSegment(sketch, "E2708", {"start": v(4.4, 2.46) * mm, "end": v(4.3, 2.47) * mm});
            skLineSegment(sketch, "E2709", {"start": v(4.3, 2.47) * mm, "end": v(4.2, 2.49) * mm});
            skLineSegment(sketch, "E2710", {"start": v(4.2, 2.49) * mm, "end": v(4.11, 2.5) * mm});
            skLineSegment(sketch, "E2711", {"start": v(4.11, 2.5) * mm, "end": v(4.04, 2.5) * mm});
            skLineSegment(sketch, "E2712", {"start": v(4.04, 2.5) * mm, "end": v(3.95, 2.5) * mm});
            skLineSegment(sketch, "E2713", {"start": v(3.95, 2.5) * mm, "end": v(3.83, 2.5) * mm});
            skLineSegment(sketch, "E2714", {"start": v(3.83, 2.5) * mm, "end": v(3.7, 2.5) * mm});
            skLineSegment(sketch, "E2715", {"start": v(3.7, 2.5) * mm, "end": v(3.63, 2.49) * mm});
            skLineSegment(sketch, "E2716", {"start": v(3.63, 2.49) * mm, "end": v(3.56, 2.48) * mm});
            skLineSegment(sketch, "E2717", {"start": v(3.56, 2.48) * mm, "end": v(3.5, 2.46) * mm});
            skLineSegment(sketch, "E2718", {"start": v(3.5, 2.46) * mm, "end": v(3.37, 2.42) * mm});
            skLineSegment(sketch, "E2719", {"start": v(3.37, 2.42) * mm, "end": v(3.26, 2.38) * mm});
            skLineSegment(sketch, "E2720", {"start": v(3.26, 2.38) * mm, "end": v(3.15, 2.33) * mm});
            skLineSegment(sketch, "E2721", {"start": v(3.15, 2.33) * mm, "end": v(3.01, 2.25) * mm});
            skLineSegment(sketch, "E2722", {"start": v(3.01, 2.25) * mm, "end": v(2.8, 2.1) * mm});
            skLineSegment(sketch, "E2723", {"start": v(2.8, 2.1) * mm, "end": v(2.61, 1.95) * mm});
            skLineSegment(sketch, "E2724", {"start": v(2.61, 1.95) * mm, "end": v(2.44, 1.77) * mm});
            skLineSegment(sketch, "E2725", {"start": v(2.44, 1.77) * mm, "end": v(2.3, 1.57) * mm});
            skLineSegment(sketch, "E2726", {"start": v(2.3, 1.57) * mm, "end": v(2.28, 1.55) * mm});
            skLineSegment(sketch, "E2727", {"start": v(2.28, 1.55) * mm, "end": v(2.26, 1.52) * mm});
            skLineSegment(sketch, "E2728", {"start": v(2.26, 1.52) * mm, "end": v(2.23, 1.49) * mm});
            skLineSegment(sketch, "E2729", {"start": v(2.23, 1.49) * mm, "end": v(2.2, 1.46) * mm});
            skLineSegment(sketch, "E2730", {"start": v(2.2, 1.46) * mm, "end": v(2.2, 1.44) * mm});
            skLineSegment(sketch, "E2731", {"start": v(2.2, 1.44) * mm, "end": v(2.18, 1.42) * mm});
            skLineSegment(sketch, "E2732", {"start": v(2.18, 1.42) * mm, "end": v(2.17, 1.4) * mm});
            skLineSegment(sketch, "E2733", {"start": v(2.17, 1.4) * mm, "end": v(2.17, 1.4) * mm});
            skLineSegment(sketch, "E2734", {"start": v(2.17, 1.4) * mm, "end": v(2.19, 1.39) * mm});
            skLineSegment(sketch, "E2735", {"start": v(2.19, 1.39) * mm, "end": v(2.23, 1.4) * mm});
            skLineSegment(sketch, "E2736", {"start": v(2.23, 1.4) * mm, "end": v(2.26, 1.4) * mm});
            skLineSegment(sketch, "E2737", {"start": v(2.26, 1.4) * mm, "end": v(2.3, 1.41) * mm});
            skLineSegment(sketch, "E2738", {"start": v(2.3, 1.41) * mm, "end": v(2.34, 1.43) * mm});
            skLineSegment(sketch, "E2739", {"start": v(2.34, 1.43) * mm, "end": v(2.38, 1.44) * mm});
            skLineSegment(sketch, "E2740", {"start": v(-8.08, 1.48) * mm, "end": v(-7.62, 1.57) * mm});
            skLineSegment(sketch, "E2741", {"start": v(-7.62, 1.57) * mm, "end": v(-7.17, 1.63) * mm});
            skLineSegment(sketch, "E2742", {"start": v(-7.17, 1.63) * mm, "end": v(-7.09, 1.64) * mm});
            skLineSegment(sketch, "E2743", {"start": v(-7.09, 1.64) * mm, "end": v(-7, 1.65) * mm});
            skLineSegment(sketch, "E2744", {"start": v(-7, 1.65) * mm, "end": v(-6.93, 1.66) * mm});
            skLineSegment(sketch, "E2745", {"start": v(-6.93, 1.66) * mm, "end": v(-6.88, 1.67) * mm});
            skLineSegment(sketch, "E2746", {"start": v(-6.88, 1.67) * mm, "end": v(-6.77, 1.67) * mm});
            skLineSegment(sketch, "E2747", {"start": v(-6.77, 1.67) * mm, "end": v(-6.62, 1.68) * mm});
            skLineSegment(sketch, "E2748", {"start": v(-6.62, 1.68) * mm, "end": v(-6.55, 1.68) * mm});
            skLineSegment(sketch, "E2749", {"start": v(-6.55, 1.68) * mm, "end": v(-6.5, 1.68) * mm});
            skLineSegment(sketch, "E2750", {"start": v(-6.5, 1.68) * mm, "end": v(-6.47, 1.68) * mm});
            skLineSegment(sketch, "E2751", {"start": v(-6.47, 1.68) * mm, "end": v(-6.47, 1.69) * mm});
            skLineSegment(sketch, "E2752", {"start": v(-6.47, 1.69) * mm, "end": v(-6.48, 1.7) * mm});
            skLineSegment(sketch, "E2753", {"start": v(-6.48, 1.7) * mm, "end": v(-6.5, 1.7) * mm});
            skLineSegment(sketch, "E2754", {"start": v(-6.5, 1.7) * mm, "end": v(-6.53, 1.72) * mm});
            skLineSegment(sketch, "E2755", {"start": v(-6.53, 1.72) * mm, "end": v(-6.56, 1.73) * mm});
            skLineSegment(sketch, "E2756", {"start": v(-6.56, 1.73) * mm, "end": v(-6.72, 1.8) * mm});
            skLineSegment(sketch, "E2757", {"start": v(-6.72, 1.8) * mm, "end": v(-6.88, 1.89) * mm});
            skLineSegment(sketch, "E2758", {"start": v(-6.88, 1.89) * mm, "end": v(-7.04, 1.97) * mm});
            skLineSegment(sketch, "E2759", {"start": v(-7.04, 1.97) * mm, "end": v(-7.16, 2.04) * mm});
            skLineSegment(sketch, "E2760", {"start": v(-7.16, 2.04) * mm, "end": v(-7.27, 2.11) * mm});
            skLineSegment(sketch, "E2761", {"start": v(-7.27, 2.11) * mm, "end": v(-7.34, 2.16) * mm});
            skLineSegment(sketch, "E2762", {"start": v(-7.34, 2.16) * mm, "end": v(-7.4, 2.18) * mm});
            skLineSegment(sketch, "E2763", {"start": v(-7.4, 2.18) * mm, "end": v(-7.42, 2.19) * mm});
            skLineSegment(sketch, "E2764", {"start": v(-7.42, 2.19) * mm, "end": v(-7.45, 2.2) * mm});
            skLineSegment(sketch, "E2765", {"start": v(-7.45, 2.2) * mm, "end": v(-7.5, 2.2) * mm});
            skLineSegment(sketch, "E2766", {"start": v(-7.5, 2.2) * mm, "end": v(-7.56, 2.21) * mm});
            skLineSegment(sketch, "E2767", {"start": v(-7.56, 2.21) * mm, "end": v(-7.63, 2.23) * mm});
            skLineSegment(sketch, "E2768", {"start": v(-7.63, 2.23) * mm, "end": v(-7.71, 2.24) * mm});
            skLineSegment(sketch, "E2769", {"start": v(-7.71, 2.24) * mm, "end": v(-7.78, 2.26) * mm});
            skLineSegment(sketch, "E2770", {"start": v(-7.78, 2.26) * mm, "end": v(-7.84, 2.27) * mm});
            skLineSegment(sketch, "E2771", {"start": v(-7.84, 2.27) * mm, "end": v(-7.89, 2.28) * mm});
            skLineSegment(sketch, "E2772", {"start": v(-7.89, 2.28) * mm, "end": v(-8.04, 2.33) * mm});
            skLineSegment(sketch, "E2773", {"start": v(-8.04, 2.33) * mm, "end": v(-8.2, 2.43) * mm});
            skLineSegment(sketch, "E2774", {"start": v(-8.2, 2.43) * mm, "end": v(-8.3, 2.5) * mm});
            skLineSegment(sketch, "E2775", {"start": v(-8.3, 2.5) * mm, "end": v(-8.41, 2.58) * mm});
            skLineSegment(sketch, "E2776", {"start": v(-8.41, 2.58) * mm, "end": v(-8.5, 2.65) * mm});
            skLineSegment(sketch, "E2777", {"start": v(-8.5, 2.65) * mm, "end": v(-8.6, 2.72) * mm});
            skLineSegment(sketch, "E2778", {"start": v(-8.6, 2.72) * mm, "end": v(-8.62, 2.74) * mm});
            skLineSegment(sketch, "E2779", {"start": v(-8.62, 2.74) * mm, "end": v(-8.65, 2.76) * mm});
            skLineSegment(sketch, "E2780", {"start": v(-8.65, 2.76) * mm, "end": v(-8.67, 2.77) * mm});
            skLineSegment(sketch, "E2781", {"start": v(-8.67, 2.77) * mm, "end": v(-8.68, 2.77) * mm});
            skLineSegment(sketch, "E2782", {"start": v(-8.68, 2.77) * mm, "end": v(-8.69, 2.76) * mm});
            skLineSegment(sketch, "E2783", {"start": v(-8.69, 2.76) * mm, "end": v(-8.69, 2.72) * mm});
            skLineSegment(sketch, "E2784", {"start": v(-8.69, 2.72) * mm, "end": v(-8.7, 2.67) * mm});
            skLineSegment(sketch, "E2785", {"start": v(-8.7, 2.67) * mm, "end": v(-8.7, 2.6) * mm});
            skLineSegment(sketch, "E2786", {"start": v(-8.7, 2.6) * mm, "end": v(-8.68, 2.4) * mm});
            skLineSegment(sketch, "E2787", {"start": v(-8.68, 2.4) * mm, "end": v(-8.65, 2.18) * mm});
            skLineSegment(sketch, "E2788", {"start": v(-8.65, 2.18) * mm, "end": v(-8.6, 1.96) * mm});
            skLineSegment(sketch, "E2789", {"start": v(-8.6, 1.96) * mm, "end": v(-8.54, 1.78) * mm});
            skLineSegment(sketch, "E2790", {"start": v(-8.54, 1.78) * mm, "end": v(-8.53, 1.74) * mm});
            skLineSegment(sketch, "E2791", {"start": v(-8.53, 1.74) * mm, "end": v(-8.51, 1.71) * mm});
            skLineSegment(sketch, "E2792", {"start": v(-8.51, 1.71) * mm, "end": v(-8.5, 1.69) * mm});
            skLineSegment(sketch, "E2793", {"start": v(-8.5, 1.69) * mm, "end": v(-8.5, 1.68) * mm});
            skLineSegment(sketch, "E2794", {"start": v(-8.5, 1.68) * mm, "end": v(-8.5, 1.66) * mm});
            skLineSegment(sketch, "E2795", {"start": v(-8.5, 1.66) * mm, "end": v(-8.5, 1.64) * mm});
            skLineSegment(sketch, "E2796", {"start": v(-8.5, 1.64) * mm, "end": v(-8.48, 1.61) * mm});
            skLineSegment(sketch, "E2797", {"start": v(-8.48, 1.61) * mm, "end": v(-8.47, 1.58) * mm});
            skLineSegment(sketch, "E2798", {"start": v(-8.47, 1.58) * mm, "end": v(-8.45, 1.55) * mm});
            skLineSegment(sketch, "E2799", {"start": v(-8.45, 1.55) * mm, "end": v(-8.44, 1.52) * mm});
            skLineSegment(sketch, "E2800", {"start": v(-8.44, 1.52) * mm, "end": v(-8.42, 1.49) * mm});
            skLineSegment(sketch, "E2801", {"start": v(-8.42, 1.49) * mm, "end": v(-8.4, 1.46) * mm});
            skLineSegment(sketch, "E2802", {"start": v(-8.4, 1.46) * mm, "end": v(-8.4, 1.44) * mm});
            skLineSegment(sketch, "E2803", {"start": v(-8.4, 1.44) * mm, "end": v(-8.38, 1.43) * mm});
            skLineSegment(sketch, "E2804", {"start": v(-8.38, 1.43) * mm, "end": v(-8.36, 1.42) * mm});
            skLineSegment(sketch, "E2805", {"start": v(-8.36, 1.42) * mm, "end": v(-8.33, 1.43) * mm});
            skLineSegment(sketch, "E2806", {"start": v(-8.33, 1.43) * mm, "end": v(-8.3, 1.43) * mm});
            skLineSegment(sketch, "E2807", {"start": v(-8.3, 1.43) * mm, "end": v(-8.24, 1.44) * mm});
            skLineSegment(sketch, "E2808", {"start": v(-8.24, 1.44) * mm, "end": v(-8.17, 1.46) * mm});
            skLineSegment(sketch, "E2809", {"start": v(-8.17, 1.46) * mm, "end": v(-8.08, 1.48) * mm});
            skLineSegment(sketch, "E2810", {"start": v(-3, 1.69) * mm, "end": v(-3.1, 1.82) * mm});
            skLineSegment(sketch, "E2811", {"start": v(-3.1, 1.82) * mm, "end": v(-3.16, 1.92) * mm});
            skLineSegment(sketch, "E2812", {"start": v(-3.16, 1.92) * mm, "end": v(-3.2, 2.01) * mm});
            skLineSegment(sketch, "E2813", {"start": v(-3.2, 2.01) * mm, "end": v(-3.24, 2.1) * mm});
            skLineSegment(sketch, "E2814", {"start": v(-3.24, 2.1) * mm, "end": v(-3.26, 2.24) * mm});
            skLineSegment(sketch, "E2815", {"start": v(-3.26, 2.24) * mm, "end": v(-3.25, 2.36) * mm});
            skLineSegment(sketch, "E2816", {"start": v(-3.25, 2.36) * mm, "end": v(-3.24, 2.4) * mm});
            skLineSegment(sketch, "E2817", {"start": v(-3.24, 2.4) * mm, "end": v(-3.24, 2.42) * mm});
            skLineSegment(sketch, "E2818", {"start": v(-3.24, 2.42) * mm, "end": v(-3.25, 2.42) * mm});
            skLineSegment(sketch, "E2819", {"start": v(-3.25, 2.42) * mm, "end": v(-3.28, 2.43) * mm});
            skLineSegment(sketch, "E2820", {"start": v(-3.28, 2.43) * mm, "end": v(-3.31, 2.44) * mm});
            skLineSegment(sketch, "E2821", {"start": v(-3.31, 2.44) * mm, "end": v(-3.35, 2.45) * mm});
            skLineSegment(sketch, "E2822", {"start": v(-3.35, 2.45) * mm, "end": v(-3.6, 2.5) * mm});
            skLineSegment(sketch, "E2823", {"start": v(-3.6, 2.5) * mm, "end": v(-3.82, 2.55) * mm});
            skLineSegment(sketch, "E2824", {"start": v(-3.82, 2.55) * mm, "end": v(-4.03, 2.58) * mm});
            skLineSegment(sketch, "E2825", {"start": v(-4.03, 2.58) * mm, "end": v(-4.23, 2.6) * mm});
            skLineSegment(sketch, "E2826", {"start": v(-4.23, 2.6) * mm, "end": v(-4.47, 2.6) * mm});
            skLineSegment(sketch, "E2827", {"start": v(-4.47, 2.6) * mm, "end": v(-4.74, 2.59) * mm});
            skLineSegment(sketch, "E2828", {"start": v(-4.74, 2.59) * mm, "end": v(-5, 2.56) * mm});
            skLineSegment(sketch, "E2829", {"start": v(-5, 2.56) * mm, "end": v(-5.24, 2.52) * mm});
            skLineSegment(sketch, "E2830", {"start": v(-5.24, 2.52) * mm, "end": v(-5.35, 2.5) * mm});
            skLineSegment(sketch, "E2831", {"start": v(-5.35, 2.5) * mm, "end": v(-5.47, 2.48) * mm});
            skLineSegment(sketch, "E2832", {"start": v(-5.47, 2.48) * mm, "end": v(-5.55, 2.46) * mm});
            skLineSegment(sketch, "E2833", {"start": v(-5.55, 2.46) * mm, "end": v(-5.64, 2.45) * mm});
            skLineSegment(sketch, "E2834", {"start": v(-5.64, 2.45) * mm, "end": v(-5.74, 2.43) * mm});
            skLineSegment(sketch, "E2835", {"start": v(-5.74, 2.43) * mm, "end": v(-5.83, 2.4) * mm});
            skLineSegment(sketch, "E2836", {"start": v(-5.83, 2.4) * mm, "end": v(-5.91, 2.4) * mm});
            skLineSegment(sketch, "E2837", {"start": v(-5.91, 2.4) * mm, "end": v(-5.99, 2.38) * mm});
            skLineSegment(sketch, "E2838", {"start": v(-5.99, 2.38) * mm, "end": v(-6.04, 2.36) * mm});
            skLineSegment(sketch, "E2839", {"start": v(-6.04, 2.36) * mm, "end": v(-6.07, 2.36) * mm});
            skLineSegment(sketch, "E2840", {"start": v(-6.07, 2.36) * mm, "end": v(-6.1, 2.34) * mm});
            skLineSegment(sketch, "E2841", {"start": v(-6.1, 2.34) * mm, "end": v(-6.17, 2.33) * mm});
            skLineSegment(sketch, "E2842", {"start": v(-6.17, 2.33) * mm, "end": v(-6.25, 2.31) * mm});
            skLineSegment(sketch, "E2843", {"start": v(-6.25, 2.31) * mm, "end": v(-6.34, 2.3) * mm});
            skLineSegment(sketch, "E2844", {"start": v(-6.34, 2.3) * mm, "end": v(-6.43, 2.27) * mm});
            skLineSegment(sketch, "E2845", {"start": v(-6.43, 2.27) * mm, "end": v(-6.52, 2.25) * mm});
            skLineSegment(sketch, "E2846", {"start": v(-6.52, 2.25) * mm, "end": v(-6.6, 2.24) * mm});
            skLineSegment(sketch, "E2847", {"start": v(-6.6, 2.24) * mm, "end": v(-6.66, 2.23) * mm});
            skLineSegment(sketch, "E2848", {"start": v(-6.66, 2.23) * mm, "end": v(-6.7, 2.22) * mm});
            skLineSegment(sketch, "E2849", {"start": v(-6.7, 2.22) * mm, "end": v(-6.72, 2.2) * mm});
            skLineSegment(sketch, "E2850", {"start": v(-6.72, 2.2) * mm, "end": v(-6.7, 2.2) * mm});
            skLineSegment(sketch, "E2851", {"start": v(-6.7, 2.2) * mm, "end": v(-6.7, 2.18) * mm});
            skLineSegment(sketch, "E2852", {"start": v(-6.7, 2.18) * mm, "end": v(-6.67, 2.16) * mm});
            skLineSegment(sketch, "E2853", {"start": v(-6.67, 2.16) * mm, "end": v(-6.65, 2.14) * mm});
            skLineSegment(sketch, "E2854", {"start": v(-6.65, 2.14) * mm, "end": v(-6.61, 2.12) * mm});
            skLineSegment(sketch, "E2855", {"start": v(-6.61, 2.12) * mm, "end": v(-6.58, 2.1) * mm});
            skLineSegment(sketch, "E2856", {"start": v(-6.58, 2.1) * mm, "end": v(-6.54, 2.08) * mm});
            skLineSegment(sketch, "E2857", {"start": v(-6.54, 2.08) * mm, "end": v(-6.5, 2.06) * mm});
            skLineSegment(sketch, "E2858", {"start": v(-6.5, 2.06) * mm, "end": v(-6.47, 2.04) * mm});
            skLineSegment(sketch, "E2859", {"start": v(-6.47, 2.04) * mm, "end": v(-6.43, 2.02) * mm});
            skLineSegment(sketch, "E2860", {"start": v(-6.43, 2.02) * mm, "end": v(-6.39, 2) * mm});
            skLineSegment(sketch, "E2861", {"start": v(-6.39, 2) * mm, "end": v(-6.35, 1.99) * mm});
            skLineSegment(sketch, "E2862", {"start": v(-6.35, 1.99) * mm, "end": v(-6.3, 1.97) * mm});
            skLineSegment(sketch, "E2863", {"start": v(-6.3, 1.97) * mm, "end": v(-6.24, 1.95) * mm});
            skLineSegment(sketch, "E2864", {"start": v(-6.24, 1.95) * mm, "end": v(-6.17, 1.93) * mm});
            skLineSegment(sketch, "E2865", {"start": v(-6.17, 1.93) * mm, "end": v(-6.1, 1.9) * mm});
            skLineSegment(sketch, "E2866", {"start": v(-6.1, 1.9) * mm, "end": v(-5.95, 1.85) * mm});
            skLineSegment(sketch, "E2867", {"start": v(-5.95, 1.85) * mm, "end": v(-5.79, 1.8) * mm});
            skLineSegment(sketch, "E2868", {"start": v(-5.79, 1.8) * mm, "end": v(-5.64, 1.78) * mm});
            skLineSegment(sketch, "E2869", {"start": v(-5.64, 1.78) * mm, "end": v(-5.53, 1.77) * mm});
            skLineSegment(sketch, "E2870", {"start": v(-5.53, 1.77) * mm, "end": v(-5.5, 1.77) * mm});
            skLineSegment(sketch, "E2871", {"start": v(-5.5, 1.77) * mm, "end": v(-5.44, 1.77) * mm});
            skLineSegment(sketch, "E2872", {"start": v(-5.44, 1.77) * mm, "end": v(-5.37, 1.78) * mm});
            skLineSegment(sketch, "E2873", {"start": v(-5.37, 1.78) * mm, "end": v(-5.31, 1.8) * mm});
            skLineSegment(sketch, "E2874", {"start": v(-5.31, 1.8) * mm, "end": v(-5.2, 1.8) * mm});
            skLineSegment(sketch, "E2875", {"start": v(-5.2, 1.8) * mm, "end": v(-5.1, 1.81) * mm});
            skLineSegment(sketch, "E2876", {"start": v(-5.1, 1.81) * mm, "end": v(-4.97, 1.82) * mm});
            skLineSegment(sketch, "E2877", {"start": v(-4.97, 1.82) * mm, "end": v(-4.85, 1.82) * mm});
            skLineSegment(sketch, "E2878", {"start": v(-4.85, 1.82) * mm, "end": v(-4.74, 1.81) * mm});
            skLineSegment(sketch, "E2879", {"start": v(-4.74, 1.81) * mm, "end": v(-4.63, 1.8) * mm});
            skLineSegment(sketch, "E2880", {"start": v(-4.63, 1.8) * mm, "end": v(-4.54, 1.79) * mm});
            skLineSegment(sketch, "E2881", {"start": v(-4.54, 1.79) * mm, "end": v(-4.48, 1.77) * mm});
            skLineSegment(sketch, "E2882", {"start": v(-4.48, 1.77) * mm, "end": v(-4.44, 1.76) * mm});
            skLineSegment(sketch, "E2883", {"start": v(-4.44, 1.76) * mm, "end": v(-4.38, 1.76) * mm});
            skLineSegment(sketch, "E2884", {"start": v(-4.38, 1.76) * mm, "end": v(-4.3, 1.76) * mm});
            skLineSegment(sketch, "E2885", {"start": v(-4.3, 1.76) * mm, "end": v(-4.16, 1.76) * mm});
            skLineSegment(sketch, "E2886", {"start": v(-4.16, 1.76) * mm, "end": v(-3.93, 1.75) * mm});
            skLineSegment(sketch, "E2887", {"start": v(-3.93, 1.75) * mm, "end": v(-3.76, 1.74) * mm});
            skLineSegment(sketch, "E2888", {"start": v(-3.76, 1.74) * mm, "end": v(-3.56, 1.71) * mm});
            skLineSegment(sketch, "E2889", {"start": v(-3.56, 1.71) * mm, "end": v(-3.35, 1.68) * mm});
            skLineSegment(sketch, "E2890", {"start": v(-3.35, 1.68) * mm, "end": v(-3.17, 1.64) * mm});
            skLineSegment(sketch, "E2891", {"start": v(-3.17, 1.64) * mm, "end": v(-3.05, 1.61) * mm});
            skLineSegment(sketch, "E2892", {"start": v(-3.05, 1.61) * mm, "end": v(-3, 1.6) * mm});
            skLineSegment(sketch, "E2893", {"start": v(-3, 1.6) * mm, "end": v(-2.97, 1.6) * mm});
            skLineSegment(sketch, "E2894", {"start": v(-2.97, 1.6) * mm, "end": v(-2.95, 1.59) * mm});
            skLineSegment(sketch, "E2895", {"start": v(-2.95, 1.59) * mm, "end": v(-2.94, 1.6) * mm});
            skLineSegment(sketch, "E2896", {"start": v(-2.94, 1.6) * mm, "end": v(-2.94, 1.6) * mm});
            skLineSegment(sketch, "E2897", {"start": v(-2.94, 1.6) * mm, "end": v(-2.96, 1.62) * mm});
            skLineSegment(sketch, "E2898", {"start": v(-2.96, 1.62) * mm, "end": v(-2.98, 1.65) * mm});
            skLineSegment(sketch, "E2899", {"start": v(-2.98, 1.65) * mm, "end": v(-3, 1.69) * mm});
            skLineSegment(sketch, "E2900", {"start": v(-5.75, 1.68) * mm, "end": v(-5.75, 1.69) * mm});
            skLineSegment(sketch, "E2901", {"start": v(-5.75, 1.69) * mm, "end": v(-5.77, 1.68) * mm});
            skLineSegment(sketch, "E2902", {"start": v(-5.77, 1.68) * mm, "end": v(-5.77, 1.67) * mm});
            skLineSegment(sketch, "E2903", {"start": v(-5.77, 1.67) * mm, "end": v(-5.76, 1.67) * mm});
            skLineSegment(sketch, "E2904", {"start": v(-5.76, 1.67) * mm, "end": v(-5.75, 1.67) * mm});
            skLineSegment(sketch, "E2905", {"start": v(-5.75, 1.67) * mm, "end": v(-5.75, 1.68) * mm});
            skLineSegment(sketch, "E2906", {"start": v(-0.47, 1.69) * mm, "end": v(-0.42, 1.7) * mm});
            skLineSegment(sketch, "E2907", {"start": v(-0.42, 1.7) * mm, "end": v(-0.37, 1.74) * mm});
            skLineSegment(sketch, "E2908", {"start": v(-0.37, 1.74) * mm, "end": v(-0.34, 1.79) * mm});
            skLineSegment(sketch, "E2909", {"start": v(-0.34, 1.79) * mm, "end": v(-0.32, 1.83) * mm});
            skLineSegment(sketch, "E2910", {"start": v(-0.32, 1.83) * mm, "end": v(-0.32, 1.85) * mm});
            skLineSegment(sketch, "E2911", {"start": v(-0.32, 1.85) * mm, "end": v(-0.33, 1.88) * mm});
            skLineSegment(sketch, "E2912", {"start": v(-0.33, 1.88) * mm, "end": v(-0.35, 1.9) * mm});
            skLineSegment(sketch, "E2913", {"start": v(-0.35, 1.9) * mm, "end": v(-0.37, 1.9) * mm});
            skLineSegment(sketch, "E2914", {"start": v(-0.37, 1.9) * mm, "end": v(-0.4, 1.89) * mm});
            skLineSegment(sketch, "E2915", {"start": v(-0.4, 1.89) * mm, "end": v(-0.42, 1.86) * mm});
            skLineSegment(sketch, "E2916", {"start": v(-0.42, 1.86) * mm, "end": v(-0.48, 1.82) * mm});
            skLineSegment(sketch, "E2917", {"start": v(-0.48, 1.82) * mm, "end": v(-0.54, 1.82) * mm});
            skLineSegment(sketch, "E2918", {"start": v(-0.54, 1.82) * mm, "end": v(-0.6, 1.85) * mm});
            skLineSegment(sketch, "E2919", {"start": v(-0.6, 1.85) * mm, "end": v(-0.66, 1.92) * mm});
            skLineSegment(sketch, "E2920", {"start": v(-0.66, 1.92) * mm, "end": v(-0.72, 2.05) * mm});
            skLineSegment(sketch, "E2921", {"start": v(-0.72, 2.05) * mm, "end": v(-0.76, 2.2) * mm});
            skLineSegment(sketch, "E2922", {"start": v(-0.76, 2.2) * mm, "end": v(-0.76, 2.35) * mm});
            skLineSegment(sketch, "E2923", {"start": v(-0.76, 2.35) * mm, "end": v(-0.73, 2.5) * mm});
            skLineSegment(sketch, "E2924", {"start": v(-0.73, 2.5) * mm, "end": v(-0.72, 2.53) * mm});
            skLineSegment(sketch, "E2925", {"start": v(-0.72, 2.53) * mm, "end": v(-0.7, 2.57) * mm});
            skLineSegment(sketch, "E2926", {"start": v(-0.7, 2.57) * mm, "end": v(-0.69, 2.61) * mm});
            skLineSegment(sketch, "E2927", {"start": v(-0.69, 2.61) * mm, "end": v(-0.67, 2.64) * mm});
            skLineSegment(sketch, "E2928", {"start": v(-0.67, 2.64) * mm, "end": v(-0.62, 2.71) * mm});
            skLineSegment(sketch, "E2929", {"start": v(-0.62, 2.71) * mm, "end": v(-0.56, 2.78) * mm});
            skLineSegment(sketch, "E2930", {"start": v(-0.56, 2.78) * mm, "end": v(-0.48, 2.85) * mm});
            skLineSegment(sketch, "E2931", {"start": v(-0.48, 2.85) * mm, "end": v(-0.4, 2.91) * mm});
            skLineSegment(sketch, "E2932", {"start": v(-0.4, 2.91) * mm, "end": v(-0.33, 2.96) * mm});
            skLineSegment(sketch, "E2933", {"start": v(-0.33, 2.96) * mm, "end": v(-0.25, 2.98) * mm});
            skLineSegment(sketch, "E2934", {"start": v(-0.25, 2.98) * mm, "end": v(-0.18, 2.99) * mm});
            skLineSegment(sketch, "E2935", {"start": v(-0.18, 2.99) * mm, "end": v(-0.11, 2.97) * mm});
            skLineSegment(sketch, "E2936", {"start": v(-0.11, 2.97) * mm, "end": v(-0.06, 2.95) * mm});
            skLineSegment(sketch, "E2937", {"start": v(-0.06, 2.95) * mm, "end": v(0, 2.92) * mm});
            skLineSegment(sketch, "E2938", {"start": v(0, 2.92) * mm, "end": v(0.04, 2.87) * mm});
            skLineSegment(sketch, "E2939", {"start": v(0.04, 2.87) * mm, "end": v(0.07, 2.83) * mm});
            skLineSegment(sketch, "E2940", {"start": v(0.07, 2.83) * mm, "end": v(0.1, 2.78) * mm});
            skLineSegment(sketch, "E2941", {"start": v(0.1, 2.78) * mm, "end": v(0.1, 2.73) * mm});
            skLineSegment(sketch, "E2942", {"start": v(0.1, 2.73) * mm, "end": v(0.1, 2.68) * mm});
            skLineSegment(sketch, "E2943", {"start": v(0.1, 2.68) * mm, "end": v(0.08, 2.64) * mm});
            skLineSegment(sketch, "E2944", {"start": v(0.08, 2.64) * mm, "end": v(0.06, 2.62) * mm});
            skLineSegment(sketch, "E2945", {"start": v(0.06, 2.62) * mm, "end": v(0.04, 2.6) * mm});
            skLineSegment(sketch, "E2946", {"start": v(0.04, 2.6) * mm, "end": v(0.01, 2.58) * mm});
            skLineSegment(sketch, "E2947", {"start": v(0.01, 2.58) * mm, "end": v(-0.02, 2.57) * mm});
            skLineSegment(sketch, "E2948", {"start": v(-0.02, 2.57) * mm, "end": v(-0.1, 2.5) * mm});
            skLineSegment(sketch, "E2949", {"start": v(-0.1, 2.5) * mm, "end": v(-0.16, 2.4) * mm});
            skLineSegment(sketch, "E2950", {"start": v(-0.16, 2.4) * mm, "end": v(-0.18, 2.3) * mm});
            skLineSegment(sketch, "E2951", {"start": v(-0.18, 2.3) * mm, "end": v(-0.16, 2.21) * mm});
            skLineSegment(sketch, "E2952", {"start": v(-0.16, 2.21) * mm, "end": v(-0.12, 2.16) * mm});
            skLineSegment(sketch, "E2953", {"start": v(-0.12, 2.16) * mm, "end": v(-0.06, 2.14) * mm});
            skLineSegment(sketch, "E2954", {"start": v(-0.06, 2.14) * mm, "end": v(0.02, 2.14) * mm});
            skLineSegment(sketch, "E2955", {"start": v(0.02, 2.14) * mm, "end": v(0.1, 2.16) * mm});
            skLineSegment(sketch, "E2956", {"start": v(0.1, 2.16) * mm, "end": v(0.15, 2.2) * mm});
            skLineSegment(sketch, "E2957", {"start": v(0.15, 2.2) * mm, "end": v(0.2, 2.26) * mm});
            skLineSegment(sketch, "E2958", {"start": v(0.2, 2.26) * mm, "end": v(0.23, 2.35) * mm});
            skLineSegment(sketch, "E2959", {"start": v(0.23, 2.35) * mm, "end": v(0.26, 2.46) * mm});
            skLineSegment(sketch, "E2960", {"start": v(0.26, 2.46) * mm, "end": v(0.28, 2.55) * mm});
            skLineSegment(sketch, "E2961", {"start": v(0.28, 2.55) * mm, "end": v(0.28, 2.62) * mm});
            skLineSegment(sketch, "E2962", {"start": v(0.28, 2.62) * mm, "end": v(0.28, 2.68) * mm});
            skLineSegment(sketch, "E2963", {"start": v(0.28, 2.68) * mm, "end": v(0.27, 2.74) * mm});
            skLineSegment(sketch, "E2964", {"start": v(0.27, 2.74) * mm, "end": v(0.25, 2.8) * mm});
            skLineSegment(sketch, "E2965", {"start": v(0.25, 2.8) * mm, "end": v(0.21, 2.86) * mm});
            skLineSegment(sketch, "E2966", {"start": v(0.21, 2.86) * mm, "end": v(0.17, 2.93) * mm});
            skLineSegment(sketch, "E2967", {"start": v(0.17, 2.93) * mm, "end": v(0.12, 3) * mm});
            skLineSegment(sketch, "E2968", {"start": v(0.12, 3) * mm, "end": v(0.07, 3.06) * mm});
            skLineSegment(sketch, "E2969", {"start": v(0.07, 3.06) * mm, "end": v(0.02, 3.1) * mm});
            skLineSegment(sketch, "E2970", {"start": v(0.02, 3.1) * mm, "end": v(-0.04, 3.15) * mm});
            skLineSegment(sketch, "E2971", {"start": v(-0.04, 3.15) * mm, "end": v(-0.08, 3.17) * mm});
            skLineSegment(sketch, "E2972", {"start": v(-0.08, 3.17) * mm, "end": v(-0.2, 3.19) * mm});
            skLineSegment(sketch, "E2973", {"start": v(-0.2, 3.19) * mm, "end": v(-0.34, 3.18) * mm});
            skLineSegment(sketch, "E2974", {"start": v(-0.34, 3.18) * mm, "end": v(-0.42, 3.16) * mm});
            skLineSegment(sketch, "E2975", {"start": v(-0.42, 3.16) * mm, "end": v(-0.5, 3.12) * mm});
            skLineSegment(sketch, "E2976", {"start": v(-0.5, 3.12) * mm, "end": v(-0.6, 3.07) * mm});
            skLineSegment(sketch, "E2977", {"start": v(-0.6, 3.07) * mm, "end": v(-0.68, 3.01) * mm});
            skLineSegment(sketch, "E2978", {"start": v(-0.68, 3.01) * mm, "end": v(-0.76, 2.93) * mm});
            skLineSegment(sketch, "E2979", {"start": v(-0.76, 2.93) * mm, "end": v(-0.83, 2.83) * mm});
            skLineSegment(sketch, "E2980", {"start": v(-0.83, 2.83) * mm, "end": v(-0.9, 2.7) * mm});
            skLineSegment(sketch, "E2981", {"start": v(-0.9, 2.7) * mm, "end": v(-0.94, 2.53) * mm});
            skLineSegment(sketch, "E2982", {"start": v(-0.94, 2.53) * mm, "end": v(-0.96, 2.47) * mm});
            skLineSegment(sketch, "E2983", {"start": v(-0.96, 2.47) * mm, "end": v(-0.97, 2.4) * mm});
            skLineSegment(sketch, "E2984", {"start": v(-0.97, 2.4) * mm, "end": v(-0.97, 2.35) * mm});
            skLineSegment(sketch, "E2985", {"start": v(-0.97, 2.35) * mm, "end": v(-0.98, 2.26) * mm});
            skLineSegment(sketch, "E2986", {"start": v(-0.98, 2.26) * mm, "end": v(-0.98, 2.18) * mm});
            skLineSegment(sketch, "E2987", {"start": v(-0.98, 2.18) * mm, "end": v(-0.97, 2.12) * mm});
            skLineSegment(sketch, "E2988", {"start": v(-0.97, 2.12) * mm, "end": v(-0.96, 2.09) * mm});
            skLineSegment(sketch, "E2989", {"start": v(-0.96, 2.09) * mm, "end": v(-0.95, 2.06) * mm});
            skLineSegment(sketch, "E2990", {"start": v(-0.95, 2.06) * mm, "end": v(-0.93, 2) * mm});
            skLineSegment(sketch, "E2991", {"start": v(-0.93, 2) * mm, "end": v(-0.9, 1.96) * mm});
            skLineSegment(sketch, "E2992", {"start": v(-0.9, 1.96) * mm, "end": v(-0.86, 1.86) * mm});
            skLineSegment(sketch, "E2993", {"start": v(-0.86, 1.86) * mm, "end": v(-0.8, 1.78) * mm});
            skLineSegment(sketch, "E2994", {"start": v(-0.8, 1.78) * mm, "end": v(-0.7, 1.72) * mm});
            skLineSegment(sketch, "E2995", {"start": v(-0.7, 1.72) * mm, "end": v(-0.6, 1.68) * mm});
            skLineSegment(sketch, "E2996", {"start": v(-0.6, 1.68) * mm, "end": v(-0.57, 1.67) * mm});
            skLineSegment(sketch, "E2997", {"start": v(-0.57, 1.67) * mm, "end": v(-0.53, 1.67) * mm});
            skLineSegment(sketch, "E2998", {"start": v(-0.53, 1.67) * mm, "end": v(-0.5, 1.67) * mm});
            skLineSegment(sketch, "E2999", {"start": v(-0.5, 1.67) * mm, "end": v(-0.47, 1.69) * mm});
            skLineSegment(sketch, "E3000", {"start": v(5.43, 1.8) * mm, "end": v(5.63, 1.83) * mm});
            skLineSegment(sketch, "E3001", {"start": v(5.63, 1.83) * mm, "end": v(5.8, 1.88) * mm});
            skLineSegment(sketch, "E3002", {"start": v(5.8, 1.88) * mm, "end": v(5.95, 1.94) * mm});
            skLineSegment(sketch, "E3003", {"start": v(5.95, 1.94) * mm, "end": v(6.13, 2.02) * mm});
            skLineSegment(sketch, "E3004", {"start": v(6.13, 2.02) * mm, "end": v(6.49, 2.17) * mm});
            skLineSegment(sketch, "E3005", {"start": v(6.49, 2.17) * mm, "end": v(6.82, 2.26) * mm});
            skLineSegment(sketch, "E3006", {"start": v(6.82, 2.26) * mm, "end": v(7.12, 2.29) * mm});
            skLineSegment(sketch, "E3007", {"start": v(7.12, 2.29) * mm, "end": v(7.4, 2.26) * mm});
            skLineSegment(sketch, "E3008", {"start": v(7.4, 2.26) * mm, "end": v(7.42, 2.26) * mm});
            skLineSegment(sketch, "E3009", {"start": v(7.42, 2.26) * mm, "end": v(7.44, 2.27) * mm});
            skLineSegment(sketch, "E3010", {"start": v(7.44, 2.27) * mm, "end": v(7.46, 2.3) * mm});
            skLineSegment(sketch, "E3011", {"start": v(7.46, 2.3) * mm, "end": v(7.5, 2.36) * mm});
            skLineSegment(sketch, "E3012", {"start": v(7.5, 2.36) * mm, "end": v(7.53, 2.41) * mm});
            skLineSegment(sketch, "E3013", {"start": v(7.53, 2.41) * mm, "end": v(7.55, 2.47) * mm});
            skLineSegment(sketch, "E3014", {"start": v(7.55, 2.47) * mm, "end": v(7.58, 2.52) * mm});
            skLineSegment(sketch, "E3015", {"start": v(7.58, 2.52) * mm, "end": v(7.6, 2.57) * mm});
            skLineSegment(sketch, "E3016", {"start": v(7.6, 2.57) * mm, "end": v(7.63, 2.61) * mm});
            skLineSegment(sketch, "E3017", {"start": v(7.63, 2.61) * mm, "end": v(7.65, 2.66) * mm});
            skLineSegment(sketch, "E3018", {"start": v(7.65, 2.66) * mm, "end": v(7.67, 2.7) * mm});
            skLineSegment(sketch, "E3019", {"start": v(7.67, 2.7) * mm, "end": v(7.69, 2.73) * mm});
            skLineSegment(sketch, "E3020", {"start": v(7.69, 2.73) * mm, "end": v(7.72, 2.79) * mm});
            skLineSegment(sketch, "E3021", {"start": v(7.72, 2.79) * mm, "end": v(7.75, 2.85) * mm});
            skLineSegment(sketch, "E3022", {"start": v(7.75, 2.85) * mm, "end": v(7.76, 2.9) * mm});
            skLineSegment(sketch, "E3023", {"start": v(7.76, 2.9) * mm, "end": v(7.77, 2.92) * mm});
            skLineSegment(sketch, "E3024", {"start": v(7.77, 2.92) * mm, "end": v(7.75, 2.93) * mm});
            skLineSegment(sketch, "E3025", {"start": v(7.75, 2.93) * mm, "end": v(7.72, 2.93) * mm});
            skLineSegment(sketch, "E3026", {"start": v(7.72, 2.93) * mm, "end": v(7.67, 2.93) * mm});
            skLineSegment(sketch, "E3027", {"start": v(7.67, 2.93) * mm, "end": v(7.59, 2.93) * mm});
            skLineSegment(sketch, "E3028", {"start": v(7.59, 2.93) * mm, "end": v(7.3, 2.92) * mm});
            skLineSegment(sketch, "E3029", {"start": v(7.3, 2.92) * mm, "end": v(7.03, 2.88) * mm});
            skLineSegment(sketch, "E3030", {"start": v(7.03, 2.88) * mm, "end": v(6.79, 2.82) * mm});
            skLineSegment(sketch, "E3031", {"start": v(6.79, 2.82) * mm, "end": v(6.57, 2.73) * mm});
            skLineSegment(sketch, "E3032", {"start": v(6.57, 2.73) * mm, "end": v(6.5, 2.7) * mm});
            skLineSegment(sketch, "E3033", {"start": v(6.5, 2.7) * mm, "end": v(6.43, 2.65) * mm});
            skLineSegment(sketch, "E3034", {"start": v(6.43, 2.65) * mm, "end": v(6.34, 2.59) * mm});
            skLineSegment(sketch, "E3035", {"start": v(6.34, 2.59) * mm, "end": v(6.25, 2.53) * mm});
            skLineSegment(sketch, "E3036", {"start": v(6.25, 2.53) * mm, "end": v(6.15, 2.46) * mm});
            skLineSegment(sketch, "E3037", {"start": v(6.15, 2.46) * mm, "end": v(6.07, 2.4) * mm});
            skLineSegment(sketch, "E3038", {"start": v(6.07, 2.4) * mm, "end": v(6, 2.35) * mm});
            skLineSegment(sketch, "E3039", {"start": v(6, 2.35) * mm, "end": v(5.95, 2.3) * mm});
            skLineSegment(sketch, "E3040", {"start": v(5.95, 2.3) * mm, "end": v(5.9, 2.26) * mm});
            skLineSegment(sketch, "E3041", {"start": v(5.9, 2.26) * mm, "end": v(5.84, 2.21) * mm});
            skLineSegment(sketch, "E3042", {"start": v(5.84, 2.21) * mm, "end": v(5.78, 2.16) * mm});
            skLineSegment(sketch, "E3043", {"start": v(5.78, 2.16) * mm, "end": v(5.73, 2.1) * mm});
            skLineSegment(sketch, "E3044", {"start": v(5.73, 2.1) * mm, "end": v(5.64, 2.02) * mm});
            skLineSegment(sketch, "E3045", {"start": v(5.64, 2.02) * mm, "end": v(5.56, 1.96) * mm});
            skLineSegment(sketch, "E3046", {"start": v(5.56, 1.96) * mm, "end": v(5.48, 1.9) * mm});
            skLineSegment(sketch, "E3047", {"start": v(5.48, 1.9) * mm, "end": v(5.4, 1.85) * mm});
            skLineSegment(sketch, "E3048", {"start": v(5.4, 1.85) * mm, "end": v(5.35, 1.83) * mm});
            skLineSegment(sketch, "E3049", {"start": v(5.35, 1.83) * mm, "end": v(5.32, 1.81) * mm});
            skLineSegment(sketch, "E3050", {"start": v(5.32, 1.81) * mm, "end": v(5.3, 1.8) * mm});
            skLineSegment(sketch, "E3051", {"start": v(5.3, 1.8) * mm, "end": v(5.29, 1.79) * mm});
            skLineSegment(sketch, "E3052", {"start": v(5.29, 1.79) * mm, "end": v(5.3, 1.78) * mm});
            skLineSegment(sketch, "E3053", {"start": v(5.3, 1.78) * mm, "end": v(5.32, 1.78) * mm});
            skLineSegment(sketch, "E3054", {"start": v(5.32, 1.78) * mm, "end": v(5.36, 1.78) * mm});
            skLineSegment(sketch, "E3055", {"start": v(5.36, 1.78) * mm, "end": v(5.43, 1.8) * mm});
            skLineSegment(sketch, "E3056", {"start": v(-7.03, 2.29) * mm, "end": v(-7.06, 2.29) * mm});
            skLineSegment(sketch, "E3057", {"start": v(-7.06, 2.29) * mm, "end": v(-7.08, 2.29) * mm});
            skLineSegment(sketch, "E3058", {"start": v(-7.08, 2.29) * mm, "end": v(-7.09, 2.28) * mm});
            skLineSegment(sketch, "E3059", {"start": v(-7.09, 2.28) * mm, "end": v(-7.06, 2.28) * mm});
            skLineSegment(sketch, "E3060", {"start": v(-7.06, 2.28) * mm, "end": v(-7.03, 2.28) * mm});
            skLineSegment(sketch, "E3061", {"start": v(-7.03, 2.28) * mm, "end": v(-7.03, 2.29) * mm});
            skLineSegment(sketch, "E3062", {"start": v(0.3, 2.38) * mm, "end": v(0.32, 2.41) * mm});
            skLineSegment(sketch, "E3063", {"start": v(0.32, 2.41) * mm, "end": v(0.34, 2.44) * mm});
            skLineSegment(sketch, "E3064", {"start": v(0.34, 2.44) * mm, "end": v(0.35, 2.46) * mm});
            skLineSegment(sketch, "E3065", {"start": v(0.35, 2.46) * mm, "end": v(0.35, 2.48) * mm});
            skLineSegment(sketch, "E3066", {"start": v(0.35, 2.48) * mm, "end": v(0.35, 2.48) * mm});
            skLineSegment(sketch, "E3067", {"start": v(0.35, 2.48) * mm, "end": v(0.34, 2.46) * mm});
            skLineSegment(sketch, "E3068", {"start": v(0.34, 2.46) * mm, "end": v(0.32, 2.44) * mm});
            skLineSegment(sketch, "E3069", {"start": v(0.32, 2.44) * mm, "end": v(0.3, 2.4) * mm});
            skLineSegment(sketch, "E3070", {"start": v(0.3, 2.4) * mm, "end": v(0.28, 2.37) * mm});
            skLineSegment(sketch, "E3071", {"start": v(0.28, 2.37) * mm, "end": v(0.27, 2.33) * mm});
            skLineSegment(sketch, "E3072", {"start": v(0.27, 2.33) * mm, "end": v(0.26, 2.31) * mm});
            skLineSegment(sketch, "E3073", {"start": v(0.26, 2.31) * mm, "end": v(0.25, 2.3) * mm});
            skLineSegment(sketch, "E3074", {"start": v(0.25, 2.3) * mm, "end": v(0.25, 2.3) * mm});
            skLineSegment(sketch, "E3075", {"start": v(0.25, 2.3) * mm, "end": v(0.26, 2.3) * mm});
            skLineSegment(sketch, "E3076", {"start": v(0.26, 2.3) * mm, "end": v(0.28, 2.33) * mm});
            skLineSegment(sketch, "E3077", {"start": v(0.28, 2.33) * mm, "end": v(0.3, 2.38) * mm});
            skLineSegment(sketch, "E3078", {"start": v(-7.96, 2.54) * mm, "end": v(-7.97, 2.55) * mm});
            skLineSegment(sketch, "E3079", {"start": v(-7.97, 2.55) * mm, "end": v(-7.99, 2.56) * mm});
            skLineSegment(sketch, "E3080", {"start": v(-7.99, 2.56) * mm, "end": v(-8, 2.55) * mm});
            skLineSegment(sketch, "E3081", {"start": v(-8, 2.55) * mm, "end": v(-7.98, 2.54) * mm});
            skLineSegment(sketch, "E3082", {"start": v(-7.98, 2.54) * mm, "end": v(-7.97, 2.54) * mm});
            skLineSegment(sketch, "E3083", {"start": v(-7.97, 2.54) * mm, "end": v(-7.95, 2.53) * mm});
            skLineSegment(sketch, "E3084", {"start": v(-7.95, 2.53) * mm, "end": v(-7.95, 2.54) * mm});
            skLineSegment(sketch, "E3085", {"start": v(-7.95, 2.54) * mm, "end": v(-7.96, 2.54) * mm});
            skLineSegment(sketch, "E3086", {"start": v(0.46, 3.03) * mm, "end": v(0.46, 3.04) * mm});
            skLineSegment(sketch, "E3087", {"start": v(0.46, 3.04) * mm, "end": v(0.45, 3.04) * mm});
            skLineSegment(sketch, "E3088", {"start": v(0.45, 3.04) * mm, "end": v(0.45, 3.03) * mm});
            skLineSegment(sketch, "E3089", {"start": v(0.45, 3.03) * mm, "end": v(0.46, 3.02) * mm});
            skLineSegment(sketch, "E3090", {"start": v(0.46, 3.02) * mm, "end": v(0.46, 3) * mm});
            skLineSegment(sketch, "E3091", {"start": v(0.46, 3) * mm, "end": v(0.47, 3) * mm});
            skLineSegment(sketch, "E3092", {"start": v(0.47, 3) * mm, "end": v(0.47, 3.01) * mm});
            skLineSegment(sketch, "E3093", {"start": v(0.47, 3.01) * mm, "end": v(0.46, 3.03) * mm});
            skLineSegment(sketch, "E3094", {"start": v(-0.76, 3.09) * mm, "end": v(-0.75, 3.1) * mm});
            skLineSegment(sketch, "E3095", {"start": v(-0.75, 3.1) * mm, "end": v(-0.76, 3.1) * mm});
            skLineSegment(sketch, "E3096", {"start": v(-0.76, 3.1) * mm, "end": v(-0.78, 3.08) * mm});
            skLineSegment(sketch, "E3097", {"start": v(-0.78, 3.08) * mm, "end": v(-0.78, 3.07) * mm});
            skLineSegment(sketch, "E3098", {"start": v(-0.78, 3.07) * mm, "end": v(-0.78, 3.07) * mm});
            skLineSegment(sketch, "E3099", {"start": v(-0.78, 3.07) * mm, "end": v(-0.76, 3.09) * mm});
            skSolve(sketch);
        }
        {
            var Q0;
            Q0=makeQuery(id+"F0.imprint","IMPRINT",FACE,{"disambiguationData":[TD([[makeQuery(id+"F0.imprint","IMPRINT",EDGE,{"derivedFrom":sQuery(id+"F0.wireOp",EDGE,"E0")}),-1.0]])]});
            extrude(context, id + "F1", {"entities" : qUnion([Q0]), "depth" : 2 * mm});
        }
        {
            var Q0;
            Q0=makeQuery(id+"F0.imprint","IMPRINT",FACE,{"disambiguationData":[TD([[makeQuery(id+"F0.imprint","IMPRINT",EDGE,{"derivedFrom":sQuery(id+"F0.wireOp",EDGE,"E2740")}),1.0]])]});
            var Q1;
            Q1=makeQuery(id+"F0.imprint","IMPRINT",FACE,{"disambiguationData":[TD([[makeQuery(id+"F0.imprint","IMPRINT",EDGE,{"derivedFrom":sQuery(id+"F0.wireOp",EDGE,"E2488")}),1.0]])]});
            var Q2;
            Q2=makeQuery(id+"F0.imprint","IMPRINT",FACE,{"disambiguationData":[TD([[makeQuery(id+"F0.imprint","IMPRINT",EDGE,{"derivedFrom":sQuery(id+"F0.wireOp",EDGE,"E2216")}),1.0]])]});
            var Q3;
            Q3=makeQuery(id+"F0.imprint","IMPRINT",FACE,{"disambiguationData":[TD([[makeQuery(id+"F0.imprint","IMPRINT",EDGE,{"derivedFrom":sQuery(id+"F0.wireOp",EDGE,"E2810")}),1.0]])]});
            var Q4;
            Q4=makeQuery(id+"F0.imprint","IMPRINT",FACE,{"disambiguationData":[TD([[makeQuery(id+"F0.imprint","IMPRINT",EDGE,{"derivedFrom":sQuery(id+"F0.wireOp",EDGE,"E2376")}),1.0]])]});
            var Q5;
            Q5=makeQuery(id+"F0.imprint","IMPRINT",FACE,{"disambiguationData":[TD([[makeQuery(id+"F0.imprint","IMPRINT",EDGE,{"derivedFrom":sQuery(id+"F0.wireOp",EDGE,"E2548")}),1.0]])]});
            extrude(context, id + "F2", {"entities" : qUnion([Q0, Q1, Q2, Q3, Q4, Q5]), "operationType" : NewBodyOperationType.ADD, "depth" : 2.5 * mm});
        }
    });
